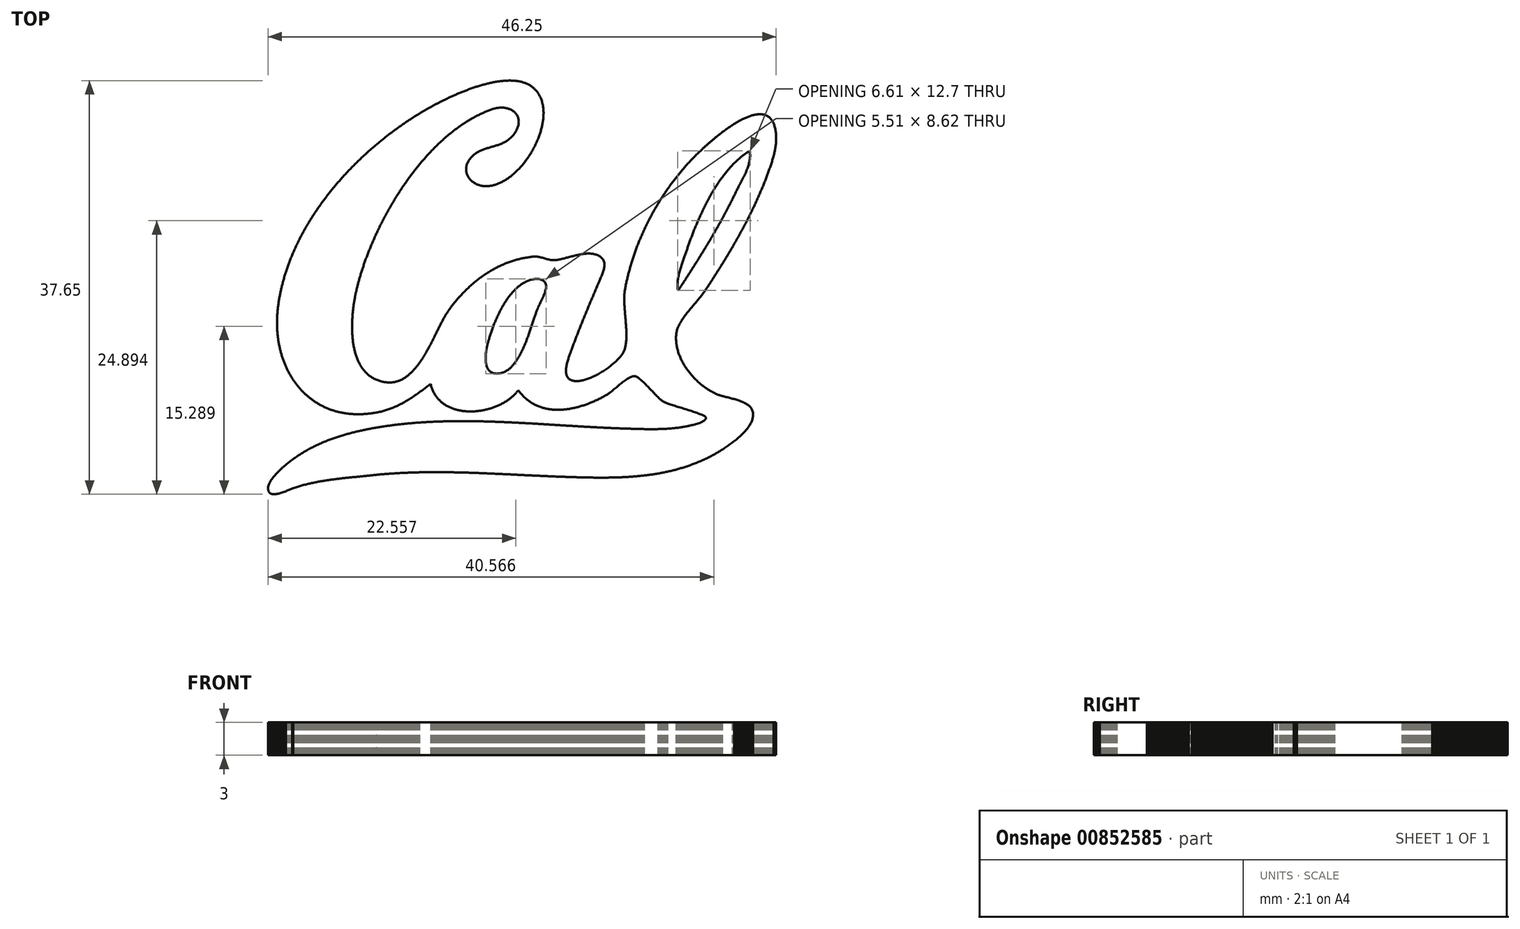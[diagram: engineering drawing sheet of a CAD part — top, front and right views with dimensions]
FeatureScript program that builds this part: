
annotation { "Feature Type Name" : "Feature", "Feature Type Description" : "" }
export const myFeature = defineFeature(function(context is Context, id is Id, definition is map)
    precondition{}
    {
        {
            var Q0;
            Q0=qCreatedBy(makeId("Top.planeOp"),FACE);
            var sketch = newSketch(context, id + "F0", { "sketchPlane" : qUnion([Q0])});
            skLineSegment(sketch, "E0", {"start": v(-8.47, -6.08) * mm, "end": v(-8.44, -6.17) * mm});
            skLineSegment(sketch, "E1", {"start": v(-8.44, -6.17) * mm, "end": v(-8.42, -6.26) * mm});
            skLineSegment(sketch, "E2", {"start": v(-8.42, -6.26) * mm, "end": v(-8.4, -6.35) * mm});
            skLineSegment(sketch, "E3", {"start": v(-8.4, -6.35) * mm, "end": v(-8.36, -6.43) * mm});
            skLineSegment(sketch, "E4", {"start": v(-8.36, -6.43) * mm, "end": v(-8.33, -6.52) * mm});
            skLineSegment(sketch, "E5", {"start": v(-8.33, -6.52) * mm, "end": v(-8.3, -6.6) * mm});
            skLineSegment(sketch, "E6", {"start": v(-8.3, -6.6) * mm, "end": v(-8.27, -6.68) * mm});
            skLineSegment(sketch, "E7", {"start": v(-8.27, -6.68) * mm, "end": v(-8.23, -6.75) * mm});
            skLineSegment(sketch, "E8", {"start": v(-8.23, -6.75) * mm, "end": v(-8.2, -6.83) * mm});
            skLineSegment(sketch, "E9", {"start": v(-8.2, -6.83) * mm, "end": v(-8.15, -6.9) * mm});
            skLineSegment(sketch, "E10", {"start": v(-8.15, -6.9) * mm, "end": v(-8.11, -6.98) * mm});
            skLineSegment(sketch, "E11", {"start": v(-8.11, -6.98) * mm, "end": v(-8.07, -7.05) * mm});
            skLineSegment(sketch, "E12", {"start": v(-8.07, -7.05) * mm, "end": v(-8.03, -7.12) * mm});
            skLineSegment(sketch, "E13", {"start": v(-8.03, -7.12) * mm, "end": v(-7.98, -7.18) * mm});
            skLineSegment(sketch, "E14", {"start": v(-7.98, -7.18) * mm, "end": v(-7.93, -7.25) * mm});
            skLineSegment(sketch, "E15", {"start": v(-7.93, -7.25) * mm, "end": v(-7.88, -7.31) * mm});
            skLineSegment(sketch, "E16", {"start": v(-7.88, -7.31) * mm, "end": v(-7.83, -7.37) * mm});
            skLineSegment(sketch, "E17", {"start": v(-7.83, -7.37) * mm, "end": v(-7.78, -7.44) * mm});
            skLineSegment(sketch, "E18", {"start": v(-7.78, -7.44) * mm, "end": v(-7.73, -7.5) * mm});
            skLineSegment(sketch, "E19", {"start": v(-7.73, -7.5) * mm, "end": v(-7.67, -7.55) * mm});
            skLineSegment(sketch, "E20", {"start": v(-7.67, -7.55) * mm, "end": v(-7.62, -7.6) * mm});
            skLineSegment(sketch, "E21", {"start": v(-7.62, -7.6) * mm, "end": v(-7.56, -7.66) * mm});
            skLineSegment(sketch, "E22", {"start": v(-7.56, -7.66) * mm, "end": v(-7.5, -7.71) * mm});
            skLineSegment(sketch, "E23", {"start": v(-7.5, -7.71) * mm, "end": v(-7.44, -7.76) * mm});
            skLineSegment(sketch, "E24", {"start": v(-7.44, -7.76) * mm, "end": v(-7.38, -7.81) * mm});
            skLineSegment(sketch, "E25", {"start": v(-7.38, -7.81) * mm, "end": v(-7.32, -7.86) * mm});
            skLineSegment(sketch, "E26", {"start": v(-7.32, -7.86) * mm, "end": v(-7.25, -7.9) * mm});
            skLineSegment(sketch, "E27", {"start": v(-7.25, -7.9) * mm, "end": v(-7.19, -7.95) * mm});
            skLineSegment(sketch, "E28", {"start": v(-7.19, -7.95) * mm, "end": v(-7.12, -8) * mm});
            skLineSegment(sketch, "E29", {"start": v(-7.12, -8) * mm, "end": v(-7.06, -8.03) * mm});
            skLineSegment(sketch, "E30", {"start": v(-7.06, -8.03) * mm, "end": v(-6.99, -8.07) * mm});
            skLineSegment(sketch, "E31", {"start": v(-6.99, -8.07) * mm, "end": v(-6.92, -8.11) * mm});
            skLineSegment(sketch, "E32", {"start": v(-6.92, -8.11) * mm, "end": v(-6.85, -8.15) * mm});
            skLineSegment(sketch, "E33", {"start": v(-6.85, -8.15) * mm, "end": v(-6.78, -8.18) * mm});
            skLineSegment(sketch, "E34", {"start": v(-6.78, -8.18) * mm, "end": v(-6.7, -8.22) * mm});
            skLineSegment(sketch, "E35", {"start": v(-6.7, -8.22) * mm, "end": v(-6.63, -8.25) * mm});
            skLineSegment(sketch, "E36", {"start": v(-6.63, -8.25) * mm, "end": v(-6.56, -8.28) * mm});
            skLineSegment(sketch, "E37", {"start": v(-6.56, -8.28) * mm, "end": v(-6.48, -8.3) * mm});
            skLineSegment(sketch, "E38", {"start": v(-6.48, -8.3) * mm, "end": v(-6.4, -8.33) * mm});
            skLineSegment(sketch, "E39", {"start": v(-6.4, -8.33) * mm, "end": v(-6.33, -8.36) * mm});
            skLineSegment(sketch, "E40", {"start": v(-6.33, -8.36) * mm, "end": v(-6.25, -8.38) * mm});
            skLineSegment(sketch, "E41", {"start": v(-6.25, -8.38) * mm, "end": v(-6.17, -8.4) * mm});
            skLineSegment(sketch, "E42", {"start": v(-6.17, -8.4) * mm, "end": v(-6.1, -8.43) * mm});
            skLineSegment(sketch, "E43", {"start": v(-6.1, -8.43) * mm, "end": v(-6.02, -8.45) * mm});
            skLineSegment(sketch, "E44", {"start": v(-6.02, -8.45) * mm, "end": v(-5.94, -8.47) * mm});
            skLineSegment(sketch, "E45", {"start": v(-5.94, -8.47) * mm, "end": v(-5.85, -8.48) * mm});
            skLineSegment(sketch, "E46", {"start": v(-5.85, -8.48) * mm, "end": v(-5.77, -8.5) * mm});
            skLineSegment(sketch, "E47", {"start": v(-5.77, -8.5) * mm, "end": v(-5.7, -8.51) * mm});
            skLineSegment(sketch, "E48", {"start": v(-5.7, -8.51) * mm, "end": v(-5.6, -8.53) * mm});
            skLineSegment(sketch, "E49", {"start": v(-5.6, -8.53) * mm, "end": v(-5.53, -8.54) * mm});
            skLineSegment(sketch, "E50", {"start": v(-5.53, -8.54) * mm, "end": v(-5.44, -8.55) * mm});
            skLineSegment(sketch, "E51", {"start": v(-5.44, -8.55) * mm, "end": v(-5.36, -8.56) * mm});
            skLineSegment(sketch, "E52", {"start": v(-5.36, -8.56) * mm, "end": v(-5.27, -8.57) * mm});
            skLineSegment(sketch, "E53", {"start": v(-5.27, -8.57) * mm, "end": v(-5.2, -8.57) * mm});
            skLineSegment(sketch, "E54", {"start": v(-5.2, -8.57) * mm, "end": v(-5.1, -8.58) * mm});
            skLineSegment(sketch, "E55", {"start": v(-5.1, -8.58) * mm, "end": v(-5.02, -8.58) * mm});
            skLineSegment(sketch, "E56", {"start": v(-5.02, -8.58) * mm, "end": v(-4.93, -8.58) * mm});
            skLineSegment(sketch, "E57", {"start": v(-4.93, -8.58) * mm, "end": v(-4.85, -8.58) * mm});
            skLineSegment(sketch, "E58", {"start": v(-4.85, -8.58) * mm, "end": v(-4.76, -8.58) * mm});
            skLineSegment(sketch, "E59", {"start": v(-4.76, -8.58) * mm, "end": v(-4.68, -8.58) * mm});
            skLineSegment(sketch, "E60", {"start": v(-4.68, -8.58) * mm, "end": v(-4.6, -8.58) * mm});
            skLineSegment(sketch, "E61", {"start": v(-4.6, -8.58) * mm, "end": v(-4.5, -8.57) * mm});
            skLineSegment(sketch, "E62", {"start": v(-4.5, -8.57) * mm, "end": v(-4.42, -8.57) * mm});
            skLineSegment(sketch, "E63", {"start": v(-4.42, -8.57) * mm, "end": v(-4.33, -8.56) * mm});
            skLineSegment(sketch, "E64", {"start": v(-4.33, -8.56) * mm, "end": v(-4.25, -8.55) * mm});
            skLineSegment(sketch, "E65", {"start": v(-4.25, -8.55) * mm, "end": v(-4.16, -8.54) * mm});
            skLineSegment(sketch, "E66", {"start": v(-4.16, -8.54) * mm, "end": v(-4.07, -8.53) * mm});
            skLineSegment(sketch, "E67", {"start": v(-4.07, -8.53) * mm, "end": v(-3.99, -8.52) * mm});
            skLineSegment(sketch, "E68", {"start": v(-3.99, -8.52) * mm, "end": v(-3.9, -8.5) * mm});
            skLineSegment(sketch, "E69", {"start": v(-3.9, -8.5) * mm, "end": v(-3.81, -8.5) * mm});
            skLineSegment(sketch, "E70", {"start": v(-3.81, -8.5) * mm, "end": v(-3.73, -8.48) * mm});
            skLineSegment(sketch, "E71", {"start": v(-3.73, -8.48) * mm, "end": v(-3.64, -8.46) * mm});
            skLineSegment(sketch, "E72", {"start": v(-3.64, -8.46) * mm, "end": v(-3.56, -8.45) * mm});
            skLineSegment(sketch, "E73", {"start": v(-3.56, -8.45) * mm, "end": v(-3.47, -8.43) * mm});
            skLineSegment(sketch, "E74", {"start": v(-3.47, -8.43) * mm, "end": v(-3.39, -8.4) * mm});
            skLineSegment(sketch, "E75", {"start": v(-3.39, -8.4) * mm, "end": v(-3.3, -8.39) * mm});
            skLineSegment(sketch, "E76", {"start": v(-3.3, -8.39) * mm, "end": v(-3.22, -8.36) * mm});
            skLineSegment(sketch, "E77", {"start": v(-3.22, -8.36) * mm, "end": v(-3.13, -8.34) * mm});
            skLineSegment(sketch, "E78", {"start": v(-3.13, -8.34) * mm, "end": v(-3.05, -8.32) * mm});
            skLineSegment(sketch, "E79", {"start": v(-3.05, -8.32) * mm, "end": v(-2.97, -8.3) * mm});
            skLineSegment(sketch, "E80", {"start": v(-2.97, -8.3) * mm, "end": v(-2.88, -8.26) * mm});
            skLineSegment(sketch, "E81", {"start": v(-2.88, -8.26) * mm, "end": v(-2.8, -8.24) * mm});
            skLineSegment(sketch, "E82", {"start": v(-2.8, -8.24) * mm, "end": v(-2.72, -8.2) * mm});
            skLineSegment(sketch, "E83", {"start": v(-2.72, -8.2) * mm, "end": v(-2.64, -8.18) * mm});
            skLineSegment(sketch, "E84", {"start": v(-2.64, -8.18) * mm, "end": v(-2.56, -8.15) * mm});
            skLineSegment(sketch, "E85", {"start": v(-2.56, -8.15) * mm, "end": v(-2.48, -8.11) * mm});
            skLineSegment(sketch, "E86", {"start": v(-2.48, -8.11) * mm, "end": v(-2.4, -8.08) * mm});
            skLineSegment(sketch, "E87", {"start": v(-2.4, -8.08) * mm, "end": v(-2.32, -8.05) * mm});
            skLineSegment(sketch, "E88", {"start": v(-2.32, -8.05) * mm, "end": v(-2.24, -8.01) * mm});
            skLineSegment(sketch, "E89", {"start": v(-2.24, -8.01) * mm, "end": v(-2.17, -7.98) * mm});
            skLineSegment(sketch, "E90", {"start": v(-2.17, -7.98) * mm, "end": v(-2.09, -7.94) * mm});
            skLineSegment(sketch, "E91", {"start": v(-2.09, -7.94) * mm, "end": v(-2.01, -7.9) * mm});
            skLineSegment(sketch, "E92", {"start": v(-2.01, -7.9) * mm, "end": v(-1.94, -7.86) * mm});
            skLineSegment(sketch, "E93", {"start": v(-1.94, -7.86) * mm, "end": v(-1.87, -7.82) * mm});
            skLineSegment(sketch, "E94", {"start": v(-1.87, -7.82) * mm, "end": v(-1.8, -7.78) * mm});
            skLineSegment(sketch, "E95", {"start": v(-1.8, -7.78) * mm, "end": v(-1.72, -7.74) * mm});
            skLineSegment(sketch, "E96", {"start": v(-1.72, -7.74) * mm, "end": v(-1.65, -7.7) * mm});
            skLineSegment(sketch, "E97", {"start": v(-1.65, -7.7) * mm, "end": v(-1.58, -7.65) * mm});
            skLineSegment(sketch, "E98", {"start": v(-1.58, -7.65) * mm, "end": v(-1.51, -7.6) * mm});
            skLineSegment(sketch, "E99", {"start": v(-1.51, -7.6) * mm, "end": v(-1.44, -7.56) * mm});
            skLineSegment(sketch, "E100", {"start": v(-1.44, -7.56) * mm, "end": v(-1.38, -7.51) * mm});
            skLineSegment(sketch, "E101", {"start": v(-1.38, -7.51) * mm, "end": v(-1.31, -7.46) * mm});
            skLineSegment(sketch, "E102", {"start": v(-1.31, -7.46) * mm, "end": v(-1.25, -7.42) * mm});
            skLineSegment(sketch, "E103", {"start": v(-1.25, -7.42) * mm, "end": v(-1.18, -7.37) * mm});
            skLineSegment(sketch, "E104", {"start": v(-1.18, -7.37) * mm, "end": v(-1.12, -7.32) * mm});
            skLineSegment(sketch, "E105", {"start": v(-1.12, -7.32) * mm, "end": v(-1.06, -7.27) * mm});
            skLineSegment(sketch, "E106", {"start": v(-1.06, -7.27) * mm, "end": v(-1, -7.21) * mm});
            skLineSegment(sketch, "E107", {"start": v(-1, -7.21) * mm, "end": v(-0.94, -7.16) * mm});
            skLineSegment(sketch, "E108", {"start": v(-0.94, -7.16) * mm, "end": v(-0.89, -7.1) * mm});
            skLineSegment(sketch, "E109", {"start": v(-0.89, -7.1) * mm, "end": v(-0.83, -7.05) * mm});
            skLineSegment(sketch, "E110", {"start": v(-0.83, -7.05) * mm, "end": v(-0.78, -7) * mm});
            skLineSegment(sketch, "E111", {"start": v(-0.78, -7) * mm, "end": v(-0.72, -6.94) * mm});
            skLineSegment(sketch, "E112", {"start": v(-0.72, -6.94) * mm, "end": v(-0.67, -6.88) * mm});
            skLineSegment(sketch, "E113", {"start": v(-0.67, -6.88) * mm, "end": v(-0.62, -6.82) * mm});
            skLineSegment(sketch, "E114", {"start": v(-0.62, -6.82) * mm, "end": v(-0.57, -6.77) * mm});
            skLineSegment(sketch, "E115", {"start": v(-0.57, -6.77) * mm, "end": v(-0.53, -6.7) * mm});
            skLineSegment(sketch, "E116", {"start": v(-0.53, -6.7) * mm, "end": v(-0.48, -6.65) * mm});
            skLineSegment(sketch, "E117", {"start": v(-0.48, -6.65) * mm, "end": v(-0.42, -6.73) * mm});
            skLineSegment(sketch, "E118", {"start": v(-0.42, -6.73) * mm, "end": v(-0.36, -6.8) * mm});
            skLineSegment(sketch, "E119", {"start": v(-0.36, -6.8) * mm, "end": v(-0.3, -6.89) * mm});
            skLineSegment(sketch, "E120", {"start": v(-0.3, -6.89) * mm, "end": v(-0.23, -6.96) * mm});
            skLineSegment(sketch, "E121", {"start": v(-0.23, -6.96) * mm, "end": v(-0.17, -7.04) * mm});
            skLineSegment(sketch, "E122", {"start": v(-0.17, -7.04) * mm, "end": v(-0.1, -7.1) * mm});
            skLineSegment(sketch, "E123", {"start": v(-0.1, -7.1) * mm, "end": v(-0.04, -7.18) * mm});
            skLineSegment(sketch, "E124", {"start": v(-0.04, -7.18) * mm, "end": v(0.03, -7.24) * mm});
            skLineSegment(sketch, "E125", {"start": v(0.03, -7.24) * mm, "end": v(0.1, -7.3) * mm});
            skLineSegment(sketch, "E126", {"start": v(0.1, -7.3) * mm, "end": v(0.16, -7.37) * mm});
            skLineSegment(sketch, "E127", {"start": v(0.16, -7.37) * mm, "end": v(0.23, -7.43) * mm});
            skLineSegment(sketch, "E128", {"start": v(0.23, -7.43) * mm, "end": v(0.3, -7.5) * mm});
            skLineSegment(sketch, "E129", {"start": v(0.3, -7.5) * mm, "end": v(0.37, -7.55) * mm});
            skLineSegment(sketch, "E130", {"start": v(0.37, -7.55) * mm, "end": v(0.45, -7.6) * mm});
            skLineSegment(sketch, "E131", {"start": v(0.45, -7.6) * mm, "end": v(0.52, -7.66) * mm});
            skLineSegment(sketch, "E132", {"start": v(0.52, -7.66) * mm, "end": v(0.6, -7.7) * mm});
            skLineSegment(sketch, "E133", {"start": v(0.6, -7.7) * mm, "end": v(0.67, -7.76) * mm});
            skLineSegment(sketch, "E134", {"start": v(0.67, -7.76) * mm, "end": v(0.74, -7.8) * mm});
            skLineSegment(sketch, "E135", {"start": v(0.74, -7.8) * mm, "end": v(0.82, -7.85) * mm});
            skLineSegment(sketch, "E136", {"start": v(0.82, -7.85) * mm, "end": v(0.9, -7.9) * mm});
            skLineSegment(sketch, "E137", {"start": v(0.9, -7.9) * mm, "end": v(0.97, -7.94) * mm});
            skLineSegment(sketch, "E138", {"start": v(0.97, -7.94) * mm, "end": v(1.05, -7.98) * mm});
            skLineSegment(sketch, "E139", {"start": v(1.05, -7.98) * mm, "end": v(1.13, -8.02) * mm});
            skLineSegment(sketch, "E140", {"start": v(1.13, -8.02) * mm, "end": v(1.2, -8.05) * mm});
            skLineSegment(sketch, "E141", {"start": v(1.2, -8.05) * mm, "end": v(1.29, -8.09) * mm});
            skLineSegment(sketch, "E142", {"start": v(1.29, -8.09) * mm, "end": v(1.37, -8.12) * mm});
            skLineSegment(sketch, "E143", {"start": v(1.37, -8.12) * mm, "end": v(1.45, -8.15) * mm});
            skLineSegment(sketch, "E144", {"start": v(1.45, -8.15) * mm, "end": v(1.53, -8.18) * mm});
            skLineSegment(sketch, "E145", {"start": v(1.53, -8.18) * mm, "end": v(1.61, -8.2) * mm});
            skLineSegment(sketch, "E146", {"start": v(1.61, -8.2) * mm, "end": v(1.7, -8.23) * mm});
            skLineSegment(sketch, "E147", {"start": v(1.7, -8.23) * mm, "end": v(1.78, -8.26) * mm});
            skLineSegment(sketch, "E148", {"start": v(1.78, -8.26) * mm, "end": v(1.86, -8.28) * mm});
            skLineSegment(sketch, "E149", {"start": v(1.86, -8.28) * mm, "end": v(1.95, -8.3) * mm});
            skLineSegment(sketch, "E150", {"start": v(1.95, -8.3) * mm, "end": v(2.03, -8.32) * mm});
            skLineSegment(sketch, "E151", {"start": v(2.03, -8.32) * mm, "end": v(2.12, -8.34) * mm});
            skLineSegment(sketch, "E152", {"start": v(2.12, -8.34) * mm, "end": v(2.2, -8.36) * mm});
            skLineSegment(sketch, "E153", {"start": v(2.2, -8.36) * mm, "end": v(2.29, -8.37) * mm});
            skLineSegment(sketch, "E154", {"start": v(2.29, -8.37) * mm, "end": v(2.37, -8.38) * mm});
            skLineSegment(sketch, "E155", {"start": v(2.37, -8.38) * mm, "end": v(2.46, -8.4) * mm});
            skLineSegment(sketch, "E156", {"start": v(2.46, -8.4) * mm, "end": v(2.55, -8.4) * mm});
            skLineSegment(sketch, "E157", {"start": v(2.55, -8.4) * mm, "end": v(2.64, -8.41) * mm});
            skLineSegment(sketch, "E158", {"start": v(2.64, -8.41) * mm, "end": v(2.72, -8.42) * mm});
            skLineSegment(sketch, "E159", {"start": v(2.72, -8.42) * mm, "end": v(2.81, -8.43) * mm});
            skLineSegment(sketch, "E160", {"start": v(2.81, -8.43) * mm, "end": v(2.9, -8.43) * mm});
            skLineSegment(sketch, "E161", {"start": v(2.9, -8.43) * mm, "end": v(3, -8.43) * mm});
            skLineSegment(sketch, "E162", {"start": v(3, -8.43) * mm, "end": v(3.08, -8.43) * mm});
            skLineSegment(sketch, "E163", {"start": v(3.08, -8.43) * mm, "end": v(3.17, -8.43) * mm});
            skLineSegment(sketch, "E164", {"start": v(3.17, -8.43) * mm, "end": v(3.26, -8.43) * mm});
            skLineSegment(sketch, "E165", {"start": v(3.26, -8.43) * mm, "end": v(3.35, -8.43) * mm});
            skLineSegment(sketch, "E166", {"start": v(3.35, -8.43) * mm, "end": v(3.44, -8.43) * mm});
            skLineSegment(sketch, "E167", {"start": v(3.44, -8.43) * mm, "end": v(3.53, -8.42) * mm});
            skLineSegment(sketch, "E168", {"start": v(3.53, -8.42) * mm, "end": v(3.62, -8.41) * mm});
            skLineSegment(sketch, "E169", {"start": v(3.62, -8.41) * mm, "end": v(3.71, -8.4) * mm});
            skLineSegment(sketch, "E170", {"start": v(3.71, -8.4) * mm, "end": v(3.8, -8.4) * mm});
            skLineSegment(sketch, "E171", {"start": v(3.8, -8.4) * mm, "end": v(3.9, -8.39) * mm});
            skLineSegment(sketch, "E172", {"start": v(3.9, -8.39) * mm, "end": v(3.98, -8.37) * mm});
            skLineSegment(sketch, "E173", {"start": v(3.98, -8.37) * mm, "end": v(4.07, -8.36) * mm});
            skLineSegment(sketch, "E174", {"start": v(4.07, -8.36) * mm, "end": v(4.17, -8.35) * mm});
            skLineSegment(sketch, "E175", {"start": v(4.17, -8.35) * mm, "end": v(4.26, -8.33) * mm});
            skLineSegment(sketch, "E176", {"start": v(4.26, -8.33) * mm, "end": v(4.35, -8.31) * mm});
            skLineSegment(sketch, "E177", {"start": v(4.35, -8.31) * mm, "end": v(4.44, -8.3) * mm});
            skLineSegment(sketch, "E178", {"start": v(4.44, -8.3) * mm, "end": v(4.53, -8.28) * mm});
            skLineSegment(sketch, "E179", {"start": v(4.53, -8.28) * mm, "end": v(4.62, -8.26) * mm});
            skLineSegment(sketch, "E180", {"start": v(4.62, -8.26) * mm, "end": v(4.71, -8.24) * mm});
            skLineSegment(sketch, "E181", {"start": v(4.71, -8.24) * mm, "end": v(4.8, -8.21) * mm});
            skLineSegment(sketch, "E182", {"start": v(4.8, -8.21) * mm, "end": v(4.9, -8.2) * mm});
            skLineSegment(sketch, "E183", {"start": v(4.9, -8.2) * mm, "end": v(4.99, -8.17) * mm});
            skLineSegment(sketch, "E184", {"start": v(4.99, -8.17) * mm, "end": v(5.08, -8.14) * mm});
            skLineSegment(sketch, "E185", {"start": v(5.08, -8.14) * mm, "end": v(5.17, -8.12) * mm});
            skLineSegment(sketch, "E186", {"start": v(5.17, -8.12) * mm, "end": v(5.26, -8.09) * mm});
            skLineSegment(sketch, "E187", {"start": v(5.26, -8.09) * mm, "end": v(5.35, -8.06) * mm});
            skLineSegment(sketch, "E188", {"start": v(5.35, -8.06) * mm, "end": v(5.44, -8.03) * mm});
            skLineSegment(sketch, "E189", {"start": v(5.44, -8.03) * mm, "end": v(5.53, -8) * mm});
            skLineSegment(sketch, "E190", {"start": v(5.53, -8) * mm, "end": v(5.62, -7.97) * mm});
            skLineSegment(sketch, "E191", {"start": v(5.62, -7.97) * mm, "end": v(5.71, -7.94) * mm});
            skLineSegment(sketch, "E192", {"start": v(5.71, -7.94) * mm, "end": v(5.8, -7.9) * mm});
            skLineSegment(sketch, "E193", {"start": v(5.8, -7.9) * mm, "end": v(5.9, -7.87) * mm});
            skLineSegment(sketch, "E194", {"start": v(5.9, -7.87) * mm, "end": v(5.98, -7.84) * mm});
            skLineSegment(sketch, "E195", {"start": v(5.98, -7.84) * mm, "end": v(6.07, -7.8) * mm});
            skLineSegment(sketch, "E196", {"start": v(6.07, -7.8) * mm, "end": v(6.16, -7.77) * mm});
            skLineSegment(sketch, "E197", {"start": v(6.16, -7.77) * mm, "end": v(6.25, -7.73) * mm});
            skLineSegment(sketch, "E198", {"start": v(6.25, -7.73) * mm, "end": v(6.33, -7.7) * mm});
            skLineSegment(sketch, "E199", {"start": v(6.33, -7.7) * mm, "end": v(6.42, -7.65) * mm});
            skLineSegment(sketch, "E200", {"start": v(6.42, -7.65) * mm, "end": v(6.5, -7.61) * mm});
            skLineSegment(sketch, "E201", {"start": v(6.5, -7.61) * mm, "end": v(6.6, -7.57) * mm});
            skLineSegment(sketch, "E202", {"start": v(6.6, -7.57) * mm, "end": v(6.68, -7.53) * mm});
            skLineSegment(sketch, "E203", {"start": v(6.68, -7.53) * mm, "end": v(6.77, -7.5) * mm});
            skLineSegment(sketch, "E204", {"start": v(6.77, -7.5) * mm, "end": v(6.85, -7.45) * mm});
            skLineSegment(sketch, "E205", {"start": v(6.85, -7.45) * mm, "end": v(6.94, -7.4) * mm});
            skLineSegment(sketch, "E206", {"start": v(6.94, -7.4) * mm, "end": v(7.02, -7.36) * mm});
            skLineSegment(sketch, "E207", {"start": v(7.02, -7.36) * mm, "end": v(7.1, -7.32) * mm});
            skLineSegment(sketch, "E208", {"start": v(7.1, -7.32) * mm, "end": v(7.2, -7.28) * mm});
            skLineSegment(sketch, "E209", {"start": v(7.2, -7.28) * mm, "end": v(7.27, -7.23) * mm});
            skLineSegment(sketch, "E210", {"start": v(7.27, -7.23) * mm, "end": v(7.36, -7.18) * mm});
            skLineSegment(sketch, "E211", {"start": v(7.36, -7.18) * mm, "end": v(7.44, -7.14) * mm});
            skLineSegment(sketch, "E212", {"start": v(7.44, -7.14) * mm, "end": v(7.52, -7.1) * mm});
            skLineSegment(sketch, "E213", {"start": v(7.52, -7.1) * mm, "end": v(7.6, -7.04) * mm});
            skLineSegment(sketch, "E214", {"start": v(7.6, -7.04) * mm, "end": v(7.66, -7) * mm});
            skLineSegment(sketch, "E215", {"start": v(7.66, -7) * mm, "end": v(7.73, -6.96) * mm});
            skLineSegment(sketch, "E216", {"start": v(7.73, -6.96) * mm, "end": v(7.8, -6.91) * mm});
            skLineSegment(sketch, "E217", {"start": v(7.8, -6.91) * mm, "end": v(7.87, -6.86) * mm});
            skLineSegment(sketch, "E218", {"start": v(7.87, -6.86) * mm, "end": v(7.95, -6.8) * mm});
            skLineSegment(sketch, "E219", {"start": v(7.95, -6.8) * mm, "end": v(8.03, -6.73) * mm});
            skLineSegment(sketch, "E220", {"start": v(8.03, -6.73) * mm, "end": v(8.1, -6.67) * mm});
            skLineSegment(sketch, "E221", {"start": v(8.1, -6.67) * mm, "end": v(8.2, -6.6) * mm});
            skLineSegment(sketch, "E222", {"start": v(8.2, -6.6) * mm, "end": v(8.28, -6.53) * mm});
            skLineSegment(sketch, "E223", {"start": v(8.28, -6.53) * mm, "end": v(8.37, -6.45) * mm});
            skLineSegment(sketch, "E224", {"start": v(8.37, -6.45) * mm, "end": v(8.46, -6.38) * mm});
            skLineSegment(sketch, "E225", {"start": v(8.46, -6.38) * mm, "end": v(8.55, -6.3) * mm});
            skLineSegment(sketch, "E226", {"start": v(8.55, -6.3) * mm, "end": v(8.64, -6.23) * mm});
            skLineSegment(sketch, "E227", {"start": v(8.64, -6.23) * mm, "end": v(8.73, -6.15) * mm});
            skLineSegment(sketch, "E228", {"start": v(8.73, -6.15) * mm, "end": v(8.82, -6.07) * mm});
            skLineSegment(sketch, "E229", {"start": v(8.82, -6.07) * mm, "end": v(8.91, -6) * mm});
            skLineSegment(sketch, "E230", {"start": v(8.91, -6) * mm, "end": v(9, -5.93) * mm});
            skLineSegment(sketch, "E231", {"start": v(9, -5.93) * mm, "end": v(9.1, -5.86) * mm});
            skLineSegment(sketch, "E232", {"start": v(9.1, -5.86) * mm, "end": v(9.2, -5.79) * mm});
            skLineSegment(sketch, "E233", {"start": v(9.2, -5.79) * mm, "end": v(9.28, -5.72) * mm});
            skLineSegment(sketch, "E234", {"start": v(9.28, -5.72) * mm, "end": v(9.37, -5.66) * mm});
            skLineSegment(sketch, "E235", {"start": v(9.37, -5.66) * mm, "end": v(9.46, -5.6) * mm});
            skLineSegment(sketch, "E236", {"start": v(9.46, -5.6) * mm, "end": v(9.55, -5.56) * mm});
            skLineSegment(sketch, "E237", {"start": v(9.55, -5.56) * mm, "end": v(9.63, -5.5) * mm});
            skLineSegment(sketch, "E238", {"start": v(9.63, -5.5) * mm, "end": v(9.71, -5.47) * mm});
            skLineSegment(sketch, "E239", {"start": v(9.71, -5.47) * mm, "end": v(9.8, -5.43) * mm});
            skLineSegment(sketch, "E240", {"start": v(9.8, -5.43) * mm, "end": v(9.87, -5.4) * mm});
            skLineSegment(sketch, "E241", {"start": v(9.87, -5.4) * mm, "end": v(9.95, -5.39) * mm});
            skLineSegment(sketch, "E242", {"start": v(9.95, -5.39) * mm, "end": v(10.02, -5.37) * mm});
            skLineSegment(sketch, "E243", {"start": v(10.02, -5.37) * mm, "end": v(10.08, -5.37) * mm});
            skLineSegment(sketch, "E244", {"start": v(10.08, -5.37) * mm, "end": v(10.13, -5.37) * mm});
            skLineSegment(sketch, "E245", {"start": v(10.13, -5.37) * mm, "end": v(10.18, -5.39) * mm});
            skLineSegment(sketch, "E246", {"start": v(10.18, -5.39) * mm, "end": v(10.24, -5.4) * mm});
            skLineSegment(sketch, "E247", {"start": v(10.24, -5.4) * mm, "end": v(10.3, -5.44) * mm});
            skLineSegment(sketch, "E248", {"start": v(10.3, -5.44) * mm, "end": v(10.36, -5.47) * mm});
            skLineSegment(sketch, "E249", {"start": v(10.36, -5.47) * mm, "end": v(10.43, -5.52) * mm});
            skLineSegment(sketch, "E250", {"start": v(10.43, -5.52) * mm, "end": v(10.5, -5.57) * mm});
            skLineSegment(sketch, "E251", {"start": v(10.5, -5.57) * mm, "end": v(10.57, -5.62) * mm});
            skLineSegment(sketch, "E252", {"start": v(10.57, -5.62) * mm, "end": v(10.64, -5.68) * mm});
            skLineSegment(sketch, "E253", {"start": v(10.64, -5.68) * mm, "end": v(10.72, -5.75) * mm});
            skLineSegment(sketch, "E254", {"start": v(10.72, -5.75) * mm, "end": v(10.8, -5.82) * mm});
            skLineSegment(sketch, "E255", {"start": v(10.8, -5.82) * mm, "end": v(10.88, -5.9) * mm});
            skLineSegment(sketch, "E256", {"start": v(10.88, -5.9) * mm, "end": v(10.96, -5.97) * mm});
            skLineSegment(sketch, "E257", {"start": v(10.96, -5.97) * mm, "end": v(11.04, -6.05) * mm});
            skLineSegment(sketch, "E258", {"start": v(11.04, -6.05) * mm, "end": v(11.12, -6.14) * mm});
            skLineSegment(sketch, "E259", {"start": v(11.12, -6.14) * mm, "end": v(11.2, -6.22) * mm});
            skLineSegment(sketch, "E260", {"start": v(11.2, -6.22) * mm, "end": v(11.3, -6.3) * mm});
            skLineSegment(sketch, "E261", {"start": v(11.3, -6.3) * mm, "end": v(11.38, -6.4) * mm});
            skLineSegment(sketch, "E262", {"start": v(11.38, -6.4) * mm, "end": v(11.46, -6.49) * mm});
            skLineSegment(sketch, "E263", {"start": v(11.46, -6.49) * mm, "end": v(11.55, -6.58) * mm});
            skLineSegment(sketch, "E264", {"start": v(11.55, -6.58) * mm, "end": v(11.63, -6.67) * mm});
            skLineSegment(sketch, "E265", {"start": v(11.63, -6.67) * mm, "end": v(11.72, -6.76) * mm});
            skLineSegment(sketch, "E266", {"start": v(11.72, -6.76) * mm, "end": v(11.8, -6.84) * mm});
            skLineSegment(sketch, "E267", {"start": v(11.8, -6.84) * mm, "end": v(11.89, -6.93) * mm});
            skLineSegment(sketch, "E268", {"start": v(11.89, -6.93) * mm, "end": v(11.97, -7.02) * mm});
            skLineSegment(sketch, "E269", {"start": v(11.97, -7.02) * mm, "end": v(12.05, -7.1) * mm});
            skLineSegment(sketch, "E270", {"start": v(12.05, -7.1) * mm, "end": v(12.13, -7.18) * mm});
            skLineSegment(sketch, "E271", {"start": v(12.13, -7.18) * mm, "end": v(12.2, -7.26) * mm});
            skLineSegment(sketch, "E272", {"start": v(12.2, -7.26) * mm, "end": v(12.28, -7.33) * mm});
            skLineSegment(sketch, "E273", {"start": v(12.28, -7.33) * mm, "end": v(12.35, -7.4) * mm});
            skLineSegment(sketch, "E274", {"start": v(12.35, -7.4) * mm, "end": v(12.42, -7.46) * mm});
            skLineSegment(sketch, "E275", {"start": v(12.42, -7.46) * mm, "end": v(12.49, -7.52) * mm});
            skLineSegment(sketch, "E276", {"start": v(12.49, -7.52) * mm, "end": v(12.55, -7.58) * mm});
            skLineSegment(sketch, "E277", {"start": v(12.55, -7.58) * mm, "end": v(12.61, -7.62) * mm});
            skLineSegment(sketch, "E278", {"start": v(12.61, -7.62) * mm, "end": v(12.67, -7.66) * mm});
            skLineSegment(sketch, "E279", {"start": v(12.67, -7.66) * mm, "end": v(12.73, -7.7) * mm});
            skLineSegment(sketch, "E280", {"start": v(12.73, -7.7) * mm, "end": v(12.76, -7.72) * mm});
            skLineSegment(sketch, "E281", {"start": v(12.76, -7.72) * mm, "end": v(12.81, -7.74) * mm});
            skLineSegment(sketch, "E282", {"start": v(12.81, -7.74) * mm, "end": v(12.87, -7.77) * mm});
            skLineSegment(sketch, "E283", {"start": v(12.87, -7.77) * mm, "end": v(12.93, -7.8) * mm});
            skLineSegment(sketch, "E284", {"start": v(12.93, -7.8) * mm, "end": v(13, -7.82) * mm});
            skLineSegment(sketch, "E285", {"start": v(13, -7.82) * mm, "end": v(13.09, -7.85) * mm});
            skLineSegment(sketch, "E286", {"start": v(13.09, -7.85) * mm, "end": v(13.17, -7.88) * mm});
            skLineSegment(sketch, "E287", {"start": v(13.17, -7.88) * mm, "end": v(13.27, -7.91) * mm});
            skLineSegment(sketch, "E288", {"start": v(13.27, -7.91) * mm, "end": v(13.37, -7.94) * mm});
            skLineSegment(sketch, "E289", {"start": v(13.37, -7.94) * mm, "end": v(13.47, -7.98) * mm});
            skLineSegment(sketch, "E290", {"start": v(13.47, -7.98) * mm, "end": v(13.58, -8.01) * mm});
            skLineSegment(sketch, "E291", {"start": v(13.58, -8.01) * mm, "end": v(13.7, -8.05) * mm});
            skLineSegment(sketch, "E292", {"start": v(13.7, -8.05) * mm, "end": v(13.81, -8.09) * mm});
            skLineSegment(sketch, "E293", {"start": v(13.81, -8.09) * mm, "end": v(13.93, -8.12) * mm});
            skLineSegment(sketch, "E294", {"start": v(13.93, -8.12) * mm, "end": v(14.06, -8.16) * mm});
            skLineSegment(sketch, "E295", {"start": v(14.06, -8.16) * mm, "end": v(14.18, -8.2) * mm});
            skLineSegment(sketch, "E296", {"start": v(14.18, -8.2) * mm, "end": v(14.31, -8.24) * mm});
            skLineSegment(sketch, "E297", {"start": v(14.31, -8.24) * mm, "end": v(14.44, -8.28) * mm});
            skLineSegment(sketch, "E298", {"start": v(14.44, -8.28) * mm, "end": v(14.57, -8.32) * mm});
            skLineSegment(sketch, "E299", {"start": v(14.57, -8.32) * mm, "end": v(14.7, -8.36) * mm});
            skLineSegment(sketch, "E300", {"start": v(14.7, -8.36) * mm, "end": v(14.83, -8.4) * mm});
            skLineSegment(sketch, "E301", {"start": v(14.83, -8.4) * mm, "end": v(14.96, -8.45) * mm});
            skLineSegment(sketch, "E302", {"start": v(14.96, -8.45) * mm, "end": v(15.08, -8.49) * mm});
            skLineSegment(sketch, "E303", {"start": v(15.08, -8.49) * mm, "end": v(15.21, -8.53) * mm});
            skLineSegment(sketch, "E304", {"start": v(15.21, -8.53) * mm, "end": v(15.33, -8.57) * mm});
            skLineSegment(sketch, "E305", {"start": v(15.33, -8.57) * mm, "end": v(15.45, -8.6) * mm});
            skLineSegment(sketch, "E306", {"start": v(15.45, -8.6) * mm, "end": v(15.57, -8.65) * mm});
            skLineSegment(sketch, "E307", {"start": v(15.57, -8.65) * mm, "end": v(15.69, -8.69) * mm});
            skLineSegment(sketch, "E308", {"start": v(15.69, -8.69) * mm, "end": v(15.8, -8.73) * mm});
            skLineSegment(sketch, "E309", {"start": v(15.8, -8.73) * mm, "end": v(15.9, -8.77) * mm});
            skLineSegment(sketch, "E310", {"start": v(15.9, -8.77) * mm, "end": v(16, -8.8) * mm});
            skLineSegment(sketch, "E311", {"start": v(16, -8.8) * mm, "end": v(16.1, -8.84) * mm});
            skLineSegment(sketch, "E312", {"start": v(16.1, -8.84) * mm, "end": v(16.18, -8.88) * mm});
            skLineSegment(sketch, "E313", {"start": v(16.18, -8.88) * mm, "end": v(16.26, -8.91) * mm});
            skLineSegment(sketch, "E314", {"start": v(16.26, -8.91) * mm, "end": v(16.33, -8.94) * mm});
            skLineSegment(sketch, "E315", {"start": v(16.33, -8.94) * mm, "end": v(16.4, -8.98) * mm});
            skLineSegment(sketch, "E316", {"start": v(16.4, -8.98) * mm, "end": v(16.45, -9) * mm});
            skLineSegment(sketch, "E317", {"start": v(16.45, -9) * mm, "end": v(16.5, -9.04) * mm});
            skLineSegment(sketch, "E318", {"start": v(16.5, -9.04) * mm, "end": v(16.53, -9.07) * mm});
            skLineSegment(sketch, "E319", {"start": v(16.53, -9.07) * mm, "end": v(16.56, -9.1) * mm});
            skLineSegment(sketch, "E320", {"start": v(16.56, -9.1) * mm, "end": v(16.58, -9.12) * mm});
            skLineSegment(sketch, "E321", {"start": v(16.58, -9.12) * mm, "end": v(16.59, -9.14) * mm});
            skLineSegment(sketch, "E322", {"start": v(16.59, -9.14) * mm, "end": v(16.58, -9.2) * mm});
            skLineSegment(sketch, "E323", {"start": v(16.58, -9.2) * mm, "end": v(16.55, -9.27) * mm});
            skLineSegment(sketch, "E324", {"start": v(16.55, -9.27) * mm, "end": v(16.51, -9.33) * mm});
            skLineSegment(sketch, "E325", {"start": v(16.51, -9.33) * mm, "end": v(16.46, -9.38) * mm});
            skLineSegment(sketch, "E326", {"start": v(16.46, -9.38) * mm, "end": v(16.4, -9.44) * mm});
            skLineSegment(sketch, "E327", {"start": v(16.4, -9.44) * mm, "end": v(16.32, -9.49) * mm});
            skLineSegment(sketch, "E328", {"start": v(16.32, -9.49) * mm, "end": v(16.23, -9.53) * mm});
            skLineSegment(sketch, "E329", {"start": v(16.23, -9.53) * mm, "end": v(16.14, -9.58) * mm});
            skLineSegment(sketch, "E330", {"start": v(16.14, -9.58) * mm, "end": v(16.04, -9.62) * mm});
            skLineSegment(sketch, "E331", {"start": v(16.04, -9.62) * mm, "end": v(15.93, -9.66) * mm});
            skLineSegment(sketch, "E332", {"start": v(15.93, -9.66) * mm, "end": v(15.82, -9.7) * mm});
            skLineSegment(sketch, "E333", {"start": v(15.82, -9.7) * mm, "end": v(15.71, -9.73) * mm});
            skLineSegment(sketch, "E334", {"start": v(15.71, -9.73) * mm, "end": v(15.6, -9.76) * mm});
            skLineSegment(sketch, "E335", {"start": v(15.6, -9.76) * mm, "end": v(15.5, -9.79) * mm});
            skLineSegment(sketch, "E336", {"start": v(15.5, -9.79) * mm, "end": v(15.4, -9.81) * mm});
            skLineSegment(sketch, "E337", {"start": v(15.4, -9.81) * mm, "end": v(15.3, -9.84) * mm});
            skLineSegment(sketch, "E338", {"start": v(15.3, -9.84) * mm, "end": v(15.2, -9.86) * mm});
            skLineSegment(sketch, "E339", {"start": v(15.2, -9.86) * mm, "end": v(15.11, -9.88) * mm});
            skLineSegment(sketch, "E340", {"start": v(15.11, -9.88) * mm, "end": v(15.04, -9.9) * mm});
            skLineSegment(sketch, "E341", {"start": v(15.04, -9.9) * mm, "end": v(14.97, -9.9) * mm});
            skLineSegment(sketch, "E342", {"start": v(14.97, -9.9) * mm, "end": v(14.92, -9.92) * mm});
            skLineSegment(sketch, "E343", {"start": v(14.92, -9.92) * mm, "end": v(14.82, -9.94) * mm});
            skLineSegment(sketch, "E344", {"start": v(14.82, -9.94) * mm, "end": v(14.72, -9.95) * mm});
            skLineSegment(sketch, "E345", {"start": v(14.72, -9.95) * mm, "end": v(14.63, -9.97) * mm});
            skLineSegment(sketch, "E346", {"start": v(14.63, -9.97) * mm, "end": v(14.53, -10) * mm});
            skLineSegment(sketch, "E347", {"start": v(14.53, -10) * mm, "end": v(14.43, -10) * mm});
            skLineSegment(sketch, "E348", {"start": v(14.43, -10) * mm, "end": v(14.33, -10.02) * mm});
            skLineSegment(sketch, "E349", {"start": v(14.33, -10.02) * mm, "end": v(14.23, -10.04) * mm});
            skLineSegment(sketch, "E350", {"start": v(14.23, -10.04) * mm, "end": v(14.14, -10.05) * mm});
            skLineSegment(sketch, "E351", {"start": v(14.14, -10.05) * mm, "end": v(14.04, -10.06) * mm});
            skLineSegment(sketch, "E352", {"start": v(14.04, -10.06) * mm, "end": v(13.93, -10.08) * mm});
            skLineSegment(sketch, "E353", {"start": v(13.93, -10.08) * mm, "end": v(13.83, -10.09) * mm});
            skLineSegment(sketch, "E354", {"start": v(13.83, -10.09) * mm, "end": v(13.73, -10.1) * mm});
            skLineSegment(sketch, "E355", {"start": v(13.73, -10.1) * mm, "end": v(13.63, -10.1) * mm});
            skLineSegment(sketch, "E356", {"start": v(13.63, -10.1) * mm, "end": v(13.53, -10.12) * mm});
            skLineSegment(sketch, "E357", {"start": v(13.53, -10.12) * mm, "end": v(13.43, -10.13) * mm});
            skLineSegment(sketch, "E358", {"start": v(13.43, -10.13) * mm, "end": v(13.32, -10.14) * mm});
            skLineSegment(sketch, "E359", {"start": v(13.32, -10.14) * mm, "end": v(13.22, -10.14) * mm});
            skLineSegment(sketch, "E360", {"start": v(13.22, -10.14) * mm, "end": v(13.12, -10.15) * mm});
            skLineSegment(sketch, "E361", {"start": v(13.12, -10.15) * mm, "end": v(13.01, -10.16) * mm});
            skLineSegment(sketch, "E362", {"start": v(13.01, -10.16) * mm, "end": v(12.9, -10.16) * mm});
            skLineSegment(sketch, "E363", {"start": v(12.9, -10.16) * mm, "end": v(12.8, -10.17) * mm});
            skLineSegment(sketch, "E364", {"start": v(12.8, -10.17) * mm, "end": v(12.7, -10.17) * mm});
            skLineSegment(sketch, "E365", {"start": v(12.7, -10.17) * mm, "end": v(12.6, -10.18) * mm});
            skLineSegment(sketch, "E366", {"start": v(12.6, -10.18) * mm, "end": v(12.5, -10.18) * mm});
            skLineSegment(sketch, "E367", {"start": v(12.5, -10.18) * mm, "end": v(12.39, -10.18) * mm});
            skLineSegment(sketch, "E368", {"start": v(12.39, -10.18) * mm, "end": v(12.28, -10.19) * mm});
            skLineSegment(sketch, "E369", {"start": v(12.28, -10.19) * mm, "end": v(12.18, -10.19) * mm});
            skLineSegment(sketch, "E370", {"start": v(12.18, -10.19) * mm, "end": v(12.07, -10.2) * mm});
            skLineSegment(sketch, "E371", {"start": v(12.07, -10.2) * mm, "end": v(11.97, -10.2) * mm});
            skLineSegment(sketch, "E372", {"start": v(11.97, -10.2) * mm, "end": v(11.86, -10.2) * mm});
            skLineSegment(sketch, "E373", {"start": v(11.86, -10.2) * mm, "end": v(11.76, -10.2) * mm});
            skLineSegment(sketch, "E374", {"start": v(11.76, -10.2) * mm, "end": v(11.65, -10.2) * mm});
            skLineSegment(sketch, "E375", {"start": v(11.65, -10.2) * mm, "end": v(11.55, -10.2) * mm});
            skLineSegment(sketch, "E376", {"start": v(11.55, -10.2) * mm, "end": v(11.44, -10.2) * mm});
            skLineSegment(sketch, "E377", {"start": v(11.44, -10.2) * mm, "end": v(11.33, -10.2) * mm});
            skLineSegment(sketch, "E378", {"start": v(11.33, -10.2) * mm, "end": v(11.23, -10.2) * mm});
            skLineSegment(sketch, "E379", {"start": v(11.23, -10.2) * mm, "end": v(11.13, -10.2) * mm});
            skLineSegment(sketch, "E380", {"start": v(11.13, -10.2) * mm, "end": v(11.02, -10.19) * mm});
            skLineSegment(sketch, "E381", {"start": v(11.02, -10.19) * mm, "end": v(10.92, -10.19) * mm});
            skLineSegment(sketch, "E382", {"start": v(10.92, -10.19) * mm, "end": v(10.81, -10.19) * mm});
            skLineSegment(sketch, "E383", {"start": v(10.81, -10.19) * mm, "end": v(10.7, -10.18) * mm});
            skLineSegment(sketch, "E384", {"start": v(10.7, -10.18) * mm, "end": v(10.6, -10.18) * mm});
            skLineSegment(sketch, "E385", {"start": v(10.6, -10.18) * mm, "end": v(10.5, -10.18) * mm});
            skLineSegment(sketch, "E386", {"start": v(10.5, -10.18) * mm, "end": v(10.4, -10.18) * mm});
            skLineSegment(sketch, "E387", {"start": v(10.4, -10.18) * mm, "end": v(10.3, -10.17) * mm});
            skLineSegment(sketch, "E388", {"start": v(10.3, -10.17) * mm, "end": v(10.2, -10.17) * mm});
            skLineSegment(sketch, "E389", {"start": v(10.2, -10.17) * mm, "end": v(10.09, -10.17) * mm});
            skLineSegment(sketch, "E390", {"start": v(10.09, -10.17) * mm, "end": v(9.99, -10.16) * mm});
            skLineSegment(sketch, "E391", {"start": v(9.99, -10.16) * mm, "end": v(9.89, -10.16) * mm});
            skLineSegment(sketch, "E392", {"start": v(9.89, -10.16) * mm, "end": v(9.79, -10.16) * mm});
            skLineSegment(sketch, "E393", {"start": v(9.79, -10.16) * mm, "end": v(9.69, -10.15) * mm});
            skLineSegment(sketch, "E394", {"start": v(9.69, -10.15) * mm, "end": v(9.59, -10.15) * mm});
            skLineSegment(sketch, "E395", {"start": v(9.59, -10.15) * mm, "end": v(9.49, -10.15) * mm});
            skLineSegment(sketch, "E396", {"start": v(9.49, -10.15) * mm, "end": v(9.39, -10.14) * mm});
            skLineSegment(sketch, "E397", {"start": v(9.39, -10.14) * mm, "end": v(9.29, -10.14) * mm});
            skLineSegment(sketch, "E398", {"start": v(9.29, -10.14) * mm, "end": v(9.2, -10.14) * mm});
            skLineSegment(sketch, "E399", {"start": v(9.2, -10.14) * mm, "end": v(9.1, -10.13) * mm});
            skLineSegment(sketch, "E400", {"start": v(9.1, -10.13) * mm, "end": v(9, -10.13) * mm});
            skLineSegment(sketch, "E401", {"start": v(9, -10.13) * mm, "end": v(8.9, -10.13) * mm});
            skLineSegment(sketch, "E402", {"start": v(8.9, -10.13) * mm, "end": v(8.8, -10.12) * mm});
            skLineSegment(sketch, "E403", {"start": v(8.8, -10.12) * mm, "end": v(8.7, -10.12) * mm});
            skLineSegment(sketch, "E404", {"start": v(8.7, -10.12) * mm, "end": v(8.6, -10.12) * mm});
            skLineSegment(sketch, "E405", {"start": v(8.6, -10.12) * mm, "end": v(8.5, -10.11) * mm});
            skLineSegment(sketch, "E406", {"start": v(8.5, -10.11) * mm, "end": v(8.4, -10.11) * mm});
            skLineSegment(sketch, "E407", {"start": v(8.4, -10.11) * mm, "end": v(8.3, -10.1) * mm});
            skLineSegment(sketch, "E408", {"start": v(8.3, -10.1) * mm, "end": v(8.2, -10.1) * mm});
            skLineSegment(sketch, "E409", {"start": v(8.2, -10.1) * mm, "end": v(8.1, -10.1) * mm});
            skLineSegment(sketch, "E410", {"start": v(8.1, -10.1) * mm, "end": v(8, -10.1) * mm});
            skLineSegment(sketch, "E411", {"start": v(8, -10.1) * mm, "end": v(7.9, -10.1) * mm});
            skLineSegment(sketch, "E412", {"start": v(7.9, -10.1) * mm, "end": v(7.81, -10.09) * mm});
            skLineSegment(sketch, "E413", {"start": v(7.81, -10.09) * mm, "end": v(7.71, -10.08) * mm});
            skLineSegment(sketch, "E414", {"start": v(7.71, -10.08) * mm, "end": v(7.61, -10.08) * mm});
            skLineSegment(sketch, "E415", {"start": v(7.61, -10.08) * mm, "end": v(7.51, -10.07) * mm});
            skLineSegment(sketch, "E416", {"start": v(7.51, -10.07) * mm, "end": v(7.41, -10.07) * mm});
            skLineSegment(sketch, "E417", {"start": v(7.41, -10.07) * mm, "end": v(7.31, -10.06) * mm});
            skLineSegment(sketch, "E418", {"start": v(7.31, -10.06) * mm, "end": v(7.21, -10.06) * mm});
            skLineSegment(sketch, "E419", {"start": v(7.21, -10.06) * mm, "end": v(7.11, -10.05) * mm});
            skLineSegment(sketch, "E420", {"start": v(7.11, -10.05) * mm, "end": v(7.01, -10.05) * mm});
            skLineSegment(sketch, "E421", {"start": v(7.01, -10.05) * mm, "end": v(6.92, -10.04) * mm});
            skLineSegment(sketch, "E422", {"start": v(6.92, -10.04) * mm, "end": v(6.82, -10.04) * mm});
            skLineSegment(sketch, "E423", {"start": v(6.82, -10.04) * mm, "end": v(6.72, -10.03) * mm});
            skLineSegment(sketch, "E424", {"start": v(6.72, -10.03) * mm, "end": v(6.62, -10.03) * mm});
            skLineSegment(sketch, "E425", {"start": v(6.62, -10.03) * mm, "end": v(6.52, -10.02) * mm});
            skLineSegment(sketch, "E426", {"start": v(6.52, -10.02) * mm, "end": v(6.42, -10.02) * mm});
            skLineSegment(sketch, "E427", {"start": v(6.42, -10.02) * mm, "end": v(6.32, -10.01) * mm});
            skLineSegment(sketch, "E428", {"start": v(6.32, -10.01) * mm, "end": v(6.21, -10) * mm});
            skLineSegment(sketch, "E429", {"start": v(6.21, -10) * mm, "end": v(6.11, -10) * mm});
            skLineSegment(sketch, "E430", {"start": v(6.11, -10) * mm, "end": v(6.01, -10) * mm});
            skLineSegment(sketch, "E431", {"start": v(6.01, -10) * mm, "end": v(5.91, -10) * mm});
            skLineSegment(sketch, "E432", {"start": v(5.91, -10) * mm, "end": v(5.81, -9.99) * mm});
            skLineSegment(sketch, "E433", {"start": v(5.81, -9.99) * mm, "end": v(5.71, -9.98) * mm});
            skLineSegment(sketch, "E434", {"start": v(5.71, -9.98) * mm, "end": v(5.61, -9.97) * mm});
            skLineSegment(sketch, "E435", {"start": v(5.61, -9.97) * mm, "end": v(5.51, -9.97) * mm});
            skLineSegment(sketch, "E436", {"start": v(5.51, -9.97) * mm, "end": v(5.41, -9.96) * mm});
            skLineSegment(sketch, "E437", {"start": v(5.41, -9.96) * mm, "end": v(5.31, -9.96) * mm});
            skLineSegment(sketch, "E438", {"start": v(5.31, -9.96) * mm, "end": v(5.2, -9.95) * mm});
            skLineSegment(sketch, "E439", {"start": v(5.2, -9.95) * mm, "end": v(5.1, -9.94) * mm});
            skLineSegment(sketch, "E440", {"start": v(5.1, -9.94) * mm, "end": v(5, -9.94) * mm});
            skLineSegment(sketch, "E441", {"start": v(5, -9.94) * mm, "end": v(4.9, -9.93) * mm});
            skLineSegment(sketch, "E442", {"start": v(4.9, -9.93) * mm, "end": v(4.8, -9.93) * mm});
            skLineSegment(sketch, "E443", {"start": v(4.8, -9.93) * mm, "end": v(4.7, -9.92) * mm});
            skLineSegment(sketch, "E444", {"start": v(4.7, -9.92) * mm, "end": v(4.6, -9.91) * mm});
            skLineSegment(sketch, "E445", {"start": v(4.6, -9.91) * mm, "end": v(4.5, -9.9) * mm});
            skLineSegment(sketch, "E446", {"start": v(4.5, -9.9) * mm, "end": v(4.4, -9.9) * mm});
            skLineSegment(sketch, "E447", {"start": v(4.4, -9.9) * mm, "end": v(4.3, -9.9) * mm});
            skLineSegment(sketch, "E448", {"start": v(4.3, -9.9) * mm, "end": v(4.2, -9.89) * mm});
            skLineSegment(sketch, "E449", {"start": v(4.2, -9.89) * mm, "end": v(4.1, -9.88) * mm});
            skLineSegment(sketch, "E450", {"start": v(4.1, -9.88) * mm, "end": v(4, -9.88) * mm});
            skLineSegment(sketch, "E451", {"start": v(4, -9.88) * mm, "end": v(3.9, -9.87) * mm});
            skLineSegment(sketch, "E452", {"start": v(3.9, -9.87) * mm, "end": v(3.8, -9.86) * mm});
            skLineSegment(sketch, "E453", {"start": v(3.8, -9.86) * mm, "end": v(3.7, -9.86) * mm});
            skLineSegment(sketch, "E454", {"start": v(3.7, -9.86) * mm, "end": v(3.59, -9.85) * mm});
            skLineSegment(sketch, "E455", {"start": v(3.59, -9.85) * mm, "end": v(3.49, -9.85) * mm});
            skLineSegment(sketch, "E456", {"start": v(3.49, -9.85) * mm, "end": v(3.39, -9.84) * mm});
            skLineSegment(sketch, "E457", {"start": v(3.39, -9.84) * mm, "end": v(3.28, -9.83) * mm});
            skLineSegment(sketch, "E458", {"start": v(3.28, -9.83) * mm, "end": v(3.18, -9.83) * mm});
            skLineSegment(sketch, "E459", {"start": v(3.18, -9.83) * mm, "end": v(3.08, -9.82) * mm});
            skLineSegment(sketch, "E460", {"start": v(3.08, -9.82) * mm, "end": v(2.98, -9.81) * mm});
            skLineSegment(sketch, "E461", {"start": v(2.98, -9.81) * mm, "end": v(2.88, -9.8) * mm});
            skLineSegment(sketch, "E462", {"start": v(2.88, -9.8) * mm, "end": v(2.78, -9.8) * mm});
            skLineSegment(sketch, "E463", {"start": v(2.78, -9.8) * mm, "end": v(2.67, -9.8) * mm});
            skLineSegment(sketch, "E464", {"start": v(2.67, -9.8) * mm, "end": v(2.57, -9.79) * mm});
            skLineSegment(sketch, "E465", {"start": v(2.57, -9.79) * mm, "end": v(2.47, -9.78) * mm});
            skLineSegment(sketch, "E466", {"start": v(2.47, -9.78) * mm, "end": v(2.37, -9.78) * mm});
            skLineSegment(sketch, "E467", {"start": v(2.37, -9.78) * mm, "end": v(2.27, -9.77) * mm});
            skLineSegment(sketch, "E468", {"start": v(2.27, -9.77) * mm, "end": v(2.16, -9.76) * mm});
            skLineSegment(sketch, "E469", {"start": v(2.16, -9.76) * mm, "end": v(2.06, -9.76) * mm});
            skLineSegment(sketch, "E470", {"start": v(2.06, -9.76) * mm, "end": v(1.96, -9.75) * mm});
            skLineSegment(sketch, "E471", {"start": v(1.96, -9.75) * mm, "end": v(1.86, -9.75) * mm});
            skLineSegment(sketch, "E472", {"start": v(1.86, -9.75) * mm, "end": v(1.75, -9.74) * mm});
            skLineSegment(sketch, "E473", {"start": v(1.75, -9.74) * mm, "end": v(1.65, -9.73) * mm});
            skLineSegment(sketch, "E474", {"start": v(1.65, -9.73) * mm, "end": v(1.55, -9.73) * mm});
            skLineSegment(sketch, "E475", {"start": v(1.55, -9.73) * mm, "end": v(1.45, -9.72) * mm});
            skLineSegment(sketch, "E476", {"start": v(1.45, -9.72) * mm, "end": v(1.35, -9.72) * mm});
            skLineSegment(sketch, "E477", {"start": v(1.35, -9.72) * mm, "end": v(1.24, -9.7) * mm});
            skLineSegment(sketch, "E478", {"start": v(1.24, -9.7) * mm, "end": v(1.14, -9.7) * mm});
            skLineSegment(sketch, "E479", {"start": v(1.14, -9.7) * mm, "end": v(1.04, -9.7) * mm});
            skLineSegment(sketch, "E480", {"start": v(1.04, -9.7) * mm, "end": v(0.94, -9.7) * mm});
            skLineSegment(sketch, "E481", {"start": v(0.94, -9.7) * mm, "end": v(0.83, -9.69) * mm});
            skLineSegment(sketch, "E482", {"start": v(0.83, -9.69) * mm, "end": v(0.73, -9.68) * mm});
            skLineSegment(sketch, "E483", {"start": v(0.73, -9.68) * mm, "end": v(0.63, -9.67) * mm});
            skLineSegment(sketch, "E484", {"start": v(0.63, -9.67) * mm, "end": v(0.53, -9.67) * mm});
            skLineSegment(sketch, "E485", {"start": v(0.53, -9.67) * mm, "end": v(0.42, -9.66) * mm});
            skLineSegment(sketch, "E486", {"start": v(0.42, -9.66) * mm, "end": v(0.32, -9.66) * mm});
            skLineSegment(sketch, "E487", {"start": v(0.32, -9.66) * mm, "end": v(0.22, -9.65) * mm});
            skLineSegment(sketch, "E488", {"start": v(0.22, -9.65) * mm, "end": v(0.12, -9.65) * mm});
            skLineSegment(sketch, "E489", {"start": v(0.12, -9.65) * mm, "end": v(0.01, -9.64) * mm});
            skLineSegment(sketch, "E490", {"start": v(0.01, -9.64) * mm, "end": v(-0.09, -9.63) * mm});
            skLineSegment(sketch, "E491", {"start": v(-0.09, -9.63) * mm, "end": v(-0.2, -9.63) * mm});
            skLineSegment(sketch, "E492", {"start": v(-0.2, -9.63) * mm, "end": v(-0.3, -9.62) * mm});
            skLineSegment(sketch, "E493", {"start": v(-0.3, -9.62) * mm, "end": v(-0.4, -9.62) * mm});
            skLineSegment(sketch, "E494", {"start": v(-0.4, -9.62) * mm, "end": v(-0.5, -9.61) * mm});
            skLineSegment(sketch, "E495", {"start": v(-0.5, -9.61) * mm, "end": v(-0.6, -9.6) * mm});
            skLineSegment(sketch, "E496", {"start": v(-0.6, -9.6) * mm, "end": v(-0.7, -9.6) * mm});
            skLineSegment(sketch, "E497", {"start": v(-0.7, -9.6) * mm, "end": v(-0.8, -9.6) * mm});
            skLineSegment(sketch, "E498", {"start": v(-0.8, -9.6) * mm, "end": v(-0.91, -9.6) * mm});
            skLineSegment(sketch, "E499", {"start": v(-0.91, -9.6) * mm, "end": v(-1.01, -9.59) * mm});
            skLineSegment(sketch, "E500", {"start": v(-1.01, -9.59) * mm, "end": v(-1.12, -9.58) * mm});
            skLineSegment(sketch, "E501", {"start": v(-1.12, -9.58) * mm, "end": v(-1.22, -9.58) * mm});
            skLineSegment(sketch, "E502", {"start": v(-1.22, -9.58) * mm, "end": v(-1.32, -9.57) * mm});
            skLineSegment(sketch, "E503", {"start": v(-1.32, -9.57) * mm, "end": v(-1.42, -9.57) * mm});
            skLineSegment(sketch, "E504", {"start": v(-1.42, -9.57) * mm, "end": v(-1.53, -9.56) * mm});
            skLineSegment(sketch, "E505", {"start": v(-1.53, -9.56) * mm, "end": v(-1.63, -9.56) * mm});
            skLineSegment(sketch, "E506", {"start": v(-1.63, -9.56) * mm, "end": v(-1.73, -9.55) * mm});
            skLineSegment(sketch, "E507", {"start": v(-1.73, -9.55) * mm, "end": v(-1.84, -9.55) * mm});
            skLineSegment(sketch, "E508", {"start": v(-1.84, -9.55) * mm, "end": v(-1.94, -9.55) * mm});
            skLineSegment(sketch, "E509", {"start": v(-1.94, -9.55) * mm, "end": v(-2.04, -9.54) * mm});
            skLineSegment(sketch, "E510", {"start": v(-2.04, -9.54) * mm, "end": v(-2.14, -9.54) * mm});
            skLineSegment(sketch, "E511", {"start": v(-2.14, -9.54) * mm, "end": v(-2.25, -9.53) * mm});
            skLineSegment(sketch, "E512", {"start": v(-2.25, -9.53) * mm, "end": v(-2.35, -9.53) * mm});
            skLineSegment(sketch, "E513", {"start": v(-2.35, -9.53) * mm, "end": v(-2.45, -9.53) * mm});
            skLineSegment(sketch, "E514", {"start": v(-2.45, -9.53) * mm, "end": v(-2.56, -9.52) * mm});
            skLineSegment(sketch, "E515", {"start": v(-2.56, -9.52) * mm, "end": v(-2.66, -9.52) * mm});
            skLineSegment(sketch, "E516", {"start": v(-2.66, -9.52) * mm, "end": v(-2.76, -9.52) * mm});
            skLineSegment(sketch, "E517", {"start": v(-2.76, -9.52) * mm, "end": v(-2.86, -9.51) * mm});
            skLineSegment(sketch, "E518", {"start": v(-2.86, -9.51) * mm, "end": v(-2.97, -9.5) * mm});
            skLineSegment(sketch, "E519", {"start": v(-2.97, -9.5) * mm, "end": v(-3.07, -9.5) * mm});
            skLineSegment(sketch, "E520", {"start": v(-3.07, -9.5) * mm, "end": v(-3.17, -9.5) * mm});
            skLineSegment(sketch, "E521", {"start": v(-3.17, -9.5) * mm, "end": v(-3.28, -9.5) * mm});
            skLineSegment(sketch, "E522", {"start": v(-3.28, -9.5) * mm, "end": v(-3.38, -9.5) * mm});
            skLineSegment(sketch, "E523", {"start": v(-3.38, -9.5) * mm, "end": v(-3.48, -9.5) * mm});
            skLineSegment(sketch, "E524", {"start": v(-3.48, -9.5) * mm, "end": v(-3.58, -9.5) * mm});
            skLineSegment(sketch, "E525", {"start": v(-3.58, -9.5) * mm, "end": v(-3.69, -9.49) * mm});
            skLineSegment(sketch, "E526", {"start": v(-3.69, -9.49) * mm, "end": v(-3.79, -9.49) * mm});
            skLineSegment(sketch, "E527", {"start": v(-3.79, -9.49) * mm, "end": v(-3.9, -9.48) * mm});
            skLineSegment(sketch, "E528", {"start": v(-3.9, -9.48) * mm, "end": v(-4, -9.48) * mm});
            skLineSegment(sketch, "E529", {"start": v(-4, -9.48) * mm, "end": v(-4.1, -9.48) * mm});
            skLineSegment(sketch, "E530", {"start": v(-4.1, -9.48) * mm, "end": v(-4.2, -9.48) * mm});
            skLineSegment(sketch, "E531", {"start": v(-4.2, -9.48) * mm, "end": v(-4.3, -9.48) * mm});
            skLineSegment(sketch, "E532", {"start": v(-4.3, -9.48) * mm, "end": v(-4.4, -9.47) * mm});
            skLineSegment(sketch, "E533", {"start": v(-4.4, -9.47) * mm, "end": v(-4.5, -9.47) * mm});
            skLineSegment(sketch, "E534", {"start": v(-4.5, -9.47) * mm, "end": v(-4.61, -9.47) * mm});
            skLineSegment(sketch, "E535", {"start": v(-4.61, -9.47) * mm, "end": v(-4.71, -9.47) * mm});
            skLineSegment(sketch, "E536", {"start": v(-4.71, -9.47) * mm, "end": v(-4.82, -9.47) * mm});
            skLineSegment(sketch, "E537", {"start": v(-4.82, -9.47) * mm, "end": v(-4.92, -9.47) * mm});
            skLineSegment(sketch, "E538", {"start": v(-4.92, -9.47) * mm, "end": v(-5.02, -9.47) * mm});
            skLineSegment(sketch, "E539", {"start": v(-5.02, -9.47) * mm, "end": v(-5.12, -9.47) * mm});
            skLineSegment(sketch, "E540", {"start": v(-5.12, -9.47) * mm, "end": v(-5.23, -9.47) * mm});
            skLineSegment(sketch, "E541", {"start": v(-5.23, -9.47) * mm, "end": v(-5.33, -9.47) * mm});
            skLineSegment(sketch, "E542", {"start": v(-5.33, -9.47) * mm, "end": v(-5.43, -9.47) * mm});
            skLineSegment(sketch, "E543", {"start": v(-5.43, -9.47) * mm, "end": v(-5.53, -9.47) * mm});
            skLineSegment(sketch, "E544", {"start": v(-5.53, -9.47) * mm, "end": v(-5.64, -9.47) * mm});
            skLineSegment(sketch, "E545", {"start": v(-5.64, -9.47) * mm, "end": v(-5.74, -9.47) * mm});
            skLineSegment(sketch, "E546", {"start": v(-5.74, -9.47) * mm, "end": v(-5.84, -9.47) * mm});
            skLineSegment(sketch, "E547", {"start": v(-5.84, -9.47) * mm, "end": v(-5.94, -9.47) * mm});
            skLineSegment(sketch, "E548", {"start": v(-5.94, -9.47) * mm, "end": v(-6.04, -9.47) * mm});
            skLineSegment(sketch, "E549", {"start": v(-6.04, -9.47) * mm, "end": v(-6.15, -9.47) * mm});
            skLineSegment(sketch, "E550", {"start": v(-6.15, -9.47) * mm, "end": v(-6.25, -9.47) * mm});
            skLineSegment(sketch, "E551", {"start": v(-6.25, -9.47) * mm, "end": v(-6.35, -9.47) * mm});
            skLineSegment(sketch, "E552", {"start": v(-6.35, -9.47) * mm, "end": v(-6.45, -9.47) * mm});
            skLineSegment(sketch, "E553", {"start": v(-6.45, -9.47) * mm, "end": v(-6.56, -9.47) * mm});
            skLineSegment(sketch, "E554", {"start": v(-6.56, -9.47) * mm, "end": v(-6.66, -9.47) * mm});
            skLineSegment(sketch, "E555", {"start": v(-6.66, -9.47) * mm, "end": v(-6.76, -9.48) * mm});
            skLineSegment(sketch, "E556", {"start": v(-6.76, -9.48) * mm, "end": v(-6.86, -9.48) * mm});
            skLineSegment(sketch, "E557", {"start": v(-6.86, -9.48) * mm, "end": v(-6.96, -9.48) * mm});
            skLineSegment(sketch, "E558", {"start": v(-6.96, -9.48) * mm, "end": v(-7.07, -9.48) * mm});
            skLineSegment(sketch, "E559", {"start": v(-7.07, -9.48) * mm, "end": v(-7.17, -9.48) * mm});
            skLineSegment(sketch, "E560", {"start": v(-7.17, -9.48) * mm, "end": v(-7.27, -9.49) * mm});
            skLineSegment(sketch, "E561", {"start": v(-7.27, -9.49) * mm, "end": v(-7.37, -9.5) * mm});
            skLineSegment(sketch, "E562", {"start": v(-7.37, -9.5) * mm, "end": v(-7.47, -9.5) * mm});
            skLineSegment(sketch, "E563", {"start": v(-7.47, -9.5) * mm, "end": v(-7.58, -9.5) * mm});
            skLineSegment(sketch, "E564", {"start": v(-7.58, -9.5) * mm, "end": v(-7.68, -9.5) * mm});
            skLineSegment(sketch, "E565", {"start": v(-7.68, -9.5) * mm, "end": v(-7.78, -9.5) * mm});
            skLineSegment(sketch, "E566", {"start": v(-7.78, -9.5) * mm, "end": v(-7.88, -9.5) * mm});
            skLineSegment(sketch, "E567", {"start": v(-7.88, -9.5) * mm, "end": v(-7.98, -9.51) * mm});
            skLineSegment(sketch, "E568", {"start": v(-7.98, -9.51) * mm, "end": v(-8.08, -9.51) * mm});
            skLineSegment(sketch, "E569", {"start": v(-8.08, -9.51) * mm, "end": v(-8.19, -9.52) * mm});
            skLineSegment(sketch, "E570", {"start": v(-8.19, -9.52) * mm, "end": v(-8.29, -9.52) * mm});
            skLineSegment(sketch, "E571", {"start": v(-8.29, -9.52) * mm, "end": v(-8.39, -9.53) * mm});
            skLineSegment(sketch, "E572", {"start": v(-8.39, -9.53) * mm, "end": v(-8.5, -9.53) * mm});
            skLineSegment(sketch, "E573", {"start": v(-8.5, -9.53) * mm, "end": v(-8.6, -9.54) * mm});
            skLineSegment(sketch, "E574", {"start": v(-8.6, -9.54) * mm, "end": v(-8.7, -9.54) * mm});
            skLineSegment(sketch, "E575", {"start": v(-8.7, -9.54) * mm, "end": v(-8.8, -9.55) * mm});
            skLineSegment(sketch, "E576", {"start": v(-8.8, -9.55) * mm, "end": v(-8.9, -9.56) * mm});
            skLineSegment(sketch, "E577", {"start": v(-8.9, -9.56) * mm, "end": v(-9, -9.56) * mm});
            skLineSegment(sketch, "E578", {"start": v(-9, -9.56) * mm, "end": v(-9.1, -9.57) * mm});
            skLineSegment(sketch, "E579", {"start": v(-9.1, -9.57) * mm, "end": v(-9.2, -9.57) * mm});
            skLineSegment(sketch, "E580", {"start": v(-9.2, -9.57) * mm, "end": v(-9.3, -9.58) * mm});
            skLineSegment(sketch, "E581", {"start": v(-9.3, -9.58) * mm, "end": v(-9.4, -9.59) * mm});
            skLineSegment(sketch, "E582", {"start": v(-9.4, -9.59) * mm, "end": v(-9.5, -9.6) * mm});
            skLineSegment(sketch, "E583", {"start": v(-9.5, -9.6) * mm, "end": v(-9.6, -9.6) * mm});
            skLineSegment(sketch, "E584", {"start": v(-9.6, -9.6) * mm, "end": v(-9.7, -9.6) * mm});
            skLineSegment(sketch, "E585", {"start": v(-9.7, -9.6) * mm, "end": v(-9.8, -9.62) * mm});
            skLineSegment(sketch, "E586", {"start": v(-9.8, -9.62) * mm, "end": v(-9.9, -9.62) * mm});
            skLineSegment(sketch, "E587", {"start": v(-9.9, -9.62) * mm, "end": v(-10, -9.63) * mm});
            skLineSegment(sketch, "E588", {"start": v(-10, -9.63) * mm, "end": v(-10.1, -9.64) * mm});
            skLineSegment(sketch, "E589", {"start": v(-10.1, -9.64) * mm, "end": v(-10.2, -9.65) * mm});
            skLineSegment(sketch, "E590", {"start": v(-10.2, -9.65) * mm, "end": v(-10.3, -9.66) * mm});
            skLineSegment(sketch, "E591", {"start": v(-10.3, -9.66) * mm, "end": v(-10.4, -9.67) * mm});
            skLineSegment(sketch, "E592", {"start": v(-10.4, -9.67) * mm, "end": v(-10.5, -9.68) * mm});
            skLineSegment(sketch, "E593", {"start": v(-10.5, -9.68) * mm, "end": v(-10.6, -9.69) * mm});
            skLineSegment(sketch, "E594", {"start": v(-10.6, -9.69) * mm, "end": v(-10.7, -9.7) * mm});
            skLineSegment(sketch, "E595", {"start": v(-10.7, -9.7) * mm, "end": v(-10.8, -9.7) * mm});
            skLineSegment(sketch, "E596", {"start": v(-10.8, -9.7) * mm, "end": v(-10.9, -9.72) * mm});
            skLineSegment(sketch, "E597", {"start": v(-10.9, -9.72) * mm, "end": v(-11, -9.73) * mm});
            skLineSegment(sketch, "E598", {"start": v(-11, -9.73) * mm, "end": v(-11.1, -9.74) * mm});
            skLineSegment(sketch, "E599", {"start": v(-11.1, -9.74) * mm, "end": v(-11.2, -9.75) * mm});
            skLineSegment(sketch, "E600", {"start": v(-11.2, -9.75) * mm, "end": v(-11.3, -9.76) * mm});
            skLineSegment(sketch, "E601", {"start": v(-11.3, -9.76) * mm, "end": v(-11.4, -9.77) * mm});
            skLineSegment(sketch, "E602", {"start": v(-11.4, -9.77) * mm, "end": v(-11.5, -9.78) * mm});
            skLineSegment(sketch, "E603", {"start": v(-11.5, -9.78) * mm, "end": v(-11.6, -9.8) * mm});
            skLineSegment(sketch, "E604", {"start": v(-11.6, -9.8) * mm, "end": v(-11.7, -9.8) * mm});
            skLineSegment(sketch, "E605", {"start": v(-11.7, -9.8) * mm, "end": v(-11.8, -9.82) * mm});
            skLineSegment(sketch, "E606", {"start": v(-11.8, -9.82) * mm, "end": v(-11.9, -9.83) * mm});
            skLineSegment(sketch, "E607", {"start": v(-11.9, -9.83) * mm, "end": v(-12, -9.84) * mm});
            skLineSegment(sketch, "E608", {"start": v(-12, -9.84) * mm, "end": v(-12.1, -9.86) * mm});
            skLineSegment(sketch, "E609", {"start": v(-12.1, -9.86) * mm, "end": v(-12.2, -9.87) * mm});
            skLineSegment(sketch, "E610", {"start": v(-12.2, -9.87) * mm, "end": v(-12.3, -9.88) * mm});
            skLineSegment(sketch, "E611", {"start": v(-12.3, -9.88) * mm, "end": v(-12.4, -9.9) * mm});
            skLineSegment(sketch, "E612", {"start": v(-12.4, -9.9) * mm, "end": v(-12.5, -9.91) * mm});
            skLineSegment(sketch, "E613", {"start": v(-12.5, -9.91) * mm, "end": v(-12.6, -9.93) * mm});
            skLineSegment(sketch, "E614", {"start": v(-12.6, -9.93) * mm, "end": v(-12.7, -9.94) * mm});
            skLineSegment(sketch, "E615", {"start": v(-12.7, -9.94) * mm, "end": v(-12.8, -9.96) * mm});
            skLineSegment(sketch, "E616", {"start": v(-12.8, -9.96) * mm, "end": v(-12.9, -9.97) * mm});
            skLineSegment(sketch, "E617", {"start": v(-12.9, -9.97) * mm, "end": v(-13, -9.99) * mm});
            skLineSegment(sketch, "E618", {"start": v(-13, -9.99) * mm, "end": v(-13.1, -10) * mm});
            skLineSegment(sketch, "E619", {"start": v(-13.1, -10) * mm, "end": v(-13.2, -10.02) * mm});
            skLineSegment(sketch, "E620", {"start": v(-13.2, -10.02) * mm, "end": v(-13.3, -10.04) * mm});
            skLineSegment(sketch, "E621", {"start": v(-13.3, -10.04) * mm, "end": v(-13.39, -10.05) * mm});
            skLineSegment(sketch, "E622", {"start": v(-13.39, -10.05) * mm, "end": v(-13.49, -10.07) * mm});
            skLineSegment(sketch, "E623", {"start": v(-13.49, -10.07) * mm, "end": v(-13.59, -10.09) * mm});
            skLineSegment(sketch, "E624", {"start": v(-13.59, -10.09) * mm, "end": v(-13.68, -10.1) * mm});
            skLineSegment(sketch, "E625", {"start": v(-13.68, -10.1) * mm, "end": v(-13.78, -10.12) * mm});
            skLineSegment(sketch, "E626", {"start": v(-13.78, -10.12) * mm, "end": v(-13.88, -10.14) * mm});
            skLineSegment(sketch, "E627", {"start": v(-13.88, -10.14) * mm, "end": v(-13.98, -10.16) * mm});
            skLineSegment(sketch, "E628", {"start": v(-13.98, -10.16) * mm, "end": v(-14.08, -10.18) * mm});
            skLineSegment(sketch, "E629", {"start": v(-14.08, -10.18) * mm, "end": v(-14.17, -10.2) * mm});
            skLineSegment(sketch, "E630", {"start": v(-14.17, -10.2) * mm, "end": v(-14.27, -10.22) * mm});
            skLineSegment(sketch, "E631", {"start": v(-14.27, -10.22) * mm, "end": v(-14.37, -10.24) * mm});
            skLineSegment(sketch, "E632", {"start": v(-14.37, -10.24) * mm, "end": v(-14.47, -10.26) * mm});
            skLineSegment(sketch, "E633", {"start": v(-14.47, -10.26) * mm, "end": v(-14.56, -10.28) * mm});
            skLineSegment(sketch, "E634", {"start": v(-14.56, -10.28) * mm, "end": v(-14.66, -10.3) * mm});
            skLineSegment(sketch, "E635", {"start": v(-14.66, -10.3) * mm, "end": v(-14.76, -10.32) * mm});
            skLineSegment(sketch, "E636", {"start": v(-14.76, -10.32) * mm, "end": v(-14.85, -10.34) * mm});
            skLineSegment(sketch, "E637", {"start": v(-14.85, -10.34) * mm, "end": v(-14.95, -10.36) * mm});
            skLineSegment(sketch, "E638", {"start": v(-14.95, -10.36) * mm, "end": v(-15.05, -10.39) * mm});
            skLineSegment(sketch, "E639", {"start": v(-15.05, -10.39) * mm, "end": v(-15.14, -10.4) * mm});
            skLineSegment(sketch, "E640", {"start": v(-15.14, -10.4) * mm, "end": v(-15.24, -10.43) * mm});
            skLineSegment(sketch, "E641", {"start": v(-15.24, -10.43) * mm, "end": v(-15.34, -10.45) * mm});
            skLineSegment(sketch, "E642", {"start": v(-15.34, -10.45) * mm, "end": v(-15.43, -10.48) * mm});
            skLineSegment(sketch, "E643", {"start": v(-15.43, -10.48) * mm, "end": v(-15.53, -10.5) * mm});
            skLineSegment(sketch, "E644", {"start": v(-15.53, -10.5) * mm, "end": v(-15.63, -10.52) * mm});
            skLineSegment(sketch, "E645", {"start": v(-15.63, -10.52) * mm, "end": v(-15.73, -10.55) * mm});
            skLineSegment(sketch, "E646", {"start": v(-15.73, -10.55) * mm, "end": v(-15.83, -10.58) * mm});
            skLineSegment(sketch, "E647", {"start": v(-15.83, -10.58) * mm, "end": v(-15.92, -10.6) * mm});
            skLineSegment(sketch, "E648", {"start": v(-15.92, -10.6) * mm, "end": v(-16.02, -10.63) * mm});
            skLineSegment(sketch, "E649", {"start": v(-16.02, -10.63) * mm, "end": v(-16.12, -10.66) * mm});
            skLineSegment(sketch, "E650", {"start": v(-16.12, -10.66) * mm, "end": v(-16.22, -10.68) * mm});
            skLineSegment(sketch, "E651", {"start": v(-16.22, -10.68) * mm, "end": v(-16.31, -10.71) * mm});
            skLineSegment(sketch, "E652", {"start": v(-16.31, -10.71) * mm, "end": v(-16.41, -10.74) * mm});
            skLineSegment(sketch, "E653", {"start": v(-16.41, -10.74) * mm, "end": v(-16.5, -10.77) * mm});
            skLineSegment(sketch, "E654", {"start": v(-16.5, -10.77) * mm, "end": v(-16.6, -10.8) * mm});
            skLineSegment(sketch, "E655", {"start": v(-16.6, -10.8) * mm, "end": v(-16.7, -10.83) * mm});
            skLineSegment(sketch, "E656", {"start": v(-16.7, -10.83) * mm, "end": v(-16.8, -10.86) * mm});
            skLineSegment(sketch, "E657", {"start": v(-16.8, -10.86) * mm, "end": v(-16.9, -10.89) * mm});
            skLineSegment(sketch, "E658", {"start": v(-16.9, -10.89) * mm, "end": v(-17, -10.92) * mm});
            skLineSegment(sketch, "E659", {"start": v(-17, -10.92) * mm, "end": v(-17.09, -10.95) * mm});
            skLineSegment(sketch, "E660", {"start": v(-17.09, -10.95) * mm, "end": v(-17.18, -10.99) * mm});
            skLineSegment(sketch, "E661", {"start": v(-17.18, -10.99) * mm, "end": v(-17.28, -11.02) * mm});
            skLineSegment(sketch, "E662", {"start": v(-17.28, -11.02) * mm, "end": v(-17.38, -11.05) * mm});
            skLineSegment(sketch, "E663", {"start": v(-17.38, -11.05) * mm, "end": v(-17.47, -11.09) * mm});
            skLineSegment(sketch, "E664", {"start": v(-17.47, -11.09) * mm, "end": v(-17.57, -11.12) * mm});
            skLineSegment(sketch, "E665", {"start": v(-17.57, -11.12) * mm, "end": v(-17.66, -11.16) * mm});
            skLineSegment(sketch, "E666", {"start": v(-17.66, -11.16) * mm, "end": v(-17.76, -11.2) * mm});
            skLineSegment(sketch, "E667", {"start": v(-17.76, -11.2) * mm, "end": v(-17.85, -11.23) * mm});
            skLineSegment(sketch, "E668", {"start": v(-17.85, -11.23) * mm, "end": v(-17.95, -11.27) * mm});
            skLineSegment(sketch, "E669", {"start": v(-17.95, -11.27) * mm, "end": v(-18.04, -11.3) * mm});
            skLineSegment(sketch, "E670", {"start": v(-18.04, -11.3) * mm, "end": v(-18.13, -11.35) * mm});
            skLineSegment(sketch, "E671", {"start": v(-18.13, -11.35) * mm, "end": v(-18.23, -11.39) * mm});
            skLineSegment(sketch, "E672", {"start": v(-18.23, -11.39) * mm, "end": v(-18.32, -11.43) * mm});
            skLineSegment(sketch, "E673", {"start": v(-18.32, -11.43) * mm, "end": v(-18.41, -11.47) * mm});
            skLineSegment(sketch, "E674", {"start": v(-18.41, -11.47) * mm, "end": v(-18.5, -11.5) * mm});
            skLineSegment(sketch, "E675", {"start": v(-18.5, -11.5) * mm, "end": v(-18.6, -11.55) * mm});
            skLineSegment(sketch, "E676", {"start": v(-18.6, -11.55) * mm, "end": v(-18.7, -11.6) * mm});
            skLineSegment(sketch, "E677", {"start": v(-18.7, -11.6) * mm, "end": v(-18.78, -11.63) * mm});
            skLineSegment(sketch, "E678", {"start": v(-18.78, -11.63) * mm, "end": v(-18.87, -11.68) * mm});
            skLineSegment(sketch, "E679", {"start": v(-18.87, -11.68) * mm, "end": v(-18.97, -11.72) * mm});
            skLineSegment(sketch, "E680", {"start": v(-18.97, -11.72) * mm, "end": v(-19.06, -11.76) * mm});
            skLineSegment(sketch, "E681", {"start": v(-19.06, -11.76) * mm, "end": v(-19.15, -11.8) * mm});
            skLineSegment(sketch, "E682", {"start": v(-19.15, -11.8) * mm, "end": v(-19.24, -11.86) * mm});
            skLineSegment(sketch, "E683", {"start": v(-19.24, -11.86) * mm, "end": v(-19.33, -11.9) * mm});
            skLineSegment(sketch, "E684", {"start": v(-19.33, -11.9) * mm, "end": v(-19.42, -11.95) * mm});
            skLineSegment(sketch, "E685", {"start": v(-19.42, -11.95) * mm, "end": v(-19.5, -12) * mm});
            skLineSegment(sketch, "E686", {"start": v(-19.5, -12) * mm, "end": v(-19.6, -12.05) * mm});
            skLineSegment(sketch, "E687", {"start": v(-19.6, -12.05) * mm, "end": v(-19.68, -12.1) * mm});
            skLineSegment(sketch, "E688", {"start": v(-19.68, -12.1) * mm, "end": v(-19.77, -12.14) * mm});
            skLineSegment(sketch, "E689", {"start": v(-19.77, -12.14) * mm, "end": v(-19.86, -12.2) * mm});
            skLineSegment(sketch, "E690", {"start": v(-19.86, -12.2) * mm, "end": v(-19.95, -12.25) * mm});
            skLineSegment(sketch, "E691", {"start": v(-19.95, -12.25) * mm, "end": v(-20.04, -12.3) * mm});
            skLineSegment(sketch, "E692", {"start": v(-20.04, -12.3) * mm, "end": v(-20.12, -12.35) * mm});
            skLineSegment(sketch, "E693", {"start": v(-20.12, -12.35) * mm, "end": v(-20.2, -12.4) * mm});
            skLineSegment(sketch, "E694", {"start": v(-20.2, -12.4) * mm, "end": v(-20.3, -12.46) * mm});
            skLineSegment(sketch, "E695", {"start": v(-20.3, -12.46) * mm, "end": v(-20.38, -12.51) * mm});
            skLineSegment(sketch, "E696", {"start": v(-20.38, -12.51) * mm, "end": v(-20.46, -12.57) * mm});
            skLineSegment(sketch, "E697", {"start": v(-20.46, -12.57) * mm, "end": v(-20.55, -12.62) * mm});
            skLineSegment(sketch, "E698", {"start": v(-20.55, -12.62) * mm, "end": v(-20.63, -12.68) * mm});
            skLineSegment(sketch, "E699", {"start": v(-20.63, -12.68) * mm, "end": v(-20.72, -12.74) * mm});
            skLineSegment(sketch, "E700", {"start": v(-20.72, -12.74) * mm, "end": v(-20.8, -12.8) * mm});
            skLineSegment(sketch, "E701", {"start": v(-20.8, -12.8) * mm, "end": v(-20.88, -12.85) * mm});
            skLineSegment(sketch, "E702", {"start": v(-20.88, -12.85) * mm, "end": v(-20.96, -12.91) * mm});
            skLineSegment(sketch, "E703", {"start": v(-20.96, -12.91) * mm, "end": v(-21.05, -12.97) * mm});
            skLineSegment(sketch, "E704", {"start": v(-21.05, -12.97) * mm, "end": v(-21.13, -13.03) * mm});
            skLineSegment(sketch, "E705", {"start": v(-21.13, -13.03) * mm, "end": v(-21.2, -13.1) * mm});
            skLineSegment(sketch, "E706", {"start": v(-21.2, -13.1) * mm, "end": v(-21.29, -13.15) * mm});
            skLineSegment(sketch, "E707", {"start": v(-21.29, -13.15) * mm, "end": v(-21.37, -13.22) * mm});
            skLineSegment(sketch, "E708", {"start": v(-21.37, -13.22) * mm, "end": v(-21.45, -13.28) * mm});
            skLineSegment(sketch, "E709", {"start": v(-21.45, -13.28) * mm, "end": v(-21.53, -13.35) * mm});
            skLineSegment(sketch, "E710", {"start": v(-21.53, -13.35) * mm, "end": v(-21.6, -13.41) * mm});
            skLineSegment(sketch, "E711", {"start": v(-21.6, -13.41) * mm, "end": v(-21.68, -13.48) * mm});
            skLineSegment(sketch, "E712", {"start": v(-21.68, -13.48) * mm, "end": v(-21.76, -13.54) * mm});
            skLineSegment(sketch, "E713", {"start": v(-21.76, -13.54) * mm, "end": v(-21.84, -13.6) * mm});
            skLineSegment(sketch, "E714", {"start": v(-21.84, -13.6) * mm, "end": v(-21.91, -13.68) * mm});
            skLineSegment(sketch, "E715", {"start": v(-21.91, -13.68) * mm, "end": v(-21.96, -13.72) * mm});
            skLineSegment(sketch, "E716", {"start": v(-21.96, -13.72) * mm, "end": v(-22.02, -13.77) * mm});
            skLineSegment(sketch, "E717", {"start": v(-22.02, -13.77) * mm, "end": v(-22.08, -13.83) * mm});
            skLineSegment(sketch, "E718", {"start": v(-22.08, -13.83) * mm, "end": v(-22.14, -13.89) * mm});
            skLineSegment(sketch, "E719", {"start": v(-22.14, -13.89) * mm, "end": v(-22.2, -13.95) * mm});
            skLineSegment(sketch, "E720", {"start": v(-22.2, -13.95) * mm, "end": v(-22.28, -14.02) * mm});
            skLineSegment(sketch, "E721", {"start": v(-22.28, -14.02) * mm, "end": v(-22.35, -14.09) * mm});
            skLineSegment(sketch, "E722", {"start": v(-22.35, -14.09) * mm, "end": v(-22.42, -14.16) * mm});
            skLineSegment(sketch, "E723", {"start": v(-22.42, -14.16) * mm, "end": v(-22.5, -14.24) * mm});
            skLineSegment(sketch, "E724", {"start": v(-22.5, -14.24) * mm, "end": v(-22.56, -14.31) * mm});
            skLineSegment(sketch, "E725", {"start": v(-22.56, -14.31) * mm, "end": v(-22.64, -14.4) * mm});
            skLineSegment(sketch, "E726", {"start": v(-22.64, -14.4) * mm, "end": v(-22.7, -14.48) * mm});
            skLineSegment(sketch, "E727", {"start": v(-22.7, -14.48) * mm, "end": v(-22.77, -14.56) * mm});
            skLineSegment(sketch, "E728", {"start": v(-22.77, -14.56) * mm, "end": v(-22.84, -14.65) * mm});
            skLineSegment(sketch, "E729", {"start": v(-22.84, -14.65) * mm, "end": v(-22.9, -14.73) * mm});
            skLineSegment(sketch, "E730", {"start": v(-22.9, -14.73) * mm, "end": v(-22.97, -14.82) * mm});
            skLineSegment(sketch, "E731", {"start": v(-22.97, -14.82) * mm, "end": v(-23.02, -14.9) * mm});
            skLineSegment(sketch, "E732", {"start": v(-23.02, -14.9) * mm, "end": v(-23.07, -15) * mm});
            skLineSegment(sketch, "E733", {"start": v(-23.07, -15) * mm, "end": v(-23.12, -15.08) * mm});
            skLineSegment(sketch, "E734", {"start": v(-23.12, -15.08) * mm, "end": v(-23.16, -15.17) * mm});
            skLineSegment(sketch, "E735", {"start": v(-23.16, -15.17) * mm, "end": v(-23.2, -15.26) * mm});
            skLineSegment(sketch, "E736", {"start": v(-23.2, -15.26) * mm, "end": v(-23.22, -15.35) * mm});
            skLineSegment(sketch, "E737", {"start": v(-23.22, -15.35) * mm, "end": v(-23.24, -15.44) * mm});
            skLineSegment(sketch, "E738", {"start": v(-23.24, -15.44) * mm, "end": v(-23.25, -15.52) * mm});
            skLineSegment(sketch, "E739", {"start": v(-23.25, -15.52) * mm, "end": v(-23.26, -15.6) * mm});
            skLineSegment(sketch, "E740", {"start": v(-23.26, -15.6) * mm, "end": v(-23.25, -15.69) * mm});
            skLineSegment(sketch, "E741", {"start": v(-23.25, -15.69) * mm, "end": v(-23.24, -15.77) * mm});
            skLineSegment(sketch, "E742", {"start": v(-23.24, -15.77) * mm, "end": v(-23.21, -15.84) * mm});
            skLineSegment(sketch, "E743", {"start": v(-23.21, -15.84) * mm, "end": v(-23.18, -15.91) * mm});
            skLineSegment(sketch, "E744", {"start": v(-23.18, -15.91) * mm, "end": v(-23.13, -15.97) * mm});
            skLineSegment(sketch, "E745", {"start": v(-23.13, -15.97) * mm, "end": v(-23.08, -16.02) * mm});
            skLineSegment(sketch, "E746", {"start": v(-23.08, -16.02) * mm, "end": v(-23.02, -16.05) * mm});
            skLineSegment(sketch, "E747", {"start": v(-23.02, -16.05) * mm, "end": v(-22.95, -16.08) * mm});
            skLineSegment(sketch, "E748", {"start": v(-22.95, -16.08) * mm, "end": v(-22.88, -16.1) * mm});
            skLineSegment(sketch, "E749", {"start": v(-22.88, -16.1) * mm, "end": v(-22.8, -16.11) * mm});
            skLineSegment(sketch, "E750", {"start": v(-22.8, -16.11) * mm, "end": v(-22.72, -16.12) * mm});
            skLineSegment(sketch, "E751", {"start": v(-22.72, -16.12) * mm, "end": v(-22.63, -16.12) * mm});
            skLineSegment(sketch, "E752", {"start": v(-22.63, -16.12) * mm, "end": v(-22.54, -16.1) * mm});
            skLineSegment(sketch, "E753", {"start": v(-22.54, -16.1) * mm, "end": v(-22.45, -16.1) * mm});
            skLineSegment(sketch, "E754", {"start": v(-22.45, -16.1) * mm, "end": v(-22.35, -16.07) * mm});
            skLineSegment(sketch, "E755", {"start": v(-22.35, -16.07) * mm, "end": v(-22.25, -16.05) * mm});
            skLineSegment(sketch, "E756", {"start": v(-22.25, -16.05) * mm, "end": v(-22.15, -16.02) * mm});
            skLineSegment(sketch, "E757", {"start": v(-22.15, -16.02) * mm, "end": v(-22.05, -15.99) * mm});
            skLineSegment(sketch, "E758", {"start": v(-22.05, -15.99) * mm, "end": v(-21.95, -15.95) * mm});
            skLineSegment(sketch, "E759", {"start": v(-21.95, -15.95) * mm, "end": v(-21.85, -15.92) * mm});
            skLineSegment(sketch, "E760", {"start": v(-21.85, -15.92) * mm, "end": v(-21.75, -15.88) * mm});
            skLineSegment(sketch, "E761", {"start": v(-21.75, -15.88) * mm, "end": v(-21.65, -15.84) * mm});
            skLineSegment(sketch, "E762", {"start": v(-21.65, -15.84) * mm, "end": v(-21.55, -15.8) * mm});
            skLineSegment(sketch, "E763", {"start": v(-21.55, -15.8) * mm, "end": v(-21.46, -15.77) * mm});
            skLineSegment(sketch, "E764", {"start": v(-21.46, -15.77) * mm, "end": v(-21.37, -15.73) * mm});
            skLineSegment(sketch, "E765", {"start": v(-21.37, -15.73) * mm, "end": v(-21.3, -15.7) * mm});
            skLineSegment(sketch, "E766", {"start": v(-21.3, -15.7) * mm, "end": v(-21.21, -15.66) * mm});
            skLineSegment(sketch, "E767", {"start": v(-21.21, -15.66) * mm, "end": v(-21.14, -15.63) * mm});
            skLineSegment(sketch, "E768", {"start": v(-21.14, -15.63) * mm, "end": v(-21.07, -15.6) * mm});
            skLineSegment(sketch, "E769", {"start": v(-21.07, -15.6) * mm, "end": v(-21.01, -15.58) * mm});
            skLineSegment(sketch, "E770", {"start": v(-21.01, -15.58) * mm, "end": v(-20.96, -15.56) * mm});
            skLineSegment(sketch, "E771", {"start": v(-20.96, -15.56) * mm, "end": v(-20.86, -15.53) * mm});
            skLineSegment(sketch, "E772", {"start": v(-20.86, -15.53) * mm, "end": v(-20.76, -15.5) * mm});
            skLineSegment(sketch, "E773", {"start": v(-20.76, -15.5) * mm, "end": v(-20.66, -15.46) * mm});
            skLineSegment(sketch, "E774", {"start": v(-20.66, -15.46) * mm, "end": v(-20.57, -15.43) * mm});
            skLineSegment(sketch, "E775", {"start": v(-20.57, -15.43) * mm, "end": v(-20.47, -15.4) * mm});
            skLineSegment(sketch, "E776", {"start": v(-20.47, -15.4) * mm, "end": v(-20.37, -15.38) * mm});
            skLineSegment(sketch, "E777", {"start": v(-20.37, -15.38) * mm, "end": v(-20.27, -15.35) * mm});
            skLineSegment(sketch, "E778", {"start": v(-20.27, -15.35) * mm, "end": v(-20.17, -15.32) * mm});
            skLineSegment(sketch, "E779", {"start": v(-20.17, -15.32) * mm, "end": v(-20.07, -15.3) * mm});
            skLineSegment(sketch, "E780", {"start": v(-20.07, -15.3) * mm, "end": v(-19.97, -15.27) * mm});
            skLineSegment(sketch, "E781", {"start": v(-19.97, -15.27) * mm, "end": v(-19.87, -15.24) * mm});
            skLineSegment(sketch, "E782", {"start": v(-19.87, -15.24) * mm, "end": v(-19.77, -15.22) * mm});
            skLineSegment(sketch, "E783", {"start": v(-19.77, -15.22) * mm, "end": v(-19.67, -15.2) * mm});
            skLineSegment(sketch, "E784", {"start": v(-19.67, -15.2) * mm, "end": v(-19.58, -15.17) * mm});
            skLineSegment(sketch, "E785", {"start": v(-19.58, -15.17) * mm, "end": v(-19.48, -15.14) * mm});
            skLineSegment(sketch, "E786", {"start": v(-19.48, -15.14) * mm, "end": v(-19.38, -15.12) * mm});
            skLineSegment(sketch, "E787", {"start": v(-19.38, -15.12) * mm, "end": v(-19.28, -15.1) * mm});
            skLineSegment(sketch, "E788", {"start": v(-19.28, -15.1) * mm, "end": v(-19.18, -15.08) * mm});
            skLineSegment(sketch, "E789", {"start": v(-19.18, -15.08) * mm, "end": v(-19.08, -15.06) * mm});
            skLineSegment(sketch, "E790", {"start": v(-19.08, -15.06) * mm, "end": v(-18.98, -15.04) * mm});
            skLineSegment(sketch, "E791", {"start": v(-18.98, -15.04) * mm, "end": v(-18.88, -15.02) * mm});
            skLineSegment(sketch, "E792", {"start": v(-18.88, -15.02) * mm, "end": v(-18.78, -15) * mm});
            skLineSegment(sketch, "E793", {"start": v(-18.78, -15) * mm, "end": v(-18.68, -14.98) * mm});
            skLineSegment(sketch, "E794", {"start": v(-18.68, -14.98) * mm, "end": v(-18.58, -14.96) * mm});
            skLineSegment(sketch, "E795", {"start": v(-18.58, -14.96) * mm, "end": v(-18.48, -14.94) * mm});
            skLineSegment(sketch, "E796", {"start": v(-18.48, -14.94) * mm, "end": v(-18.38, -14.93) * mm});
            skLineSegment(sketch, "E797", {"start": v(-18.38, -14.93) * mm, "end": v(-18.28, -14.9) * mm});
            skLineSegment(sketch, "E798", {"start": v(-18.28, -14.9) * mm, "end": v(-18.18, -14.9) * mm});
            skLineSegment(sketch, "E799", {"start": v(-18.18, -14.9) * mm, "end": v(-18.08, -14.88) * mm});
            skLineSegment(sketch, "E800", {"start": v(-18.08, -14.88) * mm, "end": v(-17.98, -14.86) * mm});
            skLineSegment(sketch, "E801", {"start": v(-17.98, -14.86) * mm, "end": v(-17.88, -14.85) * mm});
            skLineSegment(sketch, "E802", {"start": v(-17.88, -14.85) * mm, "end": v(-17.78, -14.83) * mm});
            skLineSegment(sketch, "E803", {"start": v(-17.78, -14.83) * mm, "end": v(-17.68, -14.82) * mm});
            skLineSegment(sketch, "E804", {"start": v(-17.68, -14.82) * mm, "end": v(-17.58, -14.8) * mm});
            skLineSegment(sketch, "E805", {"start": v(-17.58, -14.8) * mm, "end": v(-17.47, -14.79) * mm});
            skLineSegment(sketch, "E806", {"start": v(-17.47, -14.79) * mm, "end": v(-17.37, -14.77) * mm});
            skLineSegment(sketch, "E807", {"start": v(-17.37, -14.77) * mm, "end": v(-17.27, -14.76) * mm});
            skLineSegment(sketch, "E808", {"start": v(-17.27, -14.76) * mm, "end": v(-17.17, -14.75) * mm});
            skLineSegment(sketch, "E809", {"start": v(-17.17, -14.75) * mm, "end": v(-17.07, -14.74) * mm});
            skLineSegment(sketch, "E810", {"start": v(-17.07, -14.74) * mm, "end": v(-16.97, -14.72) * mm});
            skLineSegment(sketch, "E811", {"start": v(-16.97, -14.72) * mm, "end": v(-16.87, -14.71) * mm});
            skLineSegment(sketch, "E812", {"start": v(-16.87, -14.71) * mm, "end": v(-16.77, -14.7) * mm});
            skLineSegment(sketch, "E813", {"start": v(-16.77, -14.7) * mm, "end": v(-16.67, -14.69) * mm});
            skLineSegment(sketch, "E814", {"start": v(-16.67, -14.69) * mm, "end": v(-16.57, -14.68) * mm});
            skLineSegment(sketch, "E815", {"start": v(-16.57, -14.68) * mm, "end": v(-16.47, -14.66) * mm});
            skLineSegment(sketch, "E816", {"start": v(-16.47, -14.66) * mm, "end": v(-16.36, -14.65) * mm});
            skLineSegment(sketch, "E817", {"start": v(-16.36, -14.65) * mm, "end": v(-16.26, -14.64) * mm});
            skLineSegment(sketch, "E818", {"start": v(-16.26, -14.64) * mm, "end": v(-16.16, -14.63) * mm});
            skLineSegment(sketch, "E819", {"start": v(-16.16, -14.63) * mm, "end": v(-16.06, -14.62) * mm});
            skLineSegment(sketch, "E820", {"start": v(-16.06, -14.62) * mm, "end": v(-15.96, -14.6) * mm});
            skLineSegment(sketch, "E821", {"start": v(-15.96, -14.6) * mm, "end": v(-15.86, -14.6) * mm});
            skLineSegment(sketch, "E822", {"start": v(-15.86, -14.6) * mm, "end": v(-15.76, -14.59) * mm});
            skLineSegment(sketch, "E823", {"start": v(-15.76, -14.59) * mm, "end": v(-15.66, -14.58) * mm});
            skLineSegment(sketch, "E824", {"start": v(-15.66, -14.58) * mm, "end": v(-15.55, -14.57) * mm});
            skLineSegment(sketch, "E825", {"start": v(-15.55, -14.57) * mm, "end": v(-15.45, -14.56) * mm});
            skLineSegment(sketch, "E826", {"start": v(-15.45, -14.56) * mm, "end": v(-15.35, -14.55) * mm});
            skLineSegment(sketch, "E827", {"start": v(-15.35, -14.55) * mm, "end": v(-15.25, -14.54) * mm});
            skLineSegment(sketch, "E828", {"start": v(-15.25, -14.54) * mm, "end": v(-15.15, -14.53) * mm});
            skLineSegment(sketch, "E829", {"start": v(-15.15, -14.53) * mm, "end": v(-15.05, -14.52) * mm});
            skLineSegment(sketch, "E830", {"start": v(-15.05, -14.52) * mm, "end": v(-14.95, -14.5) * mm});
            skLineSegment(sketch, "E831", {"start": v(-14.95, -14.5) * mm, "end": v(-14.84, -14.5) * mm});
            skLineSegment(sketch, "E832", {"start": v(-14.84, -14.5) * mm, "end": v(-14.74, -14.49) * mm});
            skLineSegment(sketch, "E833", {"start": v(-14.74, -14.49) * mm, "end": v(-14.64, -14.48) * mm});
            skLineSegment(sketch, "E834", {"start": v(-14.64, -14.48) * mm, "end": v(-14.54, -14.47) * mm});
            skLineSegment(sketch, "E835", {"start": v(-14.54, -14.47) * mm, "end": v(-14.44, -14.46) * mm});
            skLineSegment(sketch, "E836", {"start": v(-14.44, -14.46) * mm, "end": v(-14.33, -14.45) * mm});
            skLineSegment(sketch, "E837", {"start": v(-14.33, -14.45) * mm, "end": v(-14.23, -14.44) * mm});
            skLineSegment(sketch, "E838", {"start": v(-14.23, -14.44) * mm, "end": v(-14.13, -14.43) * mm});
            skLineSegment(sketch, "E839", {"start": v(-14.13, -14.43) * mm, "end": v(-14.03, -14.42) * mm});
            skLineSegment(sketch, "E840", {"start": v(-14.03, -14.42) * mm, "end": v(-13.93, -14.4) * mm});
            skLineSegment(sketch, "E841", {"start": v(-13.93, -14.4) * mm, "end": v(-13.83, -14.4) * mm});
            skLineSegment(sketch, "E842", {"start": v(-13.83, -14.4) * mm, "end": v(-13.72, -14.38) * mm});
            skLineSegment(sketch, "E843", {"start": v(-13.72, -14.38) * mm, "end": v(-13.62, -14.37) * mm});
            skLineSegment(sketch, "E844", {"start": v(-13.62, -14.37) * mm, "end": v(-13.52, -14.36) * mm});
            skLineSegment(sketch, "E845", {"start": v(-13.52, -14.36) * mm, "end": v(-13.42, -14.35) * mm});
            skLineSegment(sketch, "E846", {"start": v(-13.42, -14.35) * mm, "end": v(-13.32, -14.34) * mm});
            skLineSegment(sketch, "E847", {"start": v(-13.32, -14.34) * mm, "end": v(-13.22, -14.33) * mm});
            skLineSegment(sketch, "E848", {"start": v(-13.22, -14.33) * mm, "end": v(-13.12, -14.32) * mm});
            skLineSegment(sketch, "E849", {"start": v(-13.12, -14.32) * mm, "end": v(-13.02, -14.32) * mm});
            skLineSegment(sketch, "E850", {"start": v(-13.02, -14.32) * mm, "end": v(-12.92, -14.3) * mm});
            skLineSegment(sketch, "E851", {"start": v(-12.92, -14.3) * mm, "end": v(-12.82, -14.3) * mm});
            skLineSegment(sketch, "E852", {"start": v(-12.82, -14.3) * mm, "end": v(-12.72, -14.29) * mm});
            skLineSegment(sketch, "E853", {"start": v(-12.72, -14.29) * mm, "end": v(-12.62, -14.28) * mm});
            skLineSegment(sketch, "E854", {"start": v(-12.62, -14.28) * mm, "end": v(-12.52, -14.27) * mm});
            skLineSegment(sketch, "E855", {"start": v(-12.52, -14.27) * mm, "end": v(-12.42, -14.26) * mm});
            skLineSegment(sketch, "E856", {"start": v(-12.42, -14.26) * mm, "end": v(-12.32, -14.26) * mm});
            skLineSegment(sketch, "E857", {"start": v(-12.32, -14.26) * mm, "end": v(-12.21, -14.25) * mm});
            skLineSegment(sketch, "E858", {"start": v(-12.21, -14.25) * mm, "end": v(-12.11, -14.24) * mm});
            skLineSegment(sketch, "E859", {"start": v(-12.11, -14.24) * mm, "end": v(-12.01, -14.23) * mm});
            skLineSegment(sketch, "E860", {"start": v(-12.01, -14.23) * mm, "end": v(-11.91, -14.23) * mm});
            skLineSegment(sketch, "E861", {"start": v(-11.91, -14.23) * mm, "end": v(-11.81, -14.22) * mm});
            skLineSegment(sketch, "E862", {"start": v(-11.81, -14.22) * mm, "end": v(-11.7, -14.21) * mm});
            skLineSegment(sketch, "E863", {"start": v(-11.7, -14.21) * mm, "end": v(-11.6, -14.2) * mm});
            skLineSegment(sketch, "E864", {"start": v(-11.6, -14.2) * mm, "end": v(-11.5, -14.2) * mm});
            skLineSegment(sketch, "E865", {"start": v(-11.5, -14.2) * mm, "end": v(-11.4, -14.2) * mm});
            skLineSegment(sketch, "E866", {"start": v(-11.4, -14.2) * mm, "end": v(-11.3, -14.2) * mm});
            skLineSegment(sketch, "E867", {"start": v(-11.3, -14.2) * mm, "end": v(-11.2, -14.19) * mm});
            skLineSegment(sketch, "E868", {"start": v(-11.2, -14.19) * mm, "end": v(-11.1, -14.18) * mm});
            skLineSegment(sketch, "E869", {"start": v(-11.1, -14.18) * mm, "end": v(-11, -14.18) * mm});
            skLineSegment(sketch, "E870", {"start": v(-11, -14.18) * mm, "end": v(-10.9, -14.17) * mm});
            skLineSegment(sketch, "E871", {"start": v(-10.9, -14.17) * mm, "end": v(-10.8, -14.17) * mm});
            skLineSegment(sketch, "E872", {"start": v(-10.8, -14.17) * mm, "end": v(-10.7, -14.16) * mm});
            skLineSegment(sketch, "E873", {"start": v(-10.7, -14.16) * mm, "end": v(-10.6, -14.16) * mm});
            skLineSegment(sketch, "E874", {"start": v(-10.6, -14.16) * mm, "end": v(-10.49, -14.15) * mm});
            skLineSegment(sketch, "E875", {"start": v(-10.49, -14.15) * mm, "end": v(-10.39, -14.15) * mm});
            skLineSegment(sketch, "E876", {"start": v(-10.39, -14.15) * mm, "end": v(-10.28, -14.15) * mm});
            skLineSegment(sketch, "E877", {"start": v(-10.28, -14.15) * mm, "end": v(-10.18, -14.14) * mm});
            skLineSegment(sketch, "E878", {"start": v(-10.18, -14.14) * mm, "end": v(-10.08, -14.14) * mm});
            skLineSegment(sketch, "E879", {"start": v(-10.08, -14.14) * mm, "end": v(-9.98, -14.14) * mm});
            skLineSegment(sketch, "E880", {"start": v(-9.98, -14.14) * mm, "end": v(-9.88, -14.13) * mm});
            skLineSegment(sketch, "E881", {"start": v(-9.88, -14.13) * mm, "end": v(-9.77, -14.13) * mm});
            skLineSegment(sketch, "E882", {"start": v(-9.77, -14.13) * mm, "end": v(-9.67, -14.13) * mm});
            skLineSegment(sketch, "E883", {"start": v(-9.67, -14.13) * mm, "end": v(-9.57, -14.13) * mm});
            skLineSegment(sketch, "E884", {"start": v(-9.57, -14.13) * mm, "end": v(-9.47, -14.12) * mm});
            skLineSegment(sketch, "E885", {"start": v(-9.47, -14.12) * mm, "end": v(-9.36, -14.12) * mm});
            skLineSegment(sketch, "E886", {"start": v(-9.36, -14.12) * mm, "end": v(-9.26, -14.12) * mm});
            skLineSegment(sketch, "E887", {"start": v(-9.26, -14.12) * mm, "end": v(-9.16, -14.12) * mm});
            skLineSegment(sketch, "E888", {"start": v(-9.16, -14.12) * mm, "end": v(-9.06, -14.12) * mm});
            skLineSegment(sketch, "E889", {"start": v(-9.06, -14.12) * mm, "end": v(-8.95, -14.11) * mm});
            skLineSegment(sketch, "E890", {"start": v(-8.95, -14.11) * mm, "end": v(-8.85, -14.11) * mm});
            skLineSegment(sketch, "E891", {"start": v(-8.85, -14.11) * mm, "end": v(-8.75, -14.11) * mm});
            skLineSegment(sketch, "E892", {"start": v(-8.75, -14.11) * mm, "end": v(-8.65, -14.11) * mm});
            skLineSegment(sketch, "E893", {"start": v(-8.65, -14.11) * mm, "end": v(-8.54, -14.1) * mm});
            skLineSegment(sketch, "E894", {"start": v(-8.54, -14.1) * mm, "end": v(-8.44, -14.1) * mm});
            skLineSegment(sketch, "E895", {"start": v(-8.44, -14.1) * mm, "end": v(-8.34, -14.1) * mm});
            skLineSegment(sketch, "E896", {"start": v(-8.34, -14.1) * mm, "end": v(-8.24, -14.1) * mm});
            skLineSegment(sketch, "E897", {"start": v(-8.24, -14.1) * mm, "end": v(-8.13, -14.1) * mm});
            skLineSegment(sketch, "E898", {"start": v(-8.13, -14.1) * mm, "end": v(-8.03, -14.1) * mm});
            skLineSegment(sketch, "E899", {"start": v(-8.03, -14.1) * mm, "end": v(-7.93, -14.1) * mm});
            skLineSegment(sketch, "E900", {"start": v(-7.93, -14.1) * mm, "end": v(-7.82, -14.1) * mm});
            skLineSegment(sketch, "E901", {"start": v(-7.82, -14.1) * mm, "end": v(-7.72, -14.1) * mm});
            skLineSegment(sketch, "E902", {"start": v(-7.72, -14.1) * mm, "end": v(-7.62, -14.1) * mm});
            skLineSegment(sketch, "E903", {"start": v(-7.62, -14.1) * mm, "end": v(-7.52, -14.1) * mm});
            skLineSegment(sketch, "E904", {"start": v(-7.52, -14.1) * mm, "end": v(-7.41, -14.1) * mm});
            skLineSegment(sketch, "E905", {"start": v(-7.41, -14.1) * mm, "end": v(-7.3, -14.11) * mm});
            skLineSegment(sketch, "E906", {"start": v(-7.3, -14.11) * mm, "end": v(-7.2, -14.11) * mm});
            skLineSegment(sketch, "E907", {"start": v(-7.2, -14.11) * mm, "end": v(-7.1, -14.11) * mm});
            skLineSegment(sketch, "E908", {"start": v(-7.1, -14.11) * mm, "end": v(-7, -14.11) * mm});
            skLineSegment(sketch, "E909", {"start": v(-7, -14.11) * mm, "end": v(-6.9, -14.11) * mm});
            skLineSegment(sketch, "E910", {"start": v(-6.9, -14.11) * mm, "end": v(-6.8, -14.12) * mm});
            skLineSegment(sketch, "E911", {"start": v(-6.8, -14.12) * mm, "end": v(-6.7, -14.12) * mm});
            skLineSegment(sketch, "E912", {"start": v(-6.7, -14.12) * mm, "end": v(-6.59, -14.12) * mm});
            skLineSegment(sketch, "E913", {"start": v(-6.59, -14.12) * mm, "end": v(-6.49, -14.12) * mm});
            skLineSegment(sketch, "E914", {"start": v(-6.49, -14.12) * mm, "end": v(-6.38, -14.12) * mm});
            skLineSegment(sketch, "E915", {"start": v(-6.38, -14.12) * mm, "end": v(-6.28, -14.13) * mm});
            skLineSegment(sketch, "E916", {"start": v(-6.28, -14.13) * mm, "end": v(-6.18, -14.13) * mm});
            skLineSegment(sketch, "E917", {"start": v(-6.18, -14.13) * mm, "end": v(-6.07, -14.13) * mm});
            skLineSegment(sketch, "E918", {"start": v(-6.07, -14.13) * mm, "end": v(-5.97, -14.13) * mm});
            skLineSegment(sketch, "E919", {"start": v(-5.97, -14.13) * mm, "end": v(-5.87, -14.13) * mm});
            skLineSegment(sketch, "E920", {"start": v(-5.87, -14.13) * mm, "end": v(-5.76, -14.14) * mm});
            skLineSegment(sketch, "E921", {"start": v(-5.76, -14.14) * mm, "end": v(-5.66, -14.14) * mm});
            skLineSegment(sketch, "E922", {"start": v(-5.66, -14.14) * mm, "end": v(-5.56, -14.14) * mm});
            skLineSegment(sketch, "E923", {"start": v(-5.56, -14.14) * mm, "end": v(-5.45, -14.14) * mm});
            skLineSegment(sketch, "E924", {"start": v(-5.45, -14.14) * mm, "end": v(-5.35, -14.15) * mm});
            skLineSegment(sketch, "E925", {"start": v(-5.35, -14.15) * mm, "end": v(-5.25, -14.15) * mm});
            skLineSegment(sketch, "E926", {"start": v(-5.25, -14.15) * mm, "end": v(-5.14, -14.15) * mm});
            skLineSegment(sketch, "E927", {"start": v(-5.14, -14.15) * mm, "end": v(-5.04, -14.16) * mm});
            skLineSegment(sketch, "E928", {"start": v(-5.04, -14.16) * mm, "end": v(-4.94, -14.16) * mm});
            skLineSegment(sketch, "E929", {"start": v(-4.94, -14.16) * mm, "end": v(-4.83, -14.16) * mm});
            skLineSegment(sketch, "E930", {"start": v(-4.83, -14.16) * mm, "end": v(-4.73, -14.17) * mm});
            skLineSegment(sketch, "E931", {"start": v(-4.73, -14.17) * mm, "end": v(-4.63, -14.17) * mm});
            skLineSegment(sketch, "E932", {"start": v(-4.63, -14.17) * mm, "end": v(-4.52, -14.17) * mm});
            skLineSegment(sketch, "E933", {"start": v(-4.52, -14.17) * mm, "end": v(-4.42, -14.18) * mm});
            skLineSegment(sketch, "E934", {"start": v(-4.42, -14.18) * mm, "end": v(-4.32, -14.18) * mm});
            skLineSegment(sketch, "E935", {"start": v(-4.32, -14.18) * mm, "end": v(-4.21, -14.18) * mm});
            skLineSegment(sketch, "E936", {"start": v(-4.21, -14.18) * mm, "end": v(-4.11, -14.19) * mm});
            skLineSegment(sketch, "E937", {"start": v(-4.11, -14.19) * mm, "end": v(-4, -14.2) * mm});
            skLineSegment(sketch, "E938", {"start": v(-4, -14.2) * mm, "end": v(-3.9, -14.2) * mm});
            skLineSegment(sketch, "E939", {"start": v(-3.9, -14.2) * mm, "end": v(-3.8, -14.2) * mm});
            skLineSegment(sketch, "E940", {"start": v(-3.8, -14.2) * mm, "end": v(-3.7, -14.2) * mm});
            skLineSegment(sketch, "E941", {"start": v(-3.7, -14.2) * mm, "end": v(-3.6, -14.2) * mm});
            skLineSegment(sketch, "E942", {"start": v(-3.6, -14.2) * mm, "end": v(-3.5, -14.21) * mm});
            skLineSegment(sketch, "E943", {"start": v(-3.5, -14.21) * mm, "end": v(-3.39, -14.22) * mm});
            skLineSegment(sketch, "E944", {"start": v(-3.39, -14.22) * mm, "end": v(-3.29, -14.22) * mm});
            skLineSegment(sketch, "E945", {"start": v(-3.29, -14.22) * mm, "end": v(-3.18, -14.23) * mm});
            skLineSegment(sketch, "E946", {"start": v(-3.18, -14.23) * mm, "end": v(-3.08, -14.23) * mm});
            skLineSegment(sketch, "E947", {"start": v(-3.08, -14.23) * mm, "end": v(-2.98, -14.23) * mm});
            skLineSegment(sketch, "E948", {"start": v(-2.98, -14.23) * mm, "end": v(-2.87, -14.24) * mm});
            skLineSegment(sketch, "E949", {"start": v(-2.87, -14.24) * mm, "end": v(-2.77, -14.24) * mm});
            skLineSegment(sketch, "E950", {"start": v(-2.77, -14.24) * mm, "end": v(-2.67, -14.25) * mm});
            skLineSegment(sketch, "E951", {"start": v(-2.67, -14.25) * mm, "end": v(-2.56, -14.25) * mm});
            skLineSegment(sketch, "E952", {"start": v(-2.56, -14.25) * mm, "end": v(-2.46, -14.26) * mm});
            skLineSegment(sketch, "E953", {"start": v(-2.46, -14.26) * mm, "end": v(-2.36, -14.26) * mm});
            skLineSegment(sketch, "E954", {"start": v(-2.36, -14.26) * mm, "end": v(-2.25, -14.27) * mm});
            skLineSegment(sketch, "E955", {"start": v(-2.25, -14.27) * mm, "end": v(-2.15, -14.27) * mm});
            skLineSegment(sketch, "E956", {"start": v(-2.15, -14.27) * mm, "end": v(-2.05, -14.28) * mm});
            skLineSegment(sketch, "E957", {"start": v(-2.05, -14.28) * mm, "end": v(-1.95, -14.28) * mm});
            skLineSegment(sketch, "E958", {"start": v(-1.95, -14.28) * mm, "end": v(-1.84, -14.29) * mm});
            skLineSegment(sketch, "E959", {"start": v(-1.84, -14.29) * mm, "end": v(-1.74, -14.3) * mm});
            skLineSegment(sketch, "E960", {"start": v(-1.74, -14.3) * mm, "end": v(-1.64, -14.3) * mm});
            skLineSegment(sketch, "E961", {"start": v(-1.64, -14.3) * mm, "end": v(-1.53, -14.3) * mm});
            skLineSegment(sketch, "E962", {"start": v(-1.53, -14.3) * mm, "end": v(-1.43, -14.3) * mm});
            skLineSegment(sketch, "E963", {"start": v(-1.43, -14.3) * mm, "end": v(-1.33, -14.3) * mm});
            skLineSegment(sketch, "E964", {"start": v(-1.33, -14.3) * mm, "end": v(-1.23, -14.31) * mm});
            skLineSegment(sketch, "E965", {"start": v(-1.23, -14.31) * mm, "end": v(-1.12, -14.32) * mm});
            skLineSegment(sketch, "E966", {"start": v(-1.12, -14.32) * mm, "end": v(-1.02, -14.32) * mm});
            skLineSegment(sketch, "E967", {"start": v(-1.02, -14.32) * mm, "end": v(-0.92, -14.33) * mm});
            skLineSegment(sketch, "E968", {"start": v(-0.92, -14.33) * mm, "end": v(-0.81, -14.33) * mm});
            skLineSegment(sketch, "E969", {"start": v(-0.81, -14.33) * mm, "end": v(-0.71, -14.34) * mm});
            skLineSegment(sketch, "E970", {"start": v(-0.71, -14.34) * mm, "end": v(-0.6, -14.34) * mm});
            skLineSegment(sketch, "E971", {"start": v(-0.6, -14.34) * mm, "end": v(-0.5, -14.35) * mm});
            skLineSegment(sketch, "E972", {"start": v(-0.5, -14.35) * mm, "end": v(-0.4, -14.35) * mm});
            skLineSegment(sketch, "E973", {"start": v(-0.4, -14.35) * mm, "end": v(-0.3, -14.36) * mm});
            skLineSegment(sketch, "E974", {"start": v(-0.3, -14.36) * mm, "end": v(-0.2, -14.36) * mm});
            skLineSegment(sketch, "E975", {"start": v(-0.2, -14.36) * mm, "end": v(-0.1, -14.37) * mm});
            skLineSegment(sketch, "E976", {"start": v(-0.1, -14.37) * mm, "end": v(0, -14.37) * mm});
            skLineSegment(sketch, "E977", {"start": v(0, -14.37) * mm, "end": v(0.1, -14.38) * mm});
            skLineSegment(sketch, "E978", {"start": v(0.1, -14.38) * mm, "end": v(0.21, -14.38) * mm});
            skLineSegment(sketch, "E979", {"start": v(0.21, -14.38) * mm, "end": v(0.31, -14.39) * mm});
            skLineSegment(sketch, "E980", {"start": v(0.31, -14.39) * mm, "end": v(0.42, -14.4) * mm});
            skLineSegment(sketch, "E981", {"start": v(0.42, -14.4) * mm, "end": v(0.52, -14.4) * mm});
            skLineSegment(sketch, "E982", {"start": v(0.52, -14.4) * mm, "end": v(0.62, -14.4) * mm});
            skLineSegment(sketch, "E983", {"start": v(0.62, -14.4) * mm, "end": v(0.72, -14.4) * mm});
            skLineSegment(sketch, "E984", {"start": v(0.72, -14.4) * mm, "end": v(0.82, -14.41) * mm});
            skLineSegment(sketch, "E985", {"start": v(0.82, -14.41) * mm, "end": v(0.93, -14.42) * mm});
            skLineSegment(sketch, "E986", {"start": v(0.93, -14.42) * mm, "end": v(1.03, -14.42) * mm});
            skLineSegment(sketch, "E987", {"start": v(1.03, -14.42) * mm, "end": v(1.13, -14.43) * mm});
            skLineSegment(sketch, "E988", {"start": v(1.13, -14.43) * mm, "end": v(1.23, -14.43) * mm});
            skLineSegment(sketch, "E989", {"start": v(1.23, -14.43) * mm, "end": v(1.33, -14.44) * mm});
            skLineSegment(sketch, "E990", {"start": v(1.33, -14.44) * mm, "end": v(1.44, -14.44) * mm});
            skLineSegment(sketch, "E991", {"start": v(1.44, -14.44) * mm, "end": v(1.54, -14.45) * mm});
            skLineSegment(sketch, "E992", {"start": v(1.54, -14.45) * mm, "end": v(1.64, -14.45) * mm});
            skLineSegment(sketch, "E993", {"start": v(1.64, -14.45) * mm, "end": v(1.74, -14.46) * mm});
            skLineSegment(sketch, "E994", {"start": v(1.74, -14.46) * mm, "end": v(1.84, -14.46) * mm});
            skLineSegment(sketch, "E995", {"start": v(1.84, -14.46) * mm, "end": v(1.94, -14.46) * mm});
            skLineSegment(sketch, "E996", {"start": v(1.94, -14.46) * mm, "end": v(2.05, -14.47) * mm});
            skLineSegment(sketch, "E997", {"start": v(2.05, -14.47) * mm, "end": v(2.15, -14.47) * mm});
            skLineSegment(sketch, "E998", {"start": v(2.15, -14.47) * mm, "end": v(2.25, -14.48) * mm});
            skLineSegment(sketch, "E999", {"start": v(2.25, -14.48) * mm, "end": v(2.35, -14.48) * mm});
            skLineSegment(sketch, "E1000", {"start": v(2.35, -14.48) * mm, "end": v(2.45, -14.49) * mm});
            skLineSegment(sketch, "E1001", {"start": v(2.45, -14.49) * mm, "end": v(2.55, -14.5) * mm});
            skLineSegment(sketch, "E1002", {"start": v(2.55, -14.5) * mm, "end": v(2.65, -14.5) * mm});
            skLineSegment(sketch, "E1003", {"start": v(2.65, -14.5) * mm, "end": v(2.76, -14.5) * mm});
            skLineSegment(sketch, "E1004", {"start": v(2.76, -14.5) * mm, "end": v(2.86, -14.5) * mm});
            skLineSegment(sketch, "E1005", {"start": v(2.86, -14.5) * mm, "end": v(2.96, -14.5) * mm});
            skLineSegment(sketch, "E1006", {"start": v(2.96, -14.5) * mm, "end": v(3.06, -14.51) * mm});
            skLineSegment(sketch, "E1007", {"start": v(3.06, -14.51) * mm, "end": v(3.16, -14.51) * mm});
            skLineSegment(sketch, "E1008", {"start": v(3.16, -14.51) * mm, "end": v(3.26, -14.52) * mm});
            skLineSegment(sketch, "E1009", {"start": v(3.26, -14.52) * mm, "end": v(3.36, -14.52) * mm});
            skLineSegment(sketch, "E1010", {"start": v(3.36, -14.52) * mm, "end": v(3.46, -14.53) * mm});
            skLineSegment(sketch, "E1011", {"start": v(3.46, -14.53) * mm, "end": v(3.56, -14.53) * mm});
            skLineSegment(sketch, "E1012", {"start": v(3.56, -14.53) * mm, "end": v(3.66, -14.53) * mm});
            skLineSegment(sketch, "E1013", {"start": v(3.66, -14.53) * mm, "end": v(3.76, -14.54) * mm});
            skLineSegment(sketch, "E1014", {"start": v(3.76, -14.54) * mm, "end": v(3.86, -14.54) * mm});
            skLineSegment(sketch, "E1015", {"start": v(3.86, -14.54) * mm, "end": v(3.96, -14.54) * mm});
            skLineSegment(sketch, "E1016", {"start": v(3.96, -14.54) * mm, "end": v(4.06, -14.55) * mm});
            skLineSegment(sketch, "E1017", {"start": v(4.06, -14.55) * mm, "end": v(4.17, -14.55) * mm});
            skLineSegment(sketch, "E1018", {"start": v(4.17, -14.55) * mm, "end": v(4.27, -14.55) * mm});
            skLineSegment(sketch, "E1019", {"start": v(4.27, -14.55) * mm, "end": v(4.37, -14.55) * mm});
            skLineSegment(sketch, "E1020", {"start": v(4.37, -14.55) * mm, "end": v(4.47, -14.56) * mm});
            skLineSegment(sketch, "E1021", {"start": v(4.47, -14.56) * mm, "end": v(4.57, -14.56) * mm});
            skLineSegment(sketch, "E1022", {"start": v(4.57, -14.56) * mm, "end": v(4.67, -14.56) * mm});
            skLineSegment(sketch, "E1023", {"start": v(4.67, -14.56) * mm, "end": v(4.77, -14.57) * mm});
            skLineSegment(sketch, "E1024", {"start": v(4.77, -14.57) * mm, "end": v(4.87, -14.57) * mm});
            skLineSegment(sketch, "E1025", {"start": v(4.87, -14.57) * mm, "end": v(4.97, -14.57) * mm});
            skLineSegment(sketch, "E1026", {"start": v(4.97, -14.57) * mm, "end": v(5.07, -14.57) * mm});
            skLineSegment(sketch, "E1027", {"start": v(5.07, -14.57) * mm, "end": v(5.17, -14.58) * mm});
            skLineSegment(sketch, "E1028", {"start": v(5.17, -14.58) * mm, "end": v(5.28, -14.58) * mm});
            skLineSegment(sketch, "E1029", {"start": v(5.28, -14.58) * mm, "end": v(5.38, -14.58) * mm});
            skLineSegment(sketch, "E1030", {"start": v(5.38, -14.58) * mm, "end": v(5.48, -14.58) * mm});
            skLineSegment(sketch, "E1031", {"start": v(5.48, -14.58) * mm, "end": v(5.58, -14.59) * mm});
            skLineSegment(sketch, "E1032", {"start": v(5.58, -14.59) * mm, "end": v(5.68, -14.59) * mm});
            skLineSegment(sketch, "E1033", {"start": v(5.68, -14.59) * mm, "end": v(5.78, -14.6) * mm});
            skLineSegment(sketch, "E1034", {"start": v(5.78, -14.6) * mm, "end": v(5.88, -14.6) * mm});
            skLineSegment(sketch, "E1035", {"start": v(5.88, -14.6) * mm, "end": v(5.98, -14.6) * mm});
            skLineSegment(sketch, "E1036", {"start": v(5.98, -14.6) * mm, "end": v(6.08, -14.6) * mm});
            skLineSegment(sketch, "E1037", {"start": v(6.08, -14.6) * mm, "end": v(6.18, -14.6) * mm});
            skLineSegment(sketch, "E1038", {"start": v(6.18, -14.6) * mm, "end": v(6.29, -14.6) * mm});
            skLineSegment(sketch, "E1039", {"start": v(6.29, -14.6) * mm, "end": v(6.39, -14.6) * mm});
            skLineSegment(sketch, "E1040", {"start": v(6.39, -14.6) * mm, "end": v(6.49, -14.6) * mm});
            skLineSegment(sketch, "E1041", {"start": v(6.49, -14.6) * mm, "end": v(6.59, -14.6) * mm});
            skLineSegment(sketch, "E1042", {"start": v(6.59, -14.6) * mm, "end": v(6.69, -14.6) * mm});
            skLineSegment(sketch, "E1043", {"start": v(6.69, -14.6) * mm, "end": v(6.8, -14.6) * mm});
            skLineSegment(sketch, "E1044", {"start": v(6.8, -14.6) * mm, "end": v(6.9, -14.6) * mm});
            skLineSegment(sketch, "E1045", {"start": v(6.9, -14.6) * mm, "end": v(7, -14.6) * mm});
            skLineSegment(sketch, "E1046", {"start": v(7, -14.6) * mm, "end": v(7.1, -14.6) * mm});
            skLineSegment(sketch, "E1047", {"start": v(7.1, -14.6) * mm, "end": v(7.2, -14.6) * mm});
            skLineSegment(sketch, "E1048", {"start": v(7.2, -14.6) * mm, "end": v(7.3, -14.6) * mm});
            skLineSegment(sketch, "E1049", {"start": v(7.3, -14.6) * mm, "end": v(7.4, -14.6) * mm});
            skLineSegment(sketch, "E1050", {"start": v(7.4, -14.6) * mm, "end": v(7.5, -14.6) * mm});
            skLineSegment(sketch, "E1051", {"start": v(7.5, -14.6) * mm, "end": v(7.6, -14.6) * mm});
            skLineSegment(sketch, "E1052", {"start": v(7.6, -14.6) * mm, "end": v(7.7, -14.6) * mm});
            skLineSegment(sketch, "E1053", {"start": v(7.7, -14.6) * mm, "end": v(7.8, -14.6) * mm});
            skLineSegment(sketch, "E1054", {"start": v(7.8, -14.6) * mm, "end": v(7.9, -14.6) * mm});
            skLineSegment(sketch, "E1055", {"start": v(7.9, -14.6) * mm, "end": v(8, -14.6) * mm});
            skLineSegment(sketch, "E1056", {"start": v(8, -14.6) * mm, "end": v(8.1, -14.6) * mm});
            skLineSegment(sketch, "E1057", {"start": v(8.1, -14.6) * mm, "end": v(8.2, -14.6) * mm});
            skLineSegment(sketch, "E1058", {"start": v(8.2, -14.6) * mm, "end": v(8.3, -14.6) * mm});
            skLineSegment(sketch, "E1059", {"start": v(8.3, -14.6) * mm, "end": v(8.4, -14.59) * mm});
            skLineSegment(sketch, "E1060", {"start": v(8.4, -14.59) * mm, "end": v(8.5, -14.59) * mm});
            skLineSegment(sketch, "E1061", {"start": v(8.5, -14.59) * mm, "end": v(8.6, -14.58) * mm});
            skLineSegment(sketch, "E1062", {"start": v(8.6, -14.58) * mm, "end": v(8.7, -14.58) * mm});
            skLineSegment(sketch, "E1063", {"start": v(8.7, -14.58) * mm, "end": v(8.8, -14.57) * mm});
            skLineSegment(sketch, "E1064", {"start": v(8.8, -14.57) * mm, "end": v(8.9, -14.57) * mm});
            skLineSegment(sketch, "E1065", {"start": v(8.9, -14.57) * mm, "end": v(9, -14.57) * mm});
            skLineSegment(sketch, "E1066", {"start": v(9, -14.57) * mm, "end": v(9.1, -14.56) * mm});
            skLineSegment(sketch, "E1067", {"start": v(9.1, -14.56) * mm, "end": v(9.2, -14.56) * mm});
            skLineSegment(sketch, "E1068", {"start": v(9.2, -14.56) * mm, "end": v(9.3, -14.55) * mm});
            skLineSegment(sketch, "E1069", {"start": v(9.3, -14.55) * mm, "end": v(9.4, -14.55) * mm});
            skLineSegment(sketch, "E1070", {"start": v(9.4, -14.55) * mm, "end": v(9.5, -14.54) * mm});
            skLineSegment(sketch, "E1071", {"start": v(9.5, -14.54) * mm, "end": v(9.6, -14.53) * mm});
            skLineSegment(sketch, "E1072", {"start": v(9.6, -14.53) * mm, "end": v(9.7, -14.53) * mm});
            skLineSegment(sketch, "E1073", {"start": v(9.7, -14.53) * mm, "end": v(9.8, -14.52) * mm});
            skLineSegment(sketch, "E1074", {"start": v(9.8, -14.52) * mm, "end": v(9.9, -14.51) * mm});
            skLineSegment(sketch, "E1075", {"start": v(9.9, -14.51) * mm, "end": v(10, -14.5) * mm});
            skLineSegment(sketch, "E1076", {"start": v(10, -14.5) * mm, "end": v(10.1, -14.5) * mm});
            skLineSegment(sketch, "E1077", {"start": v(10.1, -14.5) * mm, "end": v(10.2, -14.49) * mm});
            skLineSegment(sketch, "E1078", {"start": v(10.2, -14.49) * mm, "end": v(10.3, -14.48) * mm});
            skLineSegment(sketch, "E1079", {"start": v(10.3, -14.48) * mm, "end": v(10.4, -14.47) * mm});
            skLineSegment(sketch, "E1080", {"start": v(10.4, -14.47) * mm, "end": v(10.5, -14.46) * mm});
            skLineSegment(sketch, "E1081", {"start": v(10.5, -14.46) * mm, "end": v(10.6, -14.45) * mm});
            skLineSegment(sketch, "E1082", {"start": v(10.6, -14.45) * mm, "end": v(10.7, -14.44) * mm});
            skLineSegment(sketch, "E1083", {"start": v(10.7, -14.44) * mm, "end": v(10.8, -14.43) * mm});
            skLineSegment(sketch, "E1084", {"start": v(10.8, -14.43) * mm, "end": v(10.9, -14.42) * mm});
            skLineSegment(sketch, "E1085", {"start": v(10.9, -14.42) * mm, "end": v(11, -14.4) * mm});
            skLineSegment(sketch, "E1086", {"start": v(11, -14.4) * mm, "end": v(11.1, -14.4) * mm});
            skLineSegment(sketch, "E1087", {"start": v(11.1, -14.4) * mm, "end": v(11.2, -14.38) * mm});
            skLineSegment(sketch, "E1088", {"start": v(11.2, -14.38) * mm, "end": v(11.3, -14.37) * mm});
            skLineSegment(sketch, "E1089", {"start": v(11.3, -14.37) * mm, "end": v(11.4, -14.36) * mm});
            skLineSegment(sketch, "E1090", {"start": v(11.4, -14.36) * mm, "end": v(11.5, -14.35) * mm});
            skLineSegment(sketch, "E1091", {"start": v(11.5, -14.35) * mm, "end": v(11.6, -14.33) * mm});
            skLineSegment(sketch, "E1092", {"start": v(11.6, -14.33) * mm, "end": v(11.7, -14.32) * mm});
            skLineSegment(sketch, "E1093", {"start": v(11.7, -14.32) * mm, "end": v(11.8, -14.3) * mm});
            skLineSegment(sketch, "E1094", {"start": v(11.8, -14.3) * mm, "end": v(11.9, -14.29) * mm});
            skLineSegment(sketch, "E1095", {"start": v(11.9, -14.29) * mm, "end": v(12, -14.27) * mm});
            skLineSegment(sketch, "E1096", {"start": v(12, -14.27) * mm, "end": v(12.1, -14.26) * mm});
            skLineSegment(sketch, "E1097", {"start": v(12.1, -14.26) * mm, "end": v(12.2, -14.24) * mm});
            skLineSegment(sketch, "E1098", {"start": v(12.2, -14.24) * mm, "end": v(12.3, -14.22) * mm});
            skLineSegment(sketch, "E1099", {"start": v(12.3, -14.22) * mm, "end": v(12.39, -14.2) * mm});
            skLineSegment(sketch, "E1100", {"start": v(12.39, -14.2) * mm, "end": v(12.49, -14.19) * mm});
            skLineSegment(sketch, "E1101", {"start": v(12.49, -14.19) * mm, "end": v(12.59, -14.17) * mm});
            skLineSegment(sketch, "E1102", {"start": v(12.59, -14.17) * mm, "end": v(12.68, -14.15) * mm});
            skLineSegment(sketch, "E1103", {"start": v(12.68, -14.15) * mm, "end": v(12.78, -14.13) * mm});
            skLineSegment(sketch, "E1104", {"start": v(12.78, -14.13) * mm, "end": v(12.88, -14.1) * mm});
            skLineSegment(sketch, "E1105", {"start": v(12.88, -14.1) * mm, "end": v(12.98, -14.09) * mm});
            skLineSegment(sketch, "E1106", {"start": v(12.98, -14.09) * mm, "end": v(13.08, -14.07) * mm});
            skLineSegment(sketch, "E1107", {"start": v(13.08, -14.07) * mm, "end": v(13.17, -14.05) * mm});
            skLineSegment(sketch, "E1108", {"start": v(13.17, -14.05) * mm, "end": v(13.27, -14.02) * mm});
            skLineSegment(sketch, "E1109", {"start": v(13.27, -14.02) * mm, "end": v(13.37, -14) * mm});
            skLineSegment(sketch, "E1110", {"start": v(13.37, -14) * mm, "end": v(13.47, -13.98) * mm});
            skLineSegment(sketch, "E1111", {"start": v(13.47, -13.98) * mm, "end": v(13.56, -13.95) * mm});
            skLineSegment(sketch, "E1112", {"start": v(13.56, -13.95) * mm, "end": v(13.66, -13.93) * mm});
            skLineSegment(sketch, "E1113", {"start": v(13.66, -13.93) * mm, "end": v(13.76, -13.9) * mm});
            skLineSegment(sketch, "E1114", {"start": v(13.76, -13.9) * mm, "end": v(13.85, -13.88) * mm});
            skLineSegment(sketch, "E1115", {"start": v(13.85, -13.88) * mm, "end": v(13.95, -13.85) * mm});
            skLineSegment(sketch, "E1116", {"start": v(13.95, -13.85) * mm, "end": v(14.05, -13.83) * mm});
            skLineSegment(sketch, "E1117", {"start": v(14.05, -13.83) * mm, "end": v(14.14, -13.8) * mm});
            skLineSegment(sketch, "E1118", {"start": v(14.14, -13.8) * mm, "end": v(14.24, -13.77) * mm});
            skLineSegment(sketch, "E1119", {"start": v(14.24, -13.77) * mm, "end": v(14.34, -13.74) * mm});
            skLineSegment(sketch, "E1120", {"start": v(14.34, -13.74) * mm, "end": v(14.43, -13.71) * mm});
            skLineSegment(sketch, "E1121", {"start": v(14.43, -13.71) * mm, "end": v(14.53, -13.68) * mm});
            skLineSegment(sketch, "E1122", {"start": v(14.53, -13.68) * mm, "end": v(14.63, -13.65) * mm});
            skLineSegment(sketch, "E1123", {"start": v(14.63, -13.65) * mm, "end": v(14.72, -13.62) * mm});
            skLineSegment(sketch, "E1124", {"start": v(14.72, -13.62) * mm, "end": v(14.82, -13.6) * mm});
            skLineSegment(sketch, "E1125", {"start": v(14.82, -13.6) * mm, "end": v(14.91, -13.56) * mm});
            skLineSegment(sketch, "E1126", {"start": v(14.91, -13.56) * mm, "end": v(15, -13.53) * mm});
            skLineSegment(sketch, "E1127", {"start": v(15, -13.53) * mm, "end": v(15.1, -13.5) * mm});
            skLineSegment(sketch, "E1128", {"start": v(15.1, -13.5) * mm, "end": v(15.2, -13.46) * mm});
            skLineSegment(sketch, "E1129", {"start": v(15.2, -13.46) * mm, "end": v(15.3, -13.42) * mm});
            skLineSegment(sketch, "E1130", {"start": v(15.3, -13.42) * mm, "end": v(15.4, -13.39) * mm});
            skLineSegment(sketch, "E1131", {"start": v(15.4, -13.39) * mm, "end": v(15.49, -13.35) * mm});
            skLineSegment(sketch, "E1132", {"start": v(15.49, -13.35) * mm, "end": v(15.58, -13.32) * mm});
            skLineSegment(sketch, "E1133", {"start": v(15.58, -13.32) * mm, "end": v(15.68, -13.28) * mm});
            skLineSegment(sketch, "E1134", {"start": v(15.68, -13.28) * mm, "end": v(15.77, -13.24) * mm});
            skLineSegment(sketch, "E1135", {"start": v(15.77, -13.24) * mm, "end": v(15.86, -13.2) * mm});
            skLineSegment(sketch, "E1136", {"start": v(15.86, -13.2) * mm, "end": v(15.96, -13.16) * mm});
            skLineSegment(sketch, "E1137", {"start": v(15.96, -13.16) * mm, "end": v(16.05, -13.12) * mm});
            skLineSegment(sketch, "E1138", {"start": v(16.05, -13.12) * mm, "end": v(16.15, -13.08) * mm});
            skLineSegment(sketch, "E1139", {"start": v(16.15, -13.08) * mm, "end": v(16.24, -13.04) * mm});
            skLineSegment(sketch, "E1140", {"start": v(16.24, -13.04) * mm, "end": v(16.33, -13) * mm});
            skLineSegment(sketch, "E1141", {"start": v(16.33, -13) * mm, "end": v(16.43, -12.96) * mm});
            skLineSegment(sketch, "E1142", {"start": v(16.43, -12.96) * mm, "end": v(16.52, -12.91) * mm});
            skLineSegment(sketch, "E1143", {"start": v(16.52, -12.91) * mm, "end": v(16.62, -12.87) * mm});
            skLineSegment(sketch, "E1144", {"start": v(16.62, -12.87) * mm, "end": v(16.7, -12.82) * mm});
            skLineSegment(sketch, "E1145", {"start": v(16.7, -12.82) * mm, "end": v(16.76, -12.8) * mm});
            skLineSegment(sketch, "E1146", {"start": v(16.76, -12.8) * mm, "end": v(16.82, -12.77) * mm});
            skLineSegment(sketch, "E1147", {"start": v(16.82, -12.77) * mm, "end": v(16.88, -12.74) * mm});
            skLineSegment(sketch, "E1148", {"start": v(16.88, -12.74) * mm, "end": v(16.95, -12.7) * mm});
            skLineSegment(sketch, "E1149", {"start": v(16.95, -12.7) * mm, "end": v(17.01, -12.67) * mm});
            skLineSegment(sketch, "E1150", {"start": v(17.01, -12.67) * mm, "end": v(17.08, -12.63) * mm});
            skLineSegment(sketch, "E1151", {"start": v(17.08, -12.63) * mm, "end": v(17.15, -12.6) * mm});
            skLineSegment(sketch, "E1152", {"start": v(17.15, -12.6) * mm, "end": v(17.22, -12.56) * mm});
            skLineSegment(sketch, "E1153", {"start": v(17.22, -12.56) * mm, "end": v(17.3, -12.52) * mm});
            skLineSegment(sketch, "E1154", {"start": v(17.3, -12.52) * mm, "end": v(17.37, -12.47) * mm});
            skLineSegment(sketch, "E1155", {"start": v(17.37, -12.47) * mm, "end": v(17.45, -12.43) * mm});
            skLineSegment(sketch, "E1156", {"start": v(17.45, -12.43) * mm, "end": v(17.53, -12.39) * mm});
            skLineSegment(sketch, "E1157", {"start": v(17.53, -12.39) * mm, "end": v(17.6, -12.34) * mm});
            skLineSegment(sketch, "E1158", {"start": v(17.6, -12.34) * mm, "end": v(17.69, -12.3) * mm});
            skLineSegment(sketch, "E1159", {"start": v(17.69, -12.3) * mm, "end": v(17.77, -12.24) * mm});
            skLineSegment(sketch, "E1160", {"start": v(17.77, -12.24) * mm, "end": v(17.85, -12.2) * mm});
            skLineSegment(sketch, "E1161", {"start": v(17.85, -12.2) * mm, "end": v(17.94, -12.14) * mm});
            skLineSegment(sketch, "E1162", {"start": v(17.94, -12.14) * mm, "end": v(18.03, -12.08) * mm});
            skLineSegment(sketch, "E1163", {"start": v(18.03, -12.08) * mm, "end": v(18.11, -12.03) * mm});
            skLineSegment(sketch, "E1164", {"start": v(18.11, -12.03) * mm, "end": v(18.2, -11.97) * mm});
            skLineSegment(sketch, "E1165", {"start": v(18.2, -11.97) * mm, "end": v(18.29, -11.92) * mm});
            skLineSegment(sketch, "E1166", {"start": v(18.29, -11.92) * mm, "end": v(18.37, -11.86) * mm});
            skLineSegment(sketch, "E1167", {"start": v(18.37, -11.86) * mm, "end": v(18.46, -11.8) * mm});
            skLineSegment(sketch, "E1168", {"start": v(18.46, -11.8) * mm, "end": v(18.55, -11.74) * mm});
            skLineSegment(sketch, "E1169", {"start": v(18.55, -11.74) * mm, "end": v(18.64, -11.68) * mm});
            skLineSegment(sketch, "E1170", {"start": v(18.64, -11.68) * mm, "end": v(18.73, -11.61) * mm});
            skLineSegment(sketch, "E1171", {"start": v(18.73, -11.61) * mm, "end": v(18.82, -11.55) * mm});
            skLineSegment(sketch, "E1172", {"start": v(18.82, -11.55) * mm, "end": v(18.9, -11.49) * mm});
            skLineSegment(sketch, "E1173", {"start": v(18.9, -11.49) * mm, "end": v(19, -11.42) * mm});
            skLineSegment(sketch, "E1174", {"start": v(19, -11.42) * mm, "end": v(19.08, -11.36) * mm});
            skLineSegment(sketch, "E1175", {"start": v(19.08, -11.36) * mm, "end": v(19.17, -11.29) * mm});
            skLineSegment(sketch, "E1176", {"start": v(19.17, -11.29) * mm, "end": v(19.25, -11.22) * mm});
            skLineSegment(sketch, "E1177", {"start": v(19.25, -11.22) * mm, "end": v(19.34, -11.15) * mm});
            skLineSegment(sketch, "E1178", {"start": v(19.34, -11.15) * mm, "end": v(19.42, -11.08) * mm});
            skLineSegment(sketch, "E1179", {"start": v(19.42, -11.08) * mm, "end": v(19.5, -11.01) * mm});
            skLineSegment(sketch, "E1180", {"start": v(19.5, -11.01) * mm, "end": v(19.58, -10.94) * mm});
            skLineSegment(sketch, "E1181", {"start": v(19.58, -10.94) * mm, "end": v(19.66, -10.87) * mm});
            skLineSegment(sketch, "E1182", {"start": v(19.66, -10.87) * mm, "end": v(19.74, -10.8) * mm});
            skLineSegment(sketch, "E1183", {"start": v(19.74, -10.8) * mm, "end": v(19.82, -10.72) * mm});
            skLineSegment(sketch, "E1184", {"start": v(19.82, -10.72) * mm, "end": v(19.9, -10.65) * mm});
            skLineSegment(sketch, "E1185", {"start": v(19.9, -10.65) * mm, "end": v(19.97, -10.58) * mm});
            skLineSegment(sketch, "E1186", {"start": v(19.97, -10.58) * mm, "end": v(20.04, -10.5) * mm});
            skLineSegment(sketch, "E1187", {"start": v(20.04, -10.5) * mm, "end": v(20.1, -10.43) * mm});
            skLineSegment(sketch, "E1188", {"start": v(20.1, -10.43) * mm, "end": v(20.18, -10.35) * mm});
            skLineSegment(sketch, "E1189", {"start": v(20.18, -10.35) * mm, "end": v(20.24, -10.28) * mm});
            skLineSegment(sketch, "E1190", {"start": v(20.24, -10.28) * mm, "end": v(20.3, -10.2) * mm});
            skLineSegment(sketch, "E1191", {"start": v(20.3, -10.2) * mm, "end": v(20.36, -10.13) * mm});
            skLineSegment(sketch, "E1192", {"start": v(20.36, -10.13) * mm, "end": v(20.42, -10.05) * mm});
            skLineSegment(sketch, "E1193", {"start": v(20.42, -10.05) * mm, "end": v(20.48, -9.97) * mm});
            skLineSegment(sketch, "E1194", {"start": v(20.48, -9.97) * mm, "end": v(20.53, -9.9) * mm});
            skLineSegment(sketch, "E1195", {"start": v(20.53, -9.9) * mm, "end": v(20.58, -9.82) * mm});
            skLineSegment(sketch, "E1196", {"start": v(20.58, -9.82) * mm, "end": v(20.62, -9.74) * mm});
            skLineSegment(sketch, "E1197", {"start": v(20.62, -9.74) * mm, "end": v(20.66, -9.66) * mm});
            skLineSegment(sketch, "E1198", {"start": v(20.66, -9.66) * mm, "end": v(20.7, -9.59) * mm});
            skLineSegment(sketch, "E1199", {"start": v(20.7, -9.59) * mm, "end": v(20.74, -9.51) * mm});
            skLineSegment(sketch, "E1200", {"start": v(20.74, -9.51) * mm, "end": v(20.77, -9.43) * mm});
            skLineSegment(sketch, "E1201", {"start": v(20.77, -9.43) * mm, "end": v(20.8, -9.36) * mm});
            skLineSegment(sketch, "E1202", {"start": v(20.8, -9.36) * mm, "end": v(20.82, -9.28) * mm});
            skLineSegment(sketch, "E1203", {"start": v(20.82, -9.28) * mm, "end": v(20.84, -9.2) * mm});
            skLineSegment(sketch, "E1204", {"start": v(20.84, -9.2) * mm, "end": v(20.86, -9.12) * mm});
            skLineSegment(sketch, "E1205", {"start": v(20.86, -9.12) * mm, "end": v(20.87, -9.05) * mm});
            skLineSegment(sketch, "E1206", {"start": v(20.87, -9.05) * mm, "end": v(20.88, -8.97) * mm});
            skLineSegment(sketch, "E1207", {"start": v(20.88, -8.97) * mm, "end": v(20.88, -8.9) * mm});
            skLineSegment(sketch, "E1208", {"start": v(20.88, -8.9) * mm, "end": v(20.88, -8.82) * mm});
            skLineSegment(sketch, "E1209", {"start": v(20.88, -8.82) * mm, "end": v(20.87, -8.74) * mm});
            skLineSegment(sketch, "E1210", {"start": v(20.87, -8.74) * mm, "end": v(20.86, -8.67) * mm});
            skLineSegment(sketch, "E1211", {"start": v(20.86, -8.67) * mm, "end": v(20.85, -8.59) * mm});
            skLineSegment(sketch, "E1212", {"start": v(20.85, -8.59) * mm, "end": v(20.83, -8.51) * mm});
            skLineSegment(sketch, "E1213", {"start": v(20.83, -8.51) * mm, "end": v(20.8, -8.44) * mm});
            skLineSegment(sketch, "E1214", {"start": v(20.8, -8.44) * mm, "end": v(20.76, -8.37) * mm});
            skLineSegment(sketch, "E1215", {"start": v(20.76, -8.37) * mm, "end": v(20.72, -8.3) * mm});
            skLineSegment(sketch, "E1216", {"start": v(20.72, -8.3) * mm, "end": v(20.67, -8.24) * mm});
            skLineSegment(sketch, "E1217", {"start": v(20.67, -8.24) * mm, "end": v(20.62, -8.17) * mm});
            skLineSegment(sketch, "E1218", {"start": v(20.62, -8.17) * mm, "end": v(20.56, -8.12) * mm});
            skLineSegment(sketch, "E1219", {"start": v(20.56, -8.12) * mm, "end": v(20.5, -8.06) * mm});
            skLineSegment(sketch, "E1220", {"start": v(20.5, -8.06) * mm, "end": v(20.43, -8) * mm});
            skLineSegment(sketch, "E1221", {"start": v(20.43, -8) * mm, "end": v(20.36, -7.95) * mm});
            skLineSegment(sketch, "E1222", {"start": v(20.36, -7.95) * mm, "end": v(20.28, -7.9) * mm});
            skLineSegment(sketch, "E1223", {"start": v(20.28, -7.9) * mm, "end": v(20.2, -7.86) * mm});
            skLineSegment(sketch, "E1224", {"start": v(20.2, -7.86) * mm, "end": v(20.12, -7.81) * mm});
            skLineSegment(sketch, "E1225", {"start": v(20.12, -7.81) * mm, "end": v(20.03, -7.77) * mm});
            skLineSegment(sketch, "E1226", {"start": v(20.03, -7.77) * mm, "end": v(19.94, -7.73) * mm});
            skLineSegment(sketch, "E1227", {"start": v(19.94, -7.73) * mm, "end": v(19.85, -7.69) * mm});
            skLineSegment(sketch, "E1228", {"start": v(19.85, -7.69) * mm, "end": v(19.75, -7.65) * mm});
            skLineSegment(sketch, "E1229", {"start": v(19.75, -7.65) * mm, "end": v(19.65, -7.62) * mm});
            skLineSegment(sketch, "E1230", {"start": v(19.65, -7.62) * mm, "end": v(19.56, -7.58) * mm});
            skLineSegment(sketch, "E1231", {"start": v(19.56, -7.58) * mm, "end": v(19.46, -7.55) * mm});
            skLineSegment(sketch, "E1232", {"start": v(19.46, -7.55) * mm, "end": v(19.35, -7.52) * mm});
            skLineSegment(sketch, "E1233", {"start": v(19.35, -7.52) * mm, "end": v(19.25, -7.49) * mm});
            skLineSegment(sketch, "E1234", {"start": v(19.25, -7.49) * mm, "end": v(19.15, -7.46) * mm});
            skLineSegment(sketch, "E1235", {"start": v(19.15, -7.46) * mm, "end": v(19.05, -7.43) * mm});
            skLineSegment(sketch, "E1236", {"start": v(19.05, -7.43) * mm, "end": v(18.94, -7.4) * mm});
            skLineSegment(sketch, "E1237", {"start": v(18.94, -7.4) * mm, "end": v(18.84, -7.37) * mm});
            skLineSegment(sketch, "E1238", {"start": v(18.84, -7.37) * mm, "end": v(18.74, -7.35) * mm});
            skLineSegment(sketch, "E1239", {"start": v(18.74, -7.35) * mm, "end": v(18.64, -7.32) * mm});
            skLineSegment(sketch, "E1240", {"start": v(18.64, -7.32) * mm, "end": v(18.54, -7.3) * mm});
            skLineSegment(sketch, "E1241", {"start": v(18.54, -7.3) * mm, "end": v(18.44, -7.27) * mm});
            skLineSegment(sketch, "E1242", {"start": v(18.44, -7.27) * mm, "end": v(18.35, -7.25) * mm});
            skLineSegment(sketch, "E1243", {"start": v(18.35, -7.25) * mm, "end": v(18.25, -7.22) * mm});
            skLineSegment(sketch, "E1244", {"start": v(18.25, -7.22) * mm, "end": v(18.16, -7.2) * mm});
            skLineSegment(sketch, "E1245", {"start": v(18.16, -7.2) * mm, "end": v(18.08, -7.18) * mm});
            skLineSegment(sketch, "E1246", {"start": v(18.08, -7.18) * mm, "end": v(17.99, -7.15) * mm});
            skLineSegment(sketch, "E1247", {"start": v(17.99, -7.15) * mm, "end": v(17.9, -7.13) * mm});
            skLineSegment(sketch, "E1248", {"start": v(17.9, -7.13) * mm, "end": v(17.83, -7.1) * mm});
            skLineSegment(sketch, "E1249", {"start": v(17.83, -7.1) * mm, "end": v(17.76, -7.08) * mm});
            skLineSegment(sketch, "E1250", {"start": v(17.76, -7.08) * mm, "end": v(17.69, -7.05) * mm});
            skLineSegment(sketch, "E1251", {"start": v(17.69, -7.05) * mm, "end": v(17.62, -7.03) * mm});
            skLineSegment(sketch, "E1252", {"start": v(17.62, -7.03) * mm, "end": v(17.54, -7) * mm});
            skLineSegment(sketch, "E1253", {"start": v(17.54, -7) * mm, "end": v(17.46, -6.95) * mm});
            skLineSegment(sketch, "E1254", {"start": v(17.46, -6.95) * mm, "end": v(17.38, -6.92) * mm});
            skLineSegment(sketch, "E1255", {"start": v(17.38, -6.92) * mm, "end": v(17.3, -6.88) * mm});
            skLineSegment(sketch, "E1256", {"start": v(17.3, -6.88) * mm, "end": v(17.22, -6.83) * mm});
            skLineSegment(sketch, "E1257", {"start": v(17.22, -6.83) * mm, "end": v(17.14, -6.8) * mm});
            skLineSegment(sketch, "E1258", {"start": v(17.14, -6.8) * mm, "end": v(17.06, -6.75) * mm});
            skLineSegment(sketch, "E1259", {"start": v(17.06, -6.75) * mm, "end": v(16.98, -6.7) * mm});
            skLineSegment(sketch, "E1260", {"start": v(16.98, -6.7) * mm, "end": v(16.9, -6.65) * mm});
            skLineSegment(sketch, "E1261", {"start": v(16.9, -6.65) * mm, "end": v(16.82, -6.6) * mm});
            skLineSegment(sketch, "E1262", {"start": v(16.82, -6.6) * mm, "end": v(16.74, -6.55) * mm});
            skLineSegment(sketch, "E1263", {"start": v(16.74, -6.55) * mm, "end": v(16.66, -6.5) * mm});
            skLineSegment(sketch, "E1264", {"start": v(16.66, -6.5) * mm, "end": v(16.58, -6.45) * mm});
            skLineSegment(sketch, "E1265", {"start": v(16.58, -6.45) * mm, "end": v(16.5, -6.4) * mm});
            skLineSegment(sketch, "E1266", {"start": v(16.5, -6.4) * mm, "end": v(16.43, -6.34) * mm});
            skLineSegment(sketch, "E1267", {"start": v(16.43, -6.34) * mm, "end": v(16.35, -6.28) * mm});
            skLineSegment(sketch, "E1268", {"start": v(16.35, -6.28) * mm, "end": v(16.27, -6.22) * mm});
            skLineSegment(sketch, "E1269", {"start": v(16.27, -6.22) * mm, "end": v(16.2, -6.16) * mm});
            skLineSegment(sketch, "E1270", {"start": v(16.2, -6.16) * mm, "end": v(16.12, -6.1) * mm});
            skLineSegment(sketch, "E1271", {"start": v(16.12, -6.1) * mm, "end": v(16.05, -6.04) * mm});
            skLineSegment(sketch, "E1272", {"start": v(16.05, -6.04) * mm, "end": v(15.97, -5.97) * mm});
            skLineSegment(sketch, "E1273", {"start": v(15.97, -5.97) * mm, "end": v(15.9, -5.9) * mm});
            skLineSegment(sketch, "E1274", {"start": v(15.9, -5.9) * mm, "end": v(15.83, -5.84) * mm});
            skLineSegment(sketch, "E1275", {"start": v(15.83, -5.84) * mm, "end": v(15.75, -5.77) * mm});
            skLineSegment(sketch, "E1276", {"start": v(15.75, -5.77) * mm, "end": v(15.68, -5.7) * mm});
            skLineSegment(sketch, "E1277", {"start": v(15.68, -5.7) * mm, "end": v(15.61, -5.63) * mm});
            skLineSegment(sketch, "E1278", {"start": v(15.61, -5.63) * mm, "end": v(15.54, -5.56) * mm});
            skLineSegment(sketch, "E1279", {"start": v(15.54, -5.56) * mm, "end": v(15.48, -5.5) * mm});
            skLineSegment(sketch, "E1280", {"start": v(15.48, -5.5) * mm, "end": v(15.4, -5.42) * mm});
            skLineSegment(sketch, "E1281", {"start": v(15.4, -5.42) * mm, "end": v(15.34, -5.35) * mm});
            skLineSegment(sketch, "E1282", {"start": v(15.34, -5.35) * mm, "end": v(15.28, -5.27) * mm});
            skLineSegment(sketch, "E1283", {"start": v(15.28, -5.27) * mm, "end": v(15.21, -5.2) * mm});
            skLineSegment(sketch, "E1284", {"start": v(15.21, -5.2) * mm, "end": v(15.15, -5.12) * mm});
            skLineSegment(sketch, "E1285", {"start": v(15.15, -5.12) * mm, "end": v(15.09, -5.04) * mm});
            skLineSegment(sketch, "E1286", {"start": v(15.09, -5.04) * mm, "end": v(15.02, -4.96) * mm});
            skLineSegment(sketch, "E1287", {"start": v(15.02, -4.96) * mm, "end": v(14.96, -4.88) * mm});
            skLineSegment(sketch, "E1288", {"start": v(14.96, -4.88) * mm, "end": v(14.9, -4.8) * mm});
            skLineSegment(sketch, "E1289", {"start": v(14.9, -4.8) * mm, "end": v(14.85, -4.72) * mm});
            skLineSegment(sketch, "E1290", {"start": v(14.85, -4.72) * mm, "end": v(14.8, -4.64) * mm});
            skLineSegment(sketch, "E1291", {"start": v(14.8, -4.64) * mm, "end": v(14.74, -4.56) * mm});
            skLineSegment(sketch, "E1292", {"start": v(14.74, -4.56) * mm, "end": v(14.68, -4.48) * mm});
            skLineSegment(sketch, "E1293", {"start": v(14.68, -4.48) * mm, "end": v(14.63, -4.4) * mm});
            skLineSegment(sketch, "E1294", {"start": v(14.63, -4.4) * mm, "end": v(14.58, -4.3) * mm});
            skLineSegment(sketch, "E1295", {"start": v(14.58, -4.3) * mm, "end": v(14.53, -4.22) * mm});
            skLineSegment(sketch, "E1296", {"start": v(14.53, -4.22) * mm, "end": v(14.48, -4.14) * mm});
            skLineSegment(sketch, "E1297", {"start": v(14.48, -4.14) * mm, "end": v(14.44, -4.05) * mm});
            skLineSegment(sketch, "E1298", {"start": v(14.44, -4.05) * mm, "end": v(14.4, -3.96) * mm});
            skLineSegment(sketch, "E1299", {"start": v(14.4, -3.96) * mm, "end": v(14.35, -3.87) * mm});
            skLineSegment(sketch, "E1300", {"start": v(14.35, -3.87) * mm, "end": v(14.3, -3.79) * mm});
            skLineSegment(sketch, "E1301", {"start": v(14.3, -3.79) * mm, "end": v(14.27, -3.7) * mm});
            skLineSegment(sketch, "E1302", {"start": v(14.27, -3.7) * mm, "end": v(14.23, -3.6) * mm});
            skLineSegment(sketch, "E1303", {"start": v(14.23, -3.6) * mm, "end": v(14.2, -3.52) * mm});
            skLineSegment(sketch, "E1304", {"start": v(14.2, -3.52) * mm, "end": v(14.16, -3.43) * mm});
            skLineSegment(sketch, "E1305", {"start": v(14.16, -3.43) * mm, "end": v(14.13, -3.34) * mm});
            skLineSegment(sketch, "E1306", {"start": v(14.13, -3.34) * mm, "end": v(14.1, -3.25) * mm});
            skLineSegment(sketch, "E1307", {"start": v(14.1, -3.25) * mm, "end": v(14.07, -3.15) * mm});
            skLineSegment(sketch, "E1308", {"start": v(14.07, -3.15) * mm, "end": v(14.04, -3.06) * mm});
            skLineSegment(sketch, "E1309", {"start": v(14.04, -3.06) * mm, "end": v(14.01, -2.97) * mm});
            skLineSegment(sketch, "E1310", {"start": v(14.01, -2.97) * mm, "end": v(14, -2.88) * mm});
            skLineSegment(sketch, "E1311", {"start": v(14, -2.88) * mm, "end": v(13.97, -2.78) * mm});
            skLineSegment(sketch, "E1312", {"start": v(13.97, -2.78) * mm, "end": v(13.95, -2.7) * mm});
            skLineSegment(sketch, "E1313", {"start": v(13.95, -2.7) * mm, "end": v(13.93, -2.6) * mm});
            skLineSegment(sketch, "E1314", {"start": v(13.93, -2.6) * mm, "end": v(13.92, -2.5) * mm});
            skLineSegment(sketch, "E1315", {"start": v(13.92, -2.5) * mm, "end": v(13.9, -2.4) * mm});
            skLineSegment(sketch, "E1316", {"start": v(13.9, -2.4) * mm, "end": v(13.9, -2.32) * mm});
            skLineSegment(sketch, "E1317", {"start": v(13.9, -2.32) * mm, "end": v(13.88, -2.22) * mm});
            skLineSegment(sketch, "E1318", {"start": v(13.88, -2.22) * mm, "end": v(13.88, -2.13) * mm});
            skLineSegment(sketch, "E1319", {"start": v(13.88, -2.13) * mm, "end": v(13.87, -2.03) * mm});
            skLineSegment(sketch, "E1320", {"start": v(13.87, -2.03) * mm, "end": v(13.87, -1.94) * mm});
            skLineSegment(sketch, "E1321", {"start": v(13.87, -1.94) * mm, "end": v(13.87, -1.84) * mm});
            skLineSegment(sketch, "E1322", {"start": v(13.87, -1.84) * mm, "end": v(13.88, -1.75) * mm});
            skLineSegment(sketch, "E1323", {"start": v(13.88, -1.75) * mm, "end": v(13.88, -1.65) * mm});
            skLineSegment(sketch, "E1324", {"start": v(13.88, -1.65) * mm, "end": v(13.89, -1.56) * mm});
            skLineSegment(sketch, "E1325", {"start": v(13.89, -1.56) * mm, "end": v(13.9, -1.46) * mm});
            skLineSegment(sketch, "E1326", {"start": v(13.9, -1.46) * mm, "end": v(13.91, -1.39) * mm});
            skLineSegment(sketch, "E1327", {"start": v(13.91, -1.39) * mm, "end": v(13.93, -1.3) * mm});
            skLineSegment(sketch, "E1328", {"start": v(13.93, -1.3) * mm, "end": v(13.95, -1.23) * mm});
            skLineSegment(sketch, "E1329", {"start": v(13.95, -1.23) * mm, "end": v(13.97, -1.15) * mm});
            skLineSegment(sketch, "E1330", {"start": v(13.97, -1.15) * mm, "end": v(14, -1.06) * mm});
            skLineSegment(sketch, "E1331", {"start": v(14, -1.06) * mm, "end": v(14.03, -0.98) * mm});
            skLineSegment(sketch, "E1332", {"start": v(14.03, -0.98) * mm, "end": v(14.06, -0.9) * mm});
            skLineSegment(sketch, "E1333", {"start": v(14.06, -0.9) * mm, "end": v(14.1, -0.82) * mm});
            skLineSegment(sketch, "E1334", {"start": v(14.1, -0.82) * mm, "end": v(14.14, -0.73) * mm});
            skLineSegment(sketch, "E1335", {"start": v(14.14, -0.73) * mm, "end": v(14.19, -0.65) * mm});
            skLineSegment(sketch, "E1336", {"start": v(14.19, -0.65) * mm, "end": v(14.23, -0.56) * mm});
            skLineSegment(sketch, "E1337", {"start": v(14.23, -0.56) * mm, "end": v(14.28, -0.48) * mm});
            skLineSegment(sketch, "E1338", {"start": v(14.28, -0.48) * mm, "end": v(14.33, -0.39) * mm});
            skLineSegment(sketch, "E1339", {"start": v(14.33, -0.39) * mm, "end": v(14.39, -0.3) * mm});
            skLineSegment(sketch, "E1340", {"start": v(14.39, -0.3) * mm, "end": v(14.44, -0.22) * mm});
            skLineSegment(sketch, "E1341", {"start": v(14.44, -0.22) * mm, "end": v(14.5, -0.13) * mm});
            skLineSegment(sketch, "E1342", {"start": v(14.5, -0.13) * mm, "end": v(14.56, -0.04) * mm});
            skLineSegment(sketch, "E1343", {"start": v(14.56, -0.04) * mm, "end": v(14.63, 0.04) * mm});
            skLineSegment(sketch, "E1344", {"start": v(14.63, 0.04) * mm, "end": v(14.69, 0.13) * mm});
            skLineSegment(sketch, "E1345", {"start": v(14.69, 0.13) * mm, "end": v(14.75, 0.22) * mm});
            skLineSegment(sketch, "E1346", {"start": v(14.75, 0.22) * mm, "end": v(14.82, 0.3) * mm});
            skLineSegment(sketch, "E1347", {"start": v(14.82, 0.3) * mm, "end": v(14.89, 0.4) * mm});
            skLineSegment(sketch, "E1348", {"start": v(14.89, 0.4) * mm, "end": v(14.96, 0.48) * mm});
            skLineSegment(sketch, "E1349", {"start": v(14.96, 0.48) * mm, "end": v(15.03, 0.57) * mm});
            skLineSegment(sketch, "E1350", {"start": v(15.03, 0.57) * mm, "end": v(15.1, 0.65) * mm});
            skLineSegment(sketch, "E1351", {"start": v(15.1, 0.65) * mm, "end": v(15.17, 0.74) * mm});
            skLineSegment(sketch, "E1352", {"start": v(15.17, 0.74) * mm, "end": v(15.24, 0.82) * mm});
            skLineSegment(sketch, "E1353", {"start": v(15.24, 0.82) * mm, "end": v(15.3, 0.91) * mm});
            skLineSegment(sketch, "E1354", {"start": v(15.3, 0.91) * mm, "end": v(15.38, 1) * mm});
            skLineSegment(sketch, "E1355", {"start": v(15.38, 1) * mm, "end": v(15.45, 1.08) * mm});
            skLineSegment(sketch, "E1356", {"start": v(15.45, 1.08) * mm, "end": v(15.52, 1.16) * mm});
            skLineSegment(sketch, "E1357", {"start": v(15.52, 1.16) * mm, "end": v(15.6, 1.25) * mm});
            skLineSegment(sketch, "E1358", {"start": v(15.6, 1.25) * mm, "end": v(15.66, 1.33) * mm});
            skLineSegment(sketch, "E1359", {"start": v(15.66, 1.33) * mm, "end": v(15.73, 1.4) * mm});
            skLineSegment(sketch, "E1360", {"start": v(15.73, 1.4) * mm, "end": v(15.8, 1.49) * mm});
            skLineSegment(sketch, "E1361", {"start": v(15.8, 1.49) * mm, "end": v(15.86, 1.57) * mm});
            skLineSegment(sketch, "E1362", {"start": v(15.86, 1.57) * mm, "end": v(15.93, 1.65) * mm});
            skLineSegment(sketch, "E1363", {"start": v(15.93, 1.65) * mm, "end": v(16, 1.72) * mm});
            skLineSegment(sketch, "E1364", {"start": v(16, 1.72) * mm, "end": v(16.06, 1.8) * mm});
            skLineSegment(sketch, "E1365", {"start": v(16.06, 1.8) * mm, "end": v(16.12, 1.88) * mm});
            skLineSegment(sketch, "E1366", {"start": v(16.12, 1.88) * mm, "end": v(16.18, 1.95) * mm});
            skLineSegment(sketch, "E1367", {"start": v(16.18, 1.95) * mm, "end": v(16.23, 2.02) * mm});
            skLineSegment(sketch, "E1368", {"start": v(16.23, 2.02) * mm, "end": v(16.29, 2.1) * mm});
            skLineSegment(sketch, "E1369", {"start": v(16.29, 2.1) * mm, "end": v(16.34, 2.17) * mm});
            skLineSegment(sketch, "E1370", {"start": v(16.34, 2.17) * mm, "end": v(16.4, 2.24) * mm});
            skLineSegment(sketch, "E1371", {"start": v(16.4, 2.24) * mm, "end": v(16.44, 2.3) * mm});
            skLineSegment(sketch, "E1372", {"start": v(16.44, 2.3) * mm, "end": v(16.48, 2.37) * mm});
            skLineSegment(sketch, "E1373", {"start": v(16.48, 2.37) * mm, "end": v(16.54, 2.45) * mm});
            skLineSegment(sketch, "E1374", {"start": v(16.54, 2.45) * mm, "end": v(16.6, 2.54) * mm});
            skLineSegment(sketch, "E1375", {"start": v(16.6, 2.54) * mm, "end": v(16.65, 2.62) * mm});
            skLineSegment(sketch, "E1376", {"start": v(16.65, 2.62) * mm, "end": v(16.7, 2.7) * mm});
            skLineSegment(sketch, "E1377", {"start": v(16.7, 2.7) * mm, "end": v(16.77, 2.8) * mm});
            skLineSegment(sketch, "E1378", {"start": v(16.77, 2.8) * mm, "end": v(16.82, 2.88) * mm});
            skLineSegment(sketch, "E1379", {"start": v(16.82, 2.88) * mm, "end": v(16.88, 2.96) * mm});
            skLineSegment(sketch, "E1380", {"start": v(16.88, 2.96) * mm, "end": v(16.93, 3.05) * mm});
            skLineSegment(sketch, "E1381", {"start": v(16.93, 3.05) * mm, "end": v(16.99, 3.13) * mm});
            skLineSegment(sketch, "E1382", {"start": v(16.99, 3.13) * mm, "end": v(17.04, 3.22) * mm});
            skLineSegment(sketch, "E1383", {"start": v(17.04, 3.22) * mm, "end": v(17.1, 3.3) * mm});
            skLineSegment(sketch, "E1384", {"start": v(17.1, 3.3) * mm, "end": v(17.16, 3.4) * mm});
            skLineSegment(sketch, "E1385", {"start": v(17.16, 3.4) * mm, "end": v(17.21, 3.48) * mm});
            skLineSegment(sketch, "E1386", {"start": v(17.21, 3.48) * mm, "end": v(17.27, 3.56) * mm});
            skLineSegment(sketch, "E1387", {"start": v(17.27, 3.56) * mm, "end": v(17.32, 3.65) * mm});
            skLineSegment(sketch, "E1388", {"start": v(17.32, 3.65) * mm, "end": v(17.38, 3.73) * mm});
            skLineSegment(sketch, "E1389", {"start": v(17.38, 3.73) * mm, "end": v(17.43, 3.82) * mm});
            skLineSegment(sketch, "E1390", {"start": v(17.43, 3.82) * mm, "end": v(17.49, 3.9) * mm});
            skLineSegment(sketch, "E1391", {"start": v(17.49, 3.9) * mm, "end": v(17.54, 4) * mm});
            skLineSegment(sketch, "E1392", {"start": v(17.54, 4) * mm, "end": v(17.6, 4.08) * mm});
            skLineSegment(sketch, "E1393", {"start": v(17.6, 4.08) * mm, "end": v(17.65, 4.16) * mm});
            skLineSegment(sketch, "E1394", {"start": v(17.65, 4.16) * mm, "end": v(17.7, 4.25) * mm});
            skLineSegment(sketch, "E1395", {"start": v(17.7, 4.25) * mm, "end": v(17.76, 4.34) * mm});
            skLineSegment(sketch, "E1396", {"start": v(17.76, 4.34) * mm, "end": v(17.82, 4.42) * mm});
            skLineSegment(sketch, "E1397", {"start": v(17.82, 4.42) * mm, "end": v(17.87, 4.51) * mm});
            skLineSegment(sketch, "E1398", {"start": v(17.87, 4.51) * mm, "end": v(17.93, 4.6) * mm});
            skLineSegment(sketch, "E1399", {"start": v(17.93, 4.6) * mm, "end": v(17.98, 4.69) * mm});
            skLineSegment(sketch, "E1400", {"start": v(17.98, 4.69) * mm, "end": v(18.03, 4.77) * mm});
            skLineSegment(sketch, "E1401", {"start": v(18.03, 4.77) * mm, "end": v(18.09, 4.86) * mm});
            skLineSegment(sketch, "E1402", {"start": v(18.09, 4.86) * mm, "end": v(18.14, 4.95) * mm});
            skLineSegment(sketch, "E1403", {"start": v(18.14, 4.95) * mm, "end": v(18.2, 5.03) * mm});
            skLineSegment(sketch, "E1404", {"start": v(18.2, 5.03) * mm, "end": v(18.25, 5.12) * mm});
            skLineSegment(sketch, "E1405", {"start": v(18.25, 5.12) * mm, "end": v(18.3, 5.2) * mm});
            skLineSegment(sketch, "E1406", {"start": v(18.3, 5.2) * mm, "end": v(18.36, 5.3) * mm});
            skLineSegment(sketch, "E1407", {"start": v(18.36, 5.3) * mm, "end": v(18.41, 5.38) * mm});
            skLineSegment(sketch, "E1408", {"start": v(18.41, 5.38) * mm, "end": v(18.46, 5.47) * mm});
            skLineSegment(sketch, "E1409", {"start": v(18.46, 5.47) * mm, "end": v(18.52, 5.56) * mm});
            skLineSegment(sketch, "E1410", {"start": v(18.52, 5.56) * mm, "end": v(18.57, 5.65) * mm});
            skLineSegment(sketch, "E1411", {"start": v(18.57, 5.65) * mm, "end": v(18.62, 5.74) * mm});
            skLineSegment(sketch, "E1412", {"start": v(18.62, 5.74) * mm, "end": v(18.68, 5.82) * mm});
            skLineSegment(sketch, "E1413", {"start": v(18.68, 5.82) * mm, "end": v(18.73, 5.91) * mm});
            skLineSegment(sketch, "E1414", {"start": v(18.73, 5.91) * mm, "end": v(18.78, 6) * mm});
            skLineSegment(sketch, "E1415", {"start": v(18.78, 6) * mm, "end": v(18.83, 6.09) * mm});
            skLineSegment(sketch, "E1416", {"start": v(18.83, 6.09) * mm, "end": v(18.88, 6.18) * mm});
            skLineSegment(sketch, "E1417", {"start": v(18.88, 6.18) * mm, "end": v(18.94, 6.27) * mm});
            skLineSegment(sketch, "E1418", {"start": v(18.94, 6.27) * mm, "end": v(18.99, 6.35) * mm});
            skLineSegment(sketch, "E1419", {"start": v(18.99, 6.35) * mm, "end": v(19.04, 6.44) * mm});
            skLineSegment(sketch, "E1420", {"start": v(19.04, 6.44) * mm, "end": v(19.1, 6.53) * mm});
            skLineSegment(sketch, "E1421", {"start": v(19.1, 6.53) * mm, "end": v(19.14, 6.62) * mm});
            skLineSegment(sketch, "E1422", {"start": v(19.14, 6.62) * mm, "end": v(19.2, 6.7) * mm});
            skLineSegment(sketch, "E1423", {"start": v(19.2, 6.7) * mm, "end": v(19.24, 6.8) * mm});
            skLineSegment(sketch, "E1424", {"start": v(19.24, 6.8) * mm, "end": v(19.3, 6.89) * mm});
            skLineSegment(sketch, "E1425", {"start": v(19.3, 6.89) * mm, "end": v(19.35, 6.98) * mm});
            skLineSegment(sketch, "E1426", {"start": v(19.35, 6.98) * mm, "end": v(19.4, 7.07) * mm});
            skLineSegment(sketch, "E1427", {"start": v(19.4, 7.07) * mm, "end": v(19.45, 7.16) * mm});
            skLineSegment(sketch, "E1428", {"start": v(19.45, 7.16) * mm, "end": v(19.5, 7.25) * mm});
            skLineSegment(sketch, "E1429", {"start": v(19.5, 7.25) * mm, "end": v(19.55, 7.33) * mm});
            skLineSegment(sketch, "E1430", {"start": v(19.55, 7.33) * mm, "end": v(19.6, 7.42) * mm});
            skLineSegment(sketch, "E1431", {"start": v(19.6, 7.42) * mm, "end": v(19.65, 7.51) * mm});
            skLineSegment(sketch, "E1432", {"start": v(19.65, 7.51) * mm, "end": v(19.7, 7.6) * mm});
            skLineSegment(sketch, "E1433", {"start": v(19.7, 7.6) * mm, "end": v(19.75, 7.7) * mm});
            skLineSegment(sketch, "E1434", {"start": v(19.75, 7.7) * mm, "end": v(19.8, 7.78) * mm});
            skLineSegment(sketch, "E1435", {"start": v(19.8, 7.78) * mm, "end": v(19.84, 7.87) * mm});
            skLineSegment(sketch, "E1436", {"start": v(19.84, 7.87) * mm, "end": v(19.9, 7.96) * mm});
            skLineSegment(sketch, "E1437", {"start": v(19.9, 7.96) * mm, "end": v(19.94, 8.06) * mm});
            skLineSegment(sketch, "E1438", {"start": v(19.94, 8.06) * mm, "end": v(20, 8.15) * mm});
            skLineSegment(sketch, "E1439", {"start": v(20, 8.15) * mm, "end": v(20.04, 8.24) * mm});
            skLineSegment(sketch, "E1440", {"start": v(20.04, 8.24) * mm, "end": v(20.09, 8.33) * mm});
            skLineSegment(sketch, "E1441", {"start": v(20.09, 8.33) * mm, "end": v(20.13, 8.42) * mm});
            skLineSegment(sketch, "E1442", {"start": v(20.13, 8.42) * mm, "end": v(20.18, 8.5) * mm});
            skLineSegment(sketch, "E1443", {"start": v(20.18, 8.5) * mm, "end": v(20.23, 8.6) * mm});
            skLineSegment(sketch, "E1444", {"start": v(20.23, 8.6) * mm, "end": v(20.28, 8.7) * mm});
            skLineSegment(sketch, "E1445", {"start": v(20.28, 8.7) * mm, "end": v(20.32, 8.78) * mm});
            skLineSegment(sketch, "E1446", {"start": v(20.32, 8.78) * mm, "end": v(20.37, 8.87) * mm});
            skLineSegment(sketch, "E1447", {"start": v(20.37, 8.87) * mm, "end": v(20.42, 8.96) * mm});
            skLineSegment(sketch, "E1448", {"start": v(20.42, 8.96) * mm, "end": v(20.46, 9.06) * mm});
            skLineSegment(sketch, "E1449", {"start": v(20.46, 9.06) * mm, "end": v(20.5, 9.15) * mm});
            skLineSegment(sketch, "E1450", {"start": v(20.5, 9.15) * mm, "end": v(20.56, 9.24) * mm});
            skLineSegment(sketch, "E1451", {"start": v(20.56, 9.24) * mm, "end": v(20.6, 9.33) * mm});
            skLineSegment(sketch, "E1452", {"start": v(20.6, 9.33) * mm, "end": v(20.65, 9.42) * mm});
            skLineSegment(sketch, "E1453", {"start": v(20.65, 9.42) * mm, "end": v(20.7, 9.51) * mm});
            skLineSegment(sketch, "E1454", {"start": v(20.7, 9.51) * mm, "end": v(20.74, 9.6) * mm});
            skLineSegment(sketch, "E1455", {"start": v(20.74, 9.6) * mm, "end": v(20.78, 9.7) * mm});
            skLineSegment(sketch, "E1456", {"start": v(20.78, 9.7) * mm, "end": v(20.83, 9.8) * mm});
            skLineSegment(sketch, "E1457", {"start": v(20.83, 9.8) * mm, "end": v(20.87, 9.88) * mm});
            skLineSegment(sketch, "E1458", {"start": v(20.87, 9.88) * mm, "end": v(20.92, 9.98) * mm});
            skLineSegment(sketch, "E1459", {"start": v(20.92, 9.98) * mm, "end": v(20.96, 10.07) * mm});
            skLineSegment(sketch, "E1460", {"start": v(20.96, 10.07) * mm, "end": v(21, 10.16) * mm});
            skLineSegment(sketch, "E1461", {"start": v(21, 10.16) * mm, "end": v(21.05, 10.25) * mm});
            skLineSegment(sketch, "E1462", {"start": v(21.05, 10.25) * mm, "end": v(21.09, 10.35) * mm});
            skLineSegment(sketch, "E1463", {"start": v(21.09, 10.35) * mm, "end": v(21.13, 10.44) * mm});
            skLineSegment(sketch, "E1464", {"start": v(21.13, 10.44) * mm, "end": v(21.18, 10.53) * mm});
            skLineSegment(sketch, "E1465", {"start": v(21.18, 10.53) * mm, "end": v(21.22, 10.63) * mm});
            skLineSegment(sketch, "E1466", {"start": v(21.22, 10.63) * mm, "end": v(21.26, 10.72) * mm});
            skLineSegment(sketch, "E1467", {"start": v(21.26, 10.72) * mm, "end": v(21.3, 10.81) * mm});
            skLineSegment(sketch, "E1468", {"start": v(21.3, 10.81) * mm, "end": v(21.34, 10.9) * mm});
            skLineSegment(sketch, "E1469", {"start": v(21.34, 10.9) * mm, "end": v(21.39, 11) * mm});
            skLineSegment(sketch, "E1470", {"start": v(21.39, 11) * mm, "end": v(21.43, 11.1) * mm});
            skLineSegment(sketch, "E1471", {"start": v(21.43, 11.1) * mm, "end": v(21.47, 11.19) * mm});
            skLineSegment(sketch, "E1472", {"start": v(21.47, 11.19) * mm, "end": v(21.5, 11.28) * mm});
            skLineSegment(sketch, "E1473", {"start": v(21.5, 11.28) * mm, "end": v(21.55, 11.37) * mm});
            skLineSegment(sketch, "E1474", {"start": v(21.55, 11.37) * mm, "end": v(21.59, 11.47) * mm});
            skLineSegment(sketch, "E1475", {"start": v(21.59, 11.47) * mm, "end": v(21.63, 11.56) * mm});
            skLineSegment(sketch, "E1476", {"start": v(21.63, 11.56) * mm, "end": v(21.67, 11.66) * mm});
            skLineSegment(sketch, "E1477", {"start": v(21.67, 11.66) * mm, "end": v(21.7, 11.75) * mm});
            skLineSegment(sketch, "E1478", {"start": v(21.7, 11.75) * mm, "end": v(21.75, 11.84) * mm});
            skLineSegment(sketch, "E1479", {"start": v(21.75, 11.84) * mm, "end": v(21.79, 11.94) * mm});
            skLineSegment(sketch, "E1480", {"start": v(21.79, 11.94) * mm, "end": v(21.82, 12.03) * mm});
            skLineSegment(sketch, "E1481", {"start": v(21.82, 12.03) * mm, "end": v(21.86, 12.13) * mm});
            skLineSegment(sketch, "E1482", {"start": v(21.86, 12.13) * mm, "end": v(21.9, 12.22) * mm});
            skLineSegment(sketch, "E1483", {"start": v(21.9, 12.22) * mm, "end": v(21.94, 12.32) * mm});
            skLineSegment(sketch, "E1484", {"start": v(21.94, 12.32) * mm, "end": v(21.97, 12.41) * mm});
            skLineSegment(sketch, "E1485", {"start": v(21.97, 12.41) * mm, "end": v(22.01, 12.5) * mm});
            skLineSegment(sketch, "E1486", {"start": v(22.01, 12.5) * mm, "end": v(22.05, 12.6) * mm});
            skLineSegment(sketch, "E1487", {"start": v(22.05, 12.6) * mm, "end": v(22.08, 12.7) * mm});
            skLineSegment(sketch, "E1488", {"start": v(22.08, 12.7) * mm, "end": v(22.12, 12.78) * mm});
            skLineSegment(sketch, "E1489", {"start": v(22.12, 12.78) * mm, "end": v(22.15, 12.87) * mm});
            skLineSegment(sketch, "E1490", {"start": v(22.15, 12.87) * mm, "end": v(22.18, 12.96) * mm});
            skLineSegment(sketch, "E1491", {"start": v(22.18, 12.96) * mm, "end": v(22.22, 13.05) * mm});
            skLineSegment(sketch, "E1492", {"start": v(22.22, 13.05) * mm, "end": v(22.25, 13.14) * mm});
            skLineSegment(sketch, "E1493", {"start": v(22.25, 13.14) * mm, "end": v(22.28, 13.23) * mm});
            skLineSegment(sketch, "E1494", {"start": v(22.28, 13.23) * mm, "end": v(22.32, 13.32) * mm});
            skLineSegment(sketch, "E1495", {"start": v(22.32, 13.32) * mm, "end": v(22.35, 13.41) * mm});
            skLineSegment(sketch, "E1496", {"start": v(22.35, 13.41) * mm, "end": v(22.38, 13.5) * mm});
            skLineSegment(sketch, "E1497", {"start": v(22.38, 13.5) * mm, "end": v(22.42, 13.6) * mm});
            skLineSegment(sketch, "E1498", {"start": v(22.42, 13.6) * mm, "end": v(22.45, 13.7) * mm});
            skLineSegment(sketch, "E1499", {"start": v(22.45, 13.7) * mm, "end": v(22.48, 13.79) * mm});
            skLineSegment(sketch, "E1500", {"start": v(22.48, 13.79) * mm, "end": v(22.52, 13.88) * mm});
            skLineSegment(sketch, "E1501", {"start": v(22.52, 13.88) * mm, "end": v(22.55, 13.98) * mm});
            skLineSegment(sketch, "E1502", {"start": v(22.55, 13.98) * mm, "end": v(22.58, 14.08) * mm});
            skLineSegment(sketch, "E1503", {"start": v(22.58, 14.08) * mm, "end": v(22.6, 14.18) * mm});
            skLineSegment(sketch, "E1504", {"start": v(22.6, 14.18) * mm, "end": v(22.64, 14.27) * mm});
            skLineSegment(sketch, "E1505", {"start": v(22.64, 14.27) * mm, "end": v(22.67, 14.37) * mm});
            skLineSegment(sketch, "E1506", {"start": v(22.67, 14.37) * mm, "end": v(22.7, 14.47) * mm});
            skLineSegment(sketch, "E1507", {"start": v(22.7, 14.47) * mm, "end": v(22.72, 14.57) * mm});
            skLineSegment(sketch, "E1508", {"start": v(22.72, 14.57) * mm, "end": v(22.75, 14.67) * mm});
            skLineSegment(sketch, "E1509", {"start": v(22.75, 14.67) * mm, "end": v(22.78, 14.77) * mm});
            skLineSegment(sketch, "E1510", {"start": v(22.78, 14.77) * mm, "end": v(22.8, 14.87) * mm});
            skLineSegment(sketch, "E1511", {"start": v(22.8, 14.87) * mm, "end": v(22.82, 14.97) * mm});
            skLineSegment(sketch, "E1512", {"start": v(22.82, 14.97) * mm, "end": v(22.85, 15.07) * mm});
            skLineSegment(sketch, "E1513", {"start": v(22.85, 15.07) * mm, "end": v(22.87, 15.17) * mm});
            skLineSegment(sketch, "E1514", {"start": v(22.87, 15.17) * mm, "end": v(22.89, 15.27) * mm});
            skLineSegment(sketch, "E1515", {"start": v(22.89, 15.27) * mm, "end": v(22.9, 15.37) * mm});
            skLineSegment(sketch, "E1516", {"start": v(22.9, 15.37) * mm, "end": v(22.92, 15.47) * mm});
            skLineSegment(sketch, "E1517", {"start": v(22.92, 15.47) * mm, "end": v(22.93, 15.57) * mm});
            skLineSegment(sketch, "E1518", {"start": v(22.93, 15.57) * mm, "end": v(22.95, 15.67) * mm});
            skLineSegment(sketch, "E1519", {"start": v(22.95, 15.67) * mm, "end": v(22.96, 15.77) * mm});
            skLineSegment(sketch, "E1520", {"start": v(22.96, 15.77) * mm, "end": v(22.97, 15.87) * mm});
            skLineSegment(sketch, "E1521", {"start": v(22.97, 15.87) * mm, "end": v(22.98, 15.97) * mm});
            skLineSegment(sketch, "E1522", {"start": v(22.98, 15.97) * mm, "end": v(22.98, 16.07) * mm});
            skLineSegment(sketch, "E1523", {"start": v(22.98, 16.07) * mm, "end": v(22.99, 16.17) * mm});
            skLineSegment(sketch, "E1524", {"start": v(22.99, 16.17) * mm, "end": v(22.99, 16.27) * mm});
            skLineSegment(sketch, "E1525", {"start": v(22.99, 16.27) * mm, "end": v(22.99, 16.37) * mm});
            skLineSegment(sketch, "E1526", {"start": v(22.99, 16.37) * mm, "end": v(22.99, 16.47) * mm});
            skLineSegment(sketch, "E1527", {"start": v(22.99, 16.47) * mm, "end": v(22.98, 16.57) * mm});
            skLineSegment(sketch, "E1528", {"start": v(22.98, 16.57) * mm, "end": v(22.98, 16.66) * mm});
            skLineSegment(sketch, "E1529", {"start": v(22.98, 16.66) * mm, "end": v(22.97, 16.76) * mm});
            skLineSegment(sketch, "E1530", {"start": v(22.97, 16.76) * mm, "end": v(22.95, 16.85) * mm});
            skLineSegment(sketch, "E1531", {"start": v(22.95, 16.85) * mm, "end": v(22.94, 16.95) * mm});
            skLineSegment(sketch, "E1532", {"start": v(22.94, 16.95) * mm, "end": v(22.92, 17.04) * mm});
            skLineSegment(sketch, "E1533", {"start": v(22.92, 17.04) * mm, "end": v(22.9, 17.14) * mm});
            skLineSegment(sketch, "E1534", {"start": v(22.9, 17.14) * mm, "end": v(22.88, 17.23) * mm});
            skLineSegment(sketch, "E1535", {"start": v(22.88, 17.23) * mm, "end": v(22.86, 17.32) * mm});
            skLineSegment(sketch, "E1536", {"start": v(22.86, 17.32) * mm, "end": v(22.83, 17.41) * mm});
            skLineSegment(sketch, "E1537", {"start": v(22.83, 17.41) * mm, "end": v(22.8, 17.5) * mm});
            skLineSegment(sketch, "E1538", {"start": v(22.8, 17.5) * mm, "end": v(22.77, 17.58) * mm});
            skLineSegment(sketch, "E1539", {"start": v(22.77, 17.58) * mm, "end": v(22.74, 17.65) * mm});
            skLineSegment(sketch, "E1540", {"start": v(22.74, 17.65) * mm, "end": v(22.7, 17.72) * mm});
            skLineSegment(sketch, "E1541", {"start": v(22.7, 17.72) * mm, "end": v(22.67, 17.79) * mm});
            skLineSegment(sketch, "E1542", {"start": v(22.67, 17.79) * mm, "end": v(22.63, 17.85) * mm});
            skLineSegment(sketch, "E1543", {"start": v(22.63, 17.85) * mm, "end": v(22.6, 17.91) * mm});
            skLineSegment(sketch, "E1544", {"start": v(22.6, 17.91) * mm, "end": v(22.55, 17.97) * mm});
            skLineSegment(sketch, "E1545", {"start": v(22.55, 17.97) * mm, "end": v(22.51, 18.02) * mm});
            skLineSegment(sketch, "E1546", {"start": v(22.51, 18.02) * mm, "end": v(22.47, 18.08) * mm});
            skLineSegment(sketch, "E1547", {"start": v(22.47, 18.08) * mm, "end": v(22.42, 18.12) * mm});
            skLineSegment(sketch, "E1548", {"start": v(22.42, 18.12) * mm, "end": v(22.37, 18.17) * mm});
            skLineSegment(sketch, "E1549", {"start": v(22.37, 18.17) * mm, "end": v(22.32, 18.2) * mm});
            skLineSegment(sketch, "E1550", {"start": v(22.32, 18.2) * mm, "end": v(22.27, 18.24) * mm});
            skLineSegment(sketch, "E1551", {"start": v(22.27, 18.24) * mm, "end": v(22.22, 18.28) * mm});
            skLineSegment(sketch, "E1552", {"start": v(22.22, 18.28) * mm, "end": v(22.17, 18.3) * mm});
            skLineSegment(sketch, "E1553", {"start": v(22.17, 18.3) * mm, "end": v(22.12, 18.34) * mm});
            skLineSegment(sketch, "E1554", {"start": v(22.12, 18.34) * mm, "end": v(22.06, 18.36) * mm});
            skLineSegment(sketch, "E1555", {"start": v(22.06, 18.36) * mm, "end": v(22, 18.39) * mm});
            skLineSegment(sketch, "E1556", {"start": v(22, 18.39) * mm, "end": v(21.94, 18.4) * mm});
            skLineSegment(sketch, "E1557", {"start": v(21.94, 18.4) * mm, "end": v(21.88, 18.42) * mm});
            skLineSegment(sketch, "E1558", {"start": v(21.88, 18.42) * mm, "end": v(21.82, 18.44) * mm});
            skLineSegment(sketch, "E1559", {"start": v(21.82, 18.44) * mm, "end": v(21.76, 18.45) * mm});
            skLineSegment(sketch, "E1560", {"start": v(21.76, 18.45) * mm, "end": v(21.7, 18.46) * mm});
            skLineSegment(sketch, "E1561", {"start": v(21.7, 18.46) * mm, "end": v(21.63, 18.46) * mm});
            skLineSegment(sketch, "E1562", {"start": v(21.63, 18.46) * mm, "end": v(21.57, 18.47) * mm});
            skLineSegment(sketch, "E1563", {"start": v(21.57, 18.47) * mm, "end": v(21.5, 18.47) * mm});
            skLineSegment(sketch, "E1564", {"start": v(21.5, 18.47) * mm, "end": v(21.44, 18.47) * mm});
            skLineSegment(sketch, "E1565", {"start": v(21.44, 18.47) * mm, "end": v(21.37, 18.46) * mm});
            skLineSegment(sketch, "E1566", {"start": v(21.37, 18.46) * mm, "end": v(21.3, 18.46) * mm});
            skLineSegment(sketch, "E1567", {"start": v(21.3, 18.46) * mm, "end": v(21.23, 18.45) * mm});
            skLineSegment(sketch, "E1568", {"start": v(21.23, 18.45) * mm, "end": v(21.16, 18.44) * mm});
            skLineSegment(sketch, "E1569", {"start": v(21.16, 18.44) * mm, "end": v(21.09, 18.43) * mm});
            skLineSegment(sketch, "E1570", {"start": v(21.09, 18.43) * mm, "end": v(21.01, 18.41) * mm});
            skLineSegment(sketch, "E1571", {"start": v(21.01, 18.41) * mm, "end": v(20.94, 18.4) * mm});
            skLineSegment(sketch, "E1572", {"start": v(20.94, 18.4) * mm, "end": v(20.87, 18.38) * mm});
            skLineSegment(sketch, "E1573", {"start": v(20.87, 18.38) * mm, "end": v(20.8, 18.36) * mm});
            skLineSegment(sketch, "E1574", {"start": v(20.8, 18.36) * mm, "end": v(20.72, 18.33) * mm});
            skLineSegment(sketch, "E1575", {"start": v(20.72, 18.33) * mm, "end": v(20.64, 18.31) * mm});
            skLineSegment(sketch, "E1576", {"start": v(20.64, 18.31) * mm, "end": v(20.56, 18.28) * mm});
            skLineSegment(sketch, "E1577", {"start": v(20.56, 18.28) * mm, "end": v(20.49, 18.26) * mm});
            skLineSegment(sketch, "E1578", {"start": v(20.49, 18.26) * mm, "end": v(20.41, 18.23) * mm});
            skLineSegment(sketch, "E1579", {"start": v(20.41, 18.23) * mm, "end": v(20.33, 18.2) * mm});
            skLineSegment(sketch, "E1580", {"start": v(20.33, 18.2) * mm, "end": v(20.26, 18.16) * mm});
            skLineSegment(sketch, "E1581", {"start": v(20.26, 18.16) * mm, "end": v(20.18, 18.13) * mm});
            skLineSegment(sketch, "E1582", {"start": v(20.18, 18.13) * mm, "end": v(20.1, 18.1) * mm});
            skLineSegment(sketch, "E1583", {"start": v(20.1, 18.1) * mm, "end": v(20.02, 18.06) * mm});
            skLineSegment(sketch, "E1584", {"start": v(20.02, 18.06) * mm, "end": v(19.94, 18.02) * mm});
            skLineSegment(sketch, "E1585", {"start": v(19.94, 18.02) * mm, "end": v(19.86, 17.98) * mm});
            skLineSegment(sketch, "E1586", {"start": v(19.86, 17.98) * mm, "end": v(19.78, 17.94) * mm});
            skLineSegment(sketch, "E1587", {"start": v(19.78, 17.94) * mm, "end": v(19.7, 17.9) * mm});
            skLineSegment(sketch, "E1588", {"start": v(19.7, 17.9) * mm, "end": v(19.62, 17.85) * mm});
            skLineSegment(sketch, "E1589", {"start": v(19.62, 17.85) * mm, "end": v(19.54, 17.8) * mm});
            skLineSegment(sketch, "E1590", {"start": v(19.54, 17.8) * mm, "end": v(19.46, 17.76) * mm});
            skLineSegment(sketch, "E1591", {"start": v(19.46, 17.76) * mm, "end": v(19.38, 17.71) * mm});
            skLineSegment(sketch, "E1592", {"start": v(19.38, 17.71) * mm, "end": v(19.3, 17.66) * mm});
            skLineSegment(sketch, "E1593", {"start": v(19.3, 17.66) * mm, "end": v(19.22, 17.62) * mm});
            skLineSegment(sketch, "E1594", {"start": v(19.22, 17.62) * mm, "end": v(19.14, 17.57) * mm});
            skLineSegment(sketch, "E1595", {"start": v(19.14, 17.57) * mm, "end": v(19.06, 17.52) * mm});
            skLineSegment(sketch, "E1596", {"start": v(19.06, 17.52) * mm, "end": v(18.98, 17.46) * mm});
            skLineSegment(sketch, "E1597", {"start": v(18.98, 17.46) * mm, "end": v(18.9, 17.41) * mm});
            skLineSegment(sketch, "E1598", {"start": v(18.9, 17.41) * mm, "end": v(18.82, 17.36) * mm});
            skLineSegment(sketch, "E1599", {"start": v(18.82, 17.36) * mm, "end": v(18.74, 17.3) * mm});
            skLineSegment(sketch, "E1600", {"start": v(18.74, 17.3) * mm, "end": v(18.66, 17.25) * mm});
            skLineSegment(sketch, "E1601", {"start": v(18.66, 17.25) * mm, "end": v(18.59, 17.2) * mm});
            skLineSegment(sketch, "E1602", {"start": v(18.59, 17.2) * mm, "end": v(18.5, 17.14) * mm});
            skLineSegment(sketch, "E1603", {"start": v(18.5, 17.14) * mm, "end": v(18.43, 17.09) * mm});
            skLineSegment(sketch, "E1604", {"start": v(18.43, 17.09) * mm, "end": v(18.35, 17.03) * mm});
            skLineSegment(sketch, "E1605", {"start": v(18.35, 17.03) * mm, "end": v(18.28, 16.98) * mm});
            skLineSegment(sketch, "E1606", {"start": v(18.28, 16.98) * mm, "end": v(18.2, 16.92) * mm});
            skLineSegment(sketch, "E1607", {"start": v(18.2, 16.92) * mm, "end": v(18.13, 16.86) * mm});
            skLineSegment(sketch, "E1608", {"start": v(18.13, 16.86) * mm, "end": v(18.05, 16.8) * mm});
            skLineSegment(sketch, "E1609", {"start": v(18.05, 16.8) * mm, "end": v(17.98, 16.75) * mm});
            skLineSegment(sketch, "E1610", {"start": v(17.98, 16.75) * mm, "end": v(17.9, 16.7) * mm});
            skLineSegment(sketch, "E1611", {"start": v(17.9, 16.7) * mm, "end": v(17.83, 16.64) * mm});
            skLineSegment(sketch, "E1612", {"start": v(17.83, 16.64) * mm, "end": v(17.76, 16.58) * mm});
            skLineSegment(sketch, "E1613", {"start": v(17.76, 16.58) * mm, "end": v(17.69, 16.53) * mm});
            skLineSegment(sketch, "E1614", {"start": v(17.69, 16.53) * mm, "end": v(17.62, 16.47) * mm});
            skLineSegment(sketch, "E1615", {"start": v(17.62, 16.47) * mm, "end": v(17.55, 16.41) * mm});
            skLineSegment(sketch, "E1616", {"start": v(17.55, 16.41) * mm, "end": v(17.48, 16.36) * mm});
            skLineSegment(sketch, "E1617", {"start": v(17.48, 16.36) * mm, "end": v(17.41, 16.3) * mm});
            skLineSegment(sketch, "E1618", {"start": v(17.41, 16.3) * mm, "end": v(17.35, 16.25) * mm});
            skLineSegment(sketch, "E1619", {"start": v(17.35, 16.25) * mm, "end": v(17.28, 16.2) * mm});
            skLineSegment(sketch, "E1620", {"start": v(17.28, 16.2) * mm, "end": v(17.22, 16.14) * mm});
            skLineSegment(sketch, "E1621", {"start": v(17.22, 16.14) * mm, "end": v(17.15, 16.09) * mm});
            skLineSegment(sketch, "E1622", {"start": v(17.15, 16.09) * mm, "end": v(17.09, 16.03) * mm});
            skLineSegment(sketch, "E1623", {"start": v(17.09, 16.03) * mm, "end": v(17.03, 15.98) * mm});
            skLineSegment(sketch, "E1624", {"start": v(17.03, 15.98) * mm, "end": v(16.97, 15.93) * mm});
            skLineSegment(sketch, "E1625", {"start": v(16.97, 15.93) * mm, "end": v(16.9, 15.88) * mm});
            skLineSegment(sketch, "E1626", {"start": v(16.9, 15.88) * mm, "end": v(16.85, 15.83) * mm});
            skLineSegment(sketch, "E1627", {"start": v(16.85, 15.83) * mm, "end": v(16.8, 15.78) * mm});
            skLineSegment(sketch, "E1628", {"start": v(16.8, 15.78) * mm, "end": v(16.74, 15.73) * mm});
            skLineSegment(sketch, "E1629", {"start": v(16.74, 15.73) * mm, "end": v(16.69, 15.68) * mm});
            skLineSegment(sketch, "E1630", {"start": v(16.69, 15.68) * mm, "end": v(16.63, 15.64) * mm});
            skLineSegment(sketch, "E1631", {"start": v(16.63, 15.64) * mm, "end": v(16.58, 15.59) * mm});
            skLineSegment(sketch, "E1632", {"start": v(16.58, 15.59) * mm, "end": v(16.53, 15.55) * mm});
            skLineSegment(sketch, "E1633", {"start": v(16.53, 15.55) * mm, "end": v(16.49, 15.5) * mm});
            skLineSegment(sketch, "E1634", {"start": v(16.49, 15.5) * mm, "end": v(16.44, 15.46) * mm});
            skLineSegment(sketch, "E1635", {"start": v(16.44, 15.46) * mm, "end": v(16.4, 15.42) * mm});
            skLineSegment(sketch, "E1636", {"start": v(16.4, 15.42) * mm, "end": v(16.35, 15.38) * mm});
            skLineSegment(sketch, "E1637", {"start": v(16.35, 15.38) * mm, "end": v(16.31, 15.34) * mm});
            skLineSegment(sketch, "E1638", {"start": v(16.31, 15.34) * mm, "end": v(16.27, 15.3) * mm});
            skLineSegment(sketch, "E1639", {"start": v(16.27, 15.3) * mm, "end": v(16.23, 15.27) * mm});
            skLineSegment(sketch, "E1640", {"start": v(16.23, 15.27) * mm, "end": v(16.2, 15.24) * mm});
            skLineSegment(sketch, "E1641", {"start": v(16.2, 15.24) * mm, "end": v(16.16, 15.2) * mm});
            skLineSegment(sketch, "E1642", {"start": v(16.16, 15.2) * mm, "end": v(16.13, 15.17) * mm});
            skLineSegment(sketch, "E1643", {"start": v(16.13, 15.17) * mm, "end": v(16.1, 15.14) * mm});
            skLineSegment(sketch, "E1644", {"start": v(16.1, 15.14) * mm, "end": v(16.07, 15.12) * mm});
            skLineSegment(sketch, "E1645", {"start": v(16.07, 15.12) * mm, "end": v(16, 15.05) * mm});
            skLineSegment(sketch, "E1646", {"start": v(16, 15.05) * mm, "end": v(15.93, 14.98) * mm});
            skLineSegment(sketch, "E1647", {"start": v(15.93, 14.98) * mm, "end": v(15.86, 14.91) * mm});
            skLineSegment(sketch, "E1648", {"start": v(15.86, 14.91) * mm, "end": v(15.78, 14.84) * mm});
            skLineSegment(sketch, "E1649", {"start": v(15.78, 14.84) * mm, "end": v(15.71, 14.77) * mm});
            skLineSegment(sketch, "E1650", {"start": v(15.71, 14.77) * mm, "end": v(15.64, 14.7) * mm});
            skLineSegment(sketch, "E1651", {"start": v(15.64, 14.7) * mm, "end": v(15.57, 14.63) * mm});
            skLineSegment(sketch, "E1652", {"start": v(15.57, 14.63) * mm, "end": v(15.5, 14.56) * mm});
            skLineSegment(sketch, "E1653", {"start": v(15.5, 14.56) * mm, "end": v(15.43, 14.49) * mm});
            skLineSegment(sketch, "E1654", {"start": v(15.43, 14.49) * mm, "end": v(15.36, 14.42) * mm});
            skLineSegment(sketch, "E1655", {"start": v(15.36, 14.42) * mm, "end": v(15.3, 14.34) * mm});
            skLineSegment(sketch, "E1656", {"start": v(15.3, 14.34) * mm, "end": v(15.23, 14.27) * mm});
            skLineSegment(sketch, "E1657", {"start": v(15.23, 14.27) * mm, "end": v(15.16, 14.2) * mm});
            skLineSegment(sketch, "E1658", {"start": v(15.16, 14.2) * mm, "end": v(15.1, 14.13) * mm});
            skLineSegment(sketch, "E1659", {"start": v(15.1, 14.13) * mm, "end": v(15.02, 14.05) * mm});
            skLineSegment(sketch, "E1660", {"start": v(15.02, 14.05) * mm, "end": v(14.95, 13.98) * mm});
            skLineSegment(sketch, "E1661", {"start": v(14.95, 13.98) * mm, "end": v(14.89, 13.9) * mm});
            skLineSegment(sketch, "E1662", {"start": v(14.89, 13.9) * mm, "end": v(14.82, 13.83) * mm});
            skLineSegment(sketch, "E1663", {"start": v(14.82, 13.83) * mm, "end": v(14.75, 13.75) * mm});
            skLineSegment(sketch, "E1664", {"start": v(14.75, 13.75) * mm, "end": v(14.69, 13.68) * mm});
            skLineSegment(sketch, "E1665", {"start": v(14.69, 13.68) * mm, "end": v(14.62, 13.6) * mm});
            skLineSegment(sketch, "E1666", {"start": v(14.62, 13.6) * mm, "end": v(14.56, 13.53) * mm});
            skLineSegment(sketch, "E1667", {"start": v(14.56, 13.53) * mm, "end": v(14.49, 13.45) * mm});
            skLineSegment(sketch, "E1668", {"start": v(14.49, 13.45) * mm, "end": v(14.42, 13.37) * mm});
            skLineSegment(sketch, "E1669", {"start": v(14.42, 13.37) * mm, "end": v(14.36, 13.3) * mm});
            skLineSegment(sketch, "E1670", {"start": v(14.36, 13.3) * mm, "end": v(14.3, 13.22) * mm});
            skLineSegment(sketch, "E1671", {"start": v(14.3, 13.22) * mm, "end": v(14.23, 13.14) * mm});
            skLineSegment(sketch, "E1672", {"start": v(14.23, 13.14) * mm, "end": v(14.17, 13.06) * mm});
            skLineSegment(sketch, "E1673", {"start": v(14.17, 13.06) * mm, "end": v(14.1, 12.99) * mm});
            skLineSegment(sketch, "E1674", {"start": v(14.1, 12.99) * mm, "end": v(14.04, 12.9) * mm});
            skLineSegment(sketch, "E1675", {"start": v(14.04, 12.9) * mm, "end": v(13.98, 12.83) * mm});
            skLineSegment(sketch, "E1676", {"start": v(13.98, 12.83) * mm, "end": v(13.91, 12.75) * mm});
            skLineSegment(sketch, "E1677", {"start": v(13.91, 12.75) * mm, "end": v(13.85, 12.67) * mm});
            skLineSegment(sketch, "E1678", {"start": v(13.85, 12.67) * mm, "end": v(13.79, 12.59) * mm});
            skLineSegment(sketch, "E1679", {"start": v(13.79, 12.59) * mm, "end": v(13.73, 12.5) * mm});
            skLineSegment(sketch, "E1680", {"start": v(13.73, 12.5) * mm, "end": v(13.67, 12.43) * mm});
            skLineSegment(sketch, "E1681", {"start": v(13.67, 12.43) * mm, "end": v(13.6, 12.35) * mm});
            skLineSegment(sketch, "E1682", {"start": v(13.6, 12.35) * mm, "end": v(13.54, 12.27) * mm});
            skLineSegment(sketch, "E1683", {"start": v(13.54, 12.27) * mm, "end": v(13.48, 12.18) * mm});
            skLineSegment(sketch, "E1684", {"start": v(13.48, 12.18) * mm, "end": v(13.42, 12.1) * mm});
            skLineSegment(sketch, "E1685", {"start": v(13.42, 12.1) * mm, "end": v(13.36, 12.02) * mm});
            skLineSegment(sketch, "E1686", {"start": v(13.36, 12.02) * mm, "end": v(13.3, 11.94) * mm});
            skLineSegment(sketch, "E1687", {"start": v(13.3, 11.94) * mm, "end": v(13.24, 11.86) * mm});
            skLineSegment(sketch, "E1688", {"start": v(13.24, 11.86) * mm, "end": v(13.19, 11.77) * mm});
            skLineSegment(sketch, "E1689", {"start": v(13.19, 11.77) * mm, "end": v(13.13, 11.7) * mm});
            skLineSegment(sketch, "E1690", {"start": v(13.13, 11.7) * mm, "end": v(13.07, 11.6) * mm});
            skLineSegment(sketch, "E1691", {"start": v(13.07, 11.6) * mm, "end": v(13.01, 11.52) * mm});
            skLineSegment(sketch, "E1692", {"start": v(13.01, 11.52) * mm, "end": v(12.95, 11.44) * mm});
            skLineSegment(sketch, "E1693", {"start": v(12.95, 11.44) * mm, "end": v(12.9, 11.35) * mm});
            skLineSegment(sketch, "E1694", {"start": v(12.9, 11.35) * mm, "end": v(12.84, 11.27) * mm});
            skLineSegment(sketch, "E1695", {"start": v(12.84, 11.27) * mm, "end": v(12.78, 11.19) * mm});
            skLineSegment(sketch, "E1696", {"start": v(12.78, 11.19) * mm, "end": v(12.73, 11.1) * mm});
            skLineSegment(sketch, "E1697", {"start": v(12.73, 11.1) * mm, "end": v(12.67, 11.02) * mm});
            skLineSegment(sketch, "E1698", {"start": v(12.67, 11.02) * mm, "end": v(12.62, 10.93) * mm});
            skLineSegment(sketch, "E1699", {"start": v(12.62, 10.93) * mm, "end": v(12.56, 10.84) * mm});
            skLineSegment(sketch, "E1700", {"start": v(12.56, 10.84) * mm, "end": v(12.5, 10.76) * mm});
            skLineSegment(sketch, "E1701", {"start": v(12.5, 10.76) * mm, "end": v(12.45, 10.67) * mm});
            skLineSegment(sketch, "E1702", {"start": v(12.45, 10.67) * mm, "end": v(12.4, 10.59) * mm});
            skLineSegment(sketch, "E1703", {"start": v(12.4, 10.59) * mm, "end": v(12.34, 10.5) * mm});
            skLineSegment(sketch, "E1704", {"start": v(12.34, 10.5) * mm, "end": v(12.29, 10.41) * mm});
            skLineSegment(sketch, "E1705", {"start": v(12.29, 10.41) * mm, "end": v(12.24, 10.32) * mm});
            skLineSegment(sketch, "E1706", {"start": v(12.24, 10.32) * mm, "end": v(12.18, 10.24) * mm});
            skLineSegment(sketch, "E1707", {"start": v(12.18, 10.24) * mm, "end": v(12.13, 10.15) * mm});
            skLineSegment(sketch, "E1708", {"start": v(12.13, 10.15) * mm, "end": v(12.08, 10.06) * mm});
            skLineSegment(sketch, "E1709", {"start": v(12.08, 10.06) * mm, "end": v(12.03, 9.97) * mm});
            skLineSegment(sketch, "E1710", {"start": v(12.03, 9.97) * mm, "end": v(11.98, 9.89) * mm});
            skLineSegment(sketch, "E1711", {"start": v(11.98, 9.89) * mm, "end": v(11.93, 9.8) * mm});
            skLineSegment(sketch, "E1712", {"start": v(11.93, 9.8) * mm, "end": v(11.88, 9.7) * mm});
            skLineSegment(sketch, "E1713", {"start": v(11.88, 9.7) * mm, "end": v(11.83, 9.62) * mm});
            skLineSegment(sketch, "E1714", {"start": v(11.83, 9.62) * mm, "end": v(11.78, 9.53) * mm});
            skLineSegment(sketch, "E1715", {"start": v(11.78, 9.53) * mm, "end": v(11.73, 9.44) * mm});
            skLineSegment(sketch, "E1716", {"start": v(11.73, 9.44) * mm, "end": v(11.68, 9.35) * mm});
            skLineSegment(sketch, "E1717", {"start": v(11.68, 9.35) * mm, "end": v(11.63, 9.26) * mm});
            skLineSegment(sketch, "E1718", {"start": v(11.63, 9.26) * mm, "end": v(11.58, 9.17) * mm});
            skLineSegment(sketch, "E1719", {"start": v(11.58, 9.17) * mm, "end": v(11.53, 9.08) * mm});
            skLineSegment(sketch, "E1720", {"start": v(11.53, 9.08) * mm, "end": v(11.49, 9) * mm});
            skLineSegment(sketch, "E1721", {"start": v(11.49, 9) * mm, "end": v(11.44, 8.9) * mm});
            skLineSegment(sketch, "E1722", {"start": v(11.44, 8.9) * mm, "end": v(11.4, 8.8) * mm});
            skLineSegment(sketch, "E1723", {"start": v(11.4, 8.8) * mm, "end": v(11.35, 8.72) * mm});
            skLineSegment(sketch, "E1724", {"start": v(11.35, 8.72) * mm, "end": v(11.3, 8.63) * mm});
            skLineSegment(sketch, "E1725", {"start": v(11.3, 8.63) * mm, "end": v(11.25, 8.54) * mm});
            skLineSegment(sketch, "E1726", {"start": v(11.25, 8.54) * mm, "end": v(11.2, 8.44) * mm});
            skLineSegment(sketch, "E1727", {"start": v(11.2, 8.44) * mm, "end": v(11.16, 8.35) * mm});
            skLineSegment(sketch, "E1728", {"start": v(11.16, 8.35) * mm, "end": v(11.12, 8.26) * mm});
            skLineSegment(sketch, "E1729", {"start": v(11.12, 8.26) * mm, "end": v(11.08, 8.17) * mm});
            skLineSegment(sketch, "E1730", {"start": v(11.08, 8.17) * mm, "end": v(11.03, 8.08) * mm});
            skLineSegment(sketch, "E1731", {"start": v(11.03, 8.08) * mm, "end": v(10.99, 7.98) * mm});
            skLineSegment(sketch, "E1732", {"start": v(10.99, 7.98) * mm, "end": v(10.95, 7.9) * mm});
            skLineSegment(sketch, "E1733", {"start": v(10.95, 7.9) * mm, "end": v(10.9, 7.8) * mm});
            skLineSegment(sketch, "E1734", {"start": v(10.9, 7.8) * mm, "end": v(10.86, 7.7) * mm});
            skLineSegment(sketch, "E1735", {"start": v(10.86, 7.7) * mm, "end": v(10.82, 7.61) * mm});
            skLineSegment(sketch, "E1736", {"start": v(10.82, 7.61) * mm, "end": v(10.78, 7.52) * mm});
            skLineSegment(sketch, "E1737", {"start": v(10.78, 7.52) * mm, "end": v(10.74, 7.43) * mm});
            skLineSegment(sketch, "E1738", {"start": v(10.74, 7.43) * mm, "end": v(10.7, 7.33) * mm});
            skLineSegment(sketch, "E1739", {"start": v(10.7, 7.33) * mm, "end": v(10.66, 7.24) * mm});
            skLineSegment(sketch, "E1740", {"start": v(10.66, 7.24) * mm, "end": v(10.62, 7.15) * mm});
            skLineSegment(sketch, "E1741", {"start": v(10.62, 7.15) * mm, "end": v(10.58, 7.05) * mm});
            skLineSegment(sketch, "E1742", {"start": v(10.58, 7.05) * mm, "end": v(10.54, 6.96) * mm});
            skLineSegment(sketch, "E1743", {"start": v(10.54, 6.96) * mm, "end": v(10.5, 6.86) * mm});
            skLineSegment(sketch, "E1744", {"start": v(10.5, 6.86) * mm, "end": v(10.46, 6.77) * mm});
            skLineSegment(sketch, "E1745", {"start": v(10.46, 6.77) * mm, "end": v(10.43, 6.68) * mm});
            skLineSegment(sketch, "E1746", {"start": v(10.43, 6.68) * mm, "end": v(10.39, 6.58) * mm});
            skLineSegment(sketch, "E1747", {"start": v(10.39, 6.58) * mm, "end": v(10.35, 6.49) * mm});
            skLineSegment(sketch, "E1748", {"start": v(10.35, 6.49) * mm, "end": v(10.32, 6.4) * mm});
            skLineSegment(sketch, "E1749", {"start": v(10.32, 6.4) * mm, "end": v(10.28, 6.3) * mm});
            skLineSegment(sketch, "E1750", {"start": v(10.28, 6.3) * mm, "end": v(10.25, 6.2) * mm});
            skLineSegment(sketch, "E1751", {"start": v(10.25, 6.2) * mm, "end": v(10.21, 6.1) * mm});
            skLineSegment(sketch, "E1752", {"start": v(10.21, 6.1) * mm, "end": v(10.18, 6.01) * mm});
            skLineSegment(sketch, "E1753", {"start": v(10.18, 6.01) * mm, "end": v(10.14, 5.92) * mm});
            skLineSegment(sketch, "E1754", {"start": v(10.14, 5.92) * mm, "end": v(10.1, 5.82) * mm});
            skLineSegment(sketch, "E1755", {"start": v(10.1, 5.82) * mm, "end": v(10.07, 5.73) * mm});
            skLineSegment(sketch, "E1756", {"start": v(10.07, 5.73) * mm, "end": v(10.04, 5.63) * mm});
            skLineSegment(sketch, "E1757", {"start": v(10.04, 5.63) * mm, "end": v(10, 5.53) * mm});
            skLineSegment(sketch, "E1758", {"start": v(10, 5.53) * mm, "end": v(9.98, 5.44) * mm});
            skLineSegment(sketch, "E1759", {"start": v(9.98, 5.44) * mm, "end": v(9.95, 5.34) * mm});
            skLineSegment(sketch, "E1760", {"start": v(9.95, 5.34) * mm, "end": v(9.91, 5.25) * mm});
            skLineSegment(sketch, "E1761", {"start": v(9.91, 5.25) * mm, "end": v(9.88, 5.15) * mm});
            skLineSegment(sketch, "E1762", {"start": v(9.88, 5.15) * mm, "end": v(9.85, 5.05) * mm});
            skLineSegment(sketch, "E1763", {"start": v(9.85, 5.05) * mm, "end": v(9.82, 4.96) * mm});
            skLineSegment(sketch, "E1764", {"start": v(9.82, 4.96) * mm, "end": v(9.8, 4.86) * mm});
            skLineSegment(sketch, "E1765", {"start": v(9.8, 4.86) * mm, "end": v(9.77, 4.77) * mm});
            skLineSegment(sketch, "E1766", {"start": v(9.77, 4.77) * mm, "end": v(9.74, 4.67) * mm});
            skLineSegment(sketch, "E1767", {"start": v(9.74, 4.67) * mm, "end": v(9.7, 4.57) * mm});
            skLineSegment(sketch, "E1768", {"start": v(9.7, 4.57) * mm, "end": v(9.68, 4.48) * mm});
            skLineSegment(sketch, "E1769", {"start": v(9.68, 4.48) * mm, "end": v(9.65, 4.38) * mm});
            skLineSegment(sketch, "E1770", {"start": v(9.65, 4.38) * mm, "end": v(9.63, 4.28) * mm});
            skLineSegment(sketch, "E1771", {"start": v(9.63, 4.28) * mm, "end": v(9.6, 4.19) * mm});
            skLineSegment(sketch, "E1772", {"start": v(9.6, 4.19) * mm, "end": v(9.58, 4.09) * mm});
            skLineSegment(sketch, "E1773", {"start": v(9.58, 4.09) * mm, "end": v(9.55, 4) * mm});
            skLineSegment(sketch, "E1774", {"start": v(9.55, 4) * mm, "end": v(9.53, 3.9) * mm});
            skLineSegment(sketch, "E1775", {"start": v(9.53, 3.9) * mm, "end": v(9.5, 3.8) * mm});
            skLineSegment(sketch, "E1776", {"start": v(9.5, 3.8) * mm, "end": v(9.48, 3.7) * mm});
            skLineSegment(sketch, "E1777", {"start": v(9.48, 3.7) * mm, "end": v(9.45, 3.6) * mm});
            skLineSegment(sketch, "E1778", {"start": v(9.45, 3.6) * mm, "end": v(9.43, 3.5) * mm});
            skLineSegment(sketch, "E1779", {"start": v(9.43, 3.5) * mm, "end": v(9.4, 3.41) * mm});
            skLineSegment(sketch, "E1780", {"start": v(9.4, 3.41) * mm, "end": v(9.39, 3.31) * mm});
            skLineSegment(sketch, "E1781", {"start": v(9.39, 3.31) * mm, "end": v(9.37, 3.22) * mm});
            skLineSegment(sketch, "E1782", {"start": v(9.37, 3.22) * mm, "end": v(9.34, 3.12) * mm});
            skLineSegment(sketch, "E1783", {"start": v(9.34, 3.12) * mm, "end": v(9.32, 3.02) * mm});
            skLineSegment(sketch, "E1784", {"start": v(9.32, 3.02) * mm, "end": v(9.3, 2.93) * mm});
            skLineSegment(sketch, "E1785", {"start": v(9.3, 2.93) * mm, "end": v(9.28, 2.83) * mm});
            skLineSegment(sketch, "E1786", {"start": v(9.28, 2.83) * mm, "end": v(9.26, 2.73) * mm});
            skLineSegment(sketch, "E1787", {"start": v(9.26, 2.73) * mm, "end": v(9.25, 2.63) * mm});
            skLineSegment(sketch, "E1788", {"start": v(9.25, 2.63) * mm, "end": v(9.23, 2.54) * mm});
            skLineSegment(sketch, "E1789", {"start": v(9.23, 2.54) * mm, "end": v(9.21, 2.45) * mm});
            skLineSegment(sketch, "E1790", {"start": v(9.21, 2.45) * mm, "end": v(9.2, 2.37) * mm});
            skLineSegment(sketch, "E1791", {"start": v(9.2, 2.37) * mm, "end": v(9.2, 2.28) * mm});
            skLineSegment(sketch, "E1792", {"start": v(9.2, 2.28) * mm, "end": v(9.18, 2.2) * mm});
            skLineSegment(sketch, "E1793", {"start": v(9.18, 2.2) * mm, "end": v(9.17, 2.1) * mm});
            skLineSegment(sketch, "E1794", {"start": v(9.17, 2.1) * mm, "end": v(9.17, 2) * mm});
            skLineSegment(sketch, "E1795", {"start": v(9.17, 2) * mm, "end": v(9.17, 1.91) * mm});
            skLineSegment(sketch, "E1796", {"start": v(9.17, 1.91) * mm, "end": v(9.16, 1.82) * mm});
            skLineSegment(sketch, "E1797", {"start": v(9.16, 1.82) * mm, "end": v(9.16, 1.72) * mm});
            skLineSegment(sketch, "E1798", {"start": v(9.16, 1.72) * mm, "end": v(9.16, 1.62) * mm});
            skLineSegment(sketch, "E1799", {"start": v(9.16, 1.62) * mm, "end": v(9.16, 1.52) * mm});
            skLineSegment(sketch, "E1800", {"start": v(9.16, 1.52) * mm, "end": v(9.16, 1.42) * mm});
            skLineSegment(sketch, "E1801", {"start": v(9.16, 1.42) * mm, "end": v(9.17, 1.32) * mm});
            skLineSegment(sketch, "E1802", {"start": v(9.17, 1.32) * mm, "end": v(9.17, 1.21) * mm});
            skLineSegment(sketch, "E1803", {"start": v(9.17, 1.21) * mm, "end": v(9.18, 1.1) * mm});
            skLineSegment(sketch, "E1804", {"start": v(9.18, 1.1) * mm, "end": v(9.18, 1) * mm});
            skLineSegment(sketch, "E1805", {"start": v(9.18, 1) * mm, "end": v(9.19, 0.9) * mm});
            skLineSegment(sketch, "E1806", {"start": v(9.19, 0.9) * mm, "end": v(9.2, 0.78) * mm});
            skLineSegment(sketch, "E1807", {"start": v(9.2, 0.78) * mm, "end": v(9.2, 0.68) * mm});
            skLineSegment(sketch, "E1808", {"start": v(9.2, 0.68) * mm, "end": v(9.21, 0.57) * mm});
            skLineSegment(sketch, "E1809", {"start": v(9.21, 0.57) * mm, "end": v(9.22, 0.46) * mm});
            skLineSegment(sketch, "E1810", {"start": v(9.22, 0.46) * mm, "end": v(9.23, 0.35) * mm});
            skLineSegment(sketch, "E1811", {"start": v(9.23, 0.35) * mm, "end": v(9.24, 0.24) * mm});
            skLineSegment(sketch, "E1812", {"start": v(9.24, 0.24) * mm, "end": v(9.25, 0.13) * mm});
            skLineSegment(sketch, "E1813", {"start": v(9.25, 0.13) * mm, "end": v(9.26, 0.01) * mm});
            skLineSegment(sketch, "E1814", {"start": v(9.26, 0.01) * mm, "end": v(9.27, -0.1) * mm});
            skLineSegment(sketch, "E1815", {"start": v(9.27, -0.1) * mm, "end": v(9.28, -0.2) * mm});
            skLineSegment(sketch, "E1816", {"start": v(9.28, -0.2) * mm, "end": v(9.28, -0.32) * mm});
            skLineSegment(sketch, "E1817", {"start": v(9.28, -0.32) * mm, "end": v(9.3, -0.43) * mm});
            skLineSegment(sketch, "E1818", {"start": v(9.3, -0.43) * mm, "end": v(9.3, -0.54) * mm});
            skLineSegment(sketch, "E1819", {"start": v(9.3, -0.54) * mm, "end": v(9.31, -0.65) * mm});
            skLineSegment(sketch, "E1820", {"start": v(9.31, -0.65) * mm, "end": v(9.32, -0.76) * mm});
            skLineSegment(sketch, "E1821", {"start": v(9.32, -0.76) * mm, "end": v(9.32, -0.87) * mm});
            skLineSegment(sketch, "E1822", {"start": v(9.32, -0.87) * mm, "end": v(9.33, -0.98) * mm});
            skLineSegment(sketch, "E1823", {"start": v(9.33, -0.98) * mm, "end": v(9.34, -1.08) * mm});
            skLineSegment(sketch, "E1824", {"start": v(9.34, -1.08) * mm, "end": v(9.34, -1.2) * mm});
            skLineSegment(sketch, "E1825", {"start": v(9.34, -1.2) * mm, "end": v(9.35, -1.3) * mm});
            skLineSegment(sketch, "E1826", {"start": v(9.35, -1.3) * mm, "end": v(9.35, -1.4) * mm});
            skLineSegment(sketch, "E1827", {"start": v(9.35, -1.4) * mm, "end": v(9.35, -1.5) * mm});
            skLineSegment(sketch, "E1828", {"start": v(9.35, -1.5) * mm, "end": v(9.35, -1.6) * mm});
            skLineSegment(sketch, "E1829", {"start": v(9.35, -1.6) * mm, "end": v(9.35, -1.7) * mm});
            skLineSegment(sketch, "E1830", {"start": v(9.35, -1.7) * mm, "end": v(9.35, -1.8) * mm});
            skLineSegment(sketch, "E1831", {"start": v(9.35, -1.8) * mm, "end": v(9.35, -1.9) * mm});
            skLineSegment(sketch, "E1832", {"start": v(9.35, -1.9) * mm, "end": v(9.35, -2) * mm});
            skLineSegment(sketch, "E1833", {"start": v(9.35, -2) * mm, "end": v(9.34, -2.1) * mm});
            skLineSegment(sketch, "E1834", {"start": v(9.34, -2.1) * mm, "end": v(9.33, -2.2) * mm});
            skLineSegment(sketch, "E1835", {"start": v(9.33, -2.2) * mm, "end": v(9.32, -2.29) * mm});
            skLineSegment(sketch, "E1836", {"start": v(9.32, -2.29) * mm, "end": v(9.31, -2.38) * mm});
            skLineSegment(sketch, "E1837", {"start": v(9.31, -2.38) * mm, "end": v(9.3, -2.46) * mm});
            skLineSegment(sketch, "E1838", {"start": v(9.3, -2.46) * mm, "end": v(9.29, -2.55) * mm});
            skLineSegment(sketch, "E1839", {"start": v(9.29, -2.55) * mm, "end": v(9.27, -2.63) * mm});
            skLineSegment(sketch, "E1840", {"start": v(9.27, -2.63) * mm, "end": v(9.25, -2.72) * mm});
            skLineSegment(sketch, "E1841", {"start": v(9.25, -2.72) * mm, "end": v(9.23, -2.8) * mm});
            skLineSegment(sketch, "E1842", {"start": v(9.23, -2.8) * mm, "end": v(9.21, -2.87) * mm});
            skLineSegment(sketch, "E1843", {"start": v(9.21, -2.87) * mm, "end": v(9.19, -2.95) * mm});
            skLineSegment(sketch, "E1844", {"start": v(9.19, -2.95) * mm, "end": v(9.16, -3.02) * mm});
            skLineSegment(sketch, "E1845", {"start": v(9.16, -3.02) * mm, "end": v(9.13, -3.09) * mm});
            skLineSegment(sketch, "E1846", {"start": v(9.13, -3.09) * mm, "end": v(9.1, -3.15) * mm});
            skLineSegment(sketch, "E1847", {"start": v(9.1, -3.15) * mm, "end": v(9.07, -3.2) * mm});
            skLineSegment(sketch, "E1848", {"start": v(9.07, -3.2) * mm, "end": v(9.03, -3.27) * mm});
            skLineSegment(sketch, "E1849", {"start": v(9.03, -3.27) * mm, "end": v(9, -3.33) * mm});
            skLineSegment(sketch, "E1850", {"start": v(9, -3.33) * mm, "end": v(8.95, -3.4) * mm});
            skLineSegment(sketch, "E1851", {"start": v(8.95, -3.4) * mm, "end": v(8.9, -3.46) * mm});
            skLineSegment(sketch, "E1852", {"start": v(8.9, -3.46) * mm, "end": v(8.85, -3.53) * mm});
            skLineSegment(sketch, "E1853", {"start": v(8.85, -3.53) * mm, "end": v(8.8, -3.6) * mm});
            skLineSegment(sketch, "E1854", {"start": v(8.8, -3.6) * mm, "end": v(8.74, -3.66) * mm});
            skLineSegment(sketch, "E1855", {"start": v(8.74, -3.66) * mm, "end": v(8.68, -3.73) * mm});
            skLineSegment(sketch, "E1856", {"start": v(8.68, -3.73) * mm, "end": v(8.62, -3.8) * mm});
            skLineSegment(sketch, "E1857", {"start": v(8.62, -3.8) * mm, "end": v(8.56, -3.86) * mm});
            skLineSegment(sketch, "E1858", {"start": v(8.56, -3.86) * mm, "end": v(8.49, -3.93) * mm});
            skLineSegment(sketch, "E1859", {"start": v(8.49, -3.93) * mm, "end": v(8.42, -4) * mm});
            skLineSegment(sketch, "E1860", {"start": v(8.42, -4) * mm, "end": v(8.34, -4.07) * mm});
            skLineSegment(sketch, "E1861", {"start": v(8.34, -4.07) * mm, "end": v(8.27, -4.14) * mm});
            skLineSegment(sketch, "E1862", {"start": v(8.27, -4.14) * mm, "end": v(8.2, -4.2) * mm});
            skLineSegment(sketch, "E1863", {"start": v(8.2, -4.2) * mm, "end": v(8.11, -4.27) * mm});
            skLineSegment(sketch, "E1864", {"start": v(8.11, -4.27) * mm, "end": v(8.03, -4.34) * mm});
            skLineSegment(sketch, "E1865", {"start": v(8.03, -4.34) * mm, "end": v(7.95, -4.4) * mm});
            skLineSegment(sketch, "E1866", {"start": v(7.95, -4.4) * mm, "end": v(7.86, -4.47) * mm});
            skLineSegment(sketch, "E1867", {"start": v(7.86, -4.47) * mm, "end": v(7.78, -4.54) * mm});
            skLineSegment(sketch, "E1868", {"start": v(7.78, -4.54) * mm, "end": v(7.69, -4.6) * mm});
            skLineSegment(sketch, "E1869", {"start": v(7.69, -4.6) * mm, "end": v(7.6, -4.67) * mm});
            skLineSegment(sketch, "E1870", {"start": v(7.6, -4.67) * mm, "end": v(7.5, -4.73) * mm});
            skLineSegment(sketch, "E1871", {"start": v(7.5, -4.73) * mm, "end": v(7.42, -4.8) * mm});
            skLineSegment(sketch, "E1872", {"start": v(7.42, -4.8) * mm, "end": v(7.32, -4.86) * mm});
            skLineSegment(sketch, "E1873", {"start": v(7.32, -4.86) * mm, "end": v(7.23, -4.92) * mm});
            skLineSegment(sketch, "E1874", {"start": v(7.23, -4.92) * mm, "end": v(7.13, -4.98) * mm});
            skLineSegment(sketch, "E1875", {"start": v(7.13, -4.98) * mm, "end": v(7.04, -5.04) * mm});
            skLineSegment(sketch, "E1876", {"start": v(7.04, -5.04) * mm, "end": v(6.94, -5.1) * mm});
            skLineSegment(sketch, "E1877", {"start": v(6.94, -5.1) * mm, "end": v(6.84, -5.15) * mm});
            skLineSegment(sketch, "E1878", {"start": v(6.84, -5.15) * mm, "end": v(6.74, -5.2) * mm});
            skLineSegment(sketch, "E1879", {"start": v(6.74, -5.2) * mm, "end": v(6.65, -5.26) * mm});
            skLineSegment(sketch, "E1880", {"start": v(6.65, -5.26) * mm, "end": v(6.55, -5.3) * mm});
            skLineSegment(sketch, "E1881", {"start": v(6.55, -5.3) * mm, "end": v(6.45, -5.36) * mm});
            skLineSegment(sketch, "E1882", {"start": v(6.45, -5.36) * mm, "end": v(6.35, -5.4) * mm});
            skLineSegment(sketch, "E1883", {"start": v(6.35, -5.4) * mm, "end": v(6.25, -5.45) * mm});
            skLineSegment(sketch, "E1884", {"start": v(6.25, -5.45) * mm, "end": v(6.16, -5.5) * mm});
            skLineSegment(sketch, "E1885", {"start": v(6.16, -5.5) * mm, "end": v(6.06, -5.53) * mm});
            skLineSegment(sketch, "E1886", {"start": v(6.06, -5.53) * mm, "end": v(5.96, -5.57) * mm});
            skLineSegment(sketch, "E1887", {"start": v(5.96, -5.57) * mm, "end": v(5.87, -5.6) * mm});
            skLineSegment(sketch, "E1888", {"start": v(5.87, -5.6) * mm, "end": v(5.77, -5.64) * mm});
            skLineSegment(sketch, "E1889", {"start": v(5.77, -5.64) * mm, "end": v(5.67, -5.67) * mm});
            skLineSegment(sketch, "E1890", {"start": v(5.67, -5.67) * mm, "end": v(5.58, -5.7) * mm});
            skLineSegment(sketch, "E1891", {"start": v(5.58, -5.7) * mm, "end": v(5.49, -5.72) * mm});
            skLineSegment(sketch, "E1892", {"start": v(5.49, -5.72) * mm, "end": v(5.4, -5.75) * mm});
            skLineSegment(sketch, "E1893", {"start": v(5.4, -5.75) * mm, "end": v(5.3, -5.77) * mm});
            skLineSegment(sketch, "E1894", {"start": v(5.3, -5.77) * mm, "end": v(5.22, -5.78) * mm});
            skLineSegment(sketch, "E1895", {"start": v(5.22, -5.78) * mm, "end": v(5.13, -5.8) * mm});
            skLineSegment(sketch, "E1896", {"start": v(5.13, -5.8) * mm, "end": v(5.04, -5.8) * mm});
            skLineSegment(sketch, "E1897", {"start": v(5.04, -5.8) * mm, "end": v(4.96, -5.82) * mm});
            skLineSegment(sketch, "E1898", {"start": v(4.96, -5.82) * mm, "end": v(4.87, -5.82) * mm});
            skLineSegment(sketch, "E1899", {"start": v(4.87, -5.82) * mm, "end": v(4.8, -5.82) * mm});
            skLineSegment(sketch, "E1900", {"start": v(4.8, -5.82) * mm, "end": v(4.71, -5.82) * mm});
            skLineSegment(sketch, "E1901", {"start": v(4.71, -5.82) * mm, "end": v(4.64, -5.81) * mm});
            skLineSegment(sketch, "E1902", {"start": v(4.64, -5.81) * mm, "end": v(4.56, -5.8) * mm});
            skLineSegment(sketch, "E1903", {"start": v(4.56, -5.8) * mm, "end": v(4.49, -5.8) * mm});
            skLineSegment(sketch, "E1904", {"start": v(4.49, -5.8) * mm, "end": v(4.42, -5.77) * mm});
            skLineSegment(sketch, "E1905", {"start": v(4.42, -5.77) * mm, "end": v(4.34, -5.74) * mm});
            skLineSegment(sketch, "E1906", {"start": v(4.34, -5.74) * mm, "end": v(4.26, -5.7) * mm});
            skLineSegment(sketch, "E1907", {"start": v(4.26, -5.7) * mm, "end": v(4.19, -5.67) * mm});
            skLineSegment(sketch, "E1908", {"start": v(4.19, -5.67) * mm, "end": v(4.13, -5.62) * mm});
            skLineSegment(sketch, "E1909", {"start": v(4.13, -5.62) * mm, "end": v(4.07, -5.57) * mm});
            skLineSegment(sketch, "E1910", {"start": v(4.07, -5.57) * mm, "end": v(4.03, -5.51) * mm});
            skLineSegment(sketch, "E1911", {"start": v(4.03, -5.51) * mm, "end": v(3.98, -5.45) * mm});
            skLineSegment(sketch, "E1912", {"start": v(3.98, -5.45) * mm, "end": v(3.95, -5.38) * mm});
            skLineSegment(sketch, "E1913", {"start": v(3.95, -5.38) * mm, "end": v(3.92, -5.31) * mm});
            skLineSegment(sketch, "E1914", {"start": v(3.92, -5.31) * mm, "end": v(3.9, -5.24) * mm});
            skLineSegment(sketch, "E1915", {"start": v(3.9, -5.24) * mm, "end": v(3.88, -5.16) * mm});
            skLineSegment(sketch, "E1916", {"start": v(3.88, -5.16) * mm, "end": v(3.87, -5.08) * mm});
            skLineSegment(sketch, "E1917", {"start": v(3.87, -5.08) * mm, "end": v(3.86, -5) * mm});
            skLineSegment(sketch, "E1918", {"start": v(3.86, -5) * mm, "end": v(3.86, -4.91) * mm});
            skLineSegment(sketch, "E1919", {"start": v(3.86, -4.91) * mm, "end": v(3.86, -4.82) * mm});
            skLineSegment(sketch, "E1920", {"start": v(3.86, -4.82) * mm, "end": v(3.86, -4.73) * mm});
            skLineSegment(sketch, "E1921", {"start": v(3.86, -4.73) * mm, "end": v(3.87, -4.64) * mm});
            skLineSegment(sketch, "E1922", {"start": v(3.87, -4.64) * mm, "end": v(3.88, -4.55) * mm});
            skLineSegment(sketch, "E1923", {"start": v(3.88, -4.55) * mm, "end": v(3.9, -4.46) * mm});
            skLineSegment(sketch, "E1924", {"start": v(3.9, -4.46) * mm, "end": v(3.92, -4.36) * mm});
            skLineSegment(sketch, "E1925", {"start": v(3.92, -4.36) * mm, "end": v(3.94, -4.27) * mm});
            skLineSegment(sketch, "E1926", {"start": v(3.94, -4.27) * mm, "end": v(3.96, -4.17) * mm});
            skLineSegment(sketch, "E1927", {"start": v(3.96, -4.17) * mm, "end": v(3.99, -4.08) * mm});
            skLineSegment(sketch, "E1928", {"start": v(3.99, -4.08) * mm, "end": v(4.01, -3.98) * mm});
            skLineSegment(sketch, "E1929", {"start": v(4.01, -3.98) * mm, "end": v(4.04, -3.9) * mm});
            skLineSegment(sketch, "E1930", {"start": v(4.04, -3.9) * mm, "end": v(4.07, -3.8) * mm});
            skLineSegment(sketch, "E1931", {"start": v(4.07, -3.8) * mm, "end": v(4.1, -3.71) * mm});
            skLineSegment(sketch, "E1932", {"start": v(4.1, -3.71) * mm, "end": v(4.13, -3.62) * mm});
            skLineSegment(sketch, "E1933", {"start": v(4.13, -3.62) * mm, "end": v(4.16, -3.54) * mm});
            skLineSegment(sketch, "E1934", {"start": v(4.16, -3.54) * mm, "end": v(4.18, -3.45) * mm});
            skLineSegment(sketch, "E1935", {"start": v(4.18, -3.45) * mm, "end": v(4.21, -3.37) * mm});
            skLineSegment(sketch, "E1936", {"start": v(4.21, -3.37) * mm, "end": v(4.24, -3.3) * mm});
            skLineSegment(sketch, "E1937", {"start": v(4.24, -3.3) * mm, "end": v(4.27, -3.23) * mm});
            skLineSegment(sketch, "E1938", {"start": v(4.27, -3.23) * mm, "end": v(4.3, -3.16) * mm});
            skLineSegment(sketch, "E1939", {"start": v(4.3, -3.16) * mm, "end": v(4.32, -3.1) * mm});
            skLineSegment(sketch, "E1940", {"start": v(4.32, -3.1) * mm, "end": v(4.34, -3.03) * mm});
            skLineSegment(sketch, "E1941", {"start": v(4.34, -3.03) * mm, "end": v(4.36, -2.98) * mm});
            skLineSegment(sketch, "E1942", {"start": v(4.36, -2.98) * mm, "end": v(4.4, -2.88) * mm});
            skLineSegment(sketch, "E1943", {"start": v(4.4, -2.88) * mm, "end": v(4.43, -2.78) * mm});
            skLineSegment(sketch, "E1944", {"start": v(4.43, -2.78) * mm, "end": v(4.47, -2.69) * mm});
            skLineSegment(sketch, "E1945", {"start": v(4.47, -2.69) * mm, "end": v(4.5, -2.6) * mm});
            skLineSegment(sketch, "E1946", {"start": v(4.5, -2.6) * mm, "end": v(4.54, -2.5) * mm});
            skLineSegment(sketch, "E1947", {"start": v(4.54, -2.5) * mm, "end": v(4.57, -2.4) * mm});
            skLineSegment(sketch, "E1948", {"start": v(4.57, -2.4) * mm, "end": v(4.6, -2.3) * mm});
            skLineSegment(sketch, "E1949", {"start": v(4.6, -2.3) * mm, "end": v(4.64, -2.2) * mm});
            skLineSegment(sketch, "E1950", {"start": v(4.64, -2.2) * mm, "end": v(4.68, -2.11) * mm});
            skLineSegment(sketch, "E1951", {"start": v(4.68, -2.11) * mm, "end": v(4.71, -2.01) * mm});
            skLineSegment(sketch, "E1952", {"start": v(4.71, -2.01) * mm, "end": v(4.75, -1.92) * mm});
            skLineSegment(sketch, "E1953", {"start": v(4.75, -1.92) * mm, "end": v(4.79, -1.82) * mm});
            skLineSegment(sketch, "E1954", {"start": v(4.79, -1.82) * mm, "end": v(4.82, -1.73) * mm});
            skLineSegment(sketch, "E1955", {"start": v(4.82, -1.73) * mm, "end": v(4.86, -1.63) * mm});
            skLineSegment(sketch, "E1956", {"start": v(4.86, -1.63) * mm, "end": v(4.9, -1.54) * mm});
            skLineSegment(sketch, "E1957", {"start": v(4.9, -1.54) * mm, "end": v(4.93, -1.44) * mm});
            skLineSegment(sketch, "E1958", {"start": v(4.93, -1.44) * mm, "end": v(4.97, -1.35) * mm});
            skLineSegment(sketch, "E1959", {"start": v(4.97, -1.35) * mm, "end": v(5, -1.25) * mm});
            skLineSegment(sketch, "E1960", {"start": v(5, -1.25) * mm, "end": v(5.05, -1.16) * mm});
            skLineSegment(sketch, "E1961", {"start": v(5.05, -1.16) * mm, "end": v(5.08, -1.06) * mm});
            skLineSegment(sketch, "E1962", {"start": v(5.08, -1.06) * mm, "end": v(5.12, -0.97) * mm});
            skLineSegment(sketch, "E1963", {"start": v(5.12, -0.97) * mm, "end": v(5.16, -0.87) * mm});
            skLineSegment(sketch, "E1964", {"start": v(5.16, -0.87) * mm, "end": v(5.2, -0.77) * mm});
            skLineSegment(sketch, "E1965", {"start": v(5.2, -0.77) * mm, "end": v(5.24, -0.68) * mm});
            skLineSegment(sketch, "E1966", {"start": v(5.24, -0.68) * mm, "end": v(5.27, -0.58) * mm});
            skLineSegment(sketch, "E1967", {"start": v(5.27, -0.58) * mm, "end": v(5.31, -0.49) * mm});
            skLineSegment(sketch, "E1968", {"start": v(5.31, -0.49) * mm, "end": v(5.35, -0.4) * mm});
            skLineSegment(sketch, "E1969", {"start": v(5.35, -0.4) * mm, "end": v(5.4, -0.3) * mm});
            skLineSegment(sketch, "E1970", {"start": v(5.4, -0.3) * mm, "end": v(5.43, -0.2) * mm});
            skLineSegment(sketch, "E1971", {"start": v(5.43, -0.2) * mm, "end": v(5.47, -0.11) * mm});
            skLineSegment(sketch, "E1972", {"start": v(5.47, -0.11) * mm, "end": v(5.5, -0.02) * mm});
            skLineSegment(sketch, "E1973", {"start": v(5.5, -0.02) * mm, "end": v(5.55, 0.08) * mm});
            skLineSegment(sketch, "E1974", {"start": v(5.55, 0.08) * mm, "end": v(5.58, 0.17) * mm});
            skLineSegment(sketch, "E1975", {"start": v(5.58, 0.17) * mm, "end": v(5.62, 0.27) * mm});
            skLineSegment(sketch, "E1976", {"start": v(5.62, 0.27) * mm, "end": v(5.66, 0.36) * mm});
            skLineSegment(sketch, "E1977", {"start": v(5.66, 0.36) * mm, "end": v(5.7, 0.46) * mm});
            skLineSegment(sketch, "E1978", {"start": v(5.7, 0.46) * mm, "end": v(5.74, 0.55) * mm});
            skLineSegment(sketch, "E1979", {"start": v(5.74, 0.55) * mm, "end": v(5.78, 0.65) * mm});
            skLineSegment(sketch, "E1980", {"start": v(5.78, 0.65) * mm, "end": v(5.82, 0.74) * mm});
            skLineSegment(sketch, "E1981", {"start": v(5.82, 0.74) * mm, "end": v(5.86, 0.84) * mm});
            skLineSegment(sketch, "E1982", {"start": v(5.86, 0.84) * mm, "end": v(5.9, 0.93) * mm});
            skLineSegment(sketch, "E1983", {"start": v(5.9, 0.93) * mm, "end": v(5.94, 1.02) * mm});
            skLineSegment(sketch, "E1984", {"start": v(5.94, 1.02) * mm, "end": v(5.98, 1.12) * mm});
            skLineSegment(sketch, "E1985", {"start": v(5.98, 1.12) * mm, "end": v(6.02, 1.21) * mm});
            skLineSegment(sketch, "E1986", {"start": v(6.02, 1.21) * mm, "end": v(6.06, 1.3) * mm});
            skLineSegment(sketch, "E1987", {"start": v(6.06, 1.3) * mm, "end": v(6.1, 1.4) * mm});
            skLineSegment(sketch, "E1988", {"start": v(6.1, 1.4) * mm, "end": v(6.14, 1.5) * mm});
            skLineSegment(sketch, "E1989", {"start": v(6.14, 1.5) * mm, "end": v(6.18, 1.6) * mm});
            skLineSegment(sketch, "E1990", {"start": v(6.18, 1.6) * mm, "end": v(6.21, 1.69) * mm});
            skLineSegment(sketch, "E1991", {"start": v(6.21, 1.69) * mm, "end": v(6.25, 1.78) * mm});
            skLineSegment(sketch, "E1992", {"start": v(6.25, 1.78) * mm, "end": v(6.3, 1.87) * mm});
            skLineSegment(sketch, "E1993", {"start": v(6.3, 1.87) * mm, "end": v(6.33, 1.97) * mm});
            skLineSegment(sketch, "E1994", {"start": v(6.33, 1.97) * mm, "end": v(6.37, 2.06) * mm});
            skLineSegment(sketch, "E1995", {"start": v(6.37, 2.06) * mm, "end": v(6.41, 2.16) * mm});
            skLineSegment(sketch, "E1996", {"start": v(6.41, 2.16) * mm, "end": v(6.45, 2.25) * mm});
            skLineSegment(sketch, "E1997", {"start": v(6.45, 2.25) * mm, "end": v(6.5, 2.35) * mm});
            skLineSegment(sketch, "E1998", {"start": v(6.5, 2.35) * mm, "end": v(6.53, 2.44) * mm});
            skLineSegment(sketch, "E1999", {"start": v(6.53, 2.44) * mm, "end": v(6.57, 2.54) * mm});
            skLineSegment(sketch, "E2000", {"start": v(6.57, 2.54) * mm, "end": v(6.6, 2.63) * mm});
            skLineSegment(sketch, "E2001", {"start": v(6.6, 2.63) * mm, "end": v(6.65, 2.72) * mm});
            skLineSegment(sketch, "E2002", {"start": v(6.65, 2.72) * mm, "end": v(6.69, 2.82) * mm});
            skLineSegment(sketch, "E2003", {"start": v(6.69, 2.82) * mm, "end": v(6.73, 2.91) * mm});
            skLineSegment(sketch, "E2004", {"start": v(6.73, 2.91) * mm, "end": v(6.77, 3) * mm});
            skLineSegment(sketch, "E2005", {"start": v(6.77, 3) * mm, "end": v(6.8, 3.1) * mm});
            skLineSegment(sketch, "E2006", {"start": v(6.8, 3.1) * mm, "end": v(6.83, 3.17) * mm});
            skLineSegment(sketch, "E2007", {"start": v(6.83, 3.17) * mm, "end": v(6.87, 3.24) * mm});
            skLineSegment(sketch, "E2008", {"start": v(6.87, 3.24) * mm, "end": v(6.9, 3.32) * mm});
            skLineSegment(sketch, "E2009", {"start": v(6.9, 3.32) * mm, "end": v(6.94, 3.4) * mm});
            skLineSegment(sketch, "E2010", {"start": v(6.94, 3.4) * mm, "end": v(6.97, 3.48) * mm});
            skLineSegment(sketch, "E2011", {"start": v(6.97, 3.48) * mm, "end": v(7.01, 3.56) * mm});
            skLineSegment(sketch, "E2012", {"start": v(7.01, 3.56) * mm, "end": v(7.05, 3.65) * mm});
            skLineSegment(sketch, "E2013", {"start": v(7.05, 3.65) * mm, "end": v(7.09, 3.74) * mm});
            skLineSegment(sketch, "E2014", {"start": v(7.09, 3.74) * mm, "end": v(7.12, 3.83) * mm});
            skLineSegment(sketch, "E2015", {"start": v(7.12, 3.83) * mm, "end": v(7.16, 3.93) * mm});
            skLineSegment(sketch, "E2016", {"start": v(7.16, 3.93) * mm, "end": v(7.2, 4.02) * mm});
            skLineSegment(sketch, "E2017", {"start": v(7.2, 4.02) * mm, "end": v(7.23, 4.12) * mm});
            skLineSegment(sketch, "E2018", {"start": v(7.23, 4.12) * mm, "end": v(7.26, 4.21) * mm});
            skLineSegment(sketch, "E2019", {"start": v(7.26, 4.21) * mm, "end": v(7.28, 4.3) * mm});
            skLineSegment(sketch, "E2020", {"start": v(7.28, 4.3) * mm, "end": v(7.3, 4.4) * mm});
            skLineSegment(sketch, "E2021", {"start": v(7.3, 4.4) * mm, "end": v(7.33, 4.5) * mm});
            skLineSegment(sketch, "E2022", {"start": v(7.33, 4.5) * mm, "end": v(7.34, 4.6) * mm});
            skLineSegment(sketch, "E2023", {"start": v(7.34, 4.6) * mm, "end": v(7.35, 4.68) * mm});
            skLineSegment(sketch, "E2024", {"start": v(7.35, 4.68) * mm, "end": v(7.35, 4.77) * mm});
            skLineSegment(sketch, "E2025", {"start": v(7.35, 4.77) * mm, "end": v(7.35, 4.86) * mm});
            skLineSegment(sketch, "E2026", {"start": v(7.35, 4.86) * mm, "end": v(7.34, 4.95) * mm});
            skLineSegment(sketch, "E2027", {"start": v(7.34, 4.95) * mm, "end": v(7.32, 5.03) * mm});
            skLineSegment(sketch, "E2028", {"start": v(7.32, 5.03) * mm, "end": v(7.3, 5.11) * mm});
            skLineSegment(sketch, "E2029", {"start": v(7.3, 5.11) * mm, "end": v(7.26, 5.19) * mm});
            skLineSegment(sketch, "E2030", {"start": v(7.26, 5.19) * mm, "end": v(7.22, 5.26) * mm});
            skLineSegment(sketch, "E2031", {"start": v(7.22, 5.26) * mm, "end": v(7.17, 5.33) * mm});
            skLineSegment(sketch, "E2032", {"start": v(7.17, 5.33) * mm, "end": v(7.1, 5.39) * mm});
            skLineSegment(sketch, "E2033", {"start": v(7.1, 5.39) * mm, "end": v(7.04, 5.45) * mm});
            skLineSegment(sketch, "E2034", {"start": v(7.04, 5.45) * mm, "end": v(6.97, 5.5) * mm});
            skLineSegment(sketch, "E2035", {"start": v(6.97, 5.5) * mm, "end": v(6.9, 5.55) * mm});
            skLineSegment(sketch, "E2036", {"start": v(6.9, 5.55) * mm, "end": v(6.82, 5.6) * mm});
            skLineSegment(sketch, "E2037", {"start": v(6.82, 5.6) * mm, "end": v(6.74, 5.63) * mm});
            skLineSegment(sketch, "E2038", {"start": v(6.74, 5.63) * mm, "end": v(6.66, 5.66) * mm});
            skLineSegment(sketch, "E2039", {"start": v(6.66, 5.66) * mm, "end": v(6.58, 5.7) * mm});
            skLineSegment(sketch, "E2040", {"start": v(6.58, 5.7) * mm, "end": v(6.5, 5.72) * mm});
            skLineSegment(sketch, "E2041", {"start": v(6.5, 5.72) * mm, "end": v(6.41, 5.74) * mm});
            skLineSegment(sketch, "E2042", {"start": v(6.41, 5.74) * mm, "end": v(6.33, 5.76) * mm});
            skLineSegment(sketch, "E2043", {"start": v(6.33, 5.76) * mm, "end": v(6.24, 5.77) * mm});
            skLineSegment(sketch, "E2044", {"start": v(6.24, 5.77) * mm, "end": v(6.15, 5.78) * mm});
            skLineSegment(sketch, "E2045", {"start": v(6.15, 5.78) * mm, "end": v(6.05, 5.78) * mm});
            skLineSegment(sketch, "E2046", {"start": v(6.05, 5.78) * mm, "end": v(5.96, 5.79) * mm});
            skLineSegment(sketch, "E2047", {"start": v(5.96, 5.79) * mm, "end": v(5.87, 5.79) * mm});
            skLineSegment(sketch, "E2048", {"start": v(5.87, 5.79) * mm, "end": v(5.77, 5.78) * mm});
            skLineSegment(sketch, "E2049", {"start": v(5.77, 5.78) * mm, "end": v(5.68, 5.78) * mm});
            skLineSegment(sketch, "E2050", {"start": v(5.68, 5.78) * mm, "end": v(5.58, 5.77) * mm});
            skLineSegment(sketch, "E2051", {"start": v(5.58, 5.77) * mm, "end": v(5.48, 5.76) * mm});
            skLineSegment(sketch, "E2052", {"start": v(5.48, 5.76) * mm, "end": v(5.38, 5.75) * mm});
            skLineSegment(sketch, "E2053", {"start": v(5.38, 5.75) * mm, "end": v(5.28, 5.73) * mm});
            skLineSegment(sketch, "E2054", {"start": v(5.28, 5.73) * mm, "end": v(5.18, 5.71) * mm});
            skLineSegment(sketch, "E2055", {"start": v(5.18, 5.71) * mm, "end": v(5.08, 5.7) * mm});
            skLineSegment(sketch, "E2056", {"start": v(5.08, 5.7) * mm, "end": v(4.98, 5.68) * mm});
            skLineSegment(sketch, "E2057", {"start": v(4.98, 5.68) * mm, "end": v(4.88, 5.65) * mm});
            skLineSegment(sketch, "E2058", {"start": v(4.88, 5.65) * mm, "end": v(4.79, 5.63) * mm});
            skLineSegment(sketch, "E2059", {"start": v(4.79, 5.63) * mm, "end": v(4.69, 5.6) * mm});
            skLineSegment(sketch, "E2060", {"start": v(4.69, 5.6) * mm, "end": v(4.59, 5.58) * mm});
            skLineSegment(sketch, "E2061", {"start": v(4.59, 5.58) * mm, "end": v(4.49, 5.56) * mm});
            skLineSegment(sketch, "E2062", {"start": v(4.49, 5.56) * mm, "end": v(4.39, 5.53) * mm});
            skLineSegment(sketch, "E2063", {"start": v(4.39, 5.53) * mm, "end": v(4.29, 5.5) * mm});
            skLineSegment(sketch, "E2064", {"start": v(4.29, 5.5) * mm, "end": v(4.2, 5.48) * mm});
            skLineSegment(sketch, "E2065", {"start": v(4.2, 5.48) * mm, "end": v(4.1, 5.46) * mm});
            skLineSegment(sketch, "E2066", {"start": v(4.1, 5.46) * mm, "end": v(4, 5.43) * mm});
            skLineSegment(sketch, "E2067", {"start": v(4, 5.43) * mm, "end": v(3.9, 5.4) * mm});
            skLineSegment(sketch, "E2068", {"start": v(3.9, 5.4) * mm, "end": v(3.81, 5.38) * mm});
            skLineSegment(sketch, "E2069", {"start": v(3.81, 5.38) * mm, "end": v(3.72, 5.35) * mm});
            skLineSegment(sketch, "E2070", {"start": v(3.72, 5.35) * mm, "end": v(3.63, 5.33) * mm});
            skLineSegment(sketch, "E2071", {"start": v(3.63, 5.33) * mm, "end": v(3.54, 5.3) * mm});
            skLineSegment(sketch, "E2072", {"start": v(3.54, 5.3) * mm, "end": v(3.45, 5.29) * mm});
            skLineSegment(sketch, "E2073", {"start": v(3.45, 5.29) * mm, "end": v(3.36, 5.27) * mm});
            skLineSegment(sketch, "E2074", {"start": v(3.36, 5.27) * mm, "end": v(3.28, 5.25) * mm});
            skLineSegment(sketch, "E2075", {"start": v(3.28, 5.25) * mm, "end": v(3.2, 5.23) * mm});
            skLineSegment(sketch, "E2076", {"start": v(3.2, 5.23) * mm, "end": v(3.12, 5.22) * mm});
            skLineSegment(sketch, "E2077", {"start": v(3.12, 5.22) * mm, "end": v(3.04, 5.2) * mm});
            skLineSegment(sketch, "E2078", {"start": v(3.04, 5.2) * mm, "end": v(2.96, 5.2) * mm});
            skLineSegment(sketch, "E2079", {"start": v(2.96, 5.2) * mm, "end": v(2.89, 5.2) * mm});
            skLineSegment(sketch, "E2080", {"start": v(2.89, 5.2) * mm, "end": v(2.81, 5.19) * mm});
            skLineSegment(sketch, "E2081", {"start": v(2.81, 5.19) * mm, "end": v(2.75, 5.18) * mm});
            skLineSegment(sketch, "E2082", {"start": v(2.75, 5.18) * mm, "end": v(2.65, 5.19) * mm});
            skLineSegment(sketch, "E2083", {"start": v(2.65, 5.19) * mm, "end": v(2.55, 5.2) * mm});
            skLineSegment(sketch, "E2084", {"start": v(2.55, 5.2) * mm, "end": v(2.46, 5.2) * mm});
            skLineSegment(sketch, "E2085", {"start": v(2.46, 5.2) * mm, "end": v(2.36, 5.22) * mm});
            skLineSegment(sketch, "E2086", {"start": v(2.36, 5.22) * mm, "end": v(2.27, 5.25) * mm});
            skLineSegment(sketch, "E2087", {"start": v(2.27, 5.25) * mm, "end": v(2.18, 5.27) * mm});
            skLineSegment(sketch, "E2088", {"start": v(2.18, 5.27) * mm, "end": v(2.08, 5.3) * mm});
            skLineSegment(sketch, "E2089", {"start": v(2.08, 5.3) * mm, "end": v(1.99, 5.32) * mm});
            skLineSegment(sketch, "E2090", {"start": v(1.99, 5.32) * mm, "end": v(1.9, 5.35) * mm});
            skLineSegment(sketch, "E2091", {"start": v(1.9, 5.35) * mm, "end": v(1.8, 5.38) * mm});
            skLineSegment(sketch, "E2092", {"start": v(1.8, 5.38) * mm, "end": v(1.7, 5.4) * mm});
            skLineSegment(sketch, "E2093", {"start": v(1.7, 5.4) * mm, "end": v(1.61, 5.43) * mm});
            skLineSegment(sketch, "E2094", {"start": v(1.61, 5.43) * mm, "end": v(1.52, 5.46) * mm});
            skLineSegment(sketch, "E2095", {"start": v(1.52, 5.46) * mm, "end": v(1.42, 5.48) * mm});
            skLineSegment(sketch, "E2096", {"start": v(1.42, 5.48) * mm, "end": v(1.32, 5.5) * mm});
            skLineSegment(sketch, "E2097", {"start": v(1.32, 5.5) * mm, "end": v(1.22, 5.5) * mm});
            skLineSegment(sketch, "E2098", {"start": v(1.22, 5.5) * mm, "end": v(1.13, 5.51) * mm});
            skLineSegment(sketch, "E2099", {"start": v(1.13, 5.51) * mm, "end": v(1.02, 5.51) * mm});
            skLineSegment(sketch, "E2100", {"start": v(1.02, 5.51) * mm, "end": v(0.92, 5.5) * mm});
            skLineSegment(sketch, "E2101", {"start": v(0.92, 5.5) * mm, "end": v(0.82, 5.5) * mm});
            skLineSegment(sketch, "E2102", {"start": v(0.82, 5.5) * mm, "end": v(0.72, 5.49) * mm});
            skLineSegment(sketch, "E2103", {"start": v(0.72, 5.49) * mm, "end": v(0.62, 5.48) * mm});
            skLineSegment(sketch, "E2104", {"start": v(0.62, 5.48) * mm, "end": v(0.52, 5.46) * mm});
            skLineSegment(sketch, "E2105", {"start": v(0.52, 5.46) * mm, "end": v(0.42, 5.45) * mm});
            skLineSegment(sketch, "E2106", {"start": v(0.42, 5.45) * mm, "end": v(0.32, 5.43) * mm});
            skLineSegment(sketch, "E2107", {"start": v(0.32, 5.43) * mm, "end": v(0.22, 5.42) * mm});
            skLineSegment(sketch, "E2108", {"start": v(0.22, 5.42) * mm, "end": v(0.12, 5.4) * mm});
            skLineSegment(sketch, "E2109", {"start": v(0.12, 5.4) * mm, "end": v(0.02, 5.38) * mm});
            skLineSegment(sketch, "E2110", {"start": v(0.02, 5.38) * mm, "end": v(-0.08, 5.36) * mm});
            skLineSegment(sketch, "E2111", {"start": v(-0.08, 5.36) * mm, "end": v(-0.17, 5.34) * mm});
            skLineSegment(sketch, "E2112", {"start": v(-0.17, 5.34) * mm, "end": v(-0.27, 5.32) * mm});
            skLineSegment(sketch, "E2113", {"start": v(-0.27, 5.32) * mm, "end": v(-0.37, 5.3) * mm});
            skLineSegment(sketch, "E2114", {"start": v(-0.37, 5.3) * mm, "end": v(-0.46, 5.27) * mm});
            skLineSegment(sketch, "E2115", {"start": v(-0.46, 5.27) * mm, "end": v(-0.56, 5.24) * mm});
            skLineSegment(sketch, "E2116", {"start": v(-0.56, 5.24) * mm, "end": v(-0.66, 5.22) * mm});
            skLineSegment(sketch, "E2117", {"start": v(-0.66, 5.22) * mm, "end": v(-0.75, 5.2) * mm});
            skLineSegment(sketch, "E2118", {"start": v(-0.75, 5.2) * mm, "end": v(-0.85, 5.16) * mm});
            skLineSegment(sketch, "E2119", {"start": v(-0.85, 5.16) * mm, "end": v(-0.94, 5.13) * mm});
            skLineSegment(sketch, "E2120", {"start": v(-0.94, 5.13) * mm, "end": v(-1.04, 5.1) * mm});
            skLineSegment(sketch, "E2121", {"start": v(-1.04, 5.1) * mm, "end": v(-1.13, 5.07) * mm});
            skLineSegment(sketch, "E2122", {"start": v(-1.13, 5.07) * mm, "end": v(-1.22, 5.04) * mm});
            skLineSegment(sketch, "E2123", {"start": v(-1.22, 5.04) * mm, "end": v(-1.32, 5) * mm});
            skLineSegment(sketch, "E2124", {"start": v(-1.32, 5) * mm, "end": v(-1.41, 4.97) * mm});
            skLineSegment(sketch, "E2125", {"start": v(-1.41, 4.97) * mm, "end": v(-1.5, 4.94) * mm});
            skLineSegment(sketch, "E2126", {"start": v(-1.5, 4.94) * mm, "end": v(-1.6, 4.9) * mm});
            skLineSegment(sketch, "E2127", {"start": v(-1.6, 4.9) * mm, "end": v(-1.69, 4.86) * mm});
            skLineSegment(sketch, "E2128", {"start": v(-1.69, 4.86) * mm, "end": v(-1.78, 4.82) * mm});
            skLineSegment(sketch, "E2129", {"start": v(-1.78, 4.82) * mm, "end": v(-1.87, 4.79) * mm});
            skLineSegment(sketch, "E2130", {"start": v(-1.87, 4.79) * mm, "end": v(-1.96, 4.75) * mm});
            skLineSegment(sketch, "E2131", {"start": v(-1.96, 4.75) * mm, "end": v(-2.05, 4.7) * mm});
            skLineSegment(sketch, "E2132", {"start": v(-2.05, 4.7) * mm, "end": v(-2.14, 4.66) * mm});
            skLineSegment(sketch, "E2133", {"start": v(-2.14, 4.66) * mm, "end": v(-2.23, 4.62) * mm});
            skLineSegment(sketch, "E2134", {"start": v(-2.23, 4.62) * mm, "end": v(-2.32, 4.58) * mm});
            skLineSegment(sketch, "E2135", {"start": v(-2.32, 4.58) * mm, "end": v(-2.4, 4.53) * mm});
            skLineSegment(sketch, "E2136", {"start": v(-2.4, 4.53) * mm, "end": v(-2.5, 4.49) * mm});
            skLineSegment(sketch, "E2137", {"start": v(-2.5, 4.49) * mm, "end": v(-2.58, 4.44) * mm});
            skLineSegment(sketch, "E2138", {"start": v(-2.58, 4.44) * mm, "end": v(-2.67, 4.4) * mm});
            skLineSegment(sketch, "E2139", {"start": v(-2.67, 4.4) * mm, "end": v(-2.76, 4.35) * mm});
            skLineSegment(sketch, "E2140", {"start": v(-2.76, 4.35) * mm, "end": v(-2.84, 4.3) * mm});
            skLineSegment(sketch, "E2141", {"start": v(-2.84, 4.3) * mm, "end": v(-2.93, 4.25) * mm});
            skLineSegment(sketch, "E2142", {"start": v(-2.93, 4.25) * mm, "end": v(-3.01, 4.2) * mm});
            skLineSegment(sketch, "E2143", {"start": v(-3.01, 4.2) * mm, "end": v(-3.1, 4.15) * mm});
            skLineSegment(sketch, "E2144", {"start": v(-3.1, 4.15) * mm, "end": v(-3.18, 4.1) * mm});
            skLineSegment(sketch, "E2145", {"start": v(-3.18, 4.1) * mm, "end": v(-3.27, 4.04) * mm});
            skLineSegment(sketch, "E2146", {"start": v(-3.27, 4.04) * mm, "end": v(-3.35, 3.99) * mm});
            skLineSegment(sketch, "E2147", {"start": v(-3.35, 3.99) * mm, "end": v(-3.44, 3.93) * mm});
            skLineSegment(sketch, "E2148", {"start": v(-3.44, 3.93) * mm, "end": v(-3.52, 3.88) * mm});
            skLineSegment(sketch, "E2149", {"start": v(-3.52, 3.88) * mm, "end": v(-3.6, 3.82) * mm});
            skLineSegment(sketch, "E2150", {"start": v(-3.6, 3.82) * mm, "end": v(-3.68, 3.77) * mm});
            skLineSegment(sketch, "E2151", {"start": v(-3.68, 3.77) * mm, "end": v(-3.76, 3.7) * mm});
            skLineSegment(sketch, "E2152", {"start": v(-3.76, 3.7) * mm, "end": v(-3.84, 3.65) * mm});
            skLineSegment(sketch, "E2153", {"start": v(-3.84, 3.65) * mm, "end": v(-3.92, 3.6) * mm});
            skLineSegment(sketch, "E2154", {"start": v(-3.92, 3.6) * mm, "end": v(-4, 3.53) * mm});
            skLineSegment(sketch, "E2155", {"start": v(-4, 3.53) * mm, "end": v(-4.08, 3.47) * mm});
            skLineSegment(sketch, "E2156", {"start": v(-4.08, 3.47) * mm, "end": v(-4.16, 3.41) * mm});
            skLineSegment(sketch, "E2157", {"start": v(-4.16, 3.41) * mm, "end": v(-4.24, 3.35) * mm});
            skLineSegment(sketch, "E2158", {"start": v(-4.24, 3.35) * mm, "end": v(-4.32, 3.29) * mm});
            skLineSegment(sketch, "E2159", {"start": v(-4.32, 3.29) * mm, "end": v(-4.4, 3.22) * mm});
            skLineSegment(sketch, "E2160", {"start": v(-4.4, 3.22) * mm, "end": v(-4.47, 3.16) * mm});
            skLineSegment(sketch, "E2161", {"start": v(-4.47, 3.16) * mm, "end": v(-4.55, 3.1) * mm});
            skLineSegment(sketch, "E2162", {"start": v(-4.55, 3.1) * mm, "end": v(-4.63, 3.03) * mm});
            skLineSegment(sketch, "E2163", {"start": v(-4.63, 3.03) * mm, "end": v(-4.7, 2.97) * mm});
            skLineSegment(sketch, "E2164", {"start": v(-4.7, 2.97) * mm, "end": v(-4.78, 2.9) * mm});
            skLineSegment(sketch, "E2165", {"start": v(-4.78, 2.9) * mm, "end": v(-4.85, 2.83) * mm});
            skLineSegment(sketch, "E2166", {"start": v(-4.85, 2.83) * mm, "end": v(-4.93, 2.77) * mm});
            skLineSegment(sketch, "E2167", {"start": v(-4.93, 2.77) * mm, "end": v(-5, 2.7) * mm});
            skLineSegment(sketch, "E2168", {"start": v(-5, 2.7) * mm, "end": v(-5.07, 2.63) * mm});
            skLineSegment(sketch, "E2169", {"start": v(-5.07, 2.63) * mm, "end": v(-5.14, 2.56) * mm});
            skLineSegment(sketch, "E2170", {"start": v(-5.14, 2.56) * mm, "end": v(-5.22, 2.5) * mm});
            skLineSegment(sketch, "E2171", {"start": v(-5.22, 2.5) * mm, "end": v(-5.29, 2.42) * mm});
            skLineSegment(sketch, "E2172", {"start": v(-5.29, 2.42) * mm, "end": v(-5.36, 2.35) * mm});
            skLineSegment(sketch, "E2173", {"start": v(-5.36, 2.35) * mm, "end": v(-5.43, 2.28) * mm});
            skLineSegment(sketch, "E2174", {"start": v(-5.43, 2.28) * mm, "end": v(-5.5, 2.2) * mm});
            skLineSegment(sketch, "E2175", {"start": v(-5.5, 2.2) * mm, "end": v(-5.57, 2.14) * mm});
            skLineSegment(sketch, "E2176", {"start": v(-5.57, 2.14) * mm, "end": v(-5.64, 2.06) * mm});
            skLineSegment(sketch, "E2177", {"start": v(-5.64, 2.06) * mm, "end": v(-5.7, 1.99) * mm});
            skLineSegment(sketch, "E2178", {"start": v(-5.7, 1.99) * mm, "end": v(-5.77, 1.92) * mm});
            skLineSegment(sketch, "E2179", {"start": v(-5.77, 1.92) * mm, "end": v(-5.84, 1.84) * mm});
            skLineSegment(sketch, "E2180", {"start": v(-5.84, 1.84) * mm, "end": v(-5.9, 1.77) * mm});
            skLineSegment(sketch, "E2181", {"start": v(-5.9, 1.77) * mm, "end": v(-5.97, 1.7) * mm});
            skLineSegment(sketch, "E2182", {"start": v(-5.97, 1.7) * mm, "end": v(-6.04, 1.62) * mm});
            skLineSegment(sketch, "E2183", {"start": v(-6.04, 1.62) * mm, "end": v(-6.1, 1.54) * mm});
            skLineSegment(sketch, "E2184", {"start": v(-6.1, 1.54) * mm, "end": v(-6.17, 1.46) * mm});
            skLineSegment(sketch, "E2185", {"start": v(-6.17, 1.46) * mm, "end": v(-6.23, 1.39) * mm});
            skLineSegment(sketch, "E2186", {"start": v(-6.23, 1.39) * mm, "end": v(-6.3, 1.3) * mm});
            skLineSegment(sketch, "E2187", {"start": v(-6.3, 1.3) * mm, "end": v(-6.36, 1.23) * mm});
            skLineSegment(sketch, "E2188", {"start": v(-6.36, 1.23) * mm, "end": v(-6.42, 1.15) * mm});
            skLineSegment(sketch, "E2189", {"start": v(-6.42, 1.15) * mm, "end": v(-6.48, 1.07) * mm});
            skLineSegment(sketch, "E2190", {"start": v(-6.48, 1.07) * mm, "end": v(-6.54, 1) * mm});
            skLineSegment(sketch, "E2191", {"start": v(-6.54, 1) * mm, "end": v(-6.6, 0.91) * mm});
            skLineSegment(sketch, "E2192", {"start": v(-6.6, 0.91) * mm, "end": v(-6.66, 0.83) * mm});
            skLineSegment(sketch, "E2193", {"start": v(-6.66, 0.83) * mm, "end": v(-6.72, 0.75) * mm});
            skLineSegment(sketch, "E2194", {"start": v(-6.72, 0.75) * mm, "end": v(-6.78, 0.67) * mm});
            skLineSegment(sketch, "E2195", {"start": v(-6.78, 0.67) * mm, "end": v(-6.84, 0.6) * mm});
            skLineSegment(sketch, "E2196", {"start": v(-6.84, 0.6) * mm, "end": v(-6.87, 0.54) * mm});
            skLineSegment(sketch, "E2197", {"start": v(-6.87, 0.54) * mm, "end": v(-6.9, 0.49) * mm});
            skLineSegment(sketch, "E2198", {"start": v(-6.9, 0.49) * mm, "end": v(-6.95, 0.43) * mm});
            skLineSegment(sketch, "E2199", {"start": v(-6.95, 0.43) * mm, "end": v(-6.98, 0.38) * mm});
            skLineSegment(sketch, "E2200", {"start": v(-6.98, 0.38) * mm, "end": v(-7.02, 0.32) * mm});
            skLineSegment(sketch, "E2201", {"start": v(-7.02, 0.32) * mm, "end": v(-7.05, 0.26) * mm});
            skLineSegment(sketch, "E2202", {"start": v(-7.05, 0.26) * mm, "end": v(-7.1, 0.2) * mm});
            skLineSegment(sketch, "E2203", {"start": v(-7.1, 0.2) * mm, "end": v(-7.13, 0.14) * mm});
            skLineSegment(sketch, "E2204", {"start": v(-7.13, 0.14) * mm, "end": v(-7.16, 0.08) * mm});
            skLineSegment(sketch, "E2205", {"start": v(-7.16, 0.08) * mm, "end": v(-7.2, 0.01) * mm});
            skLineSegment(sketch, "E2206", {"start": v(-7.2, 0.01) * mm, "end": v(-7.24, -0.05) * mm});
            skLineSegment(sketch, "E2207", {"start": v(-7.24, -0.05) * mm, "end": v(-7.27, -0.12) * mm});
            skLineSegment(sketch, "E2208", {"start": v(-7.27, -0.12) * mm, "end": v(-7.3, -0.18) * mm});
            skLineSegment(sketch, "E2209", {"start": v(-7.3, -0.18) * mm, "end": v(-7.35, -0.25) * mm});
            skLineSegment(sketch, "E2210", {"start": v(-7.35, -0.25) * mm, "end": v(-7.38, -0.32) * mm});
            skLineSegment(sketch, "E2211", {"start": v(-7.38, -0.32) * mm, "end": v(-7.42, -0.4) * mm});
            skLineSegment(sketch, "E2212", {"start": v(-7.42, -0.4) * mm, "end": v(-7.46, -0.46) * mm});
            skLineSegment(sketch, "E2213", {"start": v(-7.46, -0.46) * mm, "end": v(-7.5, -0.53) * mm});
            skLineSegment(sketch, "E2214", {"start": v(-7.5, -0.53) * mm, "end": v(-7.53, -0.6) * mm});
            skLineSegment(sketch, "E2215", {"start": v(-7.53, -0.6) * mm, "end": v(-7.57, -0.68) * mm});
            skLineSegment(sketch, "E2216", {"start": v(-7.57, -0.68) * mm, "end": v(-7.6, -0.75) * mm});
            skLineSegment(sketch, "E2217", {"start": v(-7.6, -0.75) * mm, "end": v(-7.64, -0.83) * mm});
            skLineSegment(sketch, "E2218", {"start": v(-7.64, -0.83) * mm, "end": v(-7.68, -0.9) * mm});
            skLineSegment(sketch, "E2219", {"start": v(-7.68, -0.9) * mm, "end": v(-7.72, -0.98) * mm});
            skLineSegment(sketch, "E2220", {"start": v(-7.72, -0.98) * mm, "end": v(-7.76, -1.06) * mm});
            skLineSegment(sketch, "E2221", {"start": v(-7.76, -1.06) * mm, "end": v(-7.8, -1.13) * mm});
            skLineSegment(sketch, "E2222", {"start": v(-7.8, -1.13) * mm, "end": v(-7.84, -1.21) * mm});
            skLineSegment(sketch, "E2223", {"start": v(-7.84, -1.21) * mm, "end": v(-7.87, -1.3) * mm});
            skLineSegment(sketch, "E2224", {"start": v(-7.87, -1.3) * mm, "end": v(-7.91, -1.37) * mm});
            skLineSegment(sketch, "E2225", {"start": v(-7.91, -1.37) * mm, "end": v(-7.95, -1.45) * mm});
            skLineSegment(sketch, "E2226", {"start": v(-7.95, -1.45) * mm, "end": v(-8, -1.53) * mm});
            skLineSegment(sketch, "E2227", {"start": v(-8, -1.53) * mm, "end": v(-8.03, -1.6) * mm});
            skLineSegment(sketch, "E2228", {"start": v(-8.03, -1.6) * mm, "end": v(-8.07, -1.69) * mm});
            skLineSegment(sketch, "E2229", {"start": v(-8.07, -1.69) * mm, "end": v(-8.11, -1.77) * mm});
            skLineSegment(sketch, "E2230", {"start": v(-8.11, -1.77) * mm, "end": v(-8.15, -1.85) * mm});
            skLineSegment(sketch, "E2231", {"start": v(-8.15, -1.85) * mm, "end": v(-8.2, -1.93) * mm});
            skLineSegment(sketch, "E2232", {"start": v(-8.2, -1.93) * mm, "end": v(-8.23, -2.01) * mm});
            skLineSegment(sketch, "E2233", {"start": v(-8.23, -2.01) * mm, "end": v(-8.28, -2.1) * mm});
            skLineSegment(sketch, "E2234", {"start": v(-8.28, -2.1) * mm, "end": v(-8.32, -2.18) * mm});
            skLineSegment(sketch, "E2235", {"start": v(-8.32, -2.18) * mm, "end": v(-8.36, -2.26) * mm});
            skLineSegment(sketch, "E2236", {"start": v(-8.36, -2.26) * mm, "end": v(-8.4, -2.34) * mm});
            skLineSegment(sketch, "E2237", {"start": v(-8.4, -2.34) * mm, "end": v(-8.44, -2.42) * mm});
            skLineSegment(sketch, "E2238", {"start": v(-8.44, -2.42) * mm, "end": v(-8.49, -2.5) * mm});
            skLineSegment(sketch, "E2239", {"start": v(-8.49, -2.5) * mm, "end": v(-8.53, -2.59) * mm});
            skLineSegment(sketch, "E2240", {"start": v(-8.53, -2.59) * mm, "end": v(-8.57, -2.67) * mm});
            skLineSegment(sketch, "E2241", {"start": v(-8.57, -2.67) * mm, "end": v(-8.62, -2.75) * mm});
            skLineSegment(sketch, "E2242", {"start": v(-8.62, -2.75) * mm, "end": v(-8.66, -2.83) * mm});
            skLineSegment(sketch, "E2243", {"start": v(-8.66, -2.83) * mm, "end": v(-8.7, -2.91) * mm});
            skLineSegment(sketch, "E2244", {"start": v(-8.7, -2.91) * mm, "end": v(-8.75, -3) * mm});
            skLineSegment(sketch, "E2245", {"start": v(-8.75, -3) * mm, "end": v(-8.8, -3.07) * mm});
            skLineSegment(sketch, "E2246", {"start": v(-8.8, -3.07) * mm, "end": v(-8.84, -3.15) * mm});
            skLineSegment(sketch, "E2247", {"start": v(-8.84, -3.15) * mm, "end": v(-8.88, -3.23) * mm});
            skLineSegment(sketch, "E2248", {"start": v(-8.88, -3.23) * mm, "end": v(-8.93, -3.31) * mm});
            skLineSegment(sketch, "E2249", {"start": v(-8.93, -3.31) * mm, "end": v(-8.98, -3.39) * mm});
            skLineSegment(sketch, "E2250", {"start": v(-8.98, -3.39) * mm, "end": v(-9.02, -3.47) * mm});
            skLineSegment(sketch, "E2251", {"start": v(-9.02, -3.47) * mm, "end": v(-9.07, -3.55) * mm});
            skLineSegment(sketch, "E2252", {"start": v(-9.07, -3.55) * mm, "end": v(-9.12, -3.62) * mm});
            skLineSegment(sketch, "E2253", {"start": v(-9.12, -3.62) * mm, "end": v(-9.17, -3.7) * mm});
            skLineSegment(sketch, "E2254", {"start": v(-9.17, -3.7) * mm, "end": v(-9.22, -3.78) * mm});
            skLineSegment(sketch, "E2255", {"start": v(-9.22, -3.78) * mm, "end": v(-9.27, -3.85) * mm});
            skLineSegment(sketch, "E2256", {"start": v(-9.27, -3.85) * mm, "end": v(-9.32, -3.93) * mm});
            skLineSegment(sketch, "E2257", {"start": v(-9.32, -3.93) * mm, "end": v(-9.37, -4) * mm});
            skLineSegment(sketch, "E2258", {"start": v(-9.37, -4) * mm, "end": v(-9.42, -4.07) * mm});
            skLineSegment(sketch, "E2259", {"start": v(-9.42, -4.07) * mm, "end": v(-9.47, -4.14) * mm});
            skLineSegment(sketch, "E2260", {"start": v(-9.47, -4.14) * mm, "end": v(-9.52, -4.22) * mm});
            skLineSegment(sketch, "E2261", {"start": v(-9.52, -4.22) * mm, "end": v(-9.57, -4.29) * mm});
            skLineSegment(sketch, "E2262", {"start": v(-9.57, -4.29) * mm, "end": v(-9.62, -4.36) * mm});
            skLineSegment(sketch, "E2263", {"start": v(-9.62, -4.36) * mm, "end": v(-9.67, -4.42) * mm});
            skLineSegment(sketch, "E2264", {"start": v(-9.67, -4.42) * mm, "end": v(-9.73, -4.5) * mm});
            skLineSegment(sketch, "E2265", {"start": v(-9.73, -4.5) * mm, "end": v(-9.78, -4.56) * mm});
            skLineSegment(sketch, "E2266", {"start": v(-9.78, -4.56) * mm, "end": v(-9.84, -4.62) * mm});
            skLineSegment(sketch, "E2267", {"start": v(-9.84, -4.62) * mm, "end": v(-9.9, -4.69) * mm});
            skLineSegment(sketch, "E2268", {"start": v(-9.9, -4.69) * mm, "end": v(-9.95, -4.75) * mm});
            skLineSegment(sketch, "E2269", {"start": v(-9.95, -4.75) * mm, "end": v(-10, -4.81) * mm});
            skLineSegment(sketch, "E2270", {"start": v(-10, -4.81) * mm, "end": v(-10.06, -4.87) * mm});
            skLineSegment(sketch, "E2271", {"start": v(-10.06, -4.87) * mm, "end": v(-10.12, -4.93) * mm});
            skLineSegment(sketch, "E2272", {"start": v(-10.12, -4.93) * mm, "end": v(-10.17, -5) * mm});
            skLineSegment(sketch, "E2273", {"start": v(-10.17, -5) * mm, "end": v(-10.23, -5.05) * mm});
            skLineSegment(sketch, "E2274", {"start": v(-10.23, -5.05) * mm, "end": v(-10.3, -5.1) * mm});
            skLineSegment(sketch, "E2275", {"start": v(-10.3, -5.1) * mm, "end": v(-10.35, -5.16) * mm});
            skLineSegment(sketch, "E2276", {"start": v(-10.35, -5.16) * mm, "end": v(-10.4, -5.21) * mm});
            skLineSegment(sketch, "E2277", {"start": v(-10.4, -5.21) * mm, "end": v(-10.47, -5.26) * mm});
            skLineSegment(sketch, "E2278", {"start": v(-10.47, -5.26) * mm, "end": v(-10.53, -5.31) * mm});
            skLineSegment(sketch, "E2279", {"start": v(-10.53, -5.31) * mm, "end": v(-10.6, -5.36) * mm});
            skLineSegment(sketch, "E2280", {"start": v(-10.6, -5.36) * mm, "end": v(-10.66, -5.4) * mm});
            skLineSegment(sketch, "E2281", {"start": v(-10.66, -5.4) * mm, "end": v(-10.72, -5.45) * mm});
            skLineSegment(sketch, "E2282", {"start": v(-10.72, -5.45) * mm, "end": v(-10.78, -5.5) * mm});
            skLineSegment(sketch, "E2283", {"start": v(-10.78, -5.5) * mm, "end": v(-10.85, -5.54) * mm});
            skLineSegment(sketch, "E2284", {"start": v(-10.85, -5.54) * mm, "end": v(-10.91, -5.58) * mm});
            skLineSegment(sketch, "E2285", {"start": v(-10.91, -5.58) * mm, "end": v(-10.98, -5.61) * mm});
            skLineSegment(sketch, "E2286", {"start": v(-10.98, -5.61) * mm, "end": v(-11.04, -5.65) * mm});
            skLineSegment(sketch, "E2287", {"start": v(-11.04, -5.65) * mm, "end": v(-11.11, -5.68) * mm});
            skLineSegment(sketch, "E2288", {"start": v(-11.11, -5.68) * mm, "end": v(-11.18, -5.72) * mm});
            skLineSegment(sketch, "E2289", {"start": v(-11.18, -5.72) * mm, "end": v(-11.25, -5.75) * mm});
            skLineSegment(sketch, "E2290", {"start": v(-11.25, -5.75) * mm, "end": v(-11.32, -5.78) * mm});
            skLineSegment(sketch, "E2291", {"start": v(-11.32, -5.78) * mm, "end": v(-11.39, -5.8) * mm});
            skLineSegment(sketch, "E2292", {"start": v(-11.39, -5.8) * mm, "end": v(-11.46, -5.83) * mm});
            skLineSegment(sketch, "E2293", {"start": v(-11.46, -5.83) * mm, "end": v(-11.53, -5.85) * mm});
            skLineSegment(sketch, "E2294", {"start": v(-11.53, -5.85) * mm, "end": v(-11.6, -5.87) * mm});
            skLineSegment(sketch, "E2295", {"start": v(-11.6, -5.87) * mm, "end": v(-11.67, -5.89) * mm});
            skLineSegment(sketch, "E2296", {"start": v(-11.67, -5.89) * mm, "end": v(-11.74, -5.9) * mm});
            skLineSegment(sketch, "E2297", {"start": v(-11.74, -5.9) * mm, "end": v(-11.82, -5.92) * mm});
            skLineSegment(sketch, "E2298", {"start": v(-11.82, -5.92) * mm, "end": v(-11.9, -5.93) * mm});
            skLineSegment(sketch, "E2299", {"start": v(-11.9, -5.93) * mm, "end": v(-11.97, -5.94) * mm});
            skLineSegment(sketch, "E2300", {"start": v(-11.97, -5.94) * mm, "end": v(-12.05, -5.94) * mm});
            skLineSegment(sketch, "E2301", {"start": v(-12.05, -5.94) * mm, "end": v(-12.12, -5.95) * mm});
            skLineSegment(sketch, "E2302", {"start": v(-12.12, -5.95) * mm, "end": v(-12.2, -5.95) * mm});
            skLineSegment(sketch, "E2303", {"start": v(-12.2, -5.95) * mm, "end": v(-12.28, -5.95) * mm});
            skLineSegment(sketch, "E2304", {"start": v(-12.28, -5.95) * mm, "end": v(-12.36, -5.95) * mm});
            skLineSegment(sketch, "E2305", {"start": v(-12.36, -5.95) * mm, "end": v(-12.44, -5.94) * mm});
            skLineSegment(sketch, "E2306", {"start": v(-12.44, -5.94) * mm, "end": v(-12.52, -5.93) * mm});
            skLineSegment(sketch, "E2307", {"start": v(-12.52, -5.93) * mm, "end": v(-12.6, -5.92) * mm});
            skLineSegment(sketch, "E2308", {"start": v(-12.6, -5.92) * mm, "end": v(-12.69, -5.9) * mm});
            skLineSegment(sketch, "E2309", {"start": v(-12.69, -5.9) * mm, "end": v(-12.77, -5.9) * mm});
            skLineSegment(sketch, "E2310", {"start": v(-12.77, -5.9) * mm, "end": v(-12.85, -5.87) * mm});
            skLineSegment(sketch, "E2311", {"start": v(-12.85, -5.87) * mm, "end": v(-12.94, -5.85) * mm});
            skLineSegment(sketch, "E2312", {"start": v(-12.94, -5.85) * mm, "end": v(-13.03, -5.83) * mm});
            skLineSegment(sketch, "E2313", {"start": v(-13.03, -5.83) * mm, "end": v(-13.11, -5.8) * mm});
            skLineSegment(sketch, "E2314", {"start": v(-13.11, -5.8) * mm, "end": v(-13.2, -5.77) * mm});
            skLineSegment(sketch, "E2315", {"start": v(-13.2, -5.77) * mm, "end": v(-13.29, -5.74) * mm});
            skLineSegment(sketch, "E2316", {"start": v(-13.29, -5.74) * mm, "end": v(-13.38, -5.7) * mm});
            skLineSegment(sketch, "E2317", {"start": v(-13.38, -5.7) * mm, "end": v(-13.46, -5.67) * mm});
            skLineSegment(sketch, "E2318", {"start": v(-13.46, -5.67) * mm, "end": v(-13.55, -5.63) * mm});
            skLineSegment(sketch, "E2319", {"start": v(-13.55, -5.63) * mm, "end": v(-13.63, -5.59) * mm});
            skLineSegment(sketch, "E2320", {"start": v(-13.63, -5.59) * mm, "end": v(-13.7, -5.54) * mm});
            skLineSegment(sketch, "E2321", {"start": v(-13.7, -5.54) * mm, "end": v(-13.78, -5.5) * mm});
            skLineSegment(sketch, "E2322", {"start": v(-13.78, -5.5) * mm, "end": v(-13.86, -5.45) * mm});
            skLineSegment(sketch, "E2323", {"start": v(-13.86, -5.45) * mm, "end": v(-13.93, -5.4) * mm});
            skLineSegment(sketch, "E2324", {"start": v(-13.93, -5.4) * mm, "end": v(-14, -5.35) * mm});
            skLineSegment(sketch, "E2325", {"start": v(-14, -5.35) * mm, "end": v(-14.07, -5.3) * mm});
            skLineSegment(sketch, "E2326", {"start": v(-14.07, -5.3) * mm, "end": v(-14.14, -5.25) * mm});
            skLineSegment(sketch, "E2327", {"start": v(-14.14, -5.25) * mm, "end": v(-14.2, -5.19) * mm});
            skLineSegment(sketch, "E2328", {"start": v(-14.2, -5.19) * mm, "end": v(-14.27, -5.13) * mm});
            skLineSegment(sketch, "E2329", {"start": v(-14.27, -5.13) * mm, "end": v(-14.33, -5.07) * mm});
            skLineSegment(sketch, "E2330", {"start": v(-14.33, -5.07) * mm, "end": v(-14.4, -5) * mm});
            skLineSegment(sketch, "E2331", {"start": v(-14.4, -5) * mm, "end": v(-14.45, -4.95) * mm});
            skLineSegment(sketch, "E2332", {"start": v(-14.45, -4.95) * mm, "end": v(-14.5, -4.88) * mm});
            skLineSegment(sketch, "E2333", {"start": v(-14.5, -4.88) * mm, "end": v(-14.56, -4.81) * mm});
            skLineSegment(sketch, "E2334", {"start": v(-14.56, -4.81) * mm, "end": v(-14.61, -4.75) * mm});
            skLineSegment(sketch, "E2335", {"start": v(-14.61, -4.75) * mm, "end": v(-14.67, -4.68) * mm});
            skLineSegment(sketch, "E2336", {"start": v(-14.67, -4.68) * mm, "end": v(-14.72, -4.6) * mm});
            skLineSegment(sketch, "E2337", {"start": v(-14.72, -4.6) * mm, "end": v(-14.77, -4.53) * mm});
            skLineSegment(sketch, "E2338", {"start": v(-14.77, -4.53) * mm, "end": v(-14.81, -4.46) * mm});
            skLineSegment(sketch, "E2339", {"start": v(-14.81, -4.46) * mm, "end": v(-14.86, -4.38) * mm});
            skLineSegment(sketch, "E2340", {"start": v(-14.86, -4.38) * mm, "end": v(-14.9, -4.3) * mm});
            skLineSegment(sketch, "E2341", {"start": v(-14.9, -4.3) * mm, "end": v(-14.94, -4.23) * mm});
            skLineSegment(sketch, "E2342", {"start": v(-14.94, -4.23) * mm, "end": v(-14.98, -4.15) * mm});
            skLineSegment(sketch, "E2343", {"start": v(-14.98, -4.15) * mm, "end": v(-15.02, -4.07) * mm});
            skLineSegment(sketch, "E2344", {"start": v(-15.02, -4.07) * mm, "end": v(-15.06, -3.98) * mm});
            skLineSegment(sketch, "E2345", {"start": v(-15.06, -3.98) * mm, "end": v(-15.1, -3.9) * mm});
            skLineSegment(sketch, "E2346", {"start": v(-15.1, -3.9) * mm, "end": v(-15.13, -3.82) * mm});
            skLineSegment(sketch, "E2347", {"start": v(-15.13, -3.82) * mm, "end": v(-15.17, -3.73) * mm});
            skLineSegment(sketch, "E2348", {"start": v(-15.17, -3.73) * mm, "end": v(-15.2, -3.65) * mm});
            skLineSegment(sketch, "E2349", {"start": v(-15.2, -3.65) * mm, "end": v(-15.23, -3.56) * mm});
            skLineSegment(sketch, "E2350", {"start": v(-15.23, -3.56) * mm, "end": v(-15.26, -3.47) * mm});
            skLineSegment(sketch, "E2351", {"start": v(-15.26, -3.47) * mm, "end": v(-15.29, -3.38) * mm});
            skLineSegment(sketch, "E2352", {"start": v(-15.29, -3.38) * mm, "end": v(-15.31, -3.3) * mm});
            skLineSegment(sketch, "E2353", {"start": v(-15.31, -3.3) * mm, "end": v(-15.34, -3.2) * mm});
            skLineSegment(sketch, "E2354", {"start": v(-15.34, -3.2) * mm, "end": v(-15.36, -3.1) * mm});
            skLineSegment(sketch, "E2355", {"start": v(-15.36, -3.1) * mm, "end": v(-15.39, -3.02) * mm});
            skLineSegment(sketch, "E2356", {"start": v(-15.39, -3.02) * mm, "end": v(-15.4, -2.92) * mm});
            skLineSegment(sketch, "E2357", {"start": v(-15.4, -2.92) * mm, "end": v(-15.43, -2.83) * mm});
            skLineSegment(sketch, "E2358", {"start": v(-15.43, -2.83) * mm, "end": v(-15.45, -2.73) * mm});
            skLineSegment(sketch, "E2359", {"start": v(-15.45, -2.73) * mm, "end": v(-15.47, -2.64) * mm});
            skLineSegment(sketch, "E2360", {"start": v(-15.47, -2.64) * mm, "end": v(-15.48, -2.54) * mm});
            skLineSegment(sketch, "E2361", {"start": v(-15.48, -2.54) * mm, "end": v(-15.5, -2.45) * mm});
            skLineSegment(sketch, "E2362", {"start": v(-15.5, -2.45) * mm, "end": v(-15.51, -2.35) * mm});
            skLineSegment(sketch, "E2363", {"start": v(-15.51, -2.35) * mm, "end": v(-15.53, -2.25) * mm});
            skLineSegment(sketch, "E2364", {"start": v(-15.53, -2.25) * mm, "end": v(-15.54, -2.16) * mm});
            skLineSegment(sketch, "E2365", {"start": v(-15.54, -2.16) * mm, "end": v(-15.55, -2.06) * mm});
            skLineSegment(sketch, "E2366", {"start": v(-15.55, -2.06) * mm, "end": v(-15.56, -1.96) * mm});
            skLineSegment(sketch, "E2367", {"start": v(-15.56, -1.96) * mm, "end": v(-15.57, -1.86) * mm});
            skLineSegment(sketch, "E2368", {"start": v(-15.57, -1.86) * mm, "end": v(-15.58, -1.76) * mm});
            skLineSegment(sketch, "E2369", {"start": v(-15.58, -1.76) * mm, "end": v(-15.59, -1.66) * mm});
            skLineSegment(sketch, "E2370", {"start": v(-15.59, -1.66) * mm, "end": v(-15.6, -1.56) * mm});
            skLineSegment(sketch, "E2371", {"start": v(-15.6, -1.56) * mm, "end": v(-15.6, -1.46) * mm});
            skLineSegment(sketch, "E2372", {"start": v(-15.6, -1.46) * mm, "end": v(-15.6, -1.36) * mm});
            skLineSegment(sketch, "E2373", {"start": v(-15.6, -1.36) * mm, "end": v(-15.6, -1.27) * mm});
            skLineSegment(sketch, "E2374", {"start": v(-15.6, -1.27) * mm, "end": v(-15.6, -1.17) * mm});
            skLineSegment(sketch, "E2375", {"start": v(-15.6, -1.17) * mm, "end": v(-15.6, -1.07) * mm});
            skLineSegment(sketch, "E2376", {"start": v(-15.6, -1.07) * mm, "end": v(-15.61, -0.97) * mm});
            skLineSegment(sketch, "E2377", {"start": v(-15.61, -0.97) * mm, "end": v(-15.61, -0.87) * mm});
            skLineSegment(sketch, "E2378", {"start": v(-15.61, -0.87) * mm, "end": v(-15.61, -0.77) * mm});
            skLineSegment(sketch, "E2379", {"start": v(-15.61, -0.77) * mm, "end": v(-15.6, -0.67) * mm});
            skLineSegment(sketch, "E2380", {"start": v(-15.6, -0.67) * mm, "end": v(-15.6, -0.57) * mm});
            skLineSegment(sketch, "E2381", {"start": v(-15.6, -0.57) * mm, "end": v(-15.6, -0.47) * mm});
            skLineSegment(sketch, "E2382", {"start": v(-15.6, -0.47) * mm, "end": v(-15.6, -0.37) * mm});
            skLineSegment(sketch, "E2383", {"start": v(-15.6, -0.37) * mm, "end": v(-15.6, -0.27) * mm});
            skLineSegment(sketch, "E2384", {"start": v(-15.6, -0.27) * mm, "end": v(-15.6, -0.18) * mm});
            skLineSegment(sketch, "E2385", {"start": v(-15.6, -0.18) * mm, "end": v(-15.59, -0.08) * mm});
            skLineSegment(sketch, "E2386", {"start": v(-15.59, -0.08) * mm, "end": v(-15.58, 0.02) * mm});
            skLineSegment(sketch, "E2387", {"start": v(-15.58, 0.02) * mm, "end": v(-15.57, 0.12) * mm});
            skLineSegment(sketch, "E2388", {"start": v(-15.57, 0.12) * mm, "end": v(-15.56, 0.21) * mm});
            skLineSegment(sketch, "E2389", {"start": v(-15.56, 0.21) * mm, "end": v(-15.56, 0.3) * mm});
            skLineSegment(sketch, "E2390", {"start": v(-15.56, 0.3) * mm, "end": v(-15.55, 0.4) * mm});
            skLineSegment(sketch, "E2391", {"start": v(-15.55, 0.4) * mm, "end": v(-15.54, 0.5) * mm});
            skLineSegment(sketch, "E2392", {"start": v(-15.54, 0.5) * mm, "end": v(-15.53, 0.6) * mm});
            skLineSegment(sketch, "E2393", {"start": v(-15.53, 0.6) * mm, "end": v(-15.52, 0.68) * mm});
            skLineSegment(sketch, "E2394", {"start": v(-15.52, 0.68) * mm, "end": v(-15.5, 0.78) * mm});
            skLineSegment(sketch, "E2395", {"start": v(-15.5, 0.78) * mm, "end": v(-15.5, 0.87) * mm});
            skLineSegment(sketch, "E2396", {"start": v(-15.5, 0.87) * mm, "end": v(-15.49, 0.96) * mm});
            skLineSegment(sketch, "E2397", {"start": v(-15.49, 0.96) * mm, "end": v(-15.47, 1.05) * mm});
            skLineSegment(sketch, "E2398", {"start": v(-15.47, 1.05) * mm, "end": v(-15.46, 1.14) * mm});
            skLineSegment(sketch, "E2399", {"start": v(-15.46, 1.14) * mm, "end": v(-15.45, 1.23) * mm});
            skLineSegment(sketch, "E2400", {"start": v(-15.45, 1.23) * mm, "end": v(-15.44, 1.31) * mm});
            skLineSegment(sketch, "E2401", {"start": v(-15.44, 1.31) * mm, "end": v(-15.42, 1.4) * mm});
            skLineSegment(sketch, "E2402", {"start": v(-15.42, 1.4) * mm, "end": v(-15.4, 1.48) * mm});
            skLineSegment(sketch, "E2403", {"start": v(-15.4, 1.48) * mm, "end": v(-15.4, 1.57) * mm});
            skLineSegment(sketch, "E2404", {"start": v(-15.4, 1.57) * mm, "end": v(-15.38, 1.65) * mm});
            skLineSegment(sketch, "E2405", {"start": v(-15.38, 1.65) * mm, "end": v(-15.36, 1.73) * mm});
            skLineSegment(sketch, "E2406", {"start": v(-15.36, 1.73) * mm, "end": v(-15.35, 1.81) * mm});
            skLineSegment(sketch, "E2407", {"start": v(-15.35, 1.81) * mm, "end": v(-15.33, 1.9) * mm});
            skLineSegment(sketch, "E2408", {"start": v(-15.33, 1.9) * mm, "end": v(-15.32, 1.97) * mm});
            skLineSegment(sketch, "E2409", {"start": v(-15.32, 1.97) * mm, "end": v(-15.3, 2.05) * mm});
            skLineSegment(sketch, "E2410", {"start": v(-15.3, 2.05) * mm, "end": v(-15.29, 2.12) * mm});
            skLineSegment(sketch, "E2411", {"start": v(-15.29, 2.12) * mm, "end": v(-15.27, 2.2) * mm});
            skLineSegment(sketch, "E2412", {"start": v(-15.27, 2.2) * mm, "end": v(-15.26, 2.27) * mm});
            skLineSegment(sketch, "E2413", {"start": v(-15.26, 2.27) * mm, "end": v(-15.24, 2.35) * mm});
            skLineSegment(sketch, "E2414", {"start": v(-15.24, 2.35) * mm, "end": v(-15.22, 2.44) * mm});
            skLineSegment(sketch, "E2415", {"start": v(-15.22, 2.44) * mm, "end": v(-15.2, 2.52) * mm});
            skLineSegment(sketch, "E2416", {"start": v(-15.2, 2.52) * mm, "end": v(-15.18, 2.6) * mm});
            skLineSegment(sketch, "E2417", {"start": v(-15.18, 2.6) * mm, "end": v(-15.16, 2.69) * mm});
            skLineSegment(sketch, "E2418", {"start": v(-15.16, 2.69) * mm, "end": v(-15.14, 2.77) * mm});
            skLineSegment(sketch, "E2419", {"start": v(-15.14, 2.77) * mm, "end": v(-15.12, 2.86) * mm});
            skLineSegment(sketch, "E2420", {"start": v(-15.12, 2.86) * mm, "end": v(-15.1, 2.94) * mm});
            skLineSegment(sketch, "E2421", {"start": v(-15.1, 2.94) * mm, "end": v(-15.07, 3.03) * mm});
            skLineSegment(sketch, "E2422", {"start": v(-15.07, 3.03) * mm, "end": v(-15.05, 3.11) * mm});
            skLineSegment(sketch, "E2423", {"start": v(-15.05, 3.11) * mm, "end": v(-15.03, 3.2) * mm});
            skLineSegment(sketch, "E2424", {"start": v(-15.03, 3.2) * mm, "end": v(-15, 3.28) * mm});
            skLineSegment(sketch, "E2425", {"start": v(-15, 3.28) * mm, "end": v(-14.98, 3.37) * mm});
            skLineSegment(sketch, "E2426", {"start": v(-14.98, 3.37) * mm, "end": v(-14.96, 3.45) * mm});
            skLineSegment(sketch, "E2427", {"start": v(-14.96, 3.45) * mm, "end": v(-14.93, 3.54) * mm});
            skLineSegment(sketch, "E2428", {"start": v(-14.93, 3.54) * mm, "end": v(-14.9, 3.63) * mm});
            skLineSegment(sketch, "E2429", {"start": v(-14.9, 3.63) * mm, "end": v(-14.88, 3.71) * mm});
            skLineSegment(sketch, "E2430", {"start": v(-14.88, 3.71) * mm, "end": v(-14.85, 3.8) * mm});
            skLineSegment(sketch, "E2431", {"start": v(-14.85, 3.8) * mm, "end": v(-14.83, 3.89) * mm});
            skLineSegment(sketch, "E2432", {"start": v(-14.83, 3.89) * mm, "end": v(-14.8, 3.98) * mm});
            skLineSegment(sketch, "E2433", {"start": v(-14.8, 3.98) * mm, "end": v(-14.77, 4.06) * mm});
            skLineSegment(sketch, "E2434", {"start": v(-14.77, 4.06) * mm, "end": v(-14.75, 4.15) * mm});
            skLineSegment(sketch, "E2435", {"start": v(-14.75, 4.15) * mm, "end": v(-14.72, 4.24) * mm});
            skLineSegment(sketch, "E2436", {"start": v(-14.72, 4.24) * mm, "end": v(-14.69, 4.33) * mm});
            skLineSegment(sketch, "E2437", {"start": v(-14.69, 4.33) * mm, "end": v(-14.66, 4.42) * mm});
            skLineSegment(sketch, "E2438", {"start": v(-14.66, 4.42) * mm, "end": v(-14.63, 4.5) * mm});
            skLineSegment(sketch, "E2439", {"start": v(-14.63, 4.5) * mm, "end": v(-14.6, 4.6) * mm});
            skLineSegment(sketch, "E2440", {"start": v(-14.6, 4.6) * mm, "end": v(-14.57, 4.68) * mm});
            skLineSegment(sketch, "E2441", {"start": v(-14.57, 4.68) * mm, "end": v(-14.54, 4.77) * mm});
            skLineSegment(sketch, "E2442", {"start": v(-14.54, 4.77) * mm, "end": v(-14.51, 4.86) * mm});
            skLineSegment(sketch, "E2443", {"start": v(-14.51, 4.86) * mm, "end": v(-14.48, 4.95) * mm});
            skLineSegment(sketch, "E2444", {"start": v(-14.48, 4.95) * mm, "end": v(-14.45, 5.04) * mm});
            skLineSegment(sketch, "E2445", {"start": v(-14.45, 5.04) * mm, "end": v(-14.42, 5.13) * mm});
            skLineSegment(sketch, "E2446", {"start": v(-14.42, 5.13) * mm, "end": v(-14.38, 5.22) * mm});
            skLineSegment(sketch, "E2447", {"start": v(-14.38, 5.22) * mm, "end": v(-14.35, 5.31) * mm});
            skLineSegment(sketch, "E2448", {"start": v(-14.35, 5.31) * mm, "end": v(-14.32, 5.4) * mm});
            skLineSegment(sketch, "E2449", {"start": v(-14.32, 5.4) * mm, "end": v(-14.28, 5.5) * mm});
            skLineSegment(sketch, "E2450", {"start": v(-14.28, 5.5) * mm, "end": v(-14.25, 5.58) * mm});
            skLineSegment(sketch, "E2451", {"start": v(-14.25, 5.58) * mm, "end": v(-14.21, 5.67) * mm});
            skLineSegment(sketch, "E2452", {"start": v(-14.21, 5.67) * mm, "end": v(-14.18, 5.76) * mm});
            skLineSegment(sketch, "E2453", {"start": v(-14.18, 5.76) * mm, "end": v(-14.14, 5.86) * mm});
            skLineSegment(sketch, "E2454", {"start": v(-14.14, 5.86) * mm, "end": v(-14.1, 5.95) * mm});
            skLineSegment(sketch, "E2455", {"start": v(-14.1, 5.95) * mm, "end": v(-14.07, 6.04) * mm});
            skLineSegment(sketch, "E2456", {"start": v(-14.07, 6.04) * mm, "end": v(-14.04, 6.13) * mm});
            skLineSegment(sketch, "E2457", {"start": v(-14.04, 6.13) * mm, "end": v(-14, 6.22) * mm});
            skLineSegment(sketch, "E2458", {"start": v(-14, 6.22) * mm, "end": v(-13.96, 6.31) * mm});
            skLineSegment(sketch, "E2459", {"start": v(-13.96, 6.31) * mm, "end": v(-13.92, 6.4) * mm});
            skLineSegment(sketch, "E2460", {"start": v(-13.92, 6.4) * mm, "end": v(-13.89, 6.5) * mm});
            skLineSegment(sketch, "E2461", {"start": v(-13.89, 6.5) * mm, "end": v(-13.85, 6.58) * mm});
            skLineSegment(sketch, "E2462", {"start": v(-13.85, 6.58) * mm, "end": v(-13.8, 6.68) * mm});
            skLineSegment(sketch, "E2463", {"start": v(-13.8, 6.68) * mm, "end": v(-13.77, 6.77) * mm});
            skLineSegment(sketch, "E2464", {"start": v(-13.77, 6.77) * mm, "end": v(-13.73, 6.86) * mm});
            skLineSegment(sketch, "E2465", {"start": v(-13.73, 6.86) * mm, "end": v(-13.7, 6.95) * mm});
            skLineSegment(sketch, "E2466", {"start": v(-13.7, 6.95) * mm, "end": v(-13.65, 7.04) * mm});
            skLineSegment(sketch, "E2467", {"start": v(-13.65, 7.04) * mm, "end": v(-13.61, 7.13) * mm});
            skLineSegment(sketch, "E2468", {"start": v(-13.61, 7.13) * mm, "end": v(-13.57, 7.23) * mm});
            skLineSegment(sketch, "E2469", {"start": v(-13.57, 7.23) * mm, "end": v(-13.53, 7.32) * mm});
            skLineSegment(sketch, "E2470", {"start": v(-13.53, 7.32) * mm, "end": v(-13.49, 7.4) * mm});
            skLineSegment(sketch, "E2471", {"start": v(-13.49, 7.4) * mm, "end": v(-13.44, 7.5) * mm});
            skLineSegment(sketch, "E2472", {"start": v(-13.44, 7.5) * mm, "end": v(-13.4, 7.6) * mm});
            skLineSegment(sketch, "E2473", {"start": v(-13.4, 7.6) * mm, "end": v(-13.36, 7.69) * mm});
            skLineSegment(sketch, "E2474", {"start": v(-13.36, 7.69) * mm, "end": v(-13.32, 7.78) * mm});
            skLineSegment(sketch, "E2475", {"start": v(-13.32, 7.78) * mm, "end": v(-13.27, 7.87) * mm});
            skLineSegment(sketch, "E2476", {"start": v(-13.27, 7.87) * mm, "end": v(-13.23, 7.96) * mm});
            skLineSegment(sketch, "E2477", {"start": v(-13.23, 7.96) * mm, "end": v(-13.18, 8.05) * mm});
            skLineSegment(sketch, "E2478", {"start": v(-13.18, 8.05) * mm, "end": v(-13.14, 8.14) * mm});
            skLineSegment(sketch, "E2479", {"start": v(-13.14, 8.14) * mm, "end": v(-13.1, 8.24) * mm});
            skLineSegment(sketch, "E2480", {"start": v(-13.1, 8.24) * mm, "end": v(-13.05, 8.33) * mm});
            skLineSegment(sketch, "E2481", {"start": v(-13.05, 8.33) * mm, "end": v(-13, 8.42) * mm});
            skLineSegment(sketch, "E2482", {"start": v(-13, 8.42) * mm, "end": v(-12.96, 8.51) * mm});
            skLineSegment(sketch, "E2483", {"start": v(-12.96, 8.51) * mm, "end": v(-12.91, 8.6) * mm});
            skLineSegment(sketch, "E2484", {"start": v(-12.91, 8.6) * mm, "end": v(-12.86, 8.7) * mm});
            skLineSegment(sketch, "E2485", {"start": v(-12.86, 8.7) * mm, "end": v(-12.82, 8.79) * mm});
            skLineSegment(sketch, "E2486", {"start": v(-12.82, 8.79) * mm, "end": v(-12.77, 8.88) * mm});
            skLineSegment(sketch, "E2487", {"start": v(-12.77, 8.88) * mm, "end": v(-12.72, 8.97) * mm});
            skLineSegment(sketch, "E2488", {"start": v(-12.72, 8.97) * mm, "end": v(-12.67, 9.06) * mm});
            skLineSegment(sketch, "E2489", {"start": v(-12.67, 9.06) * mm, "end": v(-12.63, 9.15) * mm});
            skLineSegment(sketch, "E2490", {"start": v(-12.63, 9.15) * mm, "end": v(-12.58, 9.24) * mm});
            skLineSegment(sketch, "E2491", {"start": v(-12.58, 9.24) * mm, "end": v(-12.53, 9.33) * mm});
            skLineSegment(sketch, "E2492", {"start": v(-12.53, 9.33) * mm, "end": v(-12.48, 9.42) * mm});
            skLineSegment(sketch, "E2493", {"start": v(-12.48, 9.42) * mm, "end": v(-12.43, 9.51) * mm});
            skLineSegment(sketch, "E2494", {"start": v(-12.43, 9.51) * mm, "end": v(-12.38, 9.6) * mm});
            skLineSegment(sketch, "E2495", {"start": v(-12.38, 9.6) * mm, "end": v(-12.33, 9.7) * mm});
            skLineSegment(sketch, "E2496", {"start": v(-12.33, 9.7) * mm, "end": v(-12.28, 9.79) * mm});
            skLineSegment(sketch, "E2497", {"start": v(-12.28, 9.79) * mm, "end": v(-12.23, 9.88) * mm});
            skLineSegment(sketch, "E2498", {"start": v(-12.23, 9.88) * mm, "end": v(-12.18, 9.97) * mm});
            skLineSegment(sketch, "E2499", {"start": v(-12.18, 9.97) * mm, "end": v(-12.12, 10.06) * mm});
            skLineSegment(sketch, "E2500", {"start": v(-12.12, 10.06) * mm, "end": v(-12.07, 10.15) * mm});
            skLineSegment(sketch, "E2501", {"start": v(-12.07, 10.15) * mm, "end": v(-12.02, 10.24) * mm});
            skLineSegment(sketch, "E2502", {"start": v(-12.02, 10.24) * mm, "end": v(-11.97, 10.33) * mm});
            skLineSegment(sketch, "E2503", {"start": v(-11.97, 10.33) * mm, "end": v(-11.91, 10.42) * mm});
            skLineSegment(sketch, "E2504", {"start": v(-11.91, 10.42) * mm, "end": v(-11.86, 10.5) * mm});
            skLineSegment(sketch, "E2505", {"start": v(-11.86, 10.5) * mm, "end": v(-11.8, 10.6) * mm});
            skLineSegment(sketch, "E2506", {"start": v(-11.8, 10.6) * mm, "end": v(-11.75, 10.69) * mm});
            skLineSegment(sketch, "E2507", {"start": v(-11.75, 10.69) * mm, "end": v(-11.7, 10.77) * mm});
            skLineSegment(sketch, "E2508", {"start": v(-11.7, 10.77) * mm, "end": v(-11.64, 10.86) * mm});
            skLineSegment(sketch, "E2509", {"start": v(-11.64, 10.86) * mm, "end": v(-11.59, 10.95) * mm});
            skLineSegment(sketch, "E2510", {"start": v(-11.59, 10.95) * mm, "end": v(-11.53, 11.04) * mm});
            skLineSegment(sketch, "E2511", {"start": v(-11.53, 11.04) * mm, "end": v(-11.48, 11.13) * mm});
            skLineSegment(sketch, "E2512", {"start": v(-11.48, 11.13) * mm, "end": v(-11.42, 11.22) * mm});
            skLineSegment(sketch, "E2513", {"start": v(-11.42, 11.22) * mm, "end": v(-11.36, 11.3) * mm});
            skLineSegment(sketch, "E2514", {"start": v(-11.36, 11.3) * mm, "end": v(-11.3, 11.4) * mm});
            skLineSegment(sketch, "E2515", {"start": v(-11.3, 11.4) * mm, "end": v(-11.25, 11.48) * mm});
            skLineSegment(sketch, "E2516", {"start": v(-11.25, 11.48) * mm, "end": v(-11.2, 11.57) * mm});
            skLineSegment(sketch, "E2517", {"start": v(-11.2, 11.57) * mm, "end": v(-11.14, 11.65) * mm});
            skLineSegment(sketch, "E2518", {"start": v(-11.14, 11.65) * mm, "end": v(-11.08, 11.74) * mm});
            skLineSegment(sketch, "E2519", {"start": v(-11.08, 11.74) * mm, "end": v(-11.02, 11.83) * mm});
            skLineSegment(sketch, "E2520", {"start": v(-11.02, 11.83) * mm, "end": v(-10.96, 11.91) * mm});
            skLineSegment(sketch, "E2521", {"start": v(-10.96, 11.91) * mm, "end": v(-10.9, 12) * mm});
            skLineSegment(sketch, "E2522", {"start": v(-10.9, 12) * mm, "end": v(-10.84, 12.09) * mm});
            skLineSegment(sketch, "E2523", {"start": v(-10.84, 12.09) * mm, "end": v(-10.78, 12.17) * mm});
            skLineSegment(sketch, "E2524", {"start": v(-10.78, 12.17) * mm, "end": v(-10.72, 12.26) * mm});
            skLineSegment(sketch, "E2525", {"start": v(-10.72, 12.26) * mm, "end": v(-10.66, 12.34) * mm});
            skLineSegment(sketch, "E2526", {"start": v(-10.66, 12.34) * mm, "end": v(-10.6, 12.43) * mm});
            skLineSegment(sketch, "E2527", {"start": v(-10.6, 12.43) * mm, "end": v(-10.54, 12.51) * mm});
            skLineSegment(sketch, "E2528", {"start": v(-10.54, 12.51) * mm, "end": v(-10.48, 12.6) * mm});
            skLineSegment(sketch, "E2529", {"start": v(-10.48, 12.6) * mm, "end": v(-10.42, 12.68) * mm});
            skLineSegment(sketch, "E2530", {"start": v(-10.42, 12.68) * mm, "end": v(-10.36, 12.76) * mm});
            skLineSegment(sketch, "E2531", {"start": v(-10.36, 12.76) * mm, "end": v(-10.3, 12.85) * mm});
            skLineSegment(sketch, "E2532", {"start": v(-10.3, 12.85) * mm, "end": v(-10.24, 12.93) * mm});
            skLineSegment(sketch, "E2533", {"start": v(-10.24, 12.93) * mm, "end": v(-10.18, 13.01) * mm});
            skLineSegment(sketch, "E2534", {"start": v(-10.18, 13.01) * mm, "end": v(-10.11, 13.1) * mm});
            skLineSegment(sketch, "E2535", {"start": v(-10.11, 13.1) * mm, "end": v(-10.05, 13.18) * mm});
            skLineSegment(sketch, "E2536", {"start": v(-10.05, 13.18) * mm, "end": v(-9.99, 13.26) * mm});
            skLineSegment(sketch, "E2537", {"start": v(-9.99, 13.26) * mm, "end": v(-9.92, 13.34) * mm});
            skLineSegment(sketch, "E2538", {"start": v(-9.92, 13.34) * mm, "end": v(-9.86, 13.42) * mm});
            skLineSegment(sketch, "E2539", {"start": v(-9.86, 13.42) * mm, "end": v(-9.8, 13.5) * mm});
            skLineSegment(sketch, "E2540", {"start": v(-9.8, 13.5) * mm, "end": v(-9.73, 13.59) * mm});
            skLineSegment(sketch, "E2541", {"start": v(-9.73, 13.59) * mm, "end": v(-9.67, 13.67) * mm});
            skLineSegment(sketch, "E2542", {"start": v(-9.67, 13.67) * mm, "end": v(-9.6, 13.75) * mm});
            skLineSegment(sketch, "E2543", {"start": v(-9.6, 13.75) * mm, "end": v(-9.54, 13.83) * mm});
            skLineSegment(sketch, "E2544", {"start": v(-9.54, 13.83) * mm, "end": v(-9.47, 13.9) * mm});
            skLineSegment(sketch, "E2545", {"start": v(-9.47, 13.9) * mm, "end": v(-9.4, 13.98) * mm});
            skLineSegment(sketch, "E2546", {"start": v(-9.4, 13.98) * mm, "end": v(-9.34, 14.06) * mm});
            skLineSegment(sketch, "E2547", {"start": v(-9.34, 14.06) * mm, "end": v(-9.27, 14.14) * mm});
            skLineSegment(sketch, "E2548", {"start": v(-9.27, 14.14) * mm, "end": v(-9.2, 14.22) * mm});
            skLineSegment(sketch, "E2549", {"start": v(-9.2, 14.22) * mm, "end": v(-9.14, 14.3) * mm});
            skLineSegment(sketch, "E2550", {"start": v(-9.14, 14.3) * mm, "end": v(-9.07, 14.37) * mm});
            skLineSegment(sketch, "E2551", {"start": v(-9.07, 14.37) * mm, "end": v(-9, 14.45) * mm});
            skLineSegment(sketch, "E2552", {"start": v(-9, 14.45) * mm, "end": v(-8.94, 14.53) * mm});
            skLineSegment(sketch, "E2553", {"start": v(-8.94, 14.53) * mm, "end": v(-8.87, 14.6) * mm});
            skLineSegment(sketch, "E2554", {"start": v(-8.87, 14.6) * mm, "end": v(-8.8, 14.68) * mm});
            skLineSegment(sketch, "E2555", {"start": v(-8.8, 14.68) * mm, "end": v(-8.74, 14.75) * mm});
            skLineSegment(sketch, "E2556", {"start": v(-8.74, 14.75) * mm, "end": v(-8.67, 14.83) * mm});
            skLineSegment(sketch, "E2557", {"start": v(-8.67, 14.83) * mm, "end": v(-8.6, 14.9) * mm});
            skLineSegment(sketch, "E2558", {"start": v(-8.6, 14.9) * mm, "end": v(-8.53, 14.98) * mm});
            skLineSegment(sketch, "E2559", {"start": v(-8.53, 14.98) * mm, "end": v(-8.46, 15.05) * mm});
            skLineSegment(sketch, "E2560", {"start": v(-8.46, 15.05) * mm, "end": v(-8.4, 15.12) * mm});
            skLineSegment(sketch, "E2561", {"start": v(-8.4, 15.12) * mm, "end": v(-8.32, 15.2) * mm});
            skLineSegment(sketch, "E2562", {"start": v(-8.32, 15.2) * mm, "end": v(-8.25, 15.27) * mm});
            skLineSegment(sketch, "E2563", {"start": v(-8.25, 15.27) * mm, "end": v(-8.18, 15.34) * mm});
            skLineSegment(sketch, "E2564", {"start": v(-8.18, 15.34) * mm, "end": v(-8.11, 15.41) * mm});
            skLineSegment(sketch, "E2565", {"start": v(-8.11, 15.41) * mm, "end": v(-8.04, 15.48) * mm});
            skLineSegment(sketch, "E2566", {"start": v(-8.04, 15.48) * mm, "end": v(-7.97, 15.55) * mm});
            skLineSegment(sketch, "E2567", {"start": v(-7.97, 15.55) * mm, "end": v(-7.9, 15.62) * mm});
            skLineSegment(sketch, "E2568", {"start": v(-7.9, 15.62) * mm, "end": v(-7.83, 15.7) * mm});
            skLineSegment(sketch, "E2569", {"start": v(-7.83, 15.7) * mm, "end": v(-7.75, 15.76) * mm});
            skLineSegment(sketch, "E2570", {"start": v(-7.75, 15.76) * mm, "end": v(-7.68, 15.83) * mm});
            skLineSegment(sketch, "E2571", {"start": v(-7.68, 15.83) * mm, "end": v(-7.61, 15.9) * mm});
            skLineSegment(sketch, "E2572", {"start": v(-7.61, 15.9) * mm, "end": v(-7.54, 15.96) * mm});
            skLineSegment(sketch, "E2573", {"start": v(-7.54, 15.96) * mm, "end": v(-7.47, 16.03) * mm});
            skLineSegment(sketch, "E2574", {"start": v(-7.47, 16.03) * mm, "end": v(-7.4, 16.1) * mm});
            skLineSegment(sketch, "E2575", {"start": v(-7.4, 16.1) * mm, "end": v(-7.32, 16.16) * mm});
            skLineSegment(sketch, "E2576", {"start": v(-7.32, 16.16) * mm, "end": v(-7.25, 16.23) * mm});
            skLineSegment(sketch, "E2577", {"start": v(-7.25, 16.23) * mm, "end": v(-7.17, 16.3) * mm});
            skLineSegment(sketch, "E2578", {"start": v(-7.17, 16.3) * mm, "end": v(-7.1, 16.36) * mm});
            skLineSegment(sketch, "E2579", {"start": v(-7.1, 16.36) * mm, "end": v(-7.02, 16.42) * mm});
            skLineSegment(sketch, "E2580", {"start": v(-7.02, 16.42) * mm, "end": v(-6.95, 16.49) * mm});
            skLineSegment(sketch, "E2581", {"start": v(-6.95, 16.49) * mm, "end": v(-6.88, 16.55) * mm});
            skLineSegment(sketch, "E2582", {"start": v(-6.88, 16.55) * mm, "end": v(-6.8, 16.61) * mm});
            skLineSegment(sketch, "E2583", {"start": v(-6.8, 16.61) * mm, "end": v(-6.73, 16.67) * mm});
            skLineSegment(sketch, "E2584", {"start": v(-6.73, 16.67) * mm, "end": v(-6.65, 16.73) * mm});
            skLineSegment(sketch, "E2585", {"start": v(-6.65, 16.73) * mm, "end": v(-6.58, 16.8) * mm});
            skLineSegment(sketch, "E2586", {"start": v(-6.58, 16.8) * mm, "end": v(-6.5, 16.86) * mm});
            skLineSegment(sketch, "E2587", {"start": v(-6.5, 16.86) * mm, "end": v(-6.42, 16.91) * mm});
            skLineSegment(sketch, "E2588", {"start": v(-6.42, 16.91) * mm, "end": v(-6.35, 16.97) * mm});
            skLineSegment(sketch, "E2589", {"start": v(-6.35, 16.97) * mm, "end": v(-6.27, 17.03) * mm});
            skLineSegment(sketch, "E2590", {"start": v(-6.27, 17.03) * mm, "end": v(-6.2, 17.1) * mm});
            skLineSegment(sketch, "E2591", {"start": v(-6.2, 17.1) * mm, "end": v(-6.12, 17.15) * mm});
            skLineSegment(sketch, "E2592", {"start": v(-6.12, 17.15) * mm, "end": v(-6.04, 17.2) * mm});
            skLineSegment(sketch, "E2593", {"start": v(-6.04, 17.2) * mm, "end": v(-5.97, 17.26) * mm});
            skLineSegment(sketch, "E2594", {"start": v(-5.97, 17.26) * mm, "end": v(-5.89, 17.32) * mm});
            skLineSegment(sketch, "E2595", {"start": v(-5.89, 17.32) * mm, "end": v(-5.81, 17.37) * mm});
            skLineSegment(sketch, "E2596", {"start": v(-5.81, 17.37) * mm, "end": v(-5.73, 17.42) * mm});
            skLineSegment(sketch, "E2597", {"start": v(-5.73, 17.42) * mm, "end": v(-5.66, 17.48) * mm});
            skLineSegment(sketch, "E2598", {"start": v(-5.66, 17.48) * mm, "end": v(-5.58, 17.53) * mm});
            skLineSegment(sketch, "E2599", {"start": v(-5.58, 17.53) * mm, "end": v(-5.5, 17.58) * mm});
            skLineSegment(sketch, "E2600", {"start": v(-5.5, 17.58) * mm, "end": v(-5.42, 17.64) * mm});
            skLineSegment(sketch, "E2601", {"start": v(-5.42, 17.64) * mm, "end": v(-5.34, 17.69) * mm});
            skLineSegment(sketch, "E2602", {"start": v(-5.34, 17.69) * mm, "end": v(-5.26, 17.74) * mm});
            skLineSegment(sketch, "E2603", {"start": v(-5.26, 17.74) * mm, "end": v(-5.18, 17.79) * mm});
            skLineSegment(sketch, "E2604", {"start": v(-5.18, 17.79) * mm, "end": v(-5.1, 17.84) * mm});
            skLineSegment(sketch, "E2605", {"start": v(-5.1, 17.84) * mm, "end": v(-5.03, 17.89) * mm});
            skLineSegment(sketch, "E2606", {"start": v(-5.03, 17.89) * mm, "end": v(-4.95, 17.93) * mm});
            skLineSegment(sketch, "E2607", {"start": v(-4.95, 17.93) * mm, "end": v(-4.87, 17.98) * mm});
            skLineSegment(sketch, "E2608", {"start": v(-4.87, 17.98) * mm, "end": v(-4.79, 18.03) * mm});
            skLineSegment(sketch, "E2609", {"start": v(-4.79, 18.03) * mm, "end": v(-4.7, 18.07) * mm});
            skLineSegment(sketch, "E2610", {"start": v(-4.7, 18.07) * mm, "end": v(-4.63, 18.12) * mm});
            skLineSegment(sketch, "E2611", {"start": v(-4.63, 18.12) * mm, "end": v(-4.54, 18.16) * mm});
            skLineSegment(sketch, "E2612", {"start": v(-4.54, 18.16) * mm, "end": v(-4.46, 18.2) * mm});
            skLineSegment(sketch, "E2613", {"start": v(-4.46, 18.2) * mm, "end": v(-4.38, 18.25) * mm});
            skLineSegment(sketch, "E2614", {"start": v(-4.38, 18.25) * mm, "end": v(-4.3, 18.3) * mm});
            skLineSegment(sketch, "E2615", {"start": v(-4.3, 18.3) * mm, "end": v(-4.22, 18.33) * mm});
            skLineSegment(sketch, "E2616", {"start": v(-4.22, 18.33) * mm, "end": v(-4.14, 18.37) * mm});
            skLineSegment(sketch, "E2617", {"start": v(-4.14, 18.37) * mm, "end": v(-4.06, 18.41) * mm});
            skLineSegment(sketch, "E2618", {"start": v(-4.06, 18.41) * mm, "end": v(-3.98, 18.45) * mm});
            skLineSegment(sketch, "E2619", {"start": v(-3.98, 18.45) * mm, "end": v(-3.9, 18.5) * mm});
            skLineSegment(sketch, "E2620", {"start": v(-3.9, 18.5) * mm, "end": v(-3.81, 18.53) * mm});
            skLineSegment(sketch, "E2621", {"start": v(-3.81, 18.53) * mm, "end": v(-3.73, 18.57) * mm});
            skLineSegment(sketch, "E2622", {"start": v(-3.73, 18.57) * mm, "end": v(-3.65, 18.6) * mm});
            skLineSegment(sketch, "E2623", {"start": v(-3.65, 18.6) * mm, "end": v(-3.56, 18.64) * mm});
            skLineSegment(sketch, "E2624", {"start": v(-3.56, 18.64) * mm, "end": v(-3.48, 18.68) * mm});
            skLineSegment(sketch, "E2625", {"start": v(-3.48, 18.68) * mm, "end": v(-3.4, 18.71) * mm});
            skLineSegment(sketch, "E2626", {"start": v(-3.4, 18.71) * mm, "end": v(-3.31, 18.74) * mm});
            skLineSegment(sketch, "E2627", {"start": v(-3.31, 18.74) * mm, "end": v(-3.23, 18.78) * mm});
            skLineSegment(sketch, "E2628", {"start": v(-3.23, 18.78) * mm, "end": v(-3.15, 18.8) * mm});
            skLineSegment(sketch, "E2629", {"start": v(-3.15, 18.8) * mm, "end": v(-3.06, 18.84) * mm});
            skLineSegment(sketch, "E2630", {"start": v(-3.06, 18.84) * mm, "end": v(-2.98, 18.87) * mm});
            skLineSegment(sketch, "E2631", {"start": v(-2.98, 18.87) * mm, "end": v(-2.9, 18.9) * mm});
            skLineSegment(sketch, "E2632", {"start": v(-2.9, 18.9) * mm, "end": v(-2.81, 18.93) * mm});
            skLineSegment(sketch, "E2633", {"start": v(-2.81, 18.93) * mm, "end": v(-2.72, 18.96) * mm});
            skLineSegment(sketch, "E2634", {"start": v(-2.72, 18.96) * mm, "end": v(-2.63, 18.98) * mm});
            skLineSegment(sketch, "E2635", {"start": v(-2.63, 18.98) * mm, "end": v(-2.55, 19) * mm});
            skLineSegment(sketch, "E2636", {"start": v(-2.55, 19) * mm, "end": v(-2.46, 19.02) * mm});
            skLineSegment(sketch, "E2637", {"start": v(-2.46, 19.02) * mm, "end": v(-2.37, 19.04) * mm});
            skLineSegment(sketch, "E2638", {"start": v(-2.37, 19.04) * mm, "end": v(-2.29, 19.05) * mm});
            skLineSegment(sketch, "E2639", {"start": v(-2.29, 19.05) * mm, "end": v(-2.2, 19.06) * mm});
            skLineSegment(sketch, "E2640", {"start": v(-2.2, 19.06) * mm, "end": v(-2.12, 19.07) * mm});
            skLineSegment(sketch, "E2641", {"start": v(-2.12, 19.07) * mm, "end": v(-2.03, 19.07) * mm});
            skLineSegment(sketch, "E2642", {"start": v(-2.03, 19.07) * mm, "end": v(-1.95, 19.07) * mm});
            skLineSegment(sketch, "E2643", {"start": v(-1.95, 19.07) * mm, "end": v(-1.87, 19.06) * mm});
            skLineSegment(sketch, "E2644", {"start": v(-1.87, 19.06) * mm, "end": v(-1.79, 19.06) * mm});
            skLineSegment(sketch, "E2645", {"start": v(-1.79, 19.06) * mm, "end": v(-1.7, 19.05) * mm});
            skLineSegment(sketch, "E2646", {"start": v(-1.7, 19.05) * mm, "end": v(-1.63, 19.04) * mm});
            skLineSegment(sketch, "E2647", {"start": v(-1.63, 19.04) * mm, "end": v(-1.56, 19.02) * mm});
            skLineSegment(sketch, "E2648", {"start": v(-1.56, 19.02) * mm, "end": v(-1.48, 19) * mm});
            skLineSegment(sketch, "E2649", {"start": v(-1.48, 19) * mm, "end": v(-1.41, 18.98) * mm});
            skLineSegment(sketch, "E2650", {"start": v(-1.41, 18.98) * mm, "end": v(-1.34, 18.96) * mm});
            skLineSegment(sketch, "E2651", {"start": v(-1.34, 18.96) * mm, "end": v(-1.27, 18.93) * mm});
            skLineSegment(sketch, "E2652", {"start": v(-1.27, 18.93) * mm, "end": v(-1.2, 18.9) * mm});
            skLineSegment(sketch, "E2653", {"start": v(-1.2, 18.9) * mm, "end": v(-1.14, 18.87) * mm});
            skLineSegment(sketch, "E2654", {"start": v(-1.14, 18.87) * mm, "end": v(-1.08, 18.84) * mm});
            skLineSegment(sketch, "E2655", {"start": v(-1.08, 18.84) * mm, "end": v(-1.02, 18.8) * mm});
            skLineSegment(sketch, "E2656", {"start": v(-1.02, 18.8) * mm, "end": v(-0.96, 18.76) * mm});
            skLineSegment(sketch, "E2657", {"start": v(-0.96, 18.76) * mm, "end": v(-0.9, 18.72) * mm});
            skLineSegment(sketch, "E2658", {"start": v(-0.9, 18.72) * mm, "end": v(-0.85, 18.68) * mm});
            skLineSegment(sketch, "E2659", {"start": v(-0.85, 18.68) * mm, "end": v(-0.8, 18.64) * mm});
            skLineSegment(sketch, "E2660", {"start": v(-0.8, 18.64) * mm, "end": v(-0.76, 18.59) * mm});
            skLineSegment(sketch, "E2661", {"start": v(-0.76, 18.59) * mm, "end": v(-0.71, 18.54) * mm});
            skLineSegment(sketch, "E2662", {"start": v(-0.71, 18.54) * mm, "end": v(-0.67, 18.49) * mm});
            skLineSegment(sketch, "E2663", {"start": v(-0.67, 18.49) * mm, "end": v(-0.63, 18.43) * mm});
            skLineSegment(sketch, "E2664", {"start": v(-0.63, 18.43) * mm, "end": v(-0.6, 18.38) * mm});
            skLineSegment(sketch, "E2665", {"start": v(-0.6, 18.38) * mm, "end": v(-0.57, 18.32) * mm});
            skLineSegment(sketch, "E2666", {"start": v(-0.57, 18.32) * mm, "end": v(-0.54, 18.26) * mm});
            skLineSegment(sketch, "E2667", {"start": v(-0.54, 18.26) * mm, "end": v(-0.52, 18.2) * mm});
            skLineSegment(sketch, "E2668", {"start": v(-0.52, 18.2) * mm, "end": v(-0.5, 18.14) * mm});
            skLineSegment(sketch, "E2669", {"start": v(-0.5, 18.14) * mm, "end": v(-0.48, 18.07) * mm});
            skLineSegment(sketch, "E2670", {"start": v(-0.48, 18.07) * mm, "end": v(-0.46, 18) * mm});
            skLineSegment(sketch, "E2671", {"start": v(-0.46, 18) * mm, "end": v(-0.45, 17.94) * mm});
            skLineSegment(sketch, "E2672", {"start": v(-0.45, 17.94) * mm, "end": v(-0.45, 17.87) * mm});
            skLineSegment(sketch, "E2673", {"start": v(-0.45, 17.87) * mm, "end": v(-0.44, 17.8) * mm});
            skLineSegment(sketch, "E2674", {"start": v(-0.44, 17.8) * mm, "end": v(-0.44, 17.72) * mm});
            skLineSegment(sketch, "E2675", {"start": v(-0.44, 17.72) * mm, "end": v(-0.45, 17.65) * mm});
            skLineSegment(sketch, "E2676", {"start": v(-0.45, 17.65) * mm, "end": v(-0.46, 17.57) * mm});
            skLineSegment(sketch, "E2677", {"start": v(-0.46, 17.57) * mm, "end": v(-0.47, 17.5) * mm});
            skLineSegment(sketch, "E2678", {"start": v(-0.47, 17.5) * mm, "end": v(-0.5, 17.41) * mm});
            skLineSegment(sketch, "E2679", {"start": v(-0.5, 17.41) * mm, "end": v(-0.52, 17.33) * mm});
            skLineSegment(sketch, "E2680", {"start": v(-0.52, 17.33) * mm, "end": v(-0.55, 17.25) * mm});
            skLineSegment(sketch, "E2681", {"start": v(-0.55, 17.25) * mm, "end": v(-0.58, 17.17) * mm});
            skLineSegment(sketch, "E2682", {"start": v(-0.58, 17.17) * mm, "end": v(-0.62, 17.09) * mm});
            skLineSegment(sketch, "E2683", {"start": v(-0.62, 17.09) * mm, "end": v(-0.66, 17) * mm});
            skLineSegment(sketch, "E2684", {"start": v(-0.66, 17) * mm, "end": v(-0.7, 16.92) * mm});
            skLineSegment(sketch, "E2685", {"start": v(-0.7, 16.92) * mm, "end": v(-0.76, 16.83) * mm});
            skLineSegment(sketch, "E2686", {"start": v(-0.76, 16.83) * mm, "end": v(-0.82, 16.74) * mm});
            skLineSegment(sketch, "E2687", {"start": v(-0.82, 16.74) * mm, "end": v(-0.88, 16.65) * mm});
            skLineSegment(sketch, "E2688", {"start": v(-0.88, 16.65) * mm, "end": v(-0.94, 16.57) * mm});
            skLineSegment(sketch, "E2689", {"start": v(-0.94, 16.57) * mm, "end": v(-1, 16.5) * mm});
            skLineSegment(sketch, "E2690", {"start": v(-1, 16.5) * mm, "end": v(-1.07, 16.43) * mm});
            skLineSegment(sketch, "E2691", {"start": v(-1.07, 16.43) * mm, "end": v(-1.14, 16.36) * mm});
            skLineSegment(sketch, "E2692", {"start": v(-1.14, 16.36) * mm, "end": v(-1.2, 16.3) * mm});
            skLineSegment(sketch, "E2693", {"start": v(-1.2, 16.3) * mm, "end": v(-1.27, 16.23) * mm});
            skLineSegment(sketch, "E2694", {"start": v(-1.27, 16.23) * mm, "end": v(-1.35, 16.17) * mm});
            skLineSegment(sketch, "E2695", {"start": v(-1.35, 16.17) * mm, "end": v(-1.42, 16.12) * mm});
            skLineSegment(sketch, "E2696", {"start": v(-1.42, 16.12) * mm, "end": v(-1.5, 16.07) * mm});
            skLineSegment(sketch, "E2697", {"start": v(-1.5, 16.07) * mm, "end": v(-1.57, 16.02) * mm});
            skLineSegment(sketch, "E2698", {"start": v(-1.57, 16.02) * mm, "end": v(-1.65, 15.97) * mm});
            skLineSegment(sketch, "E2699", {"start": v(-1.65, 15.97) * mm, "end": v(-1.72, 15.93) * mm});
            skLineSegment(sketch, "E2700", {"start": v(-1.72, 15.93) * mm, "end": v(-1.8, 15.89) * mm});
            skLineSegment(sketch, "E2701", {"start": v(-1.8, 15.89) * mm, "end": v(-1.88, 15.85) * mm});
            skLineSegment(sketch, "E2702", {"start": v(-1.88, 15.85) * mm, "end": v(-1.96, 15.81) * mm});
            skLineSegment(sketch, "E2703", {"start": v(-1.96, 15.81) * mm, "end": v(-2.04, 15.78) * mm});
            skLineSegment(sketch, "E2704", {"start": v(-2.04, 15.78) * mm, "end": v(-2.12, 15.75) * mm});
            skLineSegment(sketch, "E2705", {"start": v(-2.12, 15.75) * mm, "end": v(-2.2, 15.71) * mm});
            skLineSegment(sketch, "E2706", {"start": v(-2.2, 15.71) * mm, "end": v(-2.3, 15.68) * mm});
            skLineSegment(sketch, "E2707", {"start": v(-2.3, 15.68) * mm, "end": v(-2.37, 15.65) * mm});
            skLineSegment(sketch, "E2708", {"start": v(-2.37, 15.65) * mm, "end": v(-2.46, 15.63) * mm});
            skLineSegment(sketch, "E2709", {"start": v(-2.46, 15.63) * mm, "end": v(-2.54, 15.6) * mm});
            skLineSegment(sketch, "E2710", {"start": v(-2.54, 15.6) * mm, "end": v(-2.63, 15.57) * mm});
            skLineSegment(sketch, "E2711", {"start": v(-2.63, 15.57) * mm, "end": v(-2.71, 15.55) * mm});
            skLineSegment(sketch, "E2712", {"start": v(-2.71, 15.55) * mm, "end": v(-2.8, 15.52) * mm});
            skLineSegment(sketch, "E2713", {"start": v(-2.8, 15.52) * mm, "end": v(-2.88, 15.5) * mm});
            skLineSegment(sketch, "E2714", {"start": v(-2.88, 15.5) * mm, "end": v(-2.97, 15.47) * mm});
            skLineSegment(sketch, "E2715", {"start": v(-2.97, 15.47) * mm, "end": v(-3.05, 15.45) * mm});
            skLineSegment(sketch, "E2716", {"start": v(-3.05, 15.45) * mm, "end": v(-3.14, 15.42) * mm});
            skLineSegment(sketch, "E2717", {"start": v(-3.14, 15.42) * mm, "end": v(-3.22, 15.4) * mm});
            skLineSegment(sketch, "E2718", {"start": v(-3.22, 15.4) * mm, "end": v(-3.3, 15.37) * mm});
            skLineSegment(sketch, "E2719", {"start": v(-3.3, 15.37) * mm, "end": v(-3.39, 15.35) * mm});
            skLineSegment(sketch, "E2720", {"start": v(-3.39, 15.35) * mm, "end": v(-3.47, 15.32) * mm});
            skLineSegment(sketch, "E2721", {"start": v(-3.47, 15.32) * mm, "end": v(-3.56, 15.3) * mm});
            skLineSegment(sketch, "E2722", {"start": v(-3.56, 15.3) * mm, "end": v(-3.64, 15.26) * mm});
            skLineSegment(sketch, "E2723", {"start": v(-3.64, 15.26) * mm, "end": v(-3.72, 15.23) * mm});
            skLineSegment(sketch, "E2724", {"start": v(-3.72, 15.23) * mm, "end": v(-3.8, 15.2) * mm});
            skLineSegment(sketch, "E2725", {"start": v(-3.8, 15.2) * mm, "end": v(-3.88, 15.16) * mm});
            skLineSegment(sketch, "E2726", {"start": v(-3.88, 15.16) * mm, "end": v(-3.96, 15.13) * mm});
            skLineSegment(sketch, "E2727", {"start": v(-3.96, 15.13) * mm, "end": v(-4.04, 15.09) * mm});
            skLineSegment(sketch, "E2728", {"start": v(-4.04, 15.09) * mm, "end": v(-4.11, 15.05) * mm});
            skLineSegment(sketch, "E2729", {"start": v(-4.11, 15.05) * mm, "end": v(-4.19, 15) * mm});
            skLineSegment(sketch, "E2730", {"start": v(-4.19, 15) * mm, "end": v(-4.26, 14.96) * mm});
            skLineSegment(sketch, "E2731", {"start": v(-4.26, 14.96) * mm, "end": v(-4.34, 14.91) * mm});
            skLineSegment(sketch, "E2732", {"start": v(-4.34, 14.91) * mm, "end": v(-4.4, 14.86) * mm});
            skLineSegment(sketch, "E2733", {"start": v(-4.4, 14.86) * mm, "end": v(-4.48, 14.81) * mm});
            skLineSegment(sketch, "E2734", {"start": v(-4.48, 14.81) * mm, "end": v(-4.55, 14.75) * mm});
            skLineSegment(sketch, "E2735", {"start": v(-4.55, 14.75) * mm, "end": v(-4.62, 14.7) * mm});
            skLineSegment(sketch, "E2736", {"start": v(-4.62, 14.7) * mm, "end": v(-4.68, 14.63) * mm});
            skLineSegment(sketch, "E2737", {"start": v(-4.68, 14.63) * mm, "end": v(-4.75, 14.57) * mm});
            skLineSegment(sketch, "E2738", {"start": v(-4.75, 14.57) * mm, "end": v(-4.8, 14.5) * mm});
            skLineSegment(sketch, "E2739", {"start": v(-4.8, 14.5) * mm, "end": v(-4.87, 14.42) * mm});
            skLineSegment(sketch, "E2740", {"start": v(-4.87, 14.42) * mm, "end": v(-4.93, 14.33) * mm});
            skLineSegment(sketch, "E2741", {"start": v(-4.93, 14.33) * mm, "end": v(-4.99, 14.25) * mm});
            skLineSegment(sketch, "E2742", {"start": v(-4.99, 14.25) * mm, "end": v(-5.03, 14.17) * mm});
            skLineSegment(sketch, "E2743", {"start": v(-5.03, 14.17) * mm, "end": v(-5.08, 14.1) * mm});
            skLineSegment(sketch, "E2744", {"start": v(-5.08, 14.1) * mm, "end": v(-5.11, 14.01) * mm});
            skLineSegment(sketch, "E2745", {"start": v(-5.11, 14.01) * mm, "end": v(-5.15, 13.93) * mm});
            skLineSegment(sketch, "E2746", {"start": v(-5.15, 13.93) * mm, "end": v(-5.17, 13.85) * mm});
            skLineSegment(sketch, "E2747", {"start": v(-5.17, 13.85) * mm, "end": v(-5.2, 13.77) * mm});
            skLineSegment(sketch, "E2748", {"start": v(-5.2, 13.77) * mm, "end": v(-5.21, 13.7) * mm});
            skLineSegment(sketch, "E2749", {"start": v(-5.21, 13.7) * mm, "end": v(-5.22, 13.62) * mm});
            skLineSegment(sketch, "E2750", {"start": v(-5.22, 13.62) * mm, "end": v(-5.23, 13.54) * mm});
            skLineSegment(sketch, "E2751", {"start": v(-5.23, 13.54) * mm, "end": v(-5.24, 13.46) * mm});
            skLineSegment(sketch, "E2752", {"start": v(-5.24, 13.46) * mm, "end": v(-5.23, 13.38) * mm});
            skLineSegment(sketch, "E2753", {"start": v(-5.23, 13.38) * mm, "end": v(-5.23, 13.3) * mm});
            skLineSegment(sketch, "E2754", {"start": v(-5.23, 13.3) * mm, "end": v(-5.22, 13.24) * mm});
            skLineSegment(sketch, "E2755", {"start": v(-5.22, 13.24) * mm, "end": v(-5.2, 13.16) * mm});
            skLineSegment(sketch, "E2756", {"start": v(-5.2, 13.16) * mm, "end": v(-5.18, 13.1) * mm});
            skLineSegment(sketch, "E2757", {"start": v(-5.18, 13.1) * mm, "end": v(-5.16, 13.02) * mm});
            skLineSegment(sketch, "E2758", {"start": v(-5.16, 13.02) * mm, "end": v(-5.13, 12.95) * mm});
            skLineSegment(sketch, "E2759", {"start": v(-5.13, 12.95) * mm, "end": v(-5.1, 12.88) * mm});
            skLineSegment(sketch, "E2760", {"start": v(-5.1, 12.88) * mm, "end": v(-5.07, 12.82) * mm});
            skLineSegment(sketch, "E2761", {"start": v(-5.07, 12.82) * mm, "end": v(-5.03, 12.75) * mm});
            skLineSegment(sketch, "E2762", {"start": v(-5.03, 12.75) * mm, "end": v(-5, 12.7) * mm});
            skLineSegment(sketch, "E2763", {"start": v(-5, 12.7) * mm, "end": v(-4.95, 12.63) * mm});
            skLineSegment(sketch, "E2764", {"start": v(-4.95, 12.63) * mm, "end": v(-4.9, 12.57) * mm});
            skLineSegment(sketch, "E2765", {"start": v(-4.9, 12.57) * mm, "end": v(-4.85, 12.51) * mm});
            skLineSegment(sketch, "E2766", {"start": v(-4.85, 12.51) * mm, "end": v(-4.8, 12.46) * mm});
            skLineSegment(sketch, "E2767", {"start": v(-4.8, 12.46) * mm, "end": v(-4.74, 12.4) * mm});
            skLineSegment(sketch, "E2768", {"start": v(-4.74, 12.4) * mm, "end": v(-4.68, 12.35) * mm});
            skLineSegment(sketch, "E2769", {"start": v(-4.68, 12.35) * mm, "end": v(-4.62, 12.3) * mm});
            skLineSegment(sketch, "E2770", {"start": v(-4.62, 12.3) * mm, "end": v(-4.56, 12.26) * mm});
            skLineSegment(sketch, "E2771", {"start": v(-4.56, 12.26) * mm, "end": v(-4.5, 12.22) * mm});
            skLineSegment(sketch, "E2772", {"start": v(-4.5, 12.22) * mm, "end": v(-4.42, 12.17) * mm});
            skLineSegment(sketch, "E2773", {"start": v(-4.42, 12.17) * mm, "end": v(-4.35, 12.14) * mm});
            skLineSegment(sketch, "E2774", {"start": v(-4.35, 12.14) * mm, "end": v(-4.28, 12.1) * mm});
            skLineSegment(sketch, "E2775", {"start": v(-4.28, 12.1) * mm, "end": v(-4.2, 12.07) * mm});
            skLineSegment(sketch, "E2776", {"start": v(-4.2, 12.07) * mm, "end": v(-4.13, 12.04) * mm});
            skLineSegment(sketch, "E2777", {"start": v(-4.13, 12.04) * mm, "end": v(-4.05, 12.01) * mm});
            skLineSegment(sketch, "E2778", {"start": v(-4.05, 12.01) * mm, "end": v(-3.97, 11.99) * mm});
            skLineSegment(sketch, "E2779", {"start": v(-3.97, 11.99) * mm, "end": v(-3.89, 11.97) * mm});
            skLineSegment(sketch, "E2780", {"start": v(-3.89, 11.97) * mm, "end": v(-3.8, 11.95) * mm});
            skLineSegment(sketch, "E2781", {"start": v(-3.8, 11.95) * mm, "end": v(-3.72, 11.93) * mm});
            skLineSegment(sketch, "E2782", {"start": v(-3.72, 11.93) * mm, "end": v(-3.63, 11.92) * mm});
            skLineSegment(sketch, "E2783", {"start": v(-3.63, 11.92) * mm, "end": v(-3.55, 11.92) * mm});
            skLineSegment(sketch, "E2784", {"start": v(-3.55, 11.92) * mm, "end": v(-3.46, 11.91) * mm});
            skLineSegment(sketch, "E2785", {"start": v(-3.46, 11.91) * mm, "end": v(-3.37, 11.91) * mm});
            skLineSegment(sketch, "E2786", {"start": v(-3.37, 11.91) * mm, "end": v(-3.28, 11.92) * mm});
            skLineSegment(sketch, "E2787", {"start": v(-3.28, 11.92) * mm, "end": v(-3.19, 11.92) * mm});
            skLineSegment(sketch, "E2788", {"start": v(-3.19, 11.92) * mm, "end": v(-3.11, 11.93) * mm});
            skLineSegment(sketch, "E2789", {"start": v(-3.11, 11.93) * mm, "end": v(-3.03, 11.94) * mm});
            skLineSegment(sketch, "E2790", {"start": v(-3.03, 11.94) * mm, "end": v(-2.95, 11.96) * mm});
            skLineSegment(sketch, "E2791", {"start": v(-2.95, 11.96) * mm, "end": v(-2.88, 11.97) * mm});
            skLineSegment(sketch, "E2792", {"start": v(-2.88, 11.97) * mm, "end": v(-2.8, 12) * mm});
            skLineSegment(sketch, "E2793", {"start": v(-2.8, 12) * mm, "end": v(-2.72, 12.01) * mm});
            skLineSegment(sketch, "E2794", {"start": v(-2.72, 12.01) * mm, "end": v(-2.64, 12.03) * mm});
            skLineSegment(sketch, "E2795", {"start": v(-2.64, 12.03) * mm, "end": v(-2.56, 12.06) * mm});
            skLineSegment(sketch, "E2796", {"start": v(-2.56, 12.06) * mm, "end": v(-2.49, 12.08) * mm});
            skLineSegment(sketch, "E2797", {"start": v(-2.49, 12.08) * mm, "end": v(-2.4, 12.11) * mm});
            skLineSegment(sketch, "E2798", {"start": v(-2.4, 12.11) * mm, "end": v(-2.33, 12.14) * mm});
            skLineSegment(sketch, "E2799", {"start": v(-2.33, 12.14) * mm, "end": v(-2.25, 12.17) * mm});
            skLineSegment(sketch, "E2800", {"start": v(-2.25, 12.17) * mm, "end": v(-2.18, 12.2) * mm});
            skLineSegment(sketch, "E2801", {"start": v(-2.18, 12.2) * mm, "end": v(-2.1, 12.24) * mm});
            skLineSegment(sketch, "E2802", {"start": v(-2.1, 12.24) * mm, "end": v(-2.02, 12.28) * mm});
            skLineSegment(sketch, "E2803", {"start": v(-2.02, 12.28) * mm, "end": v(-1.95, 12.32) * mm});
            skLineSegment(sketch, "E2804", {"start": v(-1.95, 12.32) * mm, "end": v(-1.87, 12.36) * mm});
            skLineSegment(sketch, "E2805", {"start": v(-1.87, 12.36) * mm, "end": v(-1.8, 12.4) * mm});
            skLineSegment(sketch, "E2806", {"start": v(-1.8, 12.4) * mm, "end": v(-1.72, 12.44) * mm});
            skLineSegment(sketch, "E2807", {"start": v(-1.72, 12.44) * mm, "end": v(-1.65, 12.49) * mm});
            skLineSegment(sketch, "E2808", {"start": v(-1.65, 12.49) * mm, "end": v(-1.57, 12.53) * mm});
            skLineSegment(sketch, "E2809", {"start": v(-1.57, 12.53) * mm, "end": v(-1.5, 12.58) * mm});
            skLineSegment(sketch, "E2810", {"start": v(-1.5, 12.58) * mm, "end": v(-1.42, 12.63) * mm});
            skLineSegment(sketch, "E2811", {"start": v(-1.42, 12.63) * mm, "end": v(-1.35, 12.69) * mm});
            skLineSegment(sketch, "E2812", {"start": v(-1.35, 12.69) * mm, "end": v(-1.28, 12.74) * mm});
            skLineSegment(sketch, "E2813", {"start": v(-1.28, 12.74) * mm, "end": v(-1.2, 12.8) * mm});
            skLineSegment(sketch, "E2814", {"start": v(-1.2, 12.8) * mm, "end": v(-1.13, 12.85) * mm});
            skLineSegment(sketch, "E2815", {"start": v(-1.13, 12.85) * mm, "end": v(-1.06, 12.9) * mm});
            skLineSegment(sketch, "E2816", {"start": v(-1.06, 12.9) * mm, "end": v(-0.99, 12.97) * mm});
            skLineSegment(sketch, "E2817", {"start": v(-0.99, 12.97) * mm, "end": v(-0.92, 13.03) * mm});
            skLineSegment(sketch, "E2818", {"start": v(-0.92, 13.03) * mm, "end": v(-0.85, 13.09) * mm});
            skLineSegment(sketch, "E2819", {"start": v(-0.85, 13.09) * mm, "end": v(-0.78, 13.15) * mm});
            skLineSegment(sketch, "E2820", {"start": v(-0.78, 13.15) * mm, "end": v(-0.7, 13.22) * mm});
            skLineSegment(sketch, "E2821", {"start": v(-0.7, 13.22) * mm, "end": v(-0.64, 13.28) * mm});
            skLineSegment(sketch, "E2822", {"start": v(-0.64, 13.28) * mm, "end": v(-0.57, 13.35) * mm});
            skLineSegment(sketch, "E2823", {"start": v(-0.57, 13.35) * mm, "end": v(-0.5, 13.42) * mm});
            skLineSegment(sketch, "E2824", {"start": v(-0.5, 13.42) * mm, "end": v(-0.44, 13.48) * mm});
            skLineSegment(sketch, "E2825", {"start": v(-0.44, 13.48) * mm, "end": v(-0.37, 13.55) * mm});
            skLineSegment(sketch, "E2826", {"start": v(-0.37, 13.55) * mm, "end": v(-0.3, 13.63) * mm});
            skLineSegment(sketch, "E2827", {"start": v(-0.3, 13.63) * mm, "end": v(-0.24, 13.7) * mm});
            skLineSegment(sketch, "E2828", {"start": v(-0.24, 13.7) * mm, "end": v(-0.18, 13.77) * mm});
            skLineSegment(sketch, "E2829", {"start": v(-0.18, 13.77) * mm, "end": v(-0.12, 13.85) * mm});
            skLineSegment(sketch, "E2830", {"start": v(-0.12, 13.85) * mm, "end": v(-0.05, 13.92) * mm});
            skLineSegment(sketch, "E2831", {"start": v(-0.05, 13.92) * mm, "end": v(0, 14) * mm});
            skLineSegment(sketch, "E2832", {"start": v(0, 14) * mm, "end": v(0.07, 14.07) * mm});
            skLineSegment(sketch, "E2833", {"start": v(0.07, 14.07) * mm, "end": v(0.13, 14.15) * mm});
            skLineSegment(sketch, "E2834", {"start": v(0.13, 14.15) * mm, "end": v(0.2, 14.23) * mm});
            skLineSegment(sketch, "E2835", {"start": v(0.2, 14.23) * mm, "end": v(0.25, 14.31) * mm});
            skLineSegment(sketch, "E2836", {"start": v(0.25, 14.31) * mm, "end": v(0.3, 14.4) * mm});
            skLineSegment(sketch, "E2837", {"start": v(0.3, 14.4) * mm, "end": v(0.36, 14.47) * mm});
            skLineSegment(sketch, "E2838", {"start": v(0.36, 14.47) * mm, "end": v(0.42, 14.55) * mm});
            skLineSegment(sketch, "E2839", {"start": v(0.42, 14.55) * mm, "end": v(0.48, 14.64) * mm});
            skLineSegment(sketch, "E2840", {"start": v(0.48, 14.64) * mm, "end": v(0.53, 14.72) * mm});
            skLineSegment(sketch, "E2841", {"start": v(0.53, 14.72) * mm, "end": v(0.58, 14.8) * mm});
            skLineSegment(sketch, "E2842", {"start": v(0.58, 14.8) * mm, "end": v(0.64, 14.89) * mm});
            skLineSegment(sketch, "E2843", {"start": v(0.64, 14.89) * mm, "end": v(0.69, 14.97) * mm});
            skLineSegment(sketch, "E2844", {"start": v(0.69, 14.97) * mm, "end": v(0.74, 15.06) * mm});
            skLineSegment(sketch, "E2845", {"start": v(0.74, 15.06) * mm, "end": v(0.8, 15.15) * mm});
            skLineSegment(sketch, "E2846", {"start": v(0.8, 15.15) * mm, "end": v(0.84, 15.23) * mm});
            skLineSegment(sketch, "E2847", {"start": v(0.84, 15.23) * mm, "end": v(0.89, 15.32) * mm});
            skLineSegment(sketch, "E2848", {"start": v(0.89, 15.32) * mm, "end": v(0.93, 15.4) * mm});
            skLineSegment(sketch, "E2849", {"start": v(0.93, 15.4) * mm, "end": v(0.98, 15.5) * mm});
            skLineSegment(sketch, "E2850", {"start": v(0.98, 15.5) * mm, "end": v(1.02, 15.59) * mm});
            skLineSegment(sketch, "E2851", {"start": v(1.02, 15.59) * mm, "end": v(1.07, 15.68) * mm});
            skLineSegment(sketch, "E2852", {"start": v(1.07, 15.68) * mm, "end": v(1.11, 15.76) * mm});
            skLineSegment(sketch, "E2853", {"start": v(1.11, 15.76) * mm, "end": v(1.15, 15.85) * mm});
            skLineSegment(sketch, "E2854", {"start": v(1.15, 15.85) * mm, "end": v(1.2, 15.94) * mm});
            skLineSegment(sketch, "E2855", {"start": v(1.2, 15.94) * mm, "end": v(1.23, 16.03) * mm});
            skLineSegment(sketch, "E2856", {"start": v(1.23, 16.03) * mm, "end": v(1.27, 16.12) * mm});
            skLineSegment(sketch, "E2857", {"start": v(1.27, 16.12) * mm, "end": v(1.3, 16.22) * mm});
            skLineSegment(sketch, "E2858", {"start": v(1.3, 16.22) * mm, "end": v(1.34, 16.3) * mm});
            skLineSegment(sketch, "E2859", {"start": v(1.34, 16.3) * mm, "end": v(1.38, 16.4) * mm});
            skLineSegment(sketch, "E2860", {"start": v(1.38, 16.4) * mm, "end": v(1.41, 16.49) * mm});
            skLineSegment(sketch, "E2861", {"start": v(1.41, 16.49) * mm, "end": v(1.44, 16.58) * mm});
            skLineSegment(sketch, "E2862", {"start": v(1.44, 16.58) * mm, "end": v(1.48, 16.67) * mm});
            skLineSegment(sketch, "E2863", {"start": v(1.48, 16.67) * mm, "end": v(1.5, 16.76) * mm});
            skLineSegment(sketch, "E2864", {"start": v(1.5, 16.76) * mm, "end": v(1.53, 16.85) * mm});
            skLineSegment(sketch, "E2865", {"start": v(1.53, 16.85) * mm, "end": v(1.56, 16.94) * mm});
            skLineSegment(sketch, "E2866", {"start": v(1.56, 16.94) * mm, "end": v(1.59, 17.04) * mm});
            skLineSegment(sketch, "E2867", {"start": v(1.59, 17.04) * mm, "end": v(1.61, 17.13) * mm});
            skLineSegment(sketch, "E2868", {"start": v(1.61, 17.13) * mm, "end": v(1.64, 17.22) * mm});
            skLineSegment(sketch, "E2869", {"start": v(1.64, 17.22) * mm, "end": v(1.66, 17.3) * mm});
            skLineSegment(sketch, "E2870", {"start": v(1.66, 17.3) * mm, "end": v(1.68, 17.4) * mm});
            skLineSegment(sketch, "E2871", {"start": v(1.68, 17.4) * mm, "end": v(1.7, 17.49) * mm});
            skLineSegment(sketch, "E2872", {"start": v(1.7, 17.49) * mm, "end": v(1.71, 17.58) * mm});
            skLineSegment(sketch, "E2873", {"start": v(1.71, 17.58) * mm, "end": v(1.73, 17.67) * mm});
            skLineSegment(sketch, "E2874", {"start": v(1.73, 17.67) * mm, "end": v(1.75, 17.76) * mm});
            skLineSegment(sketch, "E2875", {"start": v(1.75, 17.76) * mm, "end": v(1.76, 17.85) * mm});
            skLineSegment(sketch, "E2876", {"start": v(1.76, 17.85) * mm, "end": v(1.77, 17.94) * mm});
            skLineSegment(sketch, "E2877", {"start": v(1.77, 17.94) * mm, "end": v(1.78, 18.02) * mm});
            skLineSegment(sketch, "E2878", {"start": v(1.78, 18.02) * mm, "end": v(1.8, 18.11) * mm});
            skLineSegment(sketch, "E2879", {"start": v(1.8, 18.11) * mm, "end": v(1.8, 18.2) * mm});
            skLineSegment(sketch, "E2880", {"start": v(1.8, 18.2) * mm, "end": v(1.8, 18.29) * mm});
            skLineSegment(sketch, "E2881", {"start": v(1.8, 18.29) * mm, "end": v(1.8, 18.37) * mm});
            skLineSegment(sketch, "E2882", {"start": v(1.8, 18.37) * mm, "end": v(1.81, 18.46) * mm});
            skLineSegment(sketch, "E2883", {"start": v(1.81, 18.46) * mm, "end": v(1.81, 18.54) * mm});
            skLineSegment(sketch, "E2884", {"start": v(1.81, 18.54) * mm, "end": v(1.81, 18.63) * mm});
            skLineSegment(sketch, "E2885", {"start": v(1.81, 18.63) * mm, "end": v(1.8, 18.71) * mm});
            skLineSegment(sketch, "E2886", {"start": v(1.8, 18.71) * mm, "end": v(1.8, 18.8) * mm});
            skLineSegment(sketch, "E2887", {"start": v(1.8, 18.8) * mm, "end": v(1.8, 18.88) * mm});
            skLineSegment(sketch, "E2888", {"start": v(1.8, 18.88) * mm, "end": v(1.8, 18.96) * mm});
            skLineSegment(sketch, "E2889", {"start": v(1.8, 18.96) * mm, "end": v(1.78, 19.04) * mm});
            skLineSegment(sketch, "E2890", {"start": v(1.78, 19.04) * mm, "end": v(1.77, 19.13) * mm});
            skLineSegment(sketch, "E2891", {"start": v(1.77, 19.13) * mm, "end": v(1.76, 19.2) * mm});
            skLineSegment(sketch, "E2892", {"start": v(1.76, 19.2) * mm, "end": v(1.75, 19.28) * mm});
            skLineSegment(sketch, "E2893", {"start": v(1.75, 19.28) * mm, "end": v(1.73, 19.36) * mm});
            skLineSegment(sketch, "E2894", {"start": v(1.73, 19.36) * mm, "end": v(1.72, 19.44) * mm});
            skLineSegment(sketch, "E2895", {"start": v(1.72, 19.44) * mm, "end": v(1.7, 19.52) * mm});
            skLineSegment(sketch, "E2896", {"start": v(1.7, 19.52) * mm, "end": v(1.68, 19.6) * mm});
            skLineSegment(sketch, "E2897", {"start": v(1.68, 19.6) * mm, "end": v(1.65, 19.67) * mm});
            skLineSegment(sketch, "E2898", {"start": v(1.65, 19.67) * mm, "end": v(1.62, 19.75) * mm});
            skLineSegment(sketch, "E2899", {"start": v(1.62, 19.75) * mm, "end": v(1.6, 19.84) * mm});
            skLineSegment(sketch, "E2900", {"start": v(1.6, 19.84) * mm, "end": v(1.56, 19.92) * mm});
            skLineSegment(sketch, "E2901", {"start": v(1.56, 19.92) * mm, "end": v(1.53, 20) * mm});
            skLineSegment(sketch, "E2902", {"start": v(1.53, 20) * mm, "end": v(1.5, 20.07) * mm});
            skLineSegment(sketch, "E2903", {"start": v(1.5, 20.07) * mm, "end": v(1.45, 20.15) * mm});
            skLineSegment(sketch, "E2904", {"start": v(1.45, 20.15) * mm, "end": v(1.41, 20.22) * mm});
            skLineSegment(sketch, "E2905", {"start": v(1.41, 20.22) * mm, "end": v(1.37, 20.29) * mm});
            skLineSegment(sketch, "E2906", {"start": v(1.37, 20.29) * mm, "end": v(1.33, 20.36) * mm});
            skLineSegment(sketch, "E2907", {"start": v(1.33, 20.36) * mm, "end": v(1.29, 20.42) * mm});
            skLineSegment(sketch, "E2908", {"start": v(1.29, 20.42) * mm, "end": v(1.24, 20.49) * mm});
            skLineSegment(sketch, "E2909", {"start": v(1.24, 20.49) * mm, "end": v(1.2, 20.55) * mm});
            skLineSegment(sketch, "E2910", {"start": v(1.2, 20.55) * mm, "end": v(1.15, 20.6) * mm});
            skLineSegment(sketch, "E2911", {"start": v(1.15, 20.6) * mm, "end": v(1.1, 20.66) * mm});
            skLineSegment(sketch, "E2912", {"start": v(1.1, 20.66) * mm, "end": v(1.04, 20.72) * mm});
            skLineSegment(sketch, "E2913", {"start": v(1.04, 20.72) * mm, "end": v(1, 20.77) * mm});
            skLineSegment(sketch, "E2914", {"start": v(1, 20.77) * mm, "end": v(0.94, 20.82) * mm});
            skLineSegment(sketch, "E2915", {"start": v(0.94, 20.82) * mm, "end": v(0.88, 20.87) * mm});
            skLineSegment(sketch, "E2916", {"start": v(0.88, 20.87) * mm, "end": v(0.82, 20.92) * mm});
            skLineSegment(sketch, "E2917", {"start": v(0.82, 20.92) * mm, "end": v(0.76, 20.96) * mm});
            skLineSegment(sketch, "E2918", {"start": v(0.76, 20.96) * mm, "end": v(0.7, 21) * mm});
            skLineSegment(sketch, "E2919", {"start": v(0.7, 21) * mm, "end": v(0.64, 21.05) * mm});
            skLineSegment(sketch, "E2920", {"start": v(0.64, 21.05) * mm, "end": v(0.58, 21.09) * mm});
            skLineSegment(sketch, "E2921", {"start": v(0.58, 21.09) * mm, "end": v(0.52, 21.13) * mm});
            skLineSegment(sketch, "E2922", {"start": v(0.52, 21.13) * mm, "end": v(0.45, 21.16) * mm});
            skLineSegment(sketch, "E2923", {"start": v(0.45, 21.16) * mm, "end": v(0.39, 21.2) * mm});
            skLineSegment(sketch, "E2924", {"start": v(0.39, 21.2) * mm, "end": v(0.32, 21.23) * mm});
            skLineSegment(sketch, "E2925", {"start": v(0.32, 21.23) * mm, "end": v(0.25, 21.26) * mm});
            skLineSegment(sketch, "E2926", {"start": v(0.25, 21.26) * mm, "end": v(0.18, 21.29) * mm});
            skLineSegment(sketch, "E2927", {"start": v(0.18, 21.29) * mm, "end": v(0.11, 21.31) * mm});
            skLineSegment(sketch, "E2928", {"start": v(0.11, 21.31) * mm, "end": v(0.04, 21.34) * mm});
            skLineSegment(sketch, "E2929", {"start": v(0.04, 21.34) * mm, "end": v(-0.03, 21.36) * mm});
            skLineSegment(sketch, "E2930", {"start": v(-0.03, 21.36) * mm, "end": v(-0.1, 21.38) * mm});
            skLineSegment(sketch, "E2931", {"start": v(-0.1, 21.38) * mm, "end": v(-0.18, 21.4) * mm});
            skLineSegment(sketch, "E2932", {"start": v(-0.18, 21.4) * mm, "end": v(-0.26, 21.42) * mm});
            skLineSegment(sketch, "E2933", {"start": v(-0.26, 21.42) * mm, "end": v(-0.33, 21.44) * mm});
            skLineSegment(sketch, "E2934", {"start": v(-0.33, 21.44) * mm, "end": v(-0.4, 21.46) * mm});
            skLineSegment(sketch, "E2935", {"start": v(-0.4, 21.46) * mm, "end": v(-0.49, 21.47) * mm});
            skLineSegment(sketch, "E2936", {"start": v(-0.49, 21.47) * mm, "end": v(-0.57, 21.48) * mm});
            skLineSegment(sketch, "E2937", {"start": v(-0.57, 21.48) * mm, "end": v(-0.65, 21.5) * mm});
            skLineSegment(sketch, "E2938", {"start": v(-0.65, 21.5) * mm, "end": v(-0.73, 21.5) * mm});
            skLineSegment(sketch, "E2939", {"start": v(-0.73, 21.5) * mm, "end": v(-0.8, 21.51) * mm});
            skLineSegment(sketch, "E2940", {"start": v(-0.8, 21.51) * mm, "end": v(-0.9, 21.52) * mm});
            skLineSegment(sketch, "E2941", {"start": v(-0.9, 21.52) * mm, "end": v(-0.97, 21.52) * mm});
            skLineSegment(sketch, "E2942", {"start": v(-0.97, 21.52) * mm, "end": v(-1.06, 21.53) * mm});
            skLineSegment(sketch, "E2943", {"start": v(-1.06, 21.53) * mm, "end": v(-1.14, 21.53) * mm});
            skLineSegment(sketch, "E2944", {"start": v(-1.14, 21.53) * mm, "end": v(-1.23, 21.53) * mm});
            skLineSegment(sketch, "E2945", {"start": v(-1.23, 21.53) * mm, "end": v(-1.31, 21.53) * mm});
            skLineSegment(sketch, "E2946", {"start": v(-1.31, 21.53) * mm, "end": v(-1.4, 21.53) * mm});
            skLineSegment(sketch, "E2947", {"start": v(-1.4, 21.53) * mm, "end": v(-1.48, 21.53) * mm});
            skLineSegment(sketch, "E2948", {"start": v(-1.48, 21.53) * mm, "end": v(-1.57, 21.52) * mm});
            skLineSegment(sketch, "E2949", {"start": v(-1.57, 21.52) * mm, "end": v(-1.66, 21.52) * mm});
            skLineSegment(sketch, "E2950", {"start": v(-1.66, 21.52) * mm, "end": v(-1.75, 21.51) * mm});
            skLineSegment(sketch, "E2951", {"start": v(-1.75, 21.51) * mm, "end": v(-1.84, 21.5) * mm});
            skLineSegment(sketch, "E2952", {"start": v(-1.84, 21.5) * mm, "end": v(-1.93, 21.5) * mm});
            skLineSegment(sketch, "E2953", {"start": v(-1.93, 21.5) * mm, "end": v(-2.02, 21.49) * mm});
            skLineSegment(sketch, "E2954", {"start": v(-2.02, 21.49) * mm, "end": v(-2.1, 21.48) * mm});
            skLineSegment(sketch, "E2955", {"start": v(-2.1, 21.48) * mm, "end": v(-2.2, 21.47) * mm});
            skLineSegment(sketch, "E2956", {"start": v(-2.2, 21.47) * mm, "end": v(-2.29, 21.45) * mm});
            skLineSegment(sketch, "E2957", {"start": v(-2.29, 21.45) * mm, "end": v(-2.38, 21.44) * mm});
            skLineSegment(sketch, "E2958", {"start": v(-2.38, 21.44) * mm, "end": v(-2.47, 21.42) * mm});
            skLineSegment(sketch, "E2959", {"start": v(-2.47, 21.42) * mm, "end": v(-2.56, 21.4) * mm});
            skLineSegment(sketch, "E2960", {"start": v(-2.56, 21.4) * mm, "end": v(-2.65, 21.4) * mm});
            skLineSegment(sketch, "E2961", {"start": v(-2.65, 21.4) * mm, "end": v(-2.74, 21.37) * mm});
            skLineSegment(sketch, "E2962", {"start": v(-2.74, 21.37) * mm, "end": v(-2.84, 21.36) * mm});
            skLineSegment(sketch, "E2963", {"start": v(-2.84, 21.36) * mm, "end": v(-2.93, 21.34) * mm});
            skLineSegment(sketch, "E2964", {"start": v(-2.93, 21.34) * mm, "end": v(-3.02, 21.32) * mm});
            skLineSegment(sketch, "E2965", {"start": v(-3.02, 21.32) * mm, "end": v(-3.11, 21.3) * mm});
            skLineSegment(sketch, "E2966", {"start": v(-3.11, 21.3) * mm, "end": v(-3.2, 21.27) * mm});
            skLineSegment(sketch, "E2967", {"start": v(-3.2, 21.27) * mm, "end": v(-3.3, 21.25) * mm});
            skLineSegment(sketch, "E2968", {"start": v(-3.3, 21.25) * mm, "end": v(-3.4, 21.23) * mm});
            skLineSegment(sketch, "E2969", {"start": v(-3.4, 21.23) * mm, "end": v(-3.49, 21.2) * mm});
            skLineSegment(sketch, "E2970", {"start": v(-3.49, 21.2) * mm, "end": v(-3.58, 21.18) * mm});
            skLineSegment(sketch, "E2971", {"start": v(-3.58, 21.18) * mm, "end": v(-3.67, 21.15) * mm});
            skLineSegment(sketch, "E2972", {"start": v(-3.67, 21.15) * mm, "end": v(-3.76, 21.13) * mm});
            skLineSegment(sketch, "E2973", {"start": v(-3.76, 21.13) * mm, "end": v(-3.86, 21.1) * mm});
            skLineSegment(sketch, "E2974", {"start": v(-3.86, 21.1) * mm, "end": v(-3.95, 21.07) * mm});
            skLineSegment(sketch, "E2975", {"start": v(-3.95, 21.07) * mm, "end": v(-4.04, 21.05) * mm});
            skLineSegment(sketch, "E2976", {"start": v(-4.04, 21.05) * mm, "end": v(-4.13, 21.02) * mm});
            skLineSegment(sketch, "E2977", {"start": v(-4.13, 21.02) * mm, "end": v(-4.23, 20.99) * mm});
            skLineSegment(sketch, "E2978", {"start": v(-4.23, 20.99) * mm, "end": v(-4.32, 20.96) * mm});
            skLineSegment(sketch, "E2979", {"start": v(-4.32, 20.96) * mm, "end": v(-4.41, 20.93) * mm});
            skLineSegment(sketch, "E2980", {"start": v(-4.41, 20.93) * mm, "end": v(-4.5, 20.9) * mm});
            skLineSegment(sketch, "E2981", {"start": v(-4.5, 20.9) * mm, "end": v(-4.6, 20.87) * mm});
            skLineSegment(sketch, "E2982", {"start": v(-4.6, 20.87) * mm, "end": v(-4.68, 20.84) * mm});
            skLineSegment(sketch, "E2983", {"start": v(-4.68, 20.84) * mm, "end": v(-4.77, 20.8) * mm});
            skLineSegment(sketch, "E2984", {"start": v(-4.77, 20.8) * mm, "end": v(-4.86, 20.77) * mm});
            skLineSegment(sketch, "E2985", {"start": v(-4.86, 20.77) * mm, "end": v(-4.95, 20.74) * mm});
            skLineSegment(sketch, "E2986", {"start": v(-4.95, 20.74) * mm, "end": v(-5.04, 20.7) * mm});
            skLineSegment(sketch, "E2987", {"start": v(-5.04, 20.7) * mm, "end": v(-5.13, 20.67) * mm});
            skLineSegment(sketch, "E2988", {"start": v(-5.13, 20.67) * mm, "end": v(-5.22, 20.64) * mm});
            skLineSegment(sketch, "E2989", {"start": v(-5.22, 20.64) * mm, "end": v(-5.3, 20.6) * mm});
            skLineSegment(sketch, "E2990", {"start": v(-5.3, 20.6) * mm, "end": v(-5.4, 20.57) * mm});
            skLineSegment(sketch, "E2991", {"start": v(-5.4, 20.57) * mm, "end": v(-5.48, 20.54) * mm});
            skLineSegment(sketch, "E2992", {"start": v(-5.48, 20.54) * mm, "end": v(-5.57, 20.5) * mm});
            skLineSegment(sketch, "E2993", {"start": v(-5.57, 20.5) * mm, "end": v(-5.65, 20.47) * mm});
            skLineSegment(sketch, "E2994", {"start": v(-5.65, 20.47) * mm, "end": v(-5.74, 20.43) * mm});
            skLineSegment(sketch, "E2995", {"start": v(-5.74, 20.43) * mm, "end": v(-5.82, 20.4) * mm});
            skLineSegment(sketch, "E2996", {"start": v(-5.82, 20.4) * mm, "end": v(-5.9, 20.36) * mm});
            skLineSegment(sketch, "E2997", {"start": v(-5.9, 20.36) * mm, "end": v(-6, 20.33) * mm});
            skLineSegment(sketch, "E2998", {"start": v(-6, 20.33) * mm, "end": v(-6.07, 20.3) * mm});
            skLineSegment(sketch, "E2999", {"start": v(-6.07, 20.3) * mm, "end": v(-6.15, 20.26) * mm});
            skLineSegment(sketch, "E3000", {"start": v(-6.15, 20.26) * mm, "end": v(-6.24, 20.22) * mm});
            skLineSegment(sketch, "E3001", {"start": v(-6.24, 20.22) * mm, "end": v(-6.32, 20.19) * mm});
            skLineSegment(sketch, "E3002", {"start": v(-6.32, 20.19) * mm, "end": v(-6.4, 20.15) * mm});
            skLineSegment(sketch, "E3003", {"start": v(-6.4, 20.15) * mm, "end": v(-6.47, 20.12) * mm});
            skLineSegment(sketch, "E3004", {"start": v(-6.47, 20.12) * mm, "end": v(-6.55, 20.08) * mm});
            skLineSegment(sketch, "E3005", {"start": v(-6.55, 20.08) * mm, "end": v(-6.63, 20.05) * mm});
            skLineSegment(sketch, "E3006", {"start": v(-6.63, 20.05) * mm, "end": v(-6.7, 20.01) * mm});
            skLineSegment(sketch, "E3007", {"start": v(-6.7, 20.01) * mm, "end": v(-6.78, 19.98) * mm});
            skLineSegment(sketch, "E3008", {"start": v(-6.78, 19.98) * mm, "end": v(-6.85, 19.94) * mm});
            skLineSegment(sketch, "E3009", {"start": v(-6.85, 19.94) * mm, "end": v(-6.92, 19.9) * mm});
            skLineSegment(sketch, "E3010", {"start": v(-6.92, 19.9) * mm, "end": v(-7, 19.87) * mm});
            skLineSegment(sketch, "E3011", {"start": v(-7, 19.87) * mm, "end": v(-7.07, 19.84) * mm});
            skLineSegment(sketch, "E3012", {"start": v(-7.07, 19.84) * mm, "end": v(-7.14, 19.8) * mm});
            skLineSegment(sketch, "E3013", {"start": v(-7.14, 19.8) * mm, "end": v(-7.2, 19.77) * mm});
            skLineSegment(sketch, "E3014", {"start": v(-7.2, 19.77) * mm, "end": v(-7.27, 19.74) * mm});
            skLineSegment(sketch, "E3015", {"start": v(-7.27, 19.74) * mm, "end": v(-7.34, 19.7) * mm});
            skLineSegment(sketch, "E3016", {"start": v(-7.34, 19.7) * mm, "end": v(-7.4, 19.68) * mm});
            skLineSegment(sketch, "E3017", {"start": v(-7.4, 19.68) * mm, "end": v(-7.47, 19.64) * mm});
            skLineSegment(sketch, "E3018", {"start": v(-7.47, 19.64) * mm, "end": v(-7.53, 19.61) * mm});
            skLineSegment(sketch, "E3019", {"start": v(-7.53, 19.61) * mm, "end": v(-7.6, 19.58) * mm});
            skLineSegment(sketch, "E3020", {"start": v(-7.6, 19.58) * mm, "end": v(-7.65, 19.55) * mm});
            skLineSegment(sketch, "E3021", {"start": v(-7.65, 19.55) * mm, "end": v(-7.7, 19.52) * mm});
            skLineSegment(sketch, "E3022", {"start": v(-7.7, 19.52) * mm, "end": v(-7.77, 19.5) * mm});
            skLineSegment(sketch, "E3023", {"start": v(-7.77, 19.5) * mm, "end": v(-7.82, 19.46) * mm});
            skLineSegment(sketch, "E3024", {"start": v(-7.82, 19.46) * mm, "end": v(-7.88, 19.43) * mm});
            skLineSegment(sketch, "E3025", {"start": v(-7.88, 19.43) * mm, "end": v(-7.93, 19.4) * mm});
            skLineSegment(sketch, "E3026", {"start": v(-7.93, 19.4) * mm, "end": v(-7.98, 19.38) * mm});
            skLineSegment(sketch, "E3027", {"start": v(-7.98, 19.38) * mm, "end": v(-8.03, 19.35) * mm});
            skLineSegment(sketch, "E3028", {"start": v(-8.03, 19.35) * mm, "end": v(-8.12, 19.3) * mm});
            skLineSegment(sketch, "E3029", {"start": v(-8.12, 19.3) * mm, "end": v(-8.2, 19.26) * mm});
            skLineSegment(sketch, "E3030", {"start": v(-8.2, 19.26) * mm, "end": v(-8.28, 19.22) * mm});
            skLineSegment(sketch, "E3031", {"start": v(-8.28, 19.22) * mm, "end": v(-8.36, 19.18) * mm});
            skLineSegment(sketch, "E3032", {"start": v(-8.36, 19.18) * mm, "end": v(-8.44, 19.13) * mm});
            skLineSegment(sketch, "E3033", {"start": v(-8.44, 19.13) * mm, "end": v(-8.52, 19.08) * mm});
            skLineSegment(sketch, "E3034", {"start": v(-8.52, 19.08) * mm, "end": v(-8.6, 19.04) * mm});
            skLineSegment(sketch, "E3035", {"start": v(-8.6, 19.04) * mm, "end": v(-8.69, 19) * mm});
            skLineSegment(sketch, "E3036", {"start": v(-8.69, 19) * mm, "end": v(-8.77, 18.95) * mm});
            skLineSegment(sketch, "E3037", {"start": v(-8.77, 18.95) * mm, "end": v(-8.85, 18.9) * mm});
            skLineSegment(sketch, "E3038", {"start": v(-8.85, 18.9) * mm, "end": v(-8.93, 18.85) * mm});
            skLineSegment(sketch, "E3039", {"start": v(-8.93, 18.85) * mm, "end": v(-9.02, 18.8) * mm});
            skLineSegment(sketch, "E3040", {"start": v(-9.02, 18.8) * mm, "end": v(-9.1, 18.76) * mm});
            skLineSegment(sketch, "E3041", {"start": v(-9.1, 18.76) * mm, "end": v(-9.18, 18.7) * mm});
            skLineSegment(sketch, "E3042", {"start": v(-9.18, 18.7) * mm, "end": v(-9.26, 18.66) * mm});
            skLineSegment(sketch, "E3043", {"start": v(-9.26, 18.66) * mm, "end": v(-9.34, 18.61) * mm});
            skLineSegment(sketch, "E3044", {"start": v(-9.34, 18.61) * mm, "end": v(-9.42, 18.56) * mm});
            skLineSegment(sketch, "E3045", {"start": v(-9.42, 18.56) * mm, "end": v(-9.5, 18.51) * mm});
            skLineSegment(sketch, "E3046", {"start": v(-9.5, 18.51) * mm, "end": v(-9.59, 18.46) * mm});
            skLineSegment(sketch, "E3047", {"start": v(-9.59, 18.46) * mm, "end": v(-9.67, 18.41) * mm});
            skLineSegment(sketch, "E3048", {"start": v(-9.67, 18.41) * mm, "end": v(-9.75, 18.36) * mm});
            skLineSegment(sketch, "E3049", {"start": v(-9.75, 18.36) * mm, "end": v(-9.83, 18.31) * mm});
            skLineSegment(sketch, "E3050", {"start": v(-9.83, 18.31) * mm, "end": v(-9.91, 18.26) * mm});
            skLineSegment(sketch, "E3051", {"start": v(-9.91, 18.26) * mm, "end": v(-10, 18.2) * mm});
            skLineSegment(sketch, "E3052", {"start": v(-10, 18.2) * mm, "end": v(-10.07, 18.16) * mm});
            skLineSegment(sketch, "E3053", {"start": v(-10.07, 18.16) * mm, "end": v(-10.15, 18.1) * mm});
            skLineSegment(sketch, "E3054", {"start": v(-10.15, 18.1) * mm, "end": v(-10.23, 18.05) * mm});
            skLineSegment(sketch, "E3055", {"start": v(-10.23, 18.05) * mm, "end": v(-10.32, 18) * mm});
            skLineSegment(sketch, "E3056", {"start": v(-10.32, 18) * mm, "end": v(-10.4, 17.95) * mm});
            skLineSegment(sketch, "E3057", {"start": v(-10.4, 17.95) * mm, "end": v(-10.48, 17.9) * mm});
            skLineSegment(sketch, "E3058", {"start": v(-10.48, 17.9) * mm, "end": v(-10.56, 17.84) * mm});
            skLineSegment(sketch, "E3059", {"start": v(-10.56, 17.84) * mm, "end": v(-10.64, 17.79) * mm});
            skLineSegment(sketch, "E3060", {"start": v(-10.64, 17.79) * mm, "end": v(-10.72, 17.73) * mm});
            skLineSegment(sketch, "E3061", {"start": v(-10.72, 17.73) * mm, "end": v(-10.8, 17.68) * mm});
            skLineSegment(sketch, "E3062", {"start": v(-10.8, 17.68) * mm, "end": v(-10.88, 17.62) * mm});
            skLineSegment(sketch, "E3063", {"start": v(-10.88, 17.62) * mm, "end": v(-10.96, 17.57) * mm});
            skLineSegment(sketch, "E3064", {"start": v(-10.96, 17.57) * mm, "end": v(-11.04, 17.51) * mm});
            skLineSegment(sketch, "E3065", {"start": v(-11.04, 17.51) * mm, "end": v(-11.12, 17.46) * mm});
            skLineSegment(sketch, "E3066", {"start": v(-11.12, 17.46) * mm, "end": v(-11.2, 17.4) * mm});
            skLineSegment(sketch, "E3067", {"start": v(-11.2, 17.4) * mm, "end": v(-11.28, 17.35) * mm});
            skLineSegment(sketch, "E3068", {"start": v(-11.28, 17.35) * mm, "end": v(-11.36, 17.29) * mm});
            skLineSegment(sketch, "E3069", {"start": v(-11.36, 17.29) * mm, "end": v(-11.44, 17.23) * mm});
            skLineSegment(sketch, "E3070", {"start": v(-11.44, 17.23) * mm, "end": v(-11.52, 17.17) * mm});
            skLineSegment(sketch, "E3071", {"start": v(-11.52, 17.17) * mm, "end": v(-11.6, 17.12) * mm});
            skLineSegment(sketch, "E3072", {"start": v(-11.6, 17.12) * mm, "end": v(-11.68, 17.06) * mm});
            skLineSegment(sketch, "E3073", {"start": v(-11.68, 17.06) * mm, "end": v(-11.76, 17) * mm});
            skLineSegment(sketch, "E3074", {"start": v(-11.76, 17) * mm, "end": v(-11.83, 16.94) * mm});
            skLineSegment(sketch, "E3075", {"start": v(-11.83, 16.94) * mm, "end": v(-11.91, 16.88) * mm});
            skLineSegment(sketch, "E3076", {"start": v(-11.91, 16.88) * mm, "end": v(-12, 16.82) * mm});
            skLineSegment(sketch, "E3077", {"start": v(-12, 16.82) * mm, "end": v(-12.07, 16.77) * mm});
            skLineSegment(sketch, "E3078", {"start": v(-12.07, 16.77) * mm, "end": v(-12.15, 16.7) * mm});
            skLineSegment(sketch, "E3079", {"start": v(-12.15, 16.7) * mm, "end": v(-12.23, 16.65) * mm});
            skLineSegment(sketch, "E3080", {"start": v(-12.23, 16.65) * mm, "end": v(-12.3, 16.59) * mm});
            skLineSegment(sketch, "E3081", {"start": v(-12.3, 16.59) * mm, "end": v(-12.38, 16.53) * mm});
            skLineSegment(sketch, "E3082", {"start": v(-12.38, 16.53) * mm, "end": v(-12.46, 16.46) * mm});
            skLineSegment(sketch, "E3083", {"start": v(-12.46, 16.46) * mm, "end": v(-12.54, 16.4) * mm});
            skLineSegment(sketch, "E3084", {"start": v(-12.54, 16.4) * mm, "end": v(-12.62, 16.34) * mm});
            skLineSegment(sketch, "E3085", {"start": v(-12.62, 16.34) * mm, "end": v(-12.7, 16.28) * mm});
            skLineSegment(sketch, "E3086", {"start": v(-12.7, 16.28) * mm, "end": v(-12.77, 16.22) * mm});
            skLineSegment(sketch, "E3087", {"start": v(-12.77, 16.22) * mm, "end": v(-12.85, 16.16) * mm});
            skLineSegment(sketch, "E3088", {"start": v(-12.85, 16.16) * mm, "end": v(-12.93, 16.1) * mm});
            skLineSegment(sketch, "E3089", {"start": v(-12.93, 16.1) * mm, "end": v(-13, 16.03) * mm});
            skLineSegment(sketch, "E3090", {"start": v(-13, 16.03) * mm, "end": v(-13.08, 15.97) * mm});
            skLineSegment(sketch, "E3091", {"start": v(-13.08, 15.97) * mm, "end": v(-13.16, 15.9) * mm});
            skLineSegment(sketch, "E3092", {"start": v(-13.16, 15.9) * mm, "end": v(-13.24, 15.84) * mm});
            skLineSegment(sketch, "E3093", {"start": v(-13.24, 15.84) * mm, "end": v(-13.31, 15.78) * mm});
            skLineSegment(sketch, "E3094", {"start": v(-13.31, 15.78) * mm, "end": v(-13.39, 15.71) * mm});
            skLineSegment(sketch, "E3095", {"start": v(-13.39, 15.71) * mm, "end": v(-13.47, 15.65) * mm});
            skLineSegment(sketch, "E3096", {"start": v(-13.47, 15.65) * mm, "end": v(-13.54, 15.58) * mm});
            skLineSegment(sketch, "E3097", {"start": v(-13.54, 15.58) * mm, "end": v(-13.62, 15.52) * mm});
            skLineSegment(sketch, "E3098", {"start": v(-13.62, 15.52) * mm, "end": v(-13.7, 15.45) * mm});
            skLineSegment(sketch, "E3099", {"start": v(-13.7, 15.45) * mm, "end": v(-13.77, 15.39) * mm});
            skLineSegment(sketch, "E3100", {"start": v(-13.77, 15.39) * mm, "end": v(-13.84, 15.32) * mm});
            skLineSegment(sketch, "E3101", {"start": v(-13.84, 15.32) * mm, "end": v(-13.92, 15.26) * mm});
            skLineSegment(sketch, "E3102", {"start": v(-13.92, 15.26) * mm, "end": v(-14, 15.2) * mm});
            skLineSegment(sketch, "E3103", {"start": v(-14, 15.2) * mm, "end": v(-14.07, 15.13) * mm});
            skLineSegment(sketch, "E3104", {"start": v(-14.07, 15.13) * mm, "end": v(-14.14, 15.06) * mm});
            skLineSegment(sketch, "E3105", {"start": v(-14.14, 15.06) * mm, "end": v(-14.22, 15) * mm});
            skLineSegment(sketch, "E3106", {"start": v(-14.22, 15) * mm, "end": v(-14.3, 14.92) * mm});
            skLineSegment(sketch, "E3107", {"start": v(-14.3, 14.92) * mm, "end": v(-14.37, 14.86) * mm});
            skLineSegment(sketch, "E3108", {"start": v(-14.37, 14.86) * mm, "end": v(-14.44, 14.79) * mm});
            skLineSegment(sketch, "E3109", {"start": v(-14.44, 14.79) * mm, "end": v(-14.51, 14.72) * mm});
            skLineSegment(sketch, "E3110", {"start": v(-14.51, 14.72) * mm, "end": v(-14.59, 14.65) * mm});
            skLineSegment(sketch, "E3111", {"start": v(-14.59, 14.65) * mm, "end": v(-14.66, 14.58) * mm});
            skLineSegment(sketch, "E3112", {"start": v(-14.66, 14.58) * mm, "end": v(-14.73, 14.51) * mm});
            skLineSegment(sketch, "E3113", {"start": v(-14.73, 14.51) * mm, "end": v(-14.8, 14.45) * mm});
            skLineSegment(sketch, "E3114", {"start": v(-14.8, 14.45) * mm, "end": v(-14.88, 14.38) * mm});
            skLineSegment(sketch, "E3115", {"start": v(-14.88, 14.38) * mm, "end": v(-14.95, 14.3) * mm});
            skLineSegment(sketch, "E3116", {"start": v(-14.95, 14.3) * mm, "end": v(-15.02, 14.24) * mm});
            skLineSegment(sketch, "E3117", {"start": v(-15.02, 14.24) * mm, "end": v(-15.1, 14.17) * mm});
            skLineSegment(sketch, "E3118", {"start": v(-15.1, 14.17) * mm, "end": v(-15.17, 14.1) * mm});
            skLineSegment(sketch, "E3119", {"start": v(-15.17, 14.1) * mm, "end": v(-15.24, 14.03) * mm});
            skLineSegment(sketch, "E3120", {"start": v(-15.24, 14.03) * mm, "end": v(-15.31, 13.96) * mm});
            skLineSegment(sketch, "E3121", {"start": v(-15.31, 13.96) * mm, "end": v(-15.38, 13.88) * mm});
            skLineSegment(sketch, "E3122", {"start": v(-15.38, 13.88) * mm, "end": v(-15.45, 13.81) * mm});
            skLineSegment(sketch, "E3123", {"start": v(-15.45, 13.81) * mm, "end": v(-15.52, 13.74) * mm});
            skLineSegment(sketch, "E3124", {"start": v(-15.52, 13.74) * mm, "end": v(-15.6, 13.67) * mm});
            skLineSegment(sketch, "E3125", {"start": v(-15.6, 13.67) * mm, "end": v(-15.67, 13.6) * mm});
            skLineSegment(sketch, "E3126", {"start": v(-15.67, 13.6) * mm, "end": v(-15.74, 13.53) * mm});
            skLineSegment(sketch, "E3127", {"start": v(-15.74, 13.53) * mm, "end": v(-15.8, 13.45) * mm});
            skLineSegment(sketch, "E3128", {"start": v(-15.8, 13.45) * mm, "end": v(-15.88, 13.38) * mm});
            skLineSegment(sketch, "E3129", {"start": v(-15.88, 13.38) * mm, "end": v(-15.95, 13.3) * mm});
            skLineSegment(sketch, "E3130", {"start": v(-15.95, 13.3) * mm, "end": v(-16.01, 13.23) * mm});
            skLineSegment(sketch, "E3131", {"start": v(-16.01, 13.23) * mm, "end": v(-16.08, 13.16) * mm});
            skLineSegment(sketch, "E3132", {"start": v(-16.08, 13.16) * mm, "end": v(-16.15, 13.09) * mm});
            skLineSegment(sketch, "E3133", {"start": v(-16.15, 13.09) * mm, "end": v(-16.22, 13.01) * mm});
            skLineSegment(sketch, "E3134", {"start": v(-16.22, 13.01) * mm, "end": v(-16.29, 12.94) * mm});
            skLineSegment(sketch, "E3135", {"start": v(-16.29, 12.94) * mm, "end": v(-16.36, 12.86) * mm});
            skLineSegment(sketch, "E3136", {"start": v(-16.36, 12.86) * mm, "end": v(-16.42, 12.8) * mm});
            skLineSegment(sketch, "E3137", {"start": v(-16.42, 12.8) * mm, "end": v(-16.5, 12.72) * mm});
            skLineSegment(sketch, "E3138", {"start": v(-16.5, 12.72) * mm, "end": v(-16.56, 12.64) * mm});
            skLineSegment(sketch, "E3139", {"start": v(-16.56, 12.64) * mm, "end": v(-16.63, 12.57) * mm});
            skLineSegment(sketch, "E3140", {"start": v(-16.63, 12.57) * mm, "end": v(-16.7, 12.49) * mm});
            skLineSegment(sketch, "E3141", {"start": v(-16.7, 12.49) * mm, "end": v(-16.76, 12.41) * mm});
            skLineSegment(sketch, "E3142", {"start": v(-16.76, 12.41) * mm, "end": v(-16.83, 12.34) * mm});
            skLineSegment(sketch, "E3143", {"start": v(-16.83, 12.34) * mm, "end": v(-16.9, 12.26) * mm});
            skLineSegment(sketch, "E3144", {"start": v(-16.9, 12.26) * mm, "end": v(-16.96, 12.19) * mm});
            skLineSegment(sketch, "E3145", {"start": v(-16.96, 12.19) * mm, "end": v(-17.02, 12.1) * mm});
            skLineSegment(sketch, "E3146", {"start": v(-17.02, 12.1) * mm, "end": v(-17.09, 12.03) * mm});
            skLineSegment(sketch, "E3147", {"start": v(-17.09, 12.03) * mm, "end": v(-17.15, 11.96) * mm});
            skLineSegment(sketch, "E3148", {"start": v(-17.15, 11.96) * mm, "end": v(-17.22, 11.88) * mm});
            skLineSegment(sketch, "E3149", {"start": v(-17.22, 11.88) * mm, "end": v(-17.28, 11.8) * mm});
            skLineSegment(sketch, "E3150", {"start": v(-17.28, 11.8) * mm, "end": v(-17.35, 11.72) * mm});
            skLineSegment(sketch, "E3151", {"start": v(-17.35, 11.72) * mm, "end": v(-17.4, 11.65) * mm});
            skLineSegment(sketch, "E3152", {"start": v(-17.4, 11.65) * mm, "end": v(-17.47, 11.57) * mm});
            skLineSegment(sketch, "E3153", {"start": v(-17.47, 11.57) * mm, "end": v(-17.54, 11.49) * mm});
            skLineSegment(sketch, "E3154", {"start": v(-17.54, 11.49) * mm, "end": v(-17.6, 11.41) * mm});
            skLineSegment(sketch, "E3155", {"start": v(-17.6, 11.41) * mm, "end": v(-17.66, 11.33) * mm});
            skLineSegment(sketch, "E3156", {"start": v(-17.66, 11.33) * mm, "end": v(-17.72, 11.25) * mm});
            skLineSegment(sketch, "E3157", {"start": v(-17.72, 11.25) * mm, "end": v(-17.79, 11.17) * mm});
            skLineSegment(sketch, "E3158", {"start": v(-17.79, 11.17) * mm, "end": v(-17.85, 11.1) * mm});
            skLineSegment(sketch, "E3159", {"start": v(-17.85, 11.1) * mm, "end": v(-17.9, 11.02) * mm});
            skLineSegment(sketch, "E3160", {"start": v(-17.9, 11.02) * mm, "end": v(-17.97, 10.94) * mm});
            skLineSegment(sketch, "E3161", {"start": v(-17.97, 10.94) * mm, "end": v(-18.03, 10.86) * mm});
            skLineSegment(sketch, "E3162", {"start": v(-18.03, 10.86) * mm, "end": v(-18.1, 10.78) * mm});
            skLineSegment(sketch, "E3163", {"start": v(-18.1, 10.78) * mm, "end": v(-18.15, 10.7) * mm});
            skLineSegment(sketch, "E3164", {"start": v(-18.15, 10.7) * mm, "end": v(-18.21, 10.61) * mm});
            skLineSegment(sketch, "E3165", {"start": v(-18.21, 10.61) * mm, "end": v(-18.27, 10.53) * mm});
            skLineSegment(sketch, "E3166", {"start": v(-18.27, 10.53) * mm, "end": v(-18.33, 10.45) * mm});
            skLineSegment(sketch, "E3167", {"start": v(-18.33, 10.45) * mm, "end": v(-18.39, 10.37) * mm});
            skLineSegment(sketch, "E3168", {"start": v(-18.39, 10.37) * mm, "end": v(-18.45, 10.3) * mm});
            skLineSegment(sketch, "E3169", {"start": v(-18.45, 10.3) * mm, "end": v(-18.5, 10.2) * mm});
            skLineSegment(sketch, "E3170", {"start": v(-18.5, 10.2) * mm, "end": v(-18.56, 10.13) * mm});
            skLineSegment(sketch, "E3171", {"start": v(-18.56, 10.13) * mm, "end": v(-18.62, 10.05) * mm});
            skLineSegment(sketch, "E3172", {"start": v(-18.62, 10.05) * mm, "end": v(-18.68, 9.96) * mm});
            skLineSegment(sketch, "E3173", {"start": v(-18.68, 9.96) * mm, "end": v(-18.73, 9.88) * mm});
            skLineSegment(sketch, "E3174", {"start": v(-18.73, 9.88) * mm, "end": v(-18.8, 9.8) * mm});
            skLineSegment(sketch, "E3175", {"start": v(-18.8, 9.8) * mm, "end": v(-18.85, 9.72) * mm});
            skLineSegment(sketch, "E3176", {"start": v(-18.85, 9.72) * mm, "end": v(-18.9, 9.63) * mm});
            skLineSegment(sketch, "E3177", {"start": v(-18.9, 9.63) * mm, "end": v(-18.96, 9.55) * mm});
            skLineSegment(sketch, "E3178", {"start": v(-18.96, 9.55) * mm, "end": v(-19.01, 9.47) * mm});
            skLineSegment(sketch, "E3179", {"start": v(-19.01, 9.47) * mm, "end": v(-19.07, 9.38) * mm});
            skLineSegment(sketch, "E3180", {"start": v(-19.07, 9.38) * mm, "end": v(-19.12, 9.3) * mm});
            skLineSegment(sketch, "E3181", {"start": v(-19.12, 9.3) * mm, "end": v(-19.18, 9.22) * mm});
            skLineSegment(sketch, "E3182", {"start": v(-19.18, 9.22) * mm, "end": v(-19.23, 9.13) * mm});
            skLineSegment(sketch, "E3183", {"start": v(-19.23, 9.13) * mm, "end": v(-19.28, 9.05) * mm});
            skLineSegment(sketch, "E3184", {"start": v(-19.28, 9.05) * mm, "end": v(-19.34, 8.97) * mm});
            skLineSegment(sketch, "E3185", {"start": v(-19.34, 8.97) * mm, "end": v(-19.39, 8.88) * mm});
            skLineSegment(sketch, "E3186", {"start": v(-19.39, 8.88) * mm, "end": v(-19.44, 8.8) * mm});
            skLineSegment(sketch, "E3187", {"start": v(-19.44, 8.8) * mm, "end": v(-19.5, 8.71) * mm});
            skLineSegment(sketch, "E3188", {"start": v(-19.5, 8.71) * mm, "end": v(-19.55, 8.63) * mm});
            skLineSegment(sketch, "E3189", {"start": v(-19.55, 8.63) * mm, "end": v(-19.6, 8.54) * mm});
            skLineSegment(sketch, "E3190", {"start": v(-19.6, 8.54) * mm, "end": v(-19.65, 8.46) * mm});
            skLineSegment(sketch, "E3191", {"start": v(-19.65, 8.46) * mm, "end": v(-19.7, 8.37) * mm});
            skLineSegment(sketch, "E3192", {"start": v(-19.7, 8.37) * mm, "end": v(-19.75, 8.29) * mm});
            skLineSegment(sketch, "E3193", {"start": v(-19.75, 8.29) * mm, "end": v(-19.8, 8.2) * mm});
            skLineSegment(sketch, "E3194", {"start": v(-19.8, 8.2) * mm, "end": v(-19.85, 8.11) * mm});
            skLineSegment(sketch, "E3195", {"start": v(-19.85, 8.11) * mm, "end": v(-19.9, 8.03) * mm});
            skLineSegment(sketch, "E3196", {"start": v(-19.9, 8.03) * mm, "end": v(-19.95, 7.94) * mm});
            skLineSegment(sketch, "E3197", {"start": v(-19.95, 7.94) * mm, "end": v(-20, 7.86) * mm});
            skLineSegment(sketch, "E3198", {"start": v(-20, 7.86) * mm, "end": v(-20.04, 7.77) * mm});
            skLineSegment(sketch, "E3199", {"start": v(-20.04, 7.77) * mm, "end": v(-20.09, 7.68) * mm});
            skLineSegment(sketch, "E3200", {"start": v(-20.09, 7.68) * mm, "end": v(-20.14, 7.6) * mm});
            skLineSegment(sketch, "E3201", {"start": v(-20.14, 7.6) * mm, "end": v(-20.18, 7.5) * mm});
            skLineSegment(sketch, "E3202", {"start": v(-20.18, 7.5) * mm, "end": v(-20.23, 7.42) * mm});
            skLineSegment(sketch, "E3203", {"start": v(-20.23, 7.42) * mm, "end": v(-20.27, 7.33) * mm});
            skLineSegment(sketch, "E3204", {"start": v(-20.27, 7.33) * mm, "end": v(-20.32, 7.25) * mm});
            skLineSegment(sketch, "E3205", {"start": v(-20.32, 7.25) * mm, "end": v(-20.36, 7.16) * mm});
            skLineSegment(sketch, "E3206", {"start": v(-20.36, 7.16) * mm, "end": v(-20.4, 7.07) * mm});
            skLineSegment(sketch, "E3207", {"start": v(-20.4, 7.07) * mm, "end": v(-20.45, 6.98) * mm});
            skLineSegment(sketch, "E3208", {"start": v(-20.45, 6.98) * mm, "end": v(-20.5, 6.9) * mm});
            skLineSegment(sketch, "E3209", {"start": v(-20.5, 6.9) * mm, "end": v(-20.54, 6.8) * mm});
            skLineSegment(sketch, "E3210", {"start": v(-20.54, 6.8) * mm, "end": v(-20.58, 6.72) * mm});
            skLineSegment(sketch, "E3211", {"start": v(-20.58, 6.72) * mm, "end": v(-20.63, 6.63) * mm});
            skLineSegment(sketch, "E3212", {"start": v(-20.63, 6.63) * mm, "end": v(-20.67, 6.54) * mm});
            skLineSegment(sketch, "E3213", {"start": v(-20.67, 6.54) * mm, "end": v(-20.71, 6.45) * mm});
            skLineSegment(sketch, "E3214", {"start": v(-20.71, 6.45) * mm, "end": v(-20.75, 6.36) * mm});
            skLineSegment(sketch, "E3215", {"start": v(-20.75, 6.36) * mm, "end": v(-20.8, 6.28) * mm});
            skLineSegment(sketch, "E3216", {"start": v(-20.8, 6.28) * mm, "end": v(-20.83, 6.19) * mm});
            skLineSegment(sketch, "E3217", {"start": v(-20.83, 6.19) * mm, "end": v(-20.87, 6.1) * mm});
            skLineSegment(sketch, "E3218", {"start": v(-20.87, 6.1) * mm, "end": v(-20.91, 6) * mm});
            skLineSegment(sketch, "E3219", {"start": v(-20.91, 6) * mm, "end": v(-20.95, 5.92) * mm});
            skLineSegment(sketch, "E3220", {"start": v(-20.95, 5.92) * mm, "end": v(-21, 5.83) * mm});
            skLineSegment(sketch, "E3221", {"start": v(-21, 5.83) * mm, "end": v(-21.03, 5.74) * mm});
            skLineSegment(sketch, "E3222", {"start": v(-21.03, 5.74) * mm, "end": v(-21.07, 5.65) * mm});
            skLineSegment(sketch, "E3223", {"start": v(-21.07, 5.65) * mm, "end": v(-21.1, 5.56) * mm});
            skLineSegment(sketch, "E3224", {"start": v(-21.1, 5.56) * mm, "end": v(-21.14, 5.47) * mm});
            skLineSegment(sketch, "E3225", {"start": v(-21.14, 5.47) * mm, "end": v(-21.18, 5.38) * mm});
            skLineSegment(sketch, "E3226", {"start": v(-21.18, 5.38) * mm, "end": v(-21.21, 5.29) * mm});
            skLineSegment(sketch, "E3227", {"start": v(-21.21, 5.29) * mm, "end": v(-21.25, 5.2) * mm});
            skLineSegment(sketch, "E3228", {"start": v(-21.25, 5.2) * mm, "end": v(-21.28, 5.1) * mm});
            skLineSegment(sketch, "E3229", {"start": v(-21.28, 5.1) * mm, "end": v(-21.32, 5.01) * mm});
            skLineSegment(sketch, "E3230", {"start": v(-21.32, 5.01) * mm, "end": v(-21.35, 4.92) * mm});
            skLineSegment(sketch, "E3231", {"start": v(-21.35, 4.92) * mm, "end": v(-21.39, 4.83) * mm});
            skLineSegment(sketch, "E3232", {"start": v(-21.39, 4.83) * mm, "end": v(-21.42, 4.74) * mm});
            skLineSegment(sketch, "E3233", {"start": v(-21.42, 4.74) * mm, "end": v(-21.45, 4.65) * mm});
            skLineSegment(sketch, "E3234", {"start": v(-21.45, 4.65) * mm, "end": v(-21.48, 4.56) * mm});
            skLineSegment(sketch, "E3235", {"start": v(-21.48, 4.56) * mm, "end": v(-21.52, 4.47) * mm});
            skLineSegment(sketch, "E3236", {"start": v(-21.52, 4.47) * mm, "end": v(-21.55, 4.37) * mm});
            skLineSegment(sketch, "E3237", {"start": v(-21.55, 4.37) * mm, "end": v(-21.58, 4.28) * mm});
            skLineSegment(sketch, "E3238", {"start": v(-21.58, 4.28) * mm, "end": v(-21.6, 4.2) * mm});
            skLineSegment(sketch, "E3239", {"start": v(-21.6, 4.2) * mm, "end": v(-21.64, 4.1) * mm});
            skLineSegment(sketch, "E3240", {"start": v(-21.64, 4.1) * mm, "end": v(-21.67, 4) * mm});
            skLineSegment(sketch, "E3241", {"start": v(-21.67, 4) * mm, "end": v(-21.7, 3.91) * mm});
            skLineSegment(sketch, "E3242", {"start": v(-21.7, 3.91) * mm, "end": v(-21.73, 3.82) * mm});
            skLineSegment(sketch, "E3243", {"start": v(-21.73, 3.82) * mm, "end": v(-21.75, 3.73) * mm});
            skLineSegment(sketch, "E3244", {"start": v(-21.75, 3.73) * mm, "end": v(-21.78, 3.64) * mm});
            skLineSegment(sketch, "E3245", {"start": v(-21.78, 3.64) * mm, "end": v(-21.8, 3.54) * mm});
            skLineSegment(sketch, "E3246", {"start": v(-21.8, 3.54) * mm, "end": v(-21.83, 3.45) * mm});
            skLineSegment(sketch, "E3247", {"start": v(-21.83, 3.45) * mm, "end": v(-21.86, 3.36) * mm});
            skLineSegment(sketch, "E3248", {"start": v(-21.86, 3.36) * mm, "end": v(-21.89, 3.27) * mm});
            skLineSegment(sketch, "E3249", {"start": v(-21.89, 3.27) * mm, "end": v(-21.91, 3.17) * mm});
            skLineSegment(sketch, "E3250", {"start": v(-21.91, 3.17) * mm, "end": v(-21.94, 3.08) * mm});
            skLineSegment(sketch, "E3251", {"start": v(-21.94, 3.08) * mm, "end": v(-21.96, 2.99) * mm});
            skLineSegment(sketch, "E3252", {"start": v(-21.96, 2.99) * mm, "end": v(-21.98, 2.9) * mm});
            skLineSegment(sketch, "E3253", {"start": v(-21.98, 2.9) * mm, "end": v(-22, 2.8) * mm});
            skLineSegment(sketch, "E3254", {"start": v(-22, 2.8) * mm, "end": v(-22.03, 2.7) * mm});
            skLineSegment(sketch, "E3255", {"start": v(-22.03, 2.7) * mm, "end": v(-22.05, 2.61) * mm});
            skLineSegment(sketch, "E3256", {"start": v(-22.05, 2.61) * mm, "end": v(-22.07, 2.52) * mm});
            skLineSegment(sketch, "E3257", {"start": v(-22.07, 2.52) * mm, "end": v(-22.1, 2.42) * mm});
            skLineSegment(sketch, "E3258", {"start": v(-22.1, 2.42) * mm, "end": v(-22.11, 2.33) * mm});
            skLineSegment(sketch, "E3259", {"start": v(-22.11, 2.33) * mm, "end": v(-22.13, 2.23) * mm});
            skLineSegment(sketch, "E3260", {"start": v(-22.13, 2.23) * mm, "end": v(-22.15, 2.14) * mm});
            skLineSegment(sketch, "E3261", {"start": v(-22.15, 2.14) * mm, "end": v(-22.17, 2.05) * mm});
            skLineSegment(sketch, "E3262", {"start": v(-22.17, 2.05) * mm, "end": v(-22.19, 1.95) * mm});
            skLineSegment(sketch, "E3263", {"start": v(-22.19, 1.95) * mm, "end": v(-22.2, 1.86) * mm});
            skLineSegment(sketch, "E3264", {"start": v(-22.2, 1.86) * mm, "end": v(-22.22, 1.76) * mm});
            skLineSegment(sketch, "E3265", {"start": v(-22.22, 1.76) * mm, "end": v(-22.24, 1.67) * mm});
            skLineSegment(sketch, "E3266", {"start": v(-22.24, 1.67) * mm, "end": v(-22.26, 1.57) * mm});
            skLineSegment(sketch, "E3267", {"start": v(-22.26, 1.57) * mm, "end": v(-22.27, 1.48) * mm});
            skLineSegment(sketch, "E3268", {"start": v(-22.27, 1.48) * mm, "end": v(-22.29, 1.38) * mm});
            skLineSegment(sketch, "E3269", {"start": v(-22.29, 1.38) * mm, "end": v(-22.3, 1.29) * mm});
            skLineSegment(sketch, "E3270", {"start": v(-22.3, 1.29) * mm, "end": v(-22.32, 1.2) * mm});
            skLineSegment(sketch, "E3271", {"start": v(-22.32, 1.2) * mm, "end": v(-22.33, 1.1) * mm});
            skLineSegment(sketch, "E3272", {"start": v(-22.33, 1.1) * mm, "end": v(-22.34, 1) * mm});
            skLineSegment(sketch, "E3273", {"start": v(-22.34, 1) * mm, "end": v(-22.35, 0.9) * mm});
            skLineSegment(sketch, "E3274", {"start": v(-22.35, 0.9) * mm, "end": v(-22.37, 0.81) * mm});
            skLineSegment(sketch, "E3275", {"start": v(-22.37, 0.81) * mm, "end": v(-22.38, 0.72) * mm});
            skLineSegment(sketch, "E3276", {"start": v(-22.38, 0.72) * mm, "end": v(-22.39, 0.62) * mm});
            skLineSegment(sketch, "E3277", {"start": v(-22.39, 0.62) * mm, "end": v(-22.4, 0.53) * mm});
            skLineSegment(sketch, "E3278", {"start": v(-22.4, 0.53) * mm, "end": v(-22.4, 0.43) * mm});
            skLineSegment(sketch, "E3279", {"start": v(-22.4, 0.43) * mm, "end": v(-22.41, 0.34) * mm});
            skLineSegment(sketch, "E3280", {"start": v(-22.41, 0.34) * mm, "end": v(-22.42, 0.24) * mm});
            skLineSegment(sketch, "E3281", {"start": v(-22.42, 0.24) * mm, "end": v(-22.42, 0.15) * mm});
            skLineSegment(sketch, "E3282", {"start": v(-22.42, 0.15) * mm, "end": v(-22.43, 0.06) * mm});
            skLineSegment(sketch, "E3283", {"start": v(-22.43, 0.06) * mm, "end": v(-22.43, -0.04) * mm});
            skLineSegment(sketch, "E3284", {"start": v(-22.43, -0.04) * mm, "end": v(-22.44, -0.13) * mm});
            skLineSegment(sketch, "E3285", {"start": v(-22.44, -0.13) * mm, "end": v(-22.44, -0.23) * mm});
            skLineSegment(sketch, "E3286", {"start": v(-22.44, -0.23) * mm, "end": v(-22.44, -0.32) * mm});
            skLineSegment(sketch, "E3287", {"start": v(-22.44, -0.32) * mm, "end": v(-22.44, -0.41) * mm});
            skLineSegment(sketch, "E3288", {"start": v(-22.44, -0.41) * mm, "end": v(-22.44, -0.5) * mm});
            skLineSegment(sketch, "E3289", {"start": v(-22.44, -0.5) * mm, "end": v(-22.44, -0.6) * mm});
            skLineSegment(sketch, "E3290", {"start": v(-22.44, -0.6) * mm, "end": v(-22.44, -0.7) * mm});
            skLineSegment(sketch, "E3291", {"start": v(-22.44, -0.7) * mm, "end": v(-22.44, -0.78) * mm});
            skLineSegment(sketch, "E3292", {"start": v(-22.44, -0.78) * mm, "end": v(-22.44, -0.88) * mm});
            skLineSegment(sketch, "E3293", {"start": v(-22.44, -0.88) * mm, "end": v(-22.43, -0.97) * mm});
            skLineSegment(sketch, "E3294", {"start": v(-22.43, -0.97) * mm, "end": v(-22.43, -1.06) * mm});
            skLineSegment(sketch, "E3295", {"start": v(-22.43, -1.06) * mm, "end": v(-22.42, -1.15) * mm});
            skLineSegment(sketch, "E3296", {"start": v(-22.42, -1.15) * mm, "end": v(-22.42, -1.24) * mm});
            skLineSegment(sketch, "E3297", {"start": v(-22.42, -1.24) * mm, "end": v(-22.41, -1.33) * mm});
            skLineSegment(sketch, "E3298", {"start": v(-22.41, -1.33) * mm, "end": v(-22.4, -1.42) * mm});
            skLineSegment(sketch, "E3299", {"start": v(-22.4, -1.42) * mm, "end": v(-22.4, -1.51) * mm});
            skLineSegment(sketch, "E3300", {"start": v(-22.4, -1.51) * mm, "end": v(-22.39, -1.6) * mm});
            skLineSegment(sketch, "E3301", {"start": v(-22.39, -1.6) * mm, "end": v(-22.38, -1.7) * mm});
            skLineSegment(sketch, "E3302", {"start": v(-22.38, -1.7) * mm, "end": v(-22.37, -1.78) * mm});
            skLineSegment(sketch, "E3303", {"start": v(-22.37, -1.78) * mm, "end": v(-22.36, -1.87) * mm});
            skLineSegment(sketch, "E3304", {"start": v(-22.36, -1.87) * mm, "end": v(-22.34, -1.96) * mm});
            skLineSegment(sketch, "E3305", {"start": v(-22.34, -1.96) * mm, "end": v(-22.33, -2.05) * mm});
            skLineSegment(sketch, "E3306", {"start": v(-22.33, -2.05) * mm, "end": v(-22.32, -2.14) * mm});
            skLineSegment(sketch, "E3307", {"start": v(-22.32, -2.14) * mm, "end": v(-22.3, -2.23) * mm});
            skLineSegment(sketch, "E3308", {"start": v(-22.3, -2.23) * mm, "end": v(-22.29, -2.32) * mm});
            skLineSegment(sketch, "E3309", {"start": v(-22.29, -2.32) * mm, "end": v(-22.27, -2.4) * mm});
            skLineSegment(sketch, "E3310", {"start": v(-22.27, -2.4) * mm, "end": v(-22.26, -2.5) * mm});
            skLineSegment(sketch, "E3311", {"start": v(-22.26, -2.5) * mm, "end": v(-22.24, -2.58) * mm});
            skLineSegment(sketch, "E3312", {"start": v(-22.24, -2.58) * mm, "end": v(-22.22, -2.67) * mm});
            skLineSegment(sketch, "E3313", {"start": v(-22.22, -2.67) * mm, "end": v(-22.2, -2.75) * mm});
            skLineSegment(sketch, "E3314", {"start": v(-22.2, -2.75) * mm, "end": v(-22.18, -2.84) * mm});
            skLineSegment(sketch, "E3315", {"start": v(-22.18, -2.84) * mm, "end": v(-22.16, -2.92) * mm});
            skLineSegment(sketch, "E3316", {"start": v(-22.16, -2.92) * mm, "end": v(-22.14, -3) * mm});
            skLineSegment(sketch, "E3317", {"start": v(-22.14, -3) * mm, "end": v(-22.12, -3.1) * mm});
            skLineSegment(sketch, "E3318", {"start": v(-22.12, -3.1) * mm, "end": v(-22.1, -3.18) * mm});
            skLineSegment(sketch, "E3319", {"start": v(-22.1, -3.18) * mm, "end": v(-22.08, -3.26) * mm});
            skLineSegment(sketch, "E3320", {"start": v(-22.08, -3.26) * mm, "end": v(-22.05, -3.35) * mm});
            skLineSegment(sketch, "E3321", {"start": v(-22.05, -3.35) * mm, "end": v(-22.03, -3.43) * mm});
            skLineSegment(sketch, "E3322", {"start": v(-22.03, -3.43) * mm, "end": v(-22, -3.51) * mm});
            skLineSegment(sketch, "E3323", {"start": v(-22, -3.51) * mm, "end": v(-21.98, -3.6) * mm});
            skLineSegment(sketch, "E3324", {"start": v(-21.98, -3.6) * mm, "end": v(-21.95, -3.68) * mm});
            skLineSegment(sketch, "E3325", {"start": v(-21.95, -3.68) * mm, "end": v(-21.92, -3.76) * mm});
            skLineSegment(sketch, "E3326", {"start": v(-21.92, -3.76) * mm, "end": v(-21.9, -3.84) * mm});
            skLineSegment(sketch, "E3327", {"start": v(-21.9, -3.84) * mm, "end": v(-21.87, -3.92) * mm});
            skLineSegment(sketch, "E3328", {"start": v(-21.87, -3.92) * mm, "end": v(-21.84, -4) * mm});
            skLineSegment(sketch, "E3329", {"start": v(-21.84, -4) * mm, "end": v(-21.8, -4.08) * mm});
            skLineSegment(sketch, "E3330", {"start": v(-21.8, -4.08) * mm, "end": v(-21.78, -4.16) * mm});
            skLineSegment(sketch, "E3331", {"start": v(-21.78, -4.16) * mm, "end": v(-21.74, -4.24) * mm});
            skLineSegment(sketch, "E3332", {"start": v(-21.74, -4.24) * mm, "end": v(-21.71, -4.32) * mm});
            skLineSegment(sketch, "E3333", {"start": v(-21.71, -4.32) * mm, "end": v(-21.68, -4.4) * mm});
            skLineSegment(sketch, "E3334", {"start": v(-21.68, -4.4) * mm, "end": v(-21.64, -4.47) * mm});
            skLineSegment(sketch, "E3335", {"start": v(-21.64, -4.47) * mm, "end": v(-21.6, -4.55) * mm});
            skLineSegment(sketch, "E3336", {"start": v(-21.6, -4.55) * mm, "end": v(-21.57, -4.63) * mm});
            skLineSegment(sketch, "E3337", {"start": v(-21.57, -4.63) * mm, "end": v(-21.54, -4.7) * mm});
            skLineSegment(sketch, "E3338", {"start": v(-21.54, -4.7) * mm, "end": v(-21.5, -4.78) * mm});
            skLineSegment(sketch, "E3339", {"start": v(-21.5, -4.78) * mm, "end": v(-21.47, -4.86) * mm});
            skLineSegment(sketch, "E3340", {"start": v(-21.47, -4.86) * mm, "end": v(-21.43, -4.93) * mm});
            skLineSegment(sketch, "E3341", {"start": v(-21.43, -4.93) * mm, "end": v(-21.39, -5) * mm});
            skLineSegment(sketch, "E3342", {"start": v(-21.39, -5) * mm, "end": v(-21.35, -5.08) * mm});
            skLineSegment(sketch, "E3343", {"start": v(-21.35, -5.08) * mm, "end": v(-21.3, -5.15) * mm});
            skLineSegment(sketch, "E3344", {"start": v(-21.3, -5.15) * mm, "end": v(-21.27, -5.22) * mm});
            skLineSegment(sketch, "E3345", {"start": v(-21.27, -5.22) * mm, "end": v(-21.23, -5.3) * mm});
            skLineSegment(sketch, "E3346", {"start": v(-21.23, -5.3) * mm, "end": v(-21.19, -5.37) * mm});
            skLineSegment(sketch, "E3347", {"start": v(-21.19, -5.37) * mm, "end": v(-21.14, -5.44) * mm});
            skLineSegment(sketch, "E3348", {"start": v(-21.14, -5.44) * mm, "end": v(-21.1, -5.5) * mm});
            skLineSegment(sketch, "E3349", {"start": v(-21.1, -5.5) * mm, "end": v(-21.05, -5.58) * mm});
            skLineSegment(sketch, "E3350", {"start": v(-21.05, -5.58) * mm, "end": v(-21.01, -5.65) * mm});
            skLineSegment(sketch, "E3351", {"start": v(-21.01, -5.65) * mm, "end": v(-20.96, -5.72) * mm});
            skLineSegment(sketch, "E3352", {"start": v(-20.96, -5.72) * mm, "end": v(-20.92, -5.79) * mm});
            skLineSegment(sketch, "E3353", {"start": v(-20.92, -5.79) * mm, "end": v(-20.87, -5.85) * mm});
            skLineSegment(sketch, "E3354", {"start": v(-20.87, -5.85) * mm, "end": v(-20.82, -5.92) * mm});
            skLineSegment(sketch, "E3355", {"start": v(-20.82, -5.92) * mm, "end": v(-20.78, -5.99) * mm});
            skLineSegment(sketch, "E3356", {"start": v(-20.78, -5.99) * mm, "end": v(-20.73, -6.05) * mm});
            skLineSegment(sketch, "E3357", {"start": v(-20.73, -6.05) * mm, "end": v(-20.68, -6.12) * mm});
            skLineSegment(sketch, "E3358", {"start": v(-20.68, -6.12) * mm, "end": v(-20.63, -6.18) * mm});
            skLineSegment(sketch, "E3359", {"start": v(-20.63, -6.18) * mm, "end": v(-20.58, -6.25) * mm});
            skLineSegment(sketch, "E3360", {"start": v(-20.58, -6.25) * mm, "end": v(-20.53, -6.31) * mm});
            skLineSegment(sketch, "E3361", {"start": v(-20.53, -6.31) * mm, "end": v(-20.47, -6.37) * mm});
            skLineSegment(sketch, "E3362", {"start": v(-20.47, -6.37) * mm, "end": v(-20.42, -6.44) * mm});
            skLineSegment(sketch, "E3363", {"start": v(-20.42, -6.44) * mm, "end": v(-20.37, -6.5) * mm});
            skLineSegment(sketch, "E3364", {"start": v(-20.37, -6.5) * mm, "end": v(-20.31, -6.56) * mm});
            skLineSegment(sketch, "E3365", {"start": v(-20.31, -6.56) * mm, "end": v(-20.26, -6.62) * mm});
            skLineSegment(sketch, "E3366", {"start": v(-20.26, -6.62) * mm, "end": v(-20.2, -6.68) * mm});
            skLineSegment(sketch, "E3367", {"start": v(-20.2, -6.68) * mm, "end": v(-20.15, -6.74) * mm});
            skLineSegment(sketch, "E3368", {"start": v(-20.15, -6.74) * mm, "end": v(-20.1, -6.8) * mm});
            skLineSegment(sketch, "E3369", {"start": v(-20.1, -6.8) * mm, "end": v(-20.03, -6.85) * mm});
            skLineSegment(sketch, "E3370", {"start": v(-20.03, -6.85) * mm, "end": v(-19.98, -6.9) * mm});
            skLineSegment(sketch, "E3371", {"start": v(-19.98, -6.9) * mm, "end": v(-19.92, -6.96) * mm});
            skLineSegment(sketch, "E3372", {"start": v(-19.92, -6.96) * mm, "end": v(-19.86, -7.02) * mm});
            skLineSegment(sketch, "E3373", {"start": v(-19.86, -7.02) * mm, "end": v(-19.8, -7.07) * mm});
            skLineSegment(sketch, "E3374", {"start": v(-19.8, -7.07) * mm, "end": v(-19.74, -7.13) * mm});
            skLineSegment(sketch, "E3375", {"start": v(-19.74, -7.13) * mm, "end": v(-19.68, -7.18) * mm});
            skLineSegment(sketch, "E3376", {"start": v(-19.68, -7.18) * mm, "end": v(-19.61, -7.23) * mm});
            skLineSegment(sketch, "E3377", {"start": v(-19.61, -7.23) * mm, "end": v(-19.55, -7.29) * mm});
            skLineSegment(sketch, "E3378", {"start": v(-19.55, -7.29) * mm, "end": v(-19.49, -7.34) * mm});
            skLineSegment(sketch, "E3379", {"start": v(-19.49, -7.34) * mm, "end": v(-19.43, -7.39) * mm});
            skLineSegment(sketch, "E3380", {"start": v(-19.43, -7.39) * mm, "end": v(-19.36, -7.44) * mm});
            skLineSegment(sketch, "E3381", {"start": v(-19.36, -7.44) * mm, "end": v(-19.3, -7.49) * mm});
            skLineSegment(sketch, "E3382", {"start": v(-19.3, -7.49) * mm, "end": v(-19.23, -7.53) * mm});
            skLineSegment(sketch, "E3383", {"start": v(-19.23, -7.53) * mm, "end": v(-19.17, -7.58) * mm});
            skLineSegment(sketch, "E3384", {"start": v(-19.17, -7.58) * mm, "end": v(-19.1, -7.63) * mm});
            skLineSegment(sketch, "E3385", {"start": v(-19.1, -7.63) * mm, "end": v(-19.03, -7.67) * mm});
            skLineSegment(sketch, "E3386", {"start": v(-19.03, -7.67) * mm, "end": v(-18.96, -7.72) * mm});
            skLineSegment(sketch, "E3387", {"start": v(-18.96, -7.72) * mm, "end": v(-18.9, -7.76) * mm});
            skLineSegment(sketch, "E3388", {"start": v(-18.9, -7.76) * mm, "end": v(-18.83, -7.8) * mm});
            skLineSegment(sketch, "E3389", {"start": v(-18.83, -7.8) * mm, "end": v(-18.76, -7.85) * mm});
            skLineSegment(sketch, "E3390", {"start": v(-18.76, -7.85) * mm, "end": v(-18.69, -7.9) * mm});
            skLineSegment(sketch, "E3391", {"start": v(-18.69, -7.9) * mm, "end": v(-18.62, -7.93) * mm});
            skLineSegment(sketch, "E3392", {"start": v(-18.62, -7.93) * mm, "end": v(-18.54, -7.97) * mm});
            skLineSegment(sketch, "E3393", {"start": v(-18.54, -7.97) * mm, "end": v(-18.47, -8.01) * mm});
            skLineSegment(sketch, "E3394", {"start": v(-18.47, -8.01) * mm, "end": v(-18.4, -8.05) * mm});
            skLineSegment(sketch, "E3395", {"start": v(-18.4, -8.05) * mm, "end": v(-18.33, -8.09) * mm});
            skLineSegment(sketch, "E3396", {"start": v(-18.33, -8.09) * mm, "end": v(-18.25, -8.12) * mm});
            skLineSegment(sketch, "E3397", {"start": v(-18.25, -8.12) * mm, "end": v(-18.18, -8.16) * mm});
            skLineSegment(sketch, "E3398", {"start": v(-18.18, -8.16) * mm, "end": v(-18.1, -8.2) * mm});
            skLineSegment(sketch, "E3399", {"start": v(-18.1, -8.2) * mm, "end": v(-18.03, -8.23) * mm});
            skLineSegment(sketch, "E3400", {"start": v(-18.03, -8.23) * mm, "end": v(-17.95, -8.26) * mm});
            skLineSegment(sketch, "E3401", {"start": v(-17.95, -8.26) * mm, "end": v(-17.87, -8.3) * mm});
            skLineSegment(sketch, "E3402", {"start": v(-17.87, -8.3) * mm, "end": v(-17.8, -8.33) * mm});
            skLineSegment(sketch, "E3403", {"start": v(-17.8, -8.33) * mm, "end": v(-17.72, -8.36) * mm});
            skLineSegment(sketch, "E3404", {"start": v(-17.72, -8.36) * mm, "end": v(-17.64, -8.39) * mm});
            skLineSegment(sketch, "E3405", {"start": v(-17.64, -8.39) * mm, "end": v(-17.56, -8.42) * mm});
            skLineSegment(sketch, "E3406", {"start": v(-17.56, -8.42) * mm, "end": v(-17.48, -8.44) * mm});
            skLineSegment(sketch, "E3407", {"start": v(-17.48, -8.44) * mm, "end": v(-17.4, -8.47) * mm});
            skLineSegment(sketch, "E3408", {"start": v(-17.4, -8.47) * mm, "end": v(-17.32, -8.5) * mm});
            skLineSegment(sketch, "E3409", {"start": v(-17.32, -8.5) * mm, "end": v(-17.24, -8.52) * mm});
            skLineSegment(sketch, "E3410", {"start": v(-17.24, -8.52) * mm, "end": v(-17.16, -8.55) * mm});
            skLineSegment(sketch, "E3411", {"start": v(-17.16, -8.55) * mm, "end": v(-17.07, -8.57) * mm});
            skLineSegment(sketch, "E3412", {"start": v(-17.07, -8.57) * mm, "end": v(-16.99, -8.6) * mm});
            skLineSegment(sketch, "E3413", {"start": v(-16.99, -8.6) * mm, "end": v(-16.9, -8.61) * mm});
            skLineSegment(sketch, "E3414", {"start": v(-16.9, -8.61) * mm, "end": v(-16.82, -8.63) * mm});
            skLineSegment(sketch, "E3415", {"start": v(-16.82, -8.63) * mm, "end": v(-16.74, -8.65) * mm});
            skLineSegment(sketch, "E3416", {"start": v(-16.74, -8.65) * mm, "end": v(-16.65, -8.67) * mm});
            skLineSegment(sketch, "E3417", {"start": v(-16.65, -8.67) * mm, "end": v(-16.57, -8.69) * mm});
            skLineSegment(sketch, "E3418", {"start": v(-16.57, -8.69) * mm, "end": v(-16.48, -8.7) * mm});
            skLineSegment(sketch, "E3419", {"start": v(-16.48, -8.7) * mm, "end": v(-16.4, -8.72) * mm});
            skLineSegment(sketch, "E3420", {"start": v(-16.4, -8.72) * mm, "end": v(-16.3, -8.74) * mm});
            skLineSegment(sketch, "E3421", {"start": v(-16.3, -8.74) * mm, "end": v(-16.22, -8.75) * mm});
            skLineSegment(sketch, "E3422", {"start": v(-16.22, -8.75) * mm, "end": v(-16.13, -8.76) * mm});
            skLineSegment(sketch, "E3423", {"start": v(-16.13, -8.76) * mm, "end": v(-16.04, -8.77) * mm});
            skLineSegment(sketch, "E3424", {"start": v(-16.04, -8.77) * mm, "end": v(-15.95, -8.79) * mm});
            skLineSegment(sketch, "E3425", {"start": v(-15.95, -8.79) * mm, "end": v(-15.86, -8.8) * mm});
            skLineSegment(sketch, "E3426", {"start": v(-15.86, -8.8) * mm, "end": v(-15.77, -8.8) * mm});
            skLineSegment(sketch, "E3427", {"start": v(-15.77, -8.8) * mm, "end": v(-15.68, -8.81) * mm});
            skLineSegment(sketch, "E3428", {"start": v(-15.68, -8.81) * mm, "end": v(-15.58, -8.82) * mm});
            skLineSegment(sketch, "E3429", {"start": v(-15.58, -8.82) * mm, "end": v(-15.5, -8.82) * mm});
            skLineSegment(sketch, "E3430", {"start": v(-15.5, -8.82) * mm, "end": v(-15.4, -8.83) * mm});
            skLineSegment(sketch, "E3431", {"start": v(-15.4, -8.83) * mm, "end": v(-15.3, -8.83) * mm});
            skLineSegment(sketch, "E3432", {"start": v(-15.3, -8.83) * mm, "end": v(-15.2, -8.83) * mm});
            skLineSegment(sketch, "E3433", {"start": v(-15.2, -8.83) * mm, "end": v(-15.11, -8.83) * mm});
            skLineSegment(sketch, "E3434", {"start": v(-15.11, -8.83) * mm, "end": v(-15.02, -8.83) * mm});
            skLineSegment(sketch, "E3435", {"start": v(-15.02, -8.83) * mm, "end": v(-14.92, -8.83) * mm});
            skLineSegment(sketch, "E3436", {"start": v(-14.92, -8.83) * mm, "end": v(-14.83, -8.83) * mm});
            skLineSegment(sketch, "E3437", {"start": v(-14.83, -8.83) * mm, "end": v(-14.73, -8.83) * mm});
            skLineSegment(sketch, "E3438", {"start": v(-14.73, -8.83) * mm, "end": v(-14.63, -8.82) * mm});
            skLineSegment(sketch, "E3439", {"start": v(-14.63, -8.82) * mm, "end": v(-14.54, -8.82) * mm});
            skLineSegment(sketch, "E3440", {"start": v(-14.54, -8.82) * mm, "end": v(-14.44, -8.81) * mm});
            skLineSegment(sketch, "E3441", {"start": v(-14.44, -8.81) * mm, "end": v(-14.34, -8.8) * mm});
            skLineSegment(sketch, "E3442", {"start": v(-14.34, -8.8) * mm, "end": v(-14.24, -8.8) * mm});
            skLineSegment(sketch, "E3443", {"start": v(-14.24, -8.8) * mm, "end": v(-14.14, -8.79) * mm});
            skLineSegment(sketch, "E3444", {"start": v(-14.14, -8.79) * mm, "end": v(-14.04, -8.78) * mm});
            skLineSegment(sketch, "E3445", {"start": v(-14.04, -8.78) * mm, "end": v(-13.94, -8.76) * mm});
            skLineSegment(sketch, "E3446", {"start": v(-13.94, -8.76) * mm, "end": v(-13.84, -8.75) * mm});
            skLineSegment(sketch, "E3447", {"start": v(-13.84, -8.75) * mm, "end": v(-13.73, -8.74) * mm});
            skLineSegment(sketch, "E3448", {"start": v(-13.73, -8.74) * mm, "end": v(-13.63, -8.72) * mm});
            skLineSegment(sketch, "E3449", {"start": v(-13.63, -8.72) * mm, "end": v(-13.53, -8.7) * mm});
            skLineSegment(sketch, "E3450", {"start": v(-13.53, -8.7) * mm, "end": v(-13.43, -8.69) * mm});
            skLineSegment(sketch, "E3451", {"start": v(-13.43, -8.69) * mm, "end": v(-13.32, -8.67) * mm});
            skLineSegment(sketch, "E3452", {"start": v(-13.32, -8.67) * mm, "end": v(-13.22, -8.65) * mm});
            skLineSegment(sketch, "E3453", {"start": v(-13.22, -8.65) * mm, "end": v(-13.12, -8.62) * mm});
            skLineSegment(sketch, "E3454", {"start": v(-13.12, -8.62) * mm, "end": v(-13.01, -8.6) * mm});
            skLineSegment(sketch, "E3455", {"start": v(-13.01, -8.6) * mm, "end": v(-12.91, -8.58) * mm});
            skLineSegment(sketch, "E3456", {"start": v(-12.91, -8.58) * mm, "end": v(-12.81, -8.55) * mm});
            skLineSegment(sketch, "E3457", {"start": v(-12.81, -8.55) * mm, "end": v(-12.71, -8.52) * mm});
            skLineSegment(sketch, "E3458", {"start": v(-12.71, -8.52) * mm, "end": v(-12.61, -8.5) * mm});
            skLineSegment(sketch, "E3459", {"start": v(-12.61, -8.5) * mm, "end": v(-12.52, -8.47) * mm});
            skLineSegment(sketch, "E3460", {"start": v(-12.52, -8.47) * mm, "end": v(-12.42, -8.44) * mm});
            skLineSegment(sketch, "E3461", {"start": v(-12.42, -8.44) * mm, "end": v(-12.32, -8.4) * mm});
            skLineSegment(sketch, "E3462", {"start": v(-12.32, -8.4) * mm, "end": v(-12.23, -8.37) * mm});
            skLineSegment(sketch, "E3463", {"start": v(-12.23, -8.37) * mm, "end": v(-12.13, -8.34) * mm});
            skLineSegment(sketch, "E3464", {"start": v(-12.13, -8.34) * mm, "end": v(-12.04, -8.3) * mm});
            skLineSegment(sketch, "E3465", {"start": v(-12.04, -8.3) * mm, "end": v(-11.94, -8.26) * mm});
            skLineSegment(sketch, "E3466", {"start": v(-11.94, -8.26) * mm, "end": v(-11.85, -8.23) * mm});
            skLineSegment(sketch, "E3467", {"start": v(-11.85, -8.23) * mm, "end": v(-11.76, -8.19) * mm});
            skLineSegment(sketch, "E3468", {"start": v(-11.76, -8.19) * mm, "end": v(-11.67, -8.15) * mm});
            skLineSegment(sketch, "E3469", {"start": v(-11.67, -8.15) * mm, "end": v(-11.58, -8.1) * mm});
            skLineSegment(sketch, "E3470", {"start": v(-11.58, -8.1) * mm, "end": v(-11.49, -8.06) * mm});
            skLineSegment(sketch, "E3471", {"start": v(-11.49, -8.06) * mm, "end": v(-11.4, -8.02) * mm});
            skLineSegment(sketch, "E3472", {"start": v(-11.4, -8.02) * mm, "end": v(-11.3, -7.98) * mm});
            skLineSegment(sketch, "E3473", {"start": v(-11.3, -7.98) * mm, "end": v(-11.22, -7.93) * mm});
            skLineSegment(sketch, "E3474", {"start": v(-11.22, -7.93) * mm, "end": v(-11.13, -7.89) * mm});
            skLineSegment(sketch, "E3475", {"start": v(-11.13, -7.89) * mm, "end": v(-11.05, -7.84) * mm});
            skLineSegment(sketch, "E3476", {"start": v(-11.05, -7.84) * mm, "end": v(-10.96, -7.8) * mm});
            skLineSegment(sketch, "E3477", {"start": v(-10.96, -7.8) * mm, "end": v(-10.87, -7.74) * mm});
            skLineSegment(sketch, "E3478", {"start": v(-10.87, -7.74) * mm, "end": v(-10.79, -7.7) * mm});
            skLineSegment(sketch, "E3479", {"start": v(-10.79, -7.7) * mm, "end": v(-10.7, -7.65) * mm});
            skLineSegment(sketch, "E3480", {"start": v(-10.7, -7.65) * mm, "end": v(-10.62, -7.6) * mm});
            skLineSegment(sketch, "E3481", {"start": v(-10.62, -7.6) * mm, "end": v(-10.53, -7.54) * mm});
            skLineSegment(sketch, "E3482", {"start": v(-10.53, -7.54) * mm, "end": v(-10.45, -7.5) * mm});
            skLineSegment(sketch, "E3483", {"start": v(-10.45, -7.5) * mm, "end": v(-10.36, -7.44) * mm});
            skLineSegment(sketch, "E3484", {"start": v(-10.36, -7.44) * mm, "end": v(-10.28, -7.38) * mm});
            skLineSegment(sketch, "E3485", {"start": v(-10.28, -7.38) * mm, "end": v(-10.2, -7.33) * mm});
            skLineSegment(sketch, "E3486", {"start": v(-10.2, -7.33) * mm, "end": v(-10.11, -7.28) * mm});
            skLineSegment(sketch, "E3487", {"start": v(-10.11, -7.28) * mm, "end": v(-10.03, -7.22) * mm});
            skLineSegment(sketch, "E3488", {"start": v(-10.03, -7.22) * mm, "end": v(-9.94, -7.16) * mm});
            skLineSegment(sketch, "E3489", {"start": v(-9.94, -7.16) * mm, "end": v(-9.86, -7.1) * mm});
            skLineSegment(sketch, "E3490", {"start": v(-9.86, -7.1) * mm, "end": v(-9.78, -7.05) * mm});
            skLineSegment(sketch, "E3491", {"start": v(-9.78, -7.05) * mm, "end": v(-9.7, -7) * mm});
            skLineSegment(sketch, "E3492", {"start": v(-9.7, -7) * mm, "end": v(-9.62, -6.94) * mm});
            skLineSegment(sketch, "E3493", {"start": v(-9.62, -6.94) * mm, "end": v(-9.53, -6.88) * mm});
            skLineSegment(sketch, "E3494", {"start": v(-9.53, -6.88) * mm, "end": v(-9.45, -6.82) * mm});
            skLineSegment(sketch, "E3495", {"start": v(-9.45, -6.82) * mm, "end": v(-9.37, -6.76) * mm});
            skLineSegment(sketch, "E3496", {"start": v(-9.37, -6.76) * mm, "end": v(-9.29, -6.7) * mm});
            skLineSegment(sketch, "E3497", {"start": v(-9.29, -6.7) * mm, "end": v(-9.2, -6.64) * mm});
            skLineSegment(sketch, "E3498", {"start": v(-9.2, -6.64) * mm, "end": v(-9.12, -6.58) * mm});
            skLineSegment(sketch, "E3499", {"start": v(-9.12, -6.58) * mm, "end": v(-9.04, -6.52) * mm});
            skLineSegment(sketch, "E3500", {"start": v(-9.04, -6.52) * mm, "end": v(-8.96, -6.46) * mm});
            skLineSegment(sketch, "E3501", {"start": v(-8.96, -6.46) * mm, "end": v(-8.88, -6.4) * mm});
            skLineSegment(sketch, "E3502", {"start": v(-8.88, -6.4) * mm, "end": v(-8.8, -6.33) * mm});
            skLineSegment(sketch, "E3503", {"start": v(-8.8, -6.33) * mm, "end": v(-8.71, -6.27) * mm});
            skLineSegment(sketch, "E3504", {"start": v(-8.71, -6.27) * mm, "end": v(-8.63, -6.2) * mm});
            skLineSegment(sketch, "E3505", {"start": v(-8.63, -6.2) * mm, "end": v(-8.55, -6.15) * mm});
            skLineSegment(sketch, "E3506", {"start": v(-8.55, -6.15) * mm, "end": v(-8.47, -6.08) * mm});
            skLineSegment(sketch, "E3507", {"start": v(20.57, 15.12) * mm, "end": v(20.58, 15.03) * mm});
            skLineSegment(sketch, "E3508", {"start": v(20.58, 15.03) * mm, "end": v(20.6, 14.94) * mm});
            skLineSegment(sketch, "E3509", {"start": v(20.6, 14.94) * mm, "end": v(20.6, 14.85) * mm});
            skLineSegment(sketch, "E3510", {"start": v(20.6, 14.85) * mm, "end": v(20.6, 14.75) * mm});
            skLineSegment(sketch, "E3511", {"start": v(20.6, 14.75) * mm, "end": v(20.6, 14.66) * mm});
            skLineSegment(sketch, "E3512", {"start": v(20.6, 14.66) * mm, "end": v(20.6, 14.56) * mm});
            skLineSegment(sketch, "E3513", {"start": v(20.6, 14.56) * mm, "end": v(20.6, 14.47) * mm});
            skLineSegment(sketch, "E3514", {"start": v(20.6, 14.47) * mm, "end": v(20.59, 14.37) * mm});
            skLineSegment(sketch, "E3515", {"start": v(20.59, 14.37) * mm, "end": v(20.57, 14.28) * mm});
            skLineSegment(sketch, "E3516", {"start": v(20.57, 14.28) * mm, "end": v(20.55, 14.18) * mm});
            skLineSegment(sketch, "E3517", {"start": v(20.55, 14.18) * mm, "end": v(20.53, 14.08) * mm});
            skLineSegment(sketch, "E3518", {"start": v(20.53, 14.08) * mm, "end": v(20.5, 13.99) * mm});
            skLineSegment(sketch, "E3519", {"start": v(20.5, 13.99) * mm, "end": v(20.48, 13.89) * mm});
            skLineSegment(sketch, "E3520", {"start": v(20.48, 13.89) * mm, "end": v(20.45, 13.8) * mm});
            skLineSegment(sketch, "E3521", {"start": v(20.45, 13.8) * mm, "end": v(20.42, 13.7) * mm});
            skLineSegment(sketch, "E3522", {"start": v(20.42, 13.7) * mm, "end": v(20.39, 13.6) * mm});
            skLineSegment(sketch, "E3523", {"start": v(20.39, 13.6) * mm, "end": v(20.35, 13.5) * mm});
            skLineSegment(sketch, "E3524", {"start": v(20.35, 13.5) * mm, "end": v(20.32, 13.4) * mm});
            skLineSegment(sketch, "E3525", {"start": v(20.32, 13.4) * mm, "end": v(20.28, 13.3) * mm});
            skLineSegment(sketch, "E3526", {"start": v(20.28, 13.3) * mm, "end": v(20.24, 13.21) * mm});
            skLineSegment(sketch, "E3527", {"start": v(20.24, 13.21) * mm, "end": v(20.2, 13.12) * mm});
            skLineSegment(sketch, "E3528", {"start": v(20.2, 13.12) * mm, "end": v(20.15, 13.02) * mm});
            skLineSegment(sketch, "E3529", {"start": v(20.15, 13.02) * mm, "end": v(20.1, 12.92) * mm});
            skLineSegment(sketch, "E3530", {"start": v(20.1, 12.92) * mm, "end": v(20.06, 12.83) * mm});
            skLineSegment(sketch, "E3531", {"start": v(20.06, 12.83) * mm, "end": v(20.01, 12.74) * mm});
            skLineSegment(sketch, "E3532", {"start": v(20.01, 12.74) * mm, "end": v(19.97, 12.64) * mm});
            skLineSegment(sketch, "E3533", {"start": v(19.97, 12.64) * mm, "end": v(19.92, 12.55) * mm});
            skLineSegment(sketch, "E3534", {"start": v(19.92, 12.55) * mm, "end": v(19.87, 12.46) * mm});
            skLineSegment(sketch, "E3535", {"start": v(19.87, 12.46) * mm, "end": v(19.82, 12.36) * mm});
            skLineSegment(sketch, "E3536", {"start": v(19.82, 12.36) * mm, "end": v(19.78, 12.27) * mm});
            skLineSegment(sketch, "E3537", {"start": v(19.78, 12.27) * mm, "end": v(19.73, 12.18) * mm});
            skLineSegment(sketch, "E3538", {"start": v(19.73, 12.18) * mm, "end": v(19.68, 12.1) * mm});
            skLineSegment(sketch, "E3539", {"start": v(19.68, 12.1) * mm, "end": v(19.64, 12) * mm});
            skLineSegment(sketch, "E3540", {"start": v(19.64, 12) * mm, "end": v(19.59, 11.92) * mm});
            skLineSegment(sketch, "E3541", {"start": v(19.59, 11.92) * mm, "end": v(19.54, 11.83) * mm});
            skLineSegment(sketch, "E3542", {"start": v(19.54, 11.83) * mm, "end": v(19.5, 11.75) * mm});
            skLineSegment(sketch, "E3543", {"start": v(19.5, 11.75) * mm, "end": v(19.46, 11.66) * mm});
            skLineSegment(sketch, "E3544", {"start": v(19.46, 11.66) * mm, "end": v(19.41, 11.58) * mm});
            skLineSegment(sketch, "E3545", {"start": v(19.41, 11.58) * mm, "end": v(19.37, 11.5) * mm});
            skLineSegment(sketch, "E3546", {"start": v(19.37, 11.5) * mm, "end": v(19.34, 11.42) * mm});
            skLineSegment(sketch, "E3547", {"start": v(19.34, 11.42) * mm, "end": v(19.3, 11.33) * mm});
            skLineSegment(sketch, "E3548", {"start": v(19.3, 11.33) * mm, "end": v(19.25, 11.23) * mm});
            skLineSegment(sketch, "E3549", {"start": v(19.25, 11.23) * mm, "end": v(19.2, 11.14) * mm});
            skLineSegment(sketch, "E3550", {"start": v(19.2, 11.14) * mm, "end": v(19.16, 11.05) * mm});
            skLineSegment(sketch, "E3551", {"start": v(19.16, 11.05) * mm, "end": v(19.11, 10.96) * mm});
            skLineSegment(sketch, "E3552", {"start": v(19.11, 10.96) * mm, "end": v(19.07, 10.87) * mm});
            skLineSegment(sketch, "E3553", {"start": v(19.07, 10.87) * mm, "end": v(19.02, 10.77) * mm});
            skLineSegment(sketch, "E3554", {"start": v(19.02, 10.77) * mm, "end": v(18.98, 10.68) * mm});
            skLineSegment(sketch, "E3555", {"start": v(18.98, 10.68) * mm, "end": v(18.93, 10.6) * mm});
            skLineSegment(sketch, "E3556", {"start": v(18.93, 10.6) * mm, "end": v(18.88, 10.5) * mm});
            skLineSegment(sketch, "E3557", {"start": v(18.88, 10.5) * mm, "end": v(18.84, 10.4) * mm});
            skLineSegment(sketch, "E3558", {"start": v(18.84, 10.4) * mm, "end": v(18.8, 10.32) * mm});
            skLineSegment(sketch, "E3559", {"start": v(18.8, 10.32) * mm, "end": v(18.75, 10.23) * mm});
            skLineSegment(sketch, "E3560", {"start": v(18.75, 10.23) * mm, "end": v(18.7, 10.14) * mm});
            skLineSegment(sketch, "E3561", {"start": v(18.7, 10.14) * mm, "end": v(18.65, 10.04) * mm});
            skLineSegment(sketch, "E3562", {"start": v(18.65, 10.04) * mm, "end": v(18.6, 9.95) * mm});
            skLineSegment(sketch, "E3563", {"start": v(18.6, 9.95) * mm, "end": v(18.56, 9.86) * mm});
            skLineSegment(sketch, "E3564", {"start": v(18.56, 9.86) * mm, "end": v(18.5, 9.77) * mm});
            skLineSegment(sketch, "E3565", {"start": v(18.5, 9.77) * mm, "end": v(18.46, 9.68) * mm});
            skLineSegment(sketch, "E3566", {"start": v(18.46, 9.68) * mm, "end": v(18.41, 9.6) * mm});
            skLineSegment(sketch, "E3567", {"start": v(18.41, 9.6) * mm, "end": v(18.37, 9.5) * mm});
            skLineSegment(sketch, "E3568", {"start": v(18.37, 9.5) * mm, "end": v(18.32, 9.41) * mm});
            skLineSegment(sketch, "E3569", {"start": v(18.32, 9.41) * mm, "end": v(18.27, 9.32) * mm});
            skLineSegment(sketch, "E3570", {"start": v(18.27, 9.32) * mm, "end": v(18.22, 9.23) * mm});
            skLineSegment(sketch, "E3571", {"start": v(18.22, 9.23) * mm, "end": v(18.17, 9.14) * mm});
            skLineSegment(sketch, "E3572", {"start": v(18.17, 9.14) * mm, "end": v(18.12, 9.05) * mm});
            skLineSegment(sketch, "E3573", {"start": v(18.12, 9.05) * mm, "end": v(18.07, 8.96) * mm});
            skLineSegment(sketch, "E3574", {"start": v(18.07, 8.96) * mm, "end": v(18.03, 8.87) * mm});
            skLineSegment(sketch, "E3575", {"start": v(18.03, 8.87) * mm, "end": v(17.98, 8.78) * mm});
            skLineSegment(sketch, "E3576", {"start": v(17.98, 8.78) * mm, "end": v(17.93, 8.7) * mm});
            skLineSegment(sketch, "E3577", {"start": v(17.93, 8.7) * mm, "end": v(17.88, 8.6) * mm});
            skLineSegment(sketch, "E3578", {"start": v(17.88, 8.6) * mm, "end": v(17.83, 8.51) * mm});
            skLineSegment(sketch, "E3579", {"start": v(17.83, 8.51) * mm, "end": v(17.78, 8.42) * mm});
            skLineSegment(sketch, "E3580", {"start": v(17.78, 8.42) * mm, "end": v(17.73, 8.34) * mm});
            skLineSegment(sketch, "E3581", {"start": v(17.73, 8.34) * mm, "end": v(17.68, 8.25) * mm});
            skLineSegment(sketch, "E3582", {"start": v(17.68, 8.25) * mm, "end": v(17.63, 8.16) * mm});
            skLineSegment(sketch, "E3583", {"start": v(17.63, 8.16) * mm, "end": v(17.58, 8.07) * mm});
            skLineSegment(sketch, "E3584", {"start": v(17.58, 8.07) * mm, "end": v(17.52, 7.98) * mm});
            skLineSegment(sketch, "E3585", {"start": v(17.52, 7.98) * mm, "end": v(17.47, 7.9) * mm});
            skLineSegment(sketch, "E3586", {"start": v(17.47, 7.9) * mm, "end": v(17.42, 7.8) * mm});
            skLineSegment(sketch, "E3587", {"start": v(17.42, 7.8) * mm, "end": v(17.37, 7.71) * mm});
            skLineSegment(sketch, "E3588", {"start": v(17.37, 7.71) * mm, "end": v(17.32, 7.63) * mm});
            skLineSegment(sketch, "E3589", {"start": v(17.32, 7.63) * mm, "end": v(17.27, 7.54) * mm});
            skLineSegment(sketch, "E3590", {"start": v(17.27, 7.54) * mm, "end": v(17.22, 7.45) * mm});
            skLineSegment(sketch, "E3591", {"start": v(17.22, 7.45) * mm, "end": v(17.17, 7.36) * mm});
            skLineSegment(sketch, "E3592", {"start": v(17.17, 7.36) * mm, "end": v(17.11, 7.27) * mm});
            skLineSegment(sketch, "E3593", {"start": v(17.11, 7.27) * mm, "end": v(17.06, 7.18) * mm});
            skLineSegment(sketch, "E3594", {"start": v(17.06, 7.18) * mm, "end": v(17, 7.1) * mm});
            skLineSegment(sketch, "E3595", {"start": v(17, 7.1) * mm, "end": v(16.96, 7) * mm});
            skLineSegment(sketch, "E3596", {"start": v(16.96, 7) * mm, "end": v(16.9, 6.92) * mm});
            skLineSegment(sketch, "E3597", {"start": v(16.9, 6.92) * mm, "end": v(16.85, 6.83) * mm});
            skLineSegment(sketch, "E3598", {"start": v(16.85, 6.83) * mm, "end": v(16.8, 6.75) * mm});
            skLineSegment(sketch, "E3599", {"start": v(16.8, 6.75) * mm, "end": v(16.75, 6.66) * mm});
            skLineSegment(sketch, "E3600", {"start": v(16.75, 6.66) * mm, "end": v(16.7, 6.57) * mm});
            skLineSegment(sketch, "E3601", {"start": v(16.7, 6.57) * mm, "end": v(16.64, 6.48) * mm});
            skLineSegment(sketch, "E3602", {"start": v(16.64, 6.48) * mm, "end": v(16.59, 6.4) * mm});
            skLineSegment(sketch, "E3603", {"start": v(16.59, 6.4) * mm, "end": v(16.54, 6.3) * mm});
            skLineSegment(sketch, "E3604", {"start": v(16.54, 6.3) * mm, "end": v(16.48, 6.22) * mm});
            skLineSegment(sketch, "E3605", {"start": v(16.48, 6.22) * mm, "end": v(16.43, 6.13) * mm});
            skLineSegment(sketch, "E3606", {"start": v(16.43, 6.13) * mm, "end": v(16.38, 6.05) * mm});
            skLineSegment(sketch, "E3607", {"start": v(16.38, 6.05) * mm, "end": v(16.32, 5.96) * mm});
            skLineSegment(sketch, "E3608", {"start": v(16.32, 5.96) * mm, "end": v(16.27, 5.87) * mm});
            skLineSegment(sketch, "E3609", {"start": v(16.27, 5.87) * mm, "end": v(16.22, 5.78) * mm});
            skLineSegment(sketch, "E3610", {"start": v(16.22, 5.78) * mm, "end": v(16.16, 5.7) * mm});
            skLineSegment(sketch, "E3611", {"start": v(16.16, 5.7) * mm, "end": v(16.1, 5.61) * mm});
            skLineSegment(sketch, "E3612", {"start": v(16.1, 5.61) * mm, "end": v(16.05, 5.52) * mm});
            skLineSegment(sketch, "E3613", {"start": v(16.05, 5.52) * mm, "end": v(16, 5.44) * mm});
            skLineSegment(sketch, "E3614", {"start": v(16, 5.44) * mm, "end": v(15.95, 5.35) * mm});
            skLineSegment(sketch, "E3615", {"start": v(15.95, 5.35) * mm, "end": v(15.9, 5.26) * mm});
            skLineSegment(sketch, "E3616", {"start": v(15.9, 5.26) * mm, "end": v(15.84, 5.18) * mm});
            skLineSegment(sketch, "E3617", {"start": v(15.84, 5.18) * mm, "end": v(15.78, 5.1) * mm});
            skLineSegment(sketch, "E3618", {"start": v(15.78, 5.1) * mm, "end": v(15.73, 5) * mm});
            skLineSegment(sketch, "E3619", {"start": v(15.73, 5) * mm, "end": v(15.67, 4.92) * mm});
            skLineSegment(sketch, "E3620", {"start": v(15.67, 4.92) * mm, "end": v(15.62, 4.83) * mm});
            skLineSegment(sketch, "E3621", {"start": v(15.62, 4.83) * mm, "end": v(15.56, 4.74) * mm});
            skLineSegment(sketch, "E3622", {"start": v(15.56, 4.74) * mm, "end": v(15.5, 4.66) * mm});
            skLineSegment(sketch, "E3623", {"start": v(15.5, 4.66) * mm, "end": v(15.45, 4.57) * mm});
            skLineSegment(sketch, "E3624", {"start": v(15.45, 4.57) * mm, "end": v(15.4, 4.49) * mm});
            skLineSegment(sketch, "E3625", {"start": v(15.4, 4.49) * mm, "end": v(15.34, 4.4) * mm});
            skLineSegment(sketch, "E3626", {"start": v(15.34, 4.4) * mm, "end": v(15.29, 4.31) * mm});
            skLineSegment(sketch, "E3627", {"start": v(15.29, 4.31) * mm, "end": v(15.23, 4.23) * mm});
            skLineSegment(sketch, "E3628", {"start": v(15.23, 4.23) * mm, "end": v(15.18, 4.14) * mm});
            skLineSegment(sketch, "E3629", {"start": v(15.18, 4.14) * mm, "end": v(15.12, 4.05) * mm});
            skLineSegment(sketch, "E3630", {"start": v(15.12, 4.05) * mm, "end": v(15.07, 3.97) * mm});
            skLineSegment(sketch, "E3631", {"start": v(15.07, 3.97) * mm, "end": v(15.01, 3.88) * mm});
            skLineSegment(sketch, "E3632", {"start": v(15.01, 3.88) * mm, "end": v(14.96, 3.8) * mm});
            skLineSegment(sketch, "E3633", {"start": v(14.96, 3.8) * mm, "end": v(14.9, 3.71) * mm});
            skLineSegment(sketch, "E3634", {"start": v(14.9, 3.71) * mm, "end": v(14.85, 3.62) * mm});
            skLineSegment(sketch, "E3635", {"start": v(14.85, 3.62) * mm, "end": v(14.8, 3.54) * mm});
            skLineSegment(sketch, "E3636", {"start": v(14.8, 3.54) * mm, "end": v(14.74, 3.45) * mm});
            skLineSegment(sketch, "E3637", {"start": v(14.74, 3.45) * mm, "end": v(14.68, 3.37) * mm});
            skLineSegment(sketch, "E3638", {"start": v(14.68, 3.37) * mm, "end": v(14.62, 3.28) * mm});
            skLineSegment(sketch, "E3639", {"start": v(14.62, 3.28) * mm, "end": v(14.57, 3.2) * mm});
            skLineSegment(sketch, "E3640", {"start": v(14.57, 3.2) * mm, "end": v(14.51, 3.1) * mm});
            skLineSegment(sketch, "E3641", {"start": v(14.51, 3.1) * mm, "end": v(14.46, 3.02) * mm});
            skLineSegment(sketch, "E3642", {"start": v(14.46, 3.02) * mm, "end": v(14.4, 2.94) * mm});
            skLineSegment(sketch, "E3643", {"start": v(14.4, 2.94) * mm, "end": v(14.34, 2.85) * mm});
            skLineSegment(sketch, "E3644", {"start": v(14.34, 2.85) * mm, "end": v(14.29, 2.77) * mm});
            skLineSegment(sketch, "E3645", {"start": v(14.29, 2.77) * mm, "end": v(14.23, 2.68) * mm});
            skLineSegment(sketch, "E3646", {"start": v(14.23, 2.68) * mm, "end": v(14.18, 2.6) * mm});
            skLineSegment(sketch, "E3647", {"start": v(14.18, 2.6) * mm, "end": v(14.12, 2.51) * mm});
            skLineSegment(sketch, "E3648", {"start": v(14.12, 2.51) * mm, "end": v(14.07, 2.42) * mm});
            skLineSegment(sketch, "E3649", {"start": v(14.07, 2.42) * mm, "end": v(14.04, 2.5) * mm});
            skLineSegment(sketch, "E3650", {"start": v(14.04, 2.5) * mm, "end": v(14.03, 2.6) * mm});
            skLineSegment(sketch, "E3651", {"start": v(14.03, 2.6) * mm, "end": v(14.02, 2.68) * mm});
            skLineSegment(sketch, "E3652", {"start": v(14.02, 2.68) * mm, "end": v(14, 2.77) * mm});
            skLineSegment(sketch, "E3653", {"start": v(14, 2.77) * mm, "end": v(14, 2.87) * mm});
            skLineSegment(sketch, "E3654", {"start": v(14, 2.87) * mm, "end": v(14, 2.96) * mm});
            skLineSegment(sketch, "E3655", {"start": v(14, 2.96) * mm, "end": v(14, 3.06) * mm});
            skLineSegment(sketch, "E3656", {"start": v(14, 3.06) * mm, "end": v(14.01, 3.16) * mm});
            skLineSegment(sketch, "E3657", {"start": v(14.01, 3.16) * mm, "end": v(14.02, 3.26) * mm});
            skLineSegment(sketch, "E3658", {"start": v(14.02, 3.26) * mm, "end": v(14.03, 3.36) * mm});
            skLineSegment(sketch, "E3659", {"start": v(14.03, 3.36) * mm, "end": v(14.05, 3.46) * mm});
            skLineSegment(sketch, "E3660", {"start": v(14.05, 3.46) * mm, "end": v(14.06, 3.56) * mm});
            skLineSegment(sketch, "E3661", {"start": v(14.06, 3.56) * mm, "end": v(14.08, 3.66) * mm});
            skLineSegment(sketch, "E3662", {"start": v(14.08, 3.66) * mm, "end": v(14.1, 3.77) * mm});
            skLineSegment(sketch, "E3663", {"start": v(14.1, 3.77) * mm, "end": v(14.13, 3.87) * mm});
            skLineSegment(sketch, "E3664", {"start": v(14.13, 3.87) * mm, "end": v(14.15, 3.98) * mm});
            skLineSegment(sketch, "E3665", {"start": v(14.15, 3.98) * mm, "end": v(14.18, 4.08) * mm});
            skLineSegment(sketch, "E3666", {"start": v(14.18, 4.08) * mm, "end": v(14.21, 4.19) * mm});
            skLineSegment(sketch, "E3667", {"start": v(14.21, 4.19) * mm, "end": v(14.24, 4.3) * mm});
            skLineSegment(sketch, "E3668", {"start": v(14.24, 4.3) * mm, "end": v(14.27, 4.4) * mm});
            skLineSegment(sketch, "E3669", {"start": v(14.27, 4.4) * mm, "end": v(14.3, 4.5) * mm});
            skLineSegment(sketch, "E3670", {"start": v(14.3, 4.5) * mm, "end": v(14.34, 4.6) * mm});
            skLineSegment(sketch, "E3671", {"start": v(14.34, 4.6) * mm, "end": v(14.37, 4.7) * mm});
            skLineSegment(sketch, "E3672", {"start": v(14.37, 4.7) * mm, "end": v(14.4, 4.8) * mm});
            skLineSegment(sketch, "E3673", {"start": v(14.4, 4.8) * mm, "end": v(14.44, 4.9) * mm});
            skLineSegment(sketch, "E3674", {"start": v(14.44, 4.9) * mm, "end": v(14.47, 5) * mm});
            skLineSegment(sketch, "E3675", {"start": v(14.47, 5) * mm, "end": v(14.5, 5.1) * mm});
            skLineSegment(sketch, "E3676", {"start": v(14.5, 5.1) * mm, "end": v(14.54, 5.2) * mm});
            skLineSegment(sketch, "E3677", {"start": v(14.54, 5.2) * mm, "end": v(14.57, 5.3) * mm});
            skLineSegment(sketch, "E3678", {"start": v(14.57, 5.3) * mm, "end": v(14.6, 5.38) * mm});
            skLineSegment(sketch, "E3679", {"start": v(14.6, 5.38) * mm, "end": v(14.64, 5.47) * mm});
            skLineSegment(sketch, "E3680", {"start": v(14.64, 5.47) * mm, "end": v(14.67, 5.56) * mm});
            skLineSegment(sketch, "E3681", {"start": v(14.67, 5.56) * mm, "end": v(14.7, 5.65) * mm});
            skLineSegment(sketch, "E3682", {"start": v(14.7, 5.65) * mm, "end": v(14.73, 5.73) * mm});
            skLineSegment(sketch, "E3683", {"start": v(14.73, 5.73) * mm, "end": v(14.75, 5.81) * mm});
            skLineSegment(sketch, "E3684", {"start": v(14.75, 5.81) * mm, "end": v(14.78, 5.9) * mm});
            skLineSegment(sketch, "E3685", {"start": v(14.78, 5.9) * mm, "end": v(14.8, 5.98) * mm});
            skLineSegment(sketch, "E3686", {"start": v(14.8, 5.98) * mm, "end": v(14.84, 6.06) * mm});
            skLineSegment(sketch, "E3687", {"start": v(14.84, 6.06) * mm, "end": v(14.86, 6.15) * mm});
            skLineSegment(sketch, "E3688", {"start": v(14.86, 6.15) * mm, "end": v(14.9, 6.23) * mm});
            skLineSegment(sketch, "E3689", {"start": v(14.9, 6.23) * mm, "end": v(14.92, 6.32) * mm});
            skLineSegment(sketch, "E3690", {"start": v(14.92, 6.32) * mm, "end": v(14.95, 6.4) * mm});
            skLineSegment(sketch, "E3691", {"start": v(14.95, 6.4) * mm, "end": v(14.98, 6.5) * mm});
            skLineSegment(sketch, "E3692", {"start": v(14.98, 6.5) * mm, "end": v(15.01, 6.58) * mm});
            skLineSegment(sketch, "E3693", {"start": v(15.01, 6.58) * mm, "end": v(15.04, 6.67) * mm});
            skLineSegment(sketch, "E3694", {"start": v(15.04, 6.67) * mm, "end": v(15.08, 6.76) * mm});
            skLineSegment(sketch, "E3695", {"start": v(15.08, 6.76) * mm, "end": v(15.1, 6.84) * mm});
            skLineSegment(sketch, "E3696", {"start": v(15.1, 6.84) * mm, "end": v(15.14, 6.93) * mm});
            skLineSegment(sketch, "E3697", {"start": v(15.14, 6.93) * mm, "end": v(15.17, 7.02) * mm});
            skLineSegment(sketch, "E3698", {"start": v(15.17, 7.02) * mm, "end": v(15.2, 7.11) * mm});
            skLineSegment(sketch, "E3699", {"start": v(15.2, 7.11) * mm, "end": v(15.24, 7.2) * mm});
            skLineSegment(sketch, "E3700", {"start": v(15.24, 7.2) * mm, "end": v(15.27, 7.3) * mm});
            skLineSegment(sketch, "E3701", {"start": v(15.27, 7.3) * mm, "end": v(15.3, 7.39) * mm});
            skLineSegment(sketch, "E3702", {"start": v(15.3, 7.39) * mm, "end": v(15.34, 7.48) * mm});
            skLineSegment(sketch, "E3703", {"start": v(15.34, 7.48) * mm, "end": v(15.38, 7.57) * mm});
            skLineSegment(sketch, "E3704", {"start": v(15.38, 7.57) * mm, "end": v(15.42, 7.67) * mm});
            skLineSegment(sketch, "E3705", {"start": v(15.42, 7.67) * mm, "end": v(15.45, 7.76) * mm});
            skLineSegment(sketch, "E3706", {"start": v(15.45, 7.76) * mm, "end": v(15.49, 7.85) * mm});
            skLineSegment(sketch, "E3707", {"start": v(15.49, 7.85) * mm, "end": v(15.53, 7.95) * mm});
            skLineSegment(sketch, "E3708", {"start": v(15.53, 7.95) * mm, "end": v(15.56, 8.04) * mm});
            skLineSegment(sketch, "E3709", {"start": v(15.56, 8.04) * mm, "end": v(15.6, 8.13) * mm});
            skLineSegment(sketch, "E3710", {"start": v(15.6, 8.13) * mm, "end": v(15.64, 8.23) * mm});
            skLineSegment(sketch, "E3711", {"start": v(15.64, 8.23) * mm, "end": v(15.68, 8.32) * mm});
            skLineSegment(sketch, "E3712", {"start": v(15.68, 8.32) * mm, "end": v(15.72, 8.42) * mm});
            skLineSegment(sketch, "E3713", {"start": v(15.72, 8.42) * mm, "end": v(15.76, 8.51) * mm});
            skLineSegment(sketch, "E3714", {"start": v(15.76, 8.51) * mm, "end": v(15.8, 8.6) * mm});
            skLineSegment(sketch, "E3715", {"start": v(15.8, 8.6) * mm, "end": v(15.84, 8.7) * mm});
            skLineSegment(sketch, "E3716", {"start": v(15.84, 8.7) * mm, "end": v(15.88, 8.8) * mm});
            skLineSegment(sketch, "E3717", {"start": v(15.88, 8.8) * mm, "end": v(15.92, 8.9) * mm});
            skLineSegment(sketch, "E3718", {"start": v(15.92, 8.9) * mm, "end": v(15.96, 8.99) * mm});
            skLineSegment(sketch, "E3719", {"start": v(15.96, 8.99) * mm, "end": v(16, 9.08) * mm});
            skLineSegment(sketch, "E3720", {"start": v(16, 9.08) * mm, "end": v(16.05, 9.18) * mm});
            skLineSegment(sketch, "E3721", {"start": v(16.05, 9.18) * mm, "end": v(16.1, 9.27) * mm});
            skLineSegment(sketch, "E3722", {"start": v(16.1, 9.27) * mm, "end": v(16.14, 9.37) * mm});
            skLineSegment(sketch, "E3723", {"start": v(16.14, 9.37) * mm, "end": v(16.18, 9.46) * mm});
            skLineSegment(sketch, "E3724", {"start": v(16.18, 9.46) * mm, "end": v(16.23, 9.56) * mm});
            skLineSegment(sketch, "E3725", {"start": v(16.23, 9.56) * mm, "end": v(16.27, 9.65) * mm});
            skLineSegment(sketch, "E3726", {"start": v(16.27, 9.65) * mm, "end": v(16.32, 9.75) * mm});
            skLineSegment(sketch, "E3727", {"start": v(16.32, 9.75) * mm, "end": v(16.36, 9.84) * mm});
            skLineSegment(sketch, "E3728", {"start": v(16.36, 9.84) * mm, "end": v(16.4, 9.94) * mm});
            skLineSegment(sketch, "E3729", {"start": v(16.4, 9.94) * mm, "end": v(16.46, 10.03) * mm});
            skLineSegment(sketch, "E3730", {"start": v(16.46, 10.03) * mm, "end": v(16.5, 10.13) * mm});
            skLineSegment(sketch, "E3731", {"start": v(16.5, 10.13) * mm, "end": v(16.55, 10.22) * mm});
            skLineSegment(sketch, "E3732", {"start": v(16.55, 10.22) * mm, "end": v(16.6, 10.32) * mm});
            skLineSegment(sketch, "E3733", {"start": v(16.6, 10.32) * mm, "end": v(16.65, 10.41) * mm});
            skLineSegment(sketch, "E3734", {"start": v(16.65, 10.41) * mm, "end": v(16.7, 10.5) * mm});
            skLineSegment(sketch, "E3735", {"start": v(16.7, 10.5) * mm, "end": v(16.75, 10.6) * mm});
            skLineSegment(sketch, "E3736", {"start": v(16.75, 10.6) * mm, "end": v(16.8, 10.7) * mm});
            skLineSegment(sketch, "E3737", {"start": v(16.8, 10.7) * mm, "end": v(16.85, 10.79) * mm});
            skLineSegment(sketch, "E3738", {"start": v(16.85, 10.79) * mm, "end": v(16.9, 10.88) * mm});
            skLineSegment(sketch, "E3739", {"start": v(16.9, 10.88) * mm, "end": v(16.95, 10.97) * mm});
            skLineSegment(sketch, "E3740", {"start": v(16.95, 10.97) * mm, "end": v(17, 11.07) * mm});
            skLineSegment(sketch, "E3741", {"start": v(17, 11.07) * mm, "end": v(17.06, 11.16) * mm});
            skLineSegment(sketch, "E3742", {"start": v(17.06, 11.16) * mm, "end": v(17.1, 11.25) * mm});
            skLineSegment(sketch, "E3743", {"start": v(17.1, 11.25) * mm, "end": v(17.16, 11.34) * mm});
            skLineSegment(sketch, "E3744", {"start": v(17.16, 11.34) * mm, "end": v(17.21, 11.43) * mm});
            skLineSegment(sketch, "E3745", {"start": v(17.21, 11.43) * mm, "end": v(17.27, 11.52) * mm});
            skLineSegment(sketch, "E3746", {"start": v(17.27, 11.52) * mm, "end": v(17.32, 11.61) * mm});
            skLineSegment(sketch, "E3747", {"start": v(17.32, 11.61) * mm, "end": v(17.38, 11.7) * mm});
            skLineSegment(sketch, "E3748", {"start": v(17.38, 11.7) * mm, "end": v(17.43, 11.8) * mm});
            skLineSegment(sketch, "E3749", {"start": v(17.43, 11.8) * mm, "end": v(17.5, 11.88) * mm});
            skLineSegment(sketch, "E3750", {"start": v(17.5, 11.88) * mm, "end": v(17.55, 11.97) * mm});
            skLineSegment(sketch, "E3751", {"start": v(17.55, 11.97) * mm, "end": v(17.6, 12.05) * mm});
            skLineSegment(sketch, "E3752", {"start": v(17.6, 12.05) * mm, "end": v(17.66, 12.14) * mm});
            skLineSegment(sketch, "E3753", {"start": v(17.66, 12.14) * mm, "end": v(17.72, 12.23) * mm});
            skLineSegment(sketch, "E3754", {"start": v(17.72, 12.23) * mm, "end": v(17.78, 12.31) * mm});
            skLineSegment(sketch, "E3755", {"start": v(17.78, 12.31) * mm, "end": v(17.84, 12.4) * mm});
            skLineSegment(sketch, "E3756", {"start": v(17.84, 12.4) * mm, "end": v(17.9, 12.48) * mm});
            skLineSegment(sketch, "E3757", {"start": v(17.9, 12.48) * mm, "end": v(17.95, 12.57) * mm});
            skLineSegment(sketch, "E3758", {"start": v(17.95, 12.57) * mm, "end": v(18.01, 12.65) * mm});
            skLineSegment(sketch, "E3759", {"start": v(18.01, 12.65) * mm, "end": v(18.08, 12.73) * mm});
            skLineSegment(sketch, "E3760", {"start": v(18.08, 12.73) * mm, "end": v(18.14, 12.82) * mm});
            skLineSegment(sketch, "E3761", {"start": v(18.14, 12.82) * mm, "end": v(18.2, 12.9) * mm});
            skLineSegment(sketch, "E3762", {"start": v(18.2, 12.9) * mm, "end": v(18.26, 12.98) * mm});
            skLineSegment(sketch, "E3763", {"start": v(18.26, 12.98) * mm, "end": v(18.32, 13.06) * mm});
            skLineSegment(sketch, "E3764", {"start": v(18.32, 13.06) * mm, "end": v(18.39, 13.14) * mm});
            skLineSegment(sketch, "E3765", {"start": v(18.39, 13.14) * mm, "end": v(18.45, 13.22) * mm});
            skLineSegment(sketch, "E3766", {"start": v(18.45, 13.22) * mm, "end": v(18.51, 13.3) * mm});
            skLineSegment(sketch, "E3767", {"start": v(18.51, 13.3) * mm, "end": v(18.58, 13.37) * mm});
            skLineSegment(sketch, "E3768", {"start": v(18.58, 13.37) * mm, "end": v(18.64, 13.45) * mm});
            skLineSegment(sketch, "E3769", {"start": v(18.64, 13.45) * mm, "end": v(18.7, 13.52) * mm});
            skLineSegment(sketch, "E3770", {"start": v(18.7, 13.52) * mm, "end": v(18.77, 13.6) * mm});
            skLineSegment(sketch, "E3771", {"start": v(18.77, 13.6) * mm, "end": v(18.84, 13.67) * mm});
            skLineSegment(sketch, "E3772", {"start": v(18.84, 13.67) * mm, "end": v(18.9, 13.74) * mm});
            skLineSegment(sketch, "E3773", {"start": v(18.9, 13.74) * mm, "end": v(18.97, 13.81) * mm});
            skLineSegment(sketch, "E3774", {"start": v(18.97, 13.81) * mm, "end": v(19.04, 13.88) * mm});
            skLineSegment(sketch, "E3775", {"start": v(19.04, 13.88) * mm, "end": v(19.1, 13.95) * mm});
            skLineSegment(sketch, "E3776", {"start": v(19.1, 13.95) * mm, "end": v(19.18, 14.02) * mm});
            skLineSegment(sketch, "E3777", {"start": v(19.18, 14.02) * mm, "end": v(19.25, 14.1) * mm});
            skLineSegment(sketch, "E3778", {"start": v(19.25, 14.1) * mm, "end": v(19.31, 14.16) * mm});
            skLineSegment(sketch, "E3779", {"start": v(19.31, 14.16) * mm, "end": v(19.38, 14.22) * mm});
            skLineSegment(sketch, "E3780", {"start": v(19.38, 14.22) * mm, "end": v(19.45, 14.29) * mm});
            skLineSegment(sketch, "E3781", {"start": v(19.45, 14.29) * mm, "end": v(19.53, 14.35) * mm});
            skLineSegment(sketch, "E3782", {"start": v(19.53, 14.35) * mm, "end": v(19.6, 14.41) * mm});
            skLineSegment(sketch, "E3783", {"start": v(19.6, 14.41) * mm, "end": v(19.67, 14.48) * mm});
            skLineSegment(sketch, "E3784", {"start": v(19.67, 14.48) * mm, "end": v(19.74, 14.54) * mm});
            skLineSegment(sketch, "E3785", {"start": v(19.74, 14.54) * mm, "end": v(19.81, 14.6) * mm});
            skLineSegment(sketch, "E3786", {"start": v(19.81, 14.6) * mm, "end": v(19.89, 14.65) * mm});
            skLineSegment(sketch, "E3787", {"start": v(19.89, 14.65) * mm, "end": v(19.96, 14.71) * mm});
            skLineSegment(sketch, "E3788", {"start": v(19.96, 14.71) * mm, "end": v(20.04, 14.77) * mm});
            skLineSegment(sketch, "E3789", {"start": v(20.04, 14.77) * mm, "end": v(20.1, 14.82) * mm});
            skLineSegment(sketch, "E3790", {"start": v(20.1, 14.82) * mm, "end": v(20.19, 14.87) * mm});
            skLineSegment(sketch, "E3791", {"start": v(20.19, 14.87) * mm, "end": v(20.26, 14.93) * mm});
            skLineSegment(sketch, "E3792", {"start": v(20.26, 14.93) * mm, "end": v(20.34, 14.98) * mm});
            skLineSegment(sketch, "E3793", {"start": v(20.34, 14.98) * mm, "end": v(20.41, 15.03) * mm});
            skLineSegment(sketch, "E3794", {"start": v(20.41, 15.03) * mm, "end": v(20.5, 15.08) * mm});
            skLineSegment(sketch, "E3795", {"start": v(20.5, 15.08) * mm, "end": v(20.57, 15.12) * mm});
            skLineSegment(sketch, "E3796", {"start": v(0.86, 3.45) * mm, "end": v(0.94, 3.46) * mm});
            skLineSegment(sketch, "E3797", {"start": v(0.94, 3.46) * mm, "end": v(1.03, 3.47) * mm});
            skLineSegment(sketch, "E3798", {"start": v(1.03, 3.47) * mm, "end": v(1.12, 3.48) * mm});
            skLineSegment(sketch, "E3799", {"start": v(1.12, 3.48) * mm, "end": v(1.2, 3.48) * mm});
            skLineSegment(sketch, "E3800", {"start": v(1.2, 3.48) * mm, "end": v(1.3, 3.47) * mm});
            skLineSegment(sketch, "E3801", {"start": v(1.3, 3.47) * mm, "end": v(1.39, 3.46) * mm});
            skLineSegment(sketch, "E3802", {"start": v(1.39, 3.46) * mm, "end": v(1.47, 3.45) * mm});
            skLineSegment(sketch, "E3803", {"start": v(1.47, 3.45) * mm, "end": v(1.56, 3.43) * mm});
            skLineSegment(sketch, "E3804", {"start": v(1.56, 3.43) * mm, "end": v(1.64, 3.4) * mm});
            skLineSegment(sketch, "E3805", {"start": v(1.64, 3.4) * mm, "end": v(1.72, 3.36) * mm});
            skLineSegment(sketch, "E3806", {"start": v(1.72, 3.36) * mm, "end": v(1.8, 3.32) * mm});
            skLineSegment(sketch, "E3807", {"start": v(1.8, 3.32) * mm, "end": v(1.86, 3.27) * mm});
            skLineSegment(sketch, "E3808", {"start": v(1.86, 3.27) * mm, "end": v(1.91, 3.21) * mm});
            skLineSegment(sketch, "E3809", {"start": v(1.91, 3.21) * mm, "end": v(1.96, 3.15) * mm});
            skLineSegment(sketch, "E3810", {"start": v(1.96, 3.15) * mm, "end": v(2, 3.08) * mm});
            skLineSegment(sketch, "E3811", {"start": v(2, 3.08) * mm, "end": v(2.03, 3) * mm});
            skLineSegment(sketch, "E3812", {"start": v(2.03, 3) * mm, "end": v(2.05, 2.9) * mm});
            skLineSegment(sketch, "E3813", {"start": v(2.05, 2.9) * mm, "end": v(2.05, 2.8) * mm});
            skLineSegment(sketch, "E3814", {"start": v(2.05, 2.8) * mm, "end": v(2.04, 2.71) * mm});
            skLineSegment(sketch, "E3815", {"start": v(2.04, 2.71) * mm, "end": v(2.03, 2.62) * mm});
            skLineSegment(sketch, "E3816", {"start": v(2.03, 2.62) * mm, "end": v(2.02, 2.53) * mm});
            skLineSegment(sketch, "E3817", {"start": v(2.02, 2.53) * mm, "end": v(2, 2.43) * mm});
            skLineSegment(sketch, "E3818", {"start": v(2, 2.43) * mm, "end": v(1.97, 2.34) * mm});
            skLineSegment(sketch, "E3819", {"start": v(1.97, 2.34) * mm, "end": v(1.94, 2.24) * mm});
            skLineSegment(sketch, "E3820", {"start": v(1.94, 2.24) * mm, "end": v(1.9, 2.14) * mm});
            skLineSegment(sketch, "E3821", {"start": v(1.9, 2.14) * mm, "end": v(1.87, 2.05) * mm});
            skLineSegment(sketch, "E3822", {"start": v(1.87, 2.05) * mm, "end": v(1.83, 1.95) * mm});
            skLineSegment(sketch, "E3823", {"start": v(1.83, 1.95) * mm, "end": v(1.78, 1.85) * mm});
            skLineSegment(sketch, "E3824", {"start": v(1.78, 1.85) * mm, "end": v(1.74, 1.76) * mm});
            skLineSegment(sketch, "E3825", {"start": v(1.74, 1.76) * mm, "end": v(1.7, 1.66) * mm});
            skLineSegment(sketch, "E3826", {"start": v(1.7, 1.66) * mm, "end": v(1.65, 1.57) * mm});
            skLineSegment(sketch, "E3827", {"start": v(1.65, 1.57) * mm, "end": v(1.6, 1.47) * mm});
            skLineSegment(sketch, "E3828", {"start": v(1.6, 1.47) * mm, "end": v(1.56, 1.38) * mm});
            skLineSegment(sketch, "E3829", {"start": v(1.56, 1.38) * mm, "end": v(1.51, 1.29) * mm});
            skLineSegment(sketch, "E3830", {"start": v(1.51, 1.29) * mm, "end": v(1.47, 1.2) * mm});
            skLineSegment(sketch, "E3831", {"start": v(1.47, 1.2) * mm, "end": v(1.42, 1.1) * mm});
            skLineSegment(sketch, "E3832", {"start": v(1.42, 1.1) * mm, "end": v(1.38, 1.02) * mm});
            skLineSegment(sketch, "E3833", {"start": v(1.38, 1.02) * mm, "end": v(1.34, 0.93) * mm});
            skLineSegment(sketch, "E3834", {"start": v(1.34, 0.93) * mm, "end": v(1.3, 0.85) * mm});
            skLineSegment(sketch, "E3835", {"start": v(1.3, 0.85) * mm, "end": v(1.28, 0.79) * mm});
            skLineSegment(sketch, "E3836", {"start": v(1.28, 0.79) * mm, "end": v(1.25, 0.72) * mm});
            skLineSegment(sketch, "E3837", {"start": v(1.25, 0.72) * mm, "end": v(1.23, 0.65) * mm});
            skLineSegment(sketch, "E3838", {"start": v(1.23, 0.65) * mm, "end": v(1.2, 0.58) * mm});
            skLineSegment(sketch, "E3839", {"start": v(1.2, 0.58) * mm, "end": v(1.17, 0.5) * mm});
            skLineSegment(sketch, "E3840", {"start": v(1.17, 0.5) * mm, "end": v(1.14, 0.43) * mm});
            skLineSegment(sketch, "E3841", {"start": v(1.14, 0.43) * mm, "end": v(1.12, 0.36) * mm});
            skLineSegment(sketch, "E3842", {"start": v(1.12, 0.36) * mm, "end": v(1.09, 0.28) * mm});
            skLineSegment(sketch, "E3843", {"start": v(1.09, 0.28) * mm, "end": v(1.06, 0.2) * mm});
            skLineSegment(sketch, "E3844", {"start": v(1.06, 0.2) * mm, "end": v(1.03, 0.11) * mm});
            skLineSegment(sketch, "E3845", {"start": v(1.03, 0.11) * mm, "end": v(1, 0.03) * mm});
            skLineSegment(sketch, "E3846", {"start": v(1, 0.03) * mm, "end": v(0.97, -0.06) * mm});
            skLineSegment(sketch, "E3847", {"start": v(0.97, -0.06) * mm, "end": v(0.95, -0.14) * mm});
            skLineSegment(sketch, "E3848", {"start": v(0.95, -0.14) * mm, "end": v(0.92, -0.23) * mm});
            skLineSegment(sketch, "E3849", {"start": v(0.92, -0.23) * mm, "end": v(0.89, -0.32) * mm});
            skLineSegment(sketch, "E3850", {"start": v(0.89, -0.32) * mm, "end": v(0.86, -0.41) * mm});
            skLineSegment(sketch, "E3851", {"start": v(0.86, -0.41) * mm, "end": v(0.82, -0.5) * mm});
            skLineSegment(sketch, "E3852", {"start": v(0.82, -0.5) * mm, "end": v(0.8, -0.6) * mm});
            skLineSegment(sketch, "E3853", {"start": v(0.8, -0.6) * mm, "end": v(0.76, -0.7) * mm});
            skLineSegment(sketch, "E3854", {"start": v(0.76, -0.7) * mm, "end": v(0.73, -0.8) * mm});
            skLineSegment(sketch, "E3855", {"start": v(0.73, -0.8) * mm, "end": v(0.7, -0.89) * mm});
            skLineSegment(sketch, "E3856", {"start": v(0.7, -0.89) * mm, "end": v(0.67, -0.99) * mm});
            skLineSegment(sketch, "E3857", {"start": v(0.67, -0.99) * mm, "end": v(0.63, -1.08) * mm});
            skLineSegment(sketch, "E3858", {"start": v(0.63, -1.08) * mm, "end": v(0.6, -1.18) * mm});
            skLineSegment(sketch, "E3859", {"start": v(0.6, -1.18) * mm, "end": v(0.56, -1.28) * mm});
            skLineSegment(sketch, "E3860", {"start": v(0.56, -1.28) * mm, "end": v(0.53, -1.38) * mm});
            skLineSegment(sketch, "E3861", {"start": v(0.53, -1.38) * mm, "end": v(0.5, -1.48) * mm});
            skLineSegment(sketch, "E3862", {"start": v(0.5, -1.48) * mm, "end": v(0.46, -1.58) * mm});
            skLineSegment(sketch, "E3863", {"start": v(0.46, -1.58) * mm, "end": v(0.42, -1.68) * mm});
            skLineSegment(sketch, "E3864", {"start": v(0.42, -1.68) * mm, "end": v(0.39, -1.78) * mm});
            skLineSegment(sketch, "E3865", {"start": v(0.39, -1.78) * mm, "end": v(0.35, -1.89) * mm});
            skLineSegment(sketch, "E3866", {"start": v(0.35, -1.89) * mm, "end": v(0.3, -1.99) * mm});
            skLineSegment(sketch, "E3867", {"start": v(0.3, -1.99) * mm, "end": v(0.27, -2.09) * mm});
            skLineSegment(sketch, "E3868", {"start": v(0.27, -2.09) * mm, "end": v(0.23, -2.19) * mm});
            skLineSegment(sketch, "E3869", {"start": v(0.23, -2.19) * mm, "end": v(0.2, -2.29) * mm});
            skLineSegment(sketch, "E3870", {"start": v(0.2, -2.29) * mm, "end": v(0.15, -2.39) * mm});
            skLineSegment(sketch, "E3871", {"start": v(0.15, -2.39) * mm, "end": v(0.11, -2.49) * mm});
            skLineSegment(sketch, "E3872", {"start": v(0.11, -2.49) * mm, "end": v(0.07, -2.59) * mm});
            skLineSegment(sketch, "E3873", {"start": v(0.07, -2.59) * mm, "end": v(0.03, -2.68) * mm});
            skLineSegment(sketch, "E3874", {"start": v(0.03, -2.68) * mm, "end": v(-0.02, -2.78) * mm});
            skLineSegment(sketch, "E3875", {"start": v(-0.02, -2.78) * mm, "end": v(-0.06, -2.88) * mm});
            skLineSegment(sketch, "E3876", {"start": v(-0.06, -2.88) * mm, "end": v(-0.1, -2.97) * mm});
            skLineSegment(sketch, "E3877", {"start": v(-0.1, -2.97) * mm, "end": v(-0.15, -3.07) * mm});
            skLineSegment(sketch, "E3878", {"start": v(-0.15, -3.07) * mm, "end": v(-0.2, -3.16) * mm});
            skLineSegment(sketch, "E3879", {"start": v(-0.2, -3.16) * mm, "end": v(-0.24, -3.25) * mm});
            skLineSegment(sketch, "E3880", {"start": v(-0.24, -3.25) * mm, "end": v(-0.3, -3.35) * mm});
            skLineSegment(sketch, "E3881", {"start": v(-0.3, -3.35) * mm, "end": v(-0.34, -3.44) * mm});
            skLineSegment(sketch, "E3882", {"start": v(-0.34, -3.44) * mm, "end": v(-0.39, -3.52) * mm});
            skLineSegment(sketch, "E3883", {"start": v(-0.39, -3.52) * mm, "end": v(-0.44, -3.61) * mm});
            skLineSegment(sketch, "E3884", {"start": v(-0.44, -3.61) * mm, "end": v(-0.49, -3.7) * mm});
            skLineSegment(sketch, "E3885", {"start": v(-0.49, -3.7) * mm, "end": v(-0.54, -3.78) * mm});
            skLineSegment(sketch, "E3886", {"start": v(-0.54, -3.78) * mm, "end": v(-0.6, -3.86) * mm});
            skLineSegment(sketch, "E3887", {"start": v(-0.6, -3.86) * mm, "end": v(-0.65, -3.94) * mm});
            skLineSegment(sketch, "E3888", {"start": v(-0.65, -3.94) * mm, "end": v(-0.7, -4.02) * mm});
            skLineSegment(sketch, "E3889", {"start": v(-0.7, -4.02) * mm, "end": v(-0.76, -4.1) * mm});
            skLineSegment(sketch, "E3890", {"start": v(-0.76, -4.1) * mm, "end": v(-0.81, -4.17) * mm});
            skLineSegment(sketch, "E3891", {"start": v(-0.81, -4.17) * mm, "end": v(-0.87, -4.25) * mm});
            skLineSegment(sketch, "E3892", {"start": v(-0.87, -4.25) * mm, "end": v(-0.93, -4.32) * mm});
            skLineSegment(sketch, "E3893", {"start": v(-0.93, -4.32) * mm, "end": v(-0.99, -4.39) * mm});
            skLineSegment(sketch, "E3894", {"start": v(-0.99, -4.39) * mm, "end": v(-1.05, -4.45) * mm});
            skLineSegment(sketch, "E3895", {"start": v(-1.05, -4.45) * mm, "end": v(-1.1, -4.51) * mm});
            skLineSegment(sketch, "E3896", {"start": v(-1.1, -4.51) * mm, "end": v(-1.17, -4.58) * mm});
            skLineSegment(sketch, "E3897", {"start": v(-1.17, -4.58) * mm, "end": v(-1.23, -4.63) * mm});
            skLineSegment(sketch, "E3898", {"start": v(-1.23, -4.63) * mm, "end": v(-1.3, -4.69) * mm});
            skLineSegment(sketch, "E3899", {"start": v(-1.3, -4.69) * mm, "end": v(-1.36, -4.74) * mm});
            skLineSegment(sketch, "E3900", {"start": v(-1.36, -4.74) * mm, "end": v(-1.43, -4.8) * mm});
            skLineSegment(sketch, "E3901", {"start": v(-1.43, -4.8) * mm, "end": v(-1.5, -4.84) * mm});
            skLineSegment(sketch, "E3902", {"start": v(-1.5, -4.84) * mm, "end": v(-1.56, -4.88) * mm});
            skLineSegment(sketch, "E3903", {"start": v(-1.56, -4.88) * mm, "end": v(-1.63, -4.92) * mm});
            skLineSegment(sketch, "E3904", {"start": v(-1.63, -4.92) * mm, "end": v(-1.7, -4.96) * mm});
            skLineSegment(sketch, "E3905", {"start": v(-1.7, -4.96) * mm, "end": v(-1.77, -5) * mm});
            skLineSegment(sketch, "E3906", {"start": v(-1.77, -5) * mm, "end": v(-1.84, -5.02) * mm});
            skLineSegment(sketch, "E3907", {"start": v(-1.84, -5.02) * mm, "end": v(-1.92, -5.05) * mm});
            skLineSegment(sketch, "E3908", {"start": v(-1.92, -5.05) * mm, "end": v(-2, -5.07) * mm});
            skLineSegment(sketch, "E3909", {"start": v(-2, -5.07) * mm, "end": v(-2.07, -5.1) * mm});
            skLineSegment(sketch, "E3910", {"start": v(-2.07, -5.1) * mm, "end": v(-2.15, -5.11) * mm});
            skLineSegment(sketch, "E3911", {"start": v(-2.15, -5.11) * mm, "end": v(-2.25, -5.13) * mm});
            skLineSegment(sketch, "E3912", {"start": v(-2.25, -5.13) * mm, "end": v(-2.35, -5.14) * mm});
            skLineSegment(sketch, "E3913", {"start": v(-2.35, -5.14) * mm, "end": v(-2.45, -5.14) * mm});
            skLineSegment(sketch, "E3914", {"start": v(-2.45, -5.14) * mm, "end": v(-2.54, -5.14) * mm});
            skLineSegment(sketch, "E3915", {"start": v(-2.54, -5.14) * mm, "end": v(-2.62, -5.13) * mm});
            skLineSegment(sketch, "E3916", {"start": v(-2.62, -5.13) * mm, "end": v(-2.7, -5.12) * mm});
            skLineSegment(sketch, "E3917", {"start": v(-2.7, -5.12) * mm, "end": v(-2.78, -5.1) * mm});
            skLineSegment(sketch, "E3918", {"start": v(-2.78, -5.1) * mm, "end": v(-2.85, -5.07) * mm});
            skLineSegment(sketch, "E3919", {"start": v(-2.85, -5.07) * mm, "end": v(-2.91, -5.04) * mm});
            skLineSegment(sketch, "E3920", {"start": v(-2.91, -5.04) * mm, "end": v(-2.97, -5) * mm});
            skLineSegment(sketch, "E3921", {"start": v(-2.97, -5) * mm, "end": v(-3.03, -4.97) * mm});
            skLineSegment(sketch, "E3922", {"start": v(-3.03, -4.97) * mm, "end": v(-3.08, -4.92) * mm});
            skLineSegment(sketch, "E3923", {"start": v(-3.08, -4.92) * mm, "end": v(-3.13, -4.87) * mm});
            skLineSegment(sketch, "E3924", {"start": v(-3.13, -4.87) * mm, "end": v(-3.18, -4.82) * mm});
            skLineSegment(sketch, "E3925", {"start": v(-3.18, -4.82) * mm, "end": v(-3.22, -4.76) * mm});
            skLineSegment(sketch, "E3926", {"start": v(-3.22, -4.76) * mm, "end": v(-3.25, -4.7) * mm});
            skLineSegment(sketch, "E3927", {"start": v(-3.25, -4.7) * mm, "end": v(-3.29, -4.64) * mm});
            skLineSegment(sketch, "E3928", {"start": v(-3.29, -4.64) * mm, "end": v(-3.32, -4.58) * mm});
            skLineSegment(sketch, "E3929", {"start": v(-3.32, -4.58) * mm, "end": v(-3.34, -4.5) * mm});
            skLineSegment(sketch, "E3930", {"start": v(-3.34, -4.5) * mm, "end": v(-3.37, -4.43) * mm});
            skLineSegment(sketch, "E3931", {"start": v(-3.37, -4.43) * mm, "end": v(-3.39, -4.36) * mm});
            skLineSegment(sketch, "E3932", {"start": v(-3.39, -4.36) * mm, "end": v(-3.4, -4.28) * mm});
            skLineSegment(sketch, "E3933", {"start": v(-3.4, -4.28) * mm, "end": v(-3.42, -4.2) * mm});
            skLineSegment(sketch, "E3934", {"start": v(-3.42, -4.2) * mm, "end": v(-3.43, -4.13) * mm});
            skLineSegment(sketch, "E3935", {"start": v(-3.43, -4.13) * mm, "end": v(-3.44, -4.05) * mm});
            skLineSegment(sketch, "E3936", {"start": v(-3.44, -4.05) * mm, "end": v(-3.45, -3.96) * mm});
            skLineSegment(sketch, "E3937", {"start": v(-3.45, -3.96) * mm, "end": v(-3.45, -3.88) * mm});
            skLineSegment(sketch, "E3938", {"start": v(-3.45, -3.88) * mm, "end": v(-3.46, -3.8) * mm});
            skLineSegment(sketch, "E3939", {"start": v(-3.46, -3.8) * mm, "end": v(-3.46, -3.7) * mm});
            skLineSegment(sketch, "E3940", {"start": v(-3.46, -3.7) * mm, "end": v(-3.45, -3.62) * mm});
            skLineSegment(sketch, "E3941", {"start": v(-3.45, -3.62) * mm, "end": v(-3.45, -3.54) * mm});
            skLineSegment(sketch, "E3942", {"start": v(-3.45, -3.54) * mm, "end": v(-3.44, -3.45) * mm});
            skLineSegment(sketch, "E3943", {"start": v(-3.44, -3.45) * mm, "end": v(-3.44, -3.37) * mm});
            skLineSegment(sketch, "E3944", {"start": v(-3.44, -3.37) * mm, "end": v(-3.43, -3.28) * mm});
            skLineSegment(sketch, "E3945", {"start": v(-3.43, -3.28) * mm, "end": v(-3.42, -3.2) * mm});
            skLineSegment(sketch, "E3946", {"start": v(-3.42, -3.2) * mm, "end": v(-3.4, -3.11) * mm});
            skLineSegment(sketch, "E3947", {"start": v(-3.4, -3.11) * mm, "end": v(-3.4, -3.03) * mm});
            skLineSegment(sketch, "E3948", {"start": v(-3.4, -3.03) * mm, "end": v(-3.38, -2.95) * mm});
            skLineSegment(sketch, "E3949", {"start": v(-3.38, -2.95) * mm, "end": v(-3.37, -2.87) * mm});
            skLineSegment(sketch, "E3950", {"start": v(-3.37, -2.87) * mm, "end": v(-3.35, -2.8) * mm});
            skLineSegment(sketch, "E3951", {"start": v(-3.35, -2.8) * mm, "end": v(-3.34, -2.72) * mm});
            skLineSegment(sketch, "E3952", {"start": v(-3.34, -2.72) * mm, "end": v(-3.32, -2.65) * mm});
            skLineSegment(sketch, "E3953", {"start": v(-3.32, -2.65) * mm, "end": v(-3.3, -2.58) * mm});
            skLineSegment(sketch, "E3954", {"start": v(-3.3, -2.58) * mm, "end": v(-3.29, -2.5) * mm});
            skLineSegment(sketch, "E3955", {"start": v(-3.29, -2.5) * mm, "end": v(-3.27, -2.43) * mm});
            skLineSegment(sketch, "E3956", {"start": v(-3.27, -2.43) * mm, "end": v(-3.25, -2.36) * mm});
            skLineSegment(sketch, "E3957", {"start": v(-3.25, -2.36) * mm, "end": v(-3.23, -2.28) * mm});
            skLineSegment(sketch, "E3958", {"start": v(-3.23, -2.28) * mm, "end": v(-3.2, -2.2) * mm});
            skLineSegment(sketch, "E3959", {"start": v(-3.2, -2.2) * mm, "end": v(-3.18, -2.12) * mm});
            skLineSegment(sketch, "E3960", {"start": v(-3.18, -2.12) * mm, "end": v(-3.16, -2.03) * mm});
            skLineSegment(sketch, "E3961", {"start": v(-3.16, -2.03) * mm, "end": v(-3.14, -1.95) * mm});
            skLineSegment(sketch, "E3962", {"start": v(-3.14, -1.95) * mm, "end": v(-3.11, -1.86) * mm});
            skLineSegment(sketch, "E3963", {"start": v(-3.11, -1.86) * mm, "end": v(-3.09, -1.78) * mm});
            skLineSegment(sketch, "E3964", {"start": v(-3.09, -1.78) * mm, "end": v(-3.06, -1.7) * mm});
            skLineSegment(sketch, "E3965", {"start": v(-3.06, -1.7) * mm, "end": v(-3.03, -1.6) * mm});
            skLineSegment(sketch, "E3966", {"start": v(-3.03, -1.6) * mm, "end": v(-3, -1.52) * mm});
            skLineSegment(sketch, "E3967", {"start": v(-3, -1.52) * mm, "end": v(-2.97, -1.43) * mm});
            skLineSegment(sketch, "E3968", {"start": v(-2.97, -1.43) * mm, "end": v(-2.94, -1.34) * mm});
            skLineSegment(sketch, "E3969", {"start": v(-2.94, -1.34) * mm, "end": v(-2.91, -1.25) * mm});
            skLineSegment(sketch, "E3970", {"start": v(-2.91, -1.25) * mm, "end": v(-2.88, -1.16) * mm});
            skLineSegment(sketch, "E3971", {"start": v(-2.88, -1.16) * mm, "end": v(-2.85, -1.06) * mm});
            skLineSegment(sketch, "E3972", {"start": v(-2.85, -1.06) * mm, "end": v(-2.81, -0.97) * mm});
            skLineSegment(sketch, "E3973", {"start": v(-2.81, -0.97) * mm, "end": v(-2.78, -0.88) * mm});
            skLineSegment(sketch, "E3974", {"start": v(-2.78, -0.88) * mm, "end": v(-2.74, -0.78) * mm});
            skLineSegment(sketch, "E3975", {"start": v(-2.74, -0.78) * mm, "end": v(-2.7, -0.7) * mm});
            skLineSegment(sketch, "E3976", {"start": v(-2.7, -0.7) * mm, "end": v(-2.67, -0.6) * mm});
            skLineSegment(sketch, "E3977", {"start": v(-2.67, -0.6) * mm, "end": v(-2.63, -0.5) * mm});
            skLineSegment(sketch, "E3978", {"start": v(-2.63, -0.5) * mm, "end": v(-2.6, -0.4) * mm});
            skLineSegment(sketch, "E3979", {"start": v(-2.6, -0.4) * mm, "end": v(-2.55, -0.31) * mm});
            skLineSegment(sketch, "E3980", {"start": v(-2.55, -0.31) * mm, "end": v(-2.51, -0.22) * mm});
            skLineSegment(sketch, "E3981", {"start": v(-2.51, -0.22) * mm, "end": v(-2.47, -0.13) * mm});
            skLineSegment(sketch, "E3982", {"start": v(-2.47, -0.13) * mm, "end": v(-2.43, -0.03) * mm});
            skLineSegment(sketch, "E3983", {"start": v(-2.43, -0.03) * mm, "end": v(-2.39, 0.06) * mm});
            skLineSegment(sketch, "E3984", {"start": v(-2.39, 0.06) * mm, "end": v(-2.34, 0.16) * mm});
            skLineSegment(sketch, "E3985", {"start": v(-2.34, 0.16) * mm, "end": v(-2.3, 0.25) * mm});
            skLineSegment(sketch, "E3986", {"start": v(-2.3, 0.25) * mm, "end": v(-2.25, 0.35) * mm});
            skLineSegment(sketch, "E3987", {"start": v(-2.25, 0.35) * mm, "end": v(-2.2, 0.44) * mm});
            skLineSegment(sketch, "E3988", {"start": v(-2.2, 0.44) * mm, "end": v(-2.16, 0.53) * mm});
            skLineSegment(sketch, "E3989", {"start": v(-2.16, 0.53) * mm, "end": v(-2.1, 0.63) * mm});
            skLineSegment(sketch, "E3990", {"start": v(-2.1, 0.63) * mm, "end": v(-2.06, 0.72) * mm});
            skLineSegment(sketch, "E3991", {"start": v(-2.06, 0.72) * mm, "end": v(-2.01, 0.8) * mm});
            skLineSegment(sketch, "E3992", {"start": v(-2.01, 0.8) * mm, "end": v(-1.96, 0.9) * mm});
            skLineSegment(sketch, "E3993", {"start": v(-1.96, 0.9) * mm, "end": v(-1.9, 1) * mm});
            skLineSegment(sketch, "E3994", {"start": v(-1.9, 1) * mm, "end": v(-1.86, 1.08) * mm});
            skLineSegment(sketch, "E3995", {"start": v(-1.86, 1.08) * mm, "end": v(-1.8, 1.17) * mm});
            skLineSegment(sketch, "E3996", {"start": v(-1.8, 1.17) * mm, "end": v(-1.75, 1.26) * mm});
            skLineSegment(sketch, "E3997", {"start": v(-1.75, 1.26) * mm, "end": v(-1.7, 1.35) * mm});
            skLineSegment(sketch, "E3998", {"start": v(-1.7, 1.35) * mm, "end": v(-1.64, 1.43) * mm});
            skLineSegment(sketch, "E3999", {"start": v(-1.64, 1.43) * mm, "end": v(-1.58, 1.52) * mm});
            skLineSegment(sketch, "E4000", {"start": v(-1.58, 1.52) * mm, "end": v(-1.52, 1.6) * mm});
            skLineSegment(sketch, "E4001", {"start": v(-1.52, 1.6) * mm, "end": v(-1.46, 1.69) * mm});
            skLineSegment(sketch, "E4002", {"start": v(-1.46, 1.69) * mm, "end": v(-1.4, 1.77) * mm});
            skLineSegment(sketch, "E4003", {"start": v(-1.4, 1.77) * mm, "end": v(-1.35, 1.85) * mm});
            skLineSegment(sketch, "E4004", {"start": v(-1.35, 1.85) * mm, "end": v(-1.28, 1.93) * mm});
            skLineSegment(sketch, "E4005", {"start": v(-1.28, 1.93) * mm, "end": v(-1.22, 2) * mm});
            skLineSegment(sketch, "E4006", {"start": v(-1.22, 2) * mm, "end": v(-1.16, 2.08) * mm});
            skLineSegment(sketch, "E4007", {"start": v(-1.16, 2.08) * mm, "end": v(-1.1, 2.16) * mm});
            skLineSegment(sketch, "E4008", {"start": v(-1.1, 2.16) * mm, "end": v(-1.03, 2.23) * mm});
            skLineSegment(sketch, "E4009", {"start": v(-1.03, 2.23) * mm, "end": v(-0.97, 2.3) * mm});
            skLineSegment(sketch, "E4010", {"start": v(-0.97, 2.3) * mm, "end": v(-0.9, 2.38) * mm});
            skLineSegment(sketch, "E4011", {"start": v(-0.9, 2.38) * mm, "end": v(-0.83, 2.45) * mm});
            skLineSegment(sketch, "E4012", {"start": v(-0.83, 2.45) * mm, "end": v(-0.77, 2.52) * mm});
            skLineSegment(sketch, "E4013", {"start": v(-0.77, 2.52) * mm, "end": v(-0.7, 2.58) * mm});
            skLineSegment(sketch, "E4014", {"start": v(-0.7, 2.58) * mm, "end": v(-0.63, 2.65) * mm});
            skLineSegment(sketch, "E4015", {"start": v(-0.63, 2.65) * mm, "end": v(-0.56, 2.7) * mm});
            skLineSegment(sketch, "E4016", {"start": v(-0.56, 2.7) * mm, "end": v(-0.49, 2.77) * mm});
            skLineSegment(sketch, "E4017", {"start": v(-0.49, 2.77) * mm, "end": v(-0.41, 2.83) * mm});
            skLineSegment(sketch, "E4018", {"start": v(-0.41, 2.83) * mm, "end": v(-0.34, 2.88) * mm});
            skLineSegment(sketch, "E4019", {"start": v(-0.34, 2.88) * mm, "end": v(-0.27, 2.94) * mm});
            skLineSegment(sketch, "E4020", {"start": v(-0.27, 2.94) * mm, "end": v(-0.2, 2.99) * mm});
            skLineSegment(sketch, "E4021", {"start": v(-0.2, 2.99) * mm, "end": v(-0.12, 3.04) * mm});
            skLineSegment(sketch, "E4022", {"start": v(-0.12, 3.04) * mm, "end": v(-0.04, 3.09) * mm});
            skLineSegment(sketch, "E4023", {"start": v(-0.04, 3.09) * mm, "end": v(0.04, 3.13) * mm});
            skLineSegment(sketch, "E4024", {"start": v(0.04, 3.13) * mm, "end": v(0.12, 3.18) * mm});
            skLineSegment(sketch, "E4025", {"start": v(0.12, 3.18) * mm, "end": v(0.2, 3.22) * mm});
            skLineSegment(sketch, "E4026", {"start": v(0.2, 3.22) * mm, "end": v(0.28, 3.25) * mm});
            skLineSegment(sketch, "E4027", {"start": v(0.28, 3.25) * mm, "end": v(0.36, 3.3) * mm});
            skLineSegment(sketch, "E4028", {"start": v(0.36, 3.3) * mm, "end": v(0.44, 3.32) * mm});
            skLineSegment(sketch, "E4029", {"start": v(0.44, 3.32) * mm, "end": v(0.52, 3.35) * mm});
            skLineSegment(sketch, "E4030", {"start": v(0.52, 3.35) * mm, "end": v(0.6, 3.38) * mm});
            skLineSegment(sketch, "E4031", {"start": v(0.6, 3.38) * mm, "end": v(0.69, 3.4) * mm});
            skLineSegment(sketch, "E4032", {"start": v(0.69, 3.4) * mm, "end": v(0.77, 3.43) * mm});
            skLineSegment(sketch, "E4033", {"start": v(0.77, 3.43) * mm, "end": v(0.86, 3.45) * mm});
            skSolve(sketch);
        }
        {
            var Q0;
            Q0 = qSketchRegion(id + "F0", true);
            extrude(context, id + "F1", {"entities" : qUnion([Q0]), "depth" : 3 * mm, "offsetDistance" : 25 * mm});
        }
    });
